FCSTD DOCUMENT  (FreeCAD 0.19R20415 (Git))
Label: Vostok_Amphibia_Bezel
License: All rights reserved
LicenseURL: http://en.wikipedia.org/wiki/All_rights_reserved
objects: Sketcher::SketchObject×46, Part::FeaturePython×33, Part::Extrusion×25, Part::Cut×24, Part::Revolution×19, Part::Part2DObjectPython×9, Part::MultiFuse×7, Part::Fillet×6, Part::Cylinder×3, Part::MultiCommon×2, App::DocumentObjectGroup×2, Part::Offset2D×1, Image::ImagePlane×1, Part::Mirroring×1
note: 176 computed .brp shape members not serialized (recipe doc carries the construction recipe); baked Part::Feature solids carry a one-line shape summary decoded from their .brp

FEATURE [Sketcher::SketchObject] Sketch043
  MapMode = 5
  Placement = pos=(0,0,0) rot=(1,0,0;1.5708rad)
  sketch-geometry (12):
    g0: LineSegment StartX=15.6 StartY=2.6 StartZ=0 EndX=15.6 EndY=3.6 EndZ=0
    g1: LineSegment StartX=15.6 StartY=3.6 StartZ=0 EndX=19 EndY=3 EndZ=0
    g2: LineSegment StartX=19 StartY=3 StartZ=0 EndX=19 EndY=1 EndZ=0
    g3: LineSegment StartX=19 StartY=1 StartZ=0 EndX=17.75 EndY=1 EndZ=0
    g4: LineSegment StartX=17.75 StartY=1 StartZ=0 EndX=17.75 EndY=0 EndZ=0
    g5: LineSegment StartX=17.75 StartY=0 StartZ=0 EndX=16.75 EndY=0 EndZ=0
    g6: LineSegment StartX=16.75 StartY=2.6 StartZ=0 EndX=15.6 EndY=2.6 EndZ=0
    g7: LineSegment StartX=16.75 StartY=0 StartZ=0 EndX=16.75 EndY=0.5 EndZ=0
    g8: LineSegment StartX=16.75 StartY=0.5 StartZ=0 EndX=17.05 EndY=0.5 EndZ=0
    g9: LineSegment StartX=17.05 StartY=0.5 StartZ=0 EndX=17.05 EndY=0.75 EndZ=0
    g10: LineSegment StartX=17.05 StartY=0.75 StartZ=0 EndX=16.75 EndY=0.75 EndZ=0
    g11: LineSegment StartX=16.75 StartY=0.75 StartZ=0 EndX=16.75 EndY=2.6 EndZ=0
  constraints (37):
    c: Vertical(g0)
    c: Coincident(g0,g1)
    c: Coincident(g1,g2)
    c: Coincident(g2,g3)
    c: Coincident(g3,g4)
    c: Vertical(g4)
    c: Coincident(g4,g5)
    c: Horizontal(g6)
    c: Vertical(g2)
    c: Horizontal(g5)
    c: Coincident(g6,g0)
    c: Coincident(g5,g7)
    c: Vertical(g7)
    c: Coincident(g7,g8)
    c: Horizontal(g8)
    c: Coincident(g8,g9)
    c: Coincident(g9,g10)
    c: Coincident(g10,g11)
    c: Coincident(g11,g6)
    c: Vertical(g11)
    c: Vertical(g9)
    c: Horizontal(g10)
    c: Vertical(g10,g7)
    c: PointOnObject(g4,g-1)
    c: DistanceX(g1) = 19
    c: DistanceY(g7,g7) = 0.5
    c: DistanceY(g9,g9) = 0.25
    c: DistanceX(g10,g10) = 0.3
    c: DistanceX(g0) = 15.6
    c: DistanceX(g5,g5) = 1
    c: DistanceX(g10) = 16.75
    c: DistanceY(g0) = 3.6
    c: DistanceY(g0,g0) = 1
    c: DistanceY(g1) = 3
    c: Angle(g0,g1) = 1.39612
    c: DistanceY(g4,g4) = 1
    c: DistanceY(g2,g2) = 2
FEATURE [Part::Revolution] Revolve
  Angle = 15
  Axis = (0,0,1)
  Base = (0,0,0)
  FaceMakerClass = Part::FaceMakerBullseye
  Solid = true
  Source = -> Sketch043
  Symmetric = false
FEATURE [Sketcher::SketchObject] Sketch044
  sketch-geometry (57):
    g0: Circle [constr] CenterX=0 CenterY=0 CenterZ=0 NormalX=0 NormalY=0 NormalZ=1 AngleXU=0 Radius=19
    g1: LineSegment [constr] StartX=0 StartY=0 StartZ=0 EndX=18.9989 EndY=0.207254 EndZ=0
    g2: LineSegment StartX=18.9989 StartY=0.207254 StartZ=0 EndX=18.9497 EndY=0.206718 EndZ=0
    g3: LineSegment StartX=18.9497 StartY=0.206718 StartZ=0 EndX=18.9497 EndY=0 EndZ=0
    g4: LineSegment StartX=18.9497 StartY=0 StartZ=0 EndX=19 EndY=0 EndZ=0
    g5: LineSegment StartX=19 StartY=0 StartZ=0 EndX=19.1989 EndY=0 EndZ=0
    g6: LineSegment StartX=19.1989 StartY=0 StartZ=0 EndX=19.1989 EndY=0.209435 EndZ=0
    g7: LineSegment StartX=19.1989 StartY=0.209435 StartZ=0 EndX=18.9989 EndY=0.207254 EndZ=0
    g8: LineSegment [constr] StartX=18.9497 StartY=0.103359 StartZ=0 EndX=18.9997 EndY=0.103631 EndZ=0
    g9: LineSegment [constr] StartX=0 StartY=0 StartZ=0 EndX=18.9898 EndY=0.621663 EndZ=0
    g10: LineSegment [constr] StartX=0 StartY=0 StartZ=0 EndX=18.9717 EndY=1.03578 EndZ=0
    g11: LineSegment StartX=18.9272 StartY=1.03334 StartZ=0 EndX=18.9407 EndY=0.620054 EndZ=0
    g12: LineSegment StartX=19.1895 StartY=0.632565 StartZ=0 EndX=18.9898 EndY=0.621663 EndZ=0
    g13: LineSegment StartX=18.9898 StartY=0.621663 StartZ=0 EndX=18.9407 EndY=0.620054 EndZ=0
    g14: LineSegment StartX=18.9272 StartY=1.03334 StartZ=0 EndX=18.9717 EndY=1.03578 EndZ=0
    g15: LineSegment StartX=18.9717 StartY=1.03578 StartZ=0 EndX=19.1669 EndY=1.04643 EndZ=0
    g16: LineSegment StartX=19.1669 StartY=1.04643 StartZ=0 EndX=19.1895 EndY=0.632565 EndZ=0
    g17: LineSegment [constr] StartX=0 StartY=0 StartZ=0 EndX=18.3526 EndY=4.91756 EndZ=0
    g18: LineSegment [constr] StartX=0 StartY=0 StartZ=0 EndX=18.4051 EndY=4.71708 EndZ=0
    g19: LineSegment [constr] StartX=18.5037 StartY=4.31445 StartZ=0 EndX=0 EndY=0 EndZ=0
    g20: LineSegment [constr] StartX=0 StartY=0 StartZ=0 EndX=18.5934 EndY=3.90977 EndZ=0
    g21: LineSegment [constr] StartX=0 StartY=0 StartZ=0 EndX=18.9085 EndY=1.86233 EndZ=0
    g22: LineSegment [constr] StartX=0 StartY=0 StartZ=0 EndX=18.9446 EndY=1.4494 EndZ=0
    g23: LineSegment [constr] StartX=0 StartY=0 StartZ=0 EndX=18.6742 EndY=3.50322 EndZ=0
    g24: LineSegment [constr] StartX=18.7462 StartY=3.09501 StartZ=0 EndX=0 EndY=0 EndZ=0
    g25: LineSegment [constr] StartX=18.8093 StartY=2.68533 StartZ=0 EndX=0 EndY=0 EndZ=0
    g26: LineSegment [constr] StartX=18.8634 StartY=2.27437 StartZ=0 EndX=0 EndY=0 EndZ=0
    g27: LineSegment StartX=18.6304 StartY=3.49499 StartZ=0 EndX=18.6977 EndY=3.08701 EndZ=0
    g28: LineSegment StartX=18.9472 StartY=3.13272 StartZ=0 EndX=18.7462 EndY=3.09501 EndZ=0
    g29: LineSegment StartX=18.7462 StartY=3.09501 StartZ=0 EndX=18.6977 EndY=3.08701 EndZ=0
    g30: LineSegment StartX=18.6304 StartY=3.49499 StartZ=0 EndX=18.6742 EndY=3.50322 EndZ=0
    g31: LineSegment StartX=18.6742 StartY=3.50322 StartZ=0 EndX=18.8708 EndY=3.5401 EndZ=0
    g32: LineSegment StartX=18.8708 StartY=3.5401 StartZ=0 EndX=18.9472 EndY=3.13272 EndZ=0
    g33: LineSegment StartX=18.4602 StartY=4.30431 StartZ=0 EndX=18.5453 EndY=3.89965 EndZ=0
    g34: LineSegment StartX=18.7926 StartY=3.95621 StartZ=0 EndX=18.5934 EndY=3.90977 EndZ=0
    g35: LineSegment StartX=18.5934 StartY=3.90977 StartZ=0 EndX=18.5453 EndY=3.89965 EndZ=0
    g36: LineSegment StartX=18.4602 StartY=4.30431 StartZ=0 EndX=18.5037 EndY=4.31445 EndZ=0
    g37: LineSegment StartX=18.5037 StartY=4.31445 StartZ=0 EndX=18.6984 EndY=4.35986 EndZ=0
    g38: LineSegment StartX=18.6984 StartY=4.35986 StartZ=0 EndX=18.7926 EndY=3.95621 EndZ=0
    g39: LineSegment StartX=18.3106 StartY=4.9063 StartZ=0 EndX=18.3619 EndY=4.70599 EndZ=0
    g40: LineSegment StartX=18.5994 StartY=4.76913 StartZ=0 EndX=18.4051 EndY=4.71708 EndZ=0
    g41: LineSegment StartX=18.4051 StartY=4.71708 StartZ=0 EndX=18.3619 EndY=4.70599 EndZ=0
    g42: LineSegment StartX=18.3106 StartY=4.9063 StartZ=0 EndX=18.3526 EndY=4.91756 EndZ=0
    g43: LineSegment StartX=18.3526 StartY=4.91756 StartZ=0 EndX=18.5458 EndY=4.96933 EndZ=0
    g44: LineSegment StartX=18.5458 StartY=4.96933 StartZ=0 EndX=18.5994 EndY=4.76913 EndZ=0
    g45: LineSegment StartX=18.9001 StartY=1.44599 StartZ=0 EndX=18.9446 EndY=1.4494 EndZ=0
    g46: LineSegment StartX=18.9446 StartY=1.4494 StartZ=0 EndX=19.1395 EndY=1.46431 EndZ=0
    g47: LineSegment StartX=19.1395 StartY=1.46431 StartZ=0 EndX=19.0985 EndY=1.88104 EndZ=0
    g48: LineSegment StartX=19.0985 StartY=1.88104 StartZ=0 EndX=18.9085 EndY=1.86233 EndZ=0
    g49: LineSegment StartX=18.9085 StartY=1.86233 StartZ=0 EndX=18.8596 EndY=1.85751 EndZ=0
    g50: LineSegment StartX=18.8596 StartY=1.85751 StartZ=0 EndX=18.9001 EndY=1.44599 EndZ=0
    g51: LineSegment StartX=18.7562 StartY=2.67775 StartZ=0 EndX=18.8093 EndY=2.68533 EndZ=0
    g52: LineSegment StartX=18.8093 StartY=2.68533 StartZ=0 EndX=19.0028 EndY=2.71296 EndZ=0
    g53: LineSegment StartX=19.0028 StartY=2.71296 StartZ=0 EndX=19.0529 EndY=2.29722 EndZ=0
    g54: LineSegment StartX=19.0529 StartY=2.29722 StartZ=0 EndX=18.8634 EndY=2.27437 EndZ=0
    g55: LineSegment StartX=18.8634 StartY=2.27437 StartZ=0 EndX=18.8146 EndY=2.26849 EndZ=0
    g56: LineSegment StartX=18.8146 StartY=2.26849 StartZ=0 EndX=18.7562 EndY=2.67775 EndZ=0
  constraints (158):
    c: Coincident(g0,g-1)
    c: Radius(g0) = 19
    c: Coincident(g1,g-1)
    c: PointOnObject(g1,g0)
    c: Angle(g1) = 0.0109083
    c: Coincident(g1,g2)
    c: Coincident(g2,g3)
    c: PointOnObject(g3,g-1)
    c: Coincident(g3,g4)
    c: PointOnObject(g4,g0)
    c: Coincident(g4,g5)
    c: Coincident(g5,g6)
    c: Coincident(g6,g7)
    c: Coincident(g7,g2)
    c: PointOnObject(g2,g1)
    c: Parallel(g2,g7)
    c: Distance(g2,g6) = 0.2
    c: PointOnObject(g4,g-1)
    c: Parallel(g4,g5)
    c: Perpendicular(g6,g5)
    c: Perpendicular(g3,g4)
    c: PointOnObject(g8,g0)
    c: Perpendicular(g0,g8)
    c: Symmetric(g2,g3,g8)
    c: Distance(g8) = 0.05
    c: Coincident(g9,g-1)
    c: PointOnObject(g9,g0)
    c: Coincident(g10,g-1)
    c: PointOnObject(g10,g0)
    c: Angle(g1,g9) = 0.0218166
    c: Angle(g9,g10) = 0.0218166
    c: PointOnObject(g11,g10)
    c: PointOnObject(g11,g9)
    c: Coincident(g12,g13)
    c: Coincident(g13,g11)
    c: Coincident(g11,g14)
    c: Coincident(g14,g15)
    c: Coincident(g15,g16)
    c: Coincident(g16,g12)
    c: Coincident(g10,g14)
    c: Coincident(g12,g9)
    c: Perpendicular(g16,g12)
    c: Perpendicular(g16,g15)
    c: Parallel(g14,g15)
    c: Equal(g12,g7)
    c: Perpendicular(g13,g11)
    c: Equal(g13,g2)
    c: Coincident(g17,g-1)
    c: PointOnObject(g17,g0)
    c: Coincident(g18,g-1)
    c: PointOnObject(g18,g0)
    c: PointOnObject(g19,g0)
    c: Coincident(g19,g-1)
    c: Coincident(g20,g-1)
    c: PointOnObject(g20,g0)
    c: Coincident(g21,g-1)
    c: PointOnObject(g21,g0)
    c: Coincident(g22,g-1)
    c: PointOnObject(g22,g0)
    c: Angle(g10,g22) = 0.0218166
    c: Angle(g22,g21) = 0.0218166
    c: Angle(g18,g17) = 0.0109083
    c: Angle(g19,g18) = 0.0218166
    c: Angle(g20,g19) = 0.0218166
    c: Coincident(g23,g-1)
    c: PointOnObject(g23,g0)
    c: PointOnObject(g24,g0)
    c: Coincident(g24,g-1)
    c: PointOnObject(g25,g0)
    c: Coincident(g25,g-1)
    c: Angle(g23,g20) = 0.0218166
    c: Angle(g24,g23) = 0.0218166
    c: Angle(g25,g24) = 0.0218166
    c: PointOnObject(g26,g0)
    c: Coincident(g26,g-1)
    c: Angle(g26,g25) = 0.0218166
    c: Coincident(g28,g29)
    c: Coincident(g29,g27)
    c: Coincident(g27,g30)
    c: Coincident(g30,g31)
    c: Coincident(g31,g32)
    c: Coincident(g32,g28)
    c: Perpendicular(g32,g28)
    c: Perpendicular(g32,g31)
    c: Parallel(g30,g31)
    c: Perpendicular(g29,g27)
    c: Coincident(g34,g35)
    c: Coincident(g35,g33)
    c: Coincident(g33,g36)
    c: Coincident(g36,g37)
    c: Coincident(g37,g38)
    c: Coincident(g38,g34)
    c: Perpendicular(g38,g34)
    c: Perpendicular(g38,g37)
    c: Parallel(g36,g37)
    c: Perpendicular(g35,g33)
    c: Coincident(g40,g41)
    c: Coincident(g41,g39)
    c: Coincident(g39,g42)
    c: Coincident(g42,g43)
    c: Coincident(g43,g44)
    c: Coincident(g44,g40)
    c: Perpendicular(g44,g40)
    c: Perpendicular(g44,g43)
    c: Parallel(g42,g43)
    c: Perpendicular(g41,g39)
    c: Angle(g21,g26) = 0.0218166
    c: Coincident(g30,g23)
    c: Coincident(g28,g24)
    c: PointOnObject(g27,g24)
    c: PointOnObject(g27,g23)
    c: PointOnObject(g33,g20)
    c: Coincident(g36,g19)
    c: Coincident(g34,g20)
    c: Equal(g37,g31)
    c: PointOnObject(g33,g19)
    c: Coincident(g42,g17)
    c: Coincident(g18,g40)
    c: PointOnObject(g39,g18)
    c: Equal(g43,g37)
    c: Equal(g36,g41)
    c: PointOnObject(g39,g17)
    c: Equal(g30,g14)
    c: Equal(g37,g31)
    c: Equal(g36,g30)
    c: Equal(g37,g7)
    c: PointOnObject(g45,g22)
    c: Coincident(g45,g22)
    c: Coincident(g45,g46)
    c: Coincident(g46,g47)
    c: Coincident(g47,g48)
    c: Coincident(g48,g21)
    c: Coincident(g48,g49)
    c: PointOnObject(g49,g21)
    c: Coincident(g49,g50)
    c: Coincident(g50,g45)
    c: Equal(g45,g14)
    c: Equal(g46,g15)
    c: Perpendicular(g49,g50)
    c: Parallel(g46,g45)
    c: Parallel(g48,g49)
    c: Perpendicular(g47,g48)
    c: PointOnObject(g51,g25)
    c: Coincident(g51,g25)
    c: Coincident(g51,g52)
    c: Coincident(g52,g53)
    c: Coincident(g53,g54)
    c: Coincident(g54,g26)
    c: Coincident(g54,g55)
    c: PointOnObject(g55,g26)
    c: Coincident(g55,g56)
    c: Coincident(g56,g51)
    c: Equal(g55,g49)
    c: Equal(g48,g54)
    c: Parallel(g51,g52)
    c: Parallel(g55,g54)
    c: Perpendicular(g53,g54)
    c: Perpendicular(g56,g51)
FEATURE [Sketcher::SketchObject] Sketch
  ExternalGeometry = -> [Revolve]
  MapMode = 6
  Placement = pos=(15.6,8e-16,3.6) rot=(0.086895,0.086895,0.992421;1.57841rad)
  Support = -> [Revolve]
  sketch-geometry (2):
    g0: Circle CenterX=-6e-16 CenterY=-1.72627 CenterZ=0 NormalX=0 NormalY=0 NormalZ=1 AngleXU=0 Radius=0.75
    g1: LineSegment [constr] StartX=0 StartY=0 StartZ=0 EndX=-1.3e-15 EndY=-3.45254 EndZ=0
  constraints (4):
    c: Coincident(g1,g-1)
    c: Coincident(g1,g-3)
    c: Symmetric(g1,g1,g0)
    c: Diameter(g0) = 1.5
FEATURE [Part::Offset2D] Offset2D
  Fill = true
  Intersection = false
  Join = 0
  Mode = 1
  SelfIntersection = false
  Source = -> Sketch
  Value = 0.5
FEATURE [Sketcher::SketchObject] Sketch045
  ExternalGeometry = -> [Sketch043]
  MapMode = 6
  Placement = pos=(15.0684,4.03758,3.6) rot=(0.066781,0.08703,0.993965;1.83844rad)
  Support = -> [Revolve]
  sketch-geometry (8):
    g0: Circle [constr] CenterX=-2.328e-13 CenterY=15.841 CenterZ=0 NormalX=0 NormalY=0 NormalZ=1 AngleXU=0 Radius=17.567
    g1: GeomPoint X=-4.47757 Y=-1.14575 Z=0
    g2: ArcOfCircle CenterX=-2.328e-13 CenterY=15.841 CenterZ=0 NormalX=0 NormalY=0 NormalZ=1 AngleXU=0 Radius=17.367 StartAngle=4.55967 EndAngle=4.86511
    g3: ArcOfCircle CenterX=-2.328e-13 CenterY=15.841 CenterZ=0 NormalX=0 NormalY=0 NormalZ=1 AngleXU=0 Radius=17.767 StartAngle=4.55967 EndAngle=4.86511
    g4: ArcOfCircle CenterX=2.67235 CenterY=-1.52152 CenterZ=0 NormalX=0 NormalY=0 NormalZ=1 AngleXU=0 Radius=0.2 StartAngle=4.86511 EndAngle=8.0067
    g5: ArcOfCircle CenterX=-2.67235 CenterY=-1.52152 CenterZ=0 NormalX=0 NormalY=0 NormalZ=1 AngleXU=0 Radius=0.2 StartAngle=1.41808 EndAngle=4.55967
    g6: LineSegment [constr] StartX=2.67235 StartY=-1.52152 StartZ=0 EndX=-2.327e-13 EndY=15.841 EndZ=0
    g7: LineSegment [constr] StartX=-2.328e-13 StartY=15.841 StartZ=0 EndX=-2.67235 EndY=-1.52152 EndZ=0
  constraints (17):
    c: Symmetric(g-3,g-3,g1)
    c: PointOnObject(g1,g0)
    c: PointOnObject(g0,g-3)
    c: PointOnObject(g4,g0)
    c: Tangent(g4,g2) = 1.5708
    c: Tangent(g4,g3) = -1.5708
    c: Tangent(g5,g3) = -1.5708
    c: Tangent(g5,g2) = 1.5708
    c: Radius(g4) = 0.2
    c: Symmetric(g5,g4,g-2)
    c: Coincident(g6,g4)
    c: Coincident(g6,g0)
    c: Coincident(g7,g6)
    c: Coincident(g7,g5)
    c: Angle(g7,g6) = 0.305433
    c: Coincident(g3,g2)
    c: Coincident(g2,g0)
FEATURE [Part::Extrusion] Extrude002
  Base = -> Sketch045
  Dir = (0.167864,0.044979,0.984784)
  DirMode = 2
  FaceMakerClass = Part::FaceMakerBullseye
  LengthFwd = 0.15
  LengthRev = 0
  Reversed = true
  Solid = true
  Symmetric = false
FEATURE [Part::Extrusion] Extrude003
  Base = -> Offset2D
  Dir = (0.173785,3e-16,0.984784)
  DirMode = 2
  FaceMakerClass = Part::FaceMakerBullseye
  LengthFwd = 0.15
  LengthRev = 0
  Reversed = true
  Solid = false
  Symmetric = false
FEATURE [Part::Extrusion] Extrude001
  Base = -> Sketch
  Dir = (0.173785,1e-16,0.984784)
  DirMode = 2
  FaceMakerClass = Part::FaceMakerBullseye
  LengthFwd = 0.15
  LengthRev = 0
  Reversed = true
  Solid = true
  Symmetric = false
FEATURE [Sketcher::SketchObject] Sketch046
  MapMode = 5
  Placement = pos=(0,0,0) rot=(1,0,0;1.5708rad)
  sketch-geometry (14):
    g0: LineSegment StartX=15.6 StartY=3.05 StartZ=0 EndX=15.6 EndY=3.95 EndZ=0
    g1: LineSegment StartX=19.5 StartY=3.56699 StartZ=0 EndX=19.5 EndY=1.90849 EndZ=0
    g2: LineSegment StartX=19.5 StartY=1.90849 StartZ=0 EndX=17.75 EndY=1.65849 EndZ=0
    g3: LineSegment StartX=17.75 StartY=1.65849 StartZ=0 EndX=17.75 EndY=0 EndZ=0
    g4: LineSegment StartX=17.75 StartY=0 StartZ=0 EndX=16.75 EndY=0 EndZ=0
    g5: LineSegment StartX=16.75 StartY=3.05 StartZ=0 EndX=15.6 EndY=3.05 EndZ=0
    g6: LineSegment StartX=16.75 StartY=0 StartZ=0 EndX=16.75 EndY=0.5 EndZ=0
    g7: LineSegment StartX=16.75 StartY=0.5 StartZ=0 EndX=17.05 EndY=0.5 EndZ=0
    g8: LineSegment StartX=17.05 StartY=0.5 StartZ=0 EndX=17.05 EndY=0.75 EndZ=0
    g9: LineSegment StartX=17.05 StartY=0.75 StartZ=0 EndX=16.75 EndY=0.75 EndZ=0
    g10: LineSegment StartX=16.75 StartY=0.75 StartZ=0 EndX=16.75 EndY=3.05 EndZ=0
    g11: LineSegment StartX=18.75 StartY=4 StartZ=0 EndX=19.5 EndY=3.56699 EndZ=0
    g12: LineSegment StartX=18.75 StartY=4 StartZ=0 EndX=18.75 EndY=3.95 EndZ=0
    g13: LineSegment StartX=18.75 StartY=3.95 StartZ=0 EndX=15.6 EndY=3.95 EndZ=0
  constraints (42):
    c: Vertical(g0)
    c: Coincident(g1,g2)
    c: Coincident(g2,g3)
    c: Vertical(g3)
    c: Coincident(g3,g4)
    c: Horizontal(g5)
    c: Vertical(g1)
    c: Horizontal(g4)
    c: Coincident(g5,g0)
    c: Coincident(g4,g6)
    c: Vertical(g6)
    c: Coincident(g6,g7)
    c: Horizontal(g7)
    c: Coincident(g7,g8)
    c: Coincident(g8,g9)
    c: Coincident(g9,g10)
    c: Coincident(g10,g5)
    c: Vertical(g10)
    c: Vertical(g8)
    c: Horizontal(g9)
    c: Vertical(g9,g6)
    c: PointOnObject(g3,g-1)
    c: DistanceX(g1) = 19.5
    c: DistanceY(g2,g1) = 0.25
    c: DistanceY(g6,g6) = 0.5
    c: DistanceY(g8,g8) = 0.25
    c: DistanceX(g9,g9) = 0.3
    c: DistanceX(g0) = 15.6
    c: DistanceX(g4,g4) = 1
    c: DistanceX(g9) = 16.75
    c: DistanceY(g0,g0) = 0.9
    c: Coincident(g11,g1)
    c: DistanceY(g11) = 4
    c: Coincident(g11,g12)
    c: Vertical(g12)
    c: Coincident(g12,g13)
    c: Horizontal(g13)
    c: DistanceY(g12,g12) = 0.05
    c: Coincident(g0,g13)
    c: Angle(g12,g11) = 1.0472
    c: DistanceX(g11,g1) = 0.75
    c: Equal(g1,g3)
FEATURE [Part::Revolution] Revolve001
  Angle = 15
  Axis = (0,0,1)
  Base = (0,0,0)
  FaceMakerClass = Part::FaceMakerBullseye
  Solid = true
  Source = -> Sketch046
  Symmetric = false
FEATURE [Sketcher::SketchObject] Sketch047
  sketch-geometry (8):
    g0: GeomPoint X=19.5 Y=0 Z=0
    g1: ArcOfCircle CenterX=19.5 CenterY=0.4 CenterZ=0 NormalX=0 NormalY=0 NormalZ=1 AngleXU=0 Radius=0.4 StartAngle=1.61182 EndAngle=4.71239
    g2: Circle [constr] CenterX=0 CenterY=0 CenterZ=0 NormalX=0 NormalY=0 NormalZ=1 AngleXU=0 Radius=19.5
    g3: LineSegment StartX=19.5463 StartY=1.02438 StartZ=0 EndX=19.6 EndY=0 EndZ=0
    g4: LineSegment StartX=19.5 StartY=0 StartZ=0 EndX=19.6 EndY=0 EndZ=0
    g5: ArcOfCircle CenterX=-4.84e-14 CenterY=9.927e-13 CenterZ=0 NormalX=0 NormalY=0 NormalZ=1 AngleXU=0 Radius=19.5 StartAngle=0.0410199 EndAngle=0.0523599
    g6: LineSegment StartX=19.5463 StartY=1.02438 StartZ=0 EndX=19.4733 EndY=1.02055 EndZ=0
    g7: LineSegment [constr] StartX=19.4733 StartY=1.02055 StartZ=0 EndX=0 EndY=0 EndZ=0
  constraints (22):
    c: PointOnObject(g0,g-1)
    c: DistanceX(g0) = 19.5
    c: PointOnObject(g0,g2)
    c: PointOnObject(g1,g2)
    c: Coincident(g1,g0)
    c: Coincident(g4,g0)
    c: Coincident(g4,g3)
    c: Coincident(g-1,g2)
    c: Horizontal(g4)
    c: DistanceX(g4,g4) = 0.1
    c: Coincident(g5,g1)
    c: Coincident(g6,g3)
    c: Coincident(g6,g5)
    c: Coincident(g7,g5)
    c: Coincident(g7,g-1)
    c: PointOnObject(g5,g2)
    c: Equal(g5,g2)
    c: Parallel(g6,g7)
    c: Perpendicular(g3,g6)
    c: Angle(g-1,g7) = 0.0523599
    c: Tangent(g1,g-1)
    c: Radius(g1) = 0.4
FEATURE [Part::FeaturePython] Array003  # Draft array (typed FeaturePython)
  Angle = 12
  ArrayType = 1
  Axis = (0,0,1)
  Base = -> Sketch047
  Center = (0,0,0)
  Fuse = false
  IntervalAxis = (0,0,0)
  IntervalX = (1,0,0)
  IntervalY = (0,1,0)
  IntervalZ = (0,0,1)
  NumberPolar = 5
  NumberX = 2
  NumberY = 2
  NumberZ = 1
FEATURE [Part::Extrusion] Extrude006
  Base = -> Array003
  Dir = (0,0,1)
  DirMode = 2
  FaceMakerClass = Part::FaceMakerBullseye
  LengthFwd = 4
  LengthRev = 0
  Solid = true
  Symmetric = false
FEATURE [Part::Cut] Cut002
  Base = -> Revolve001
  Tool = -> Extrude006
FEATURE [Part::FeaturePython] Array004  label="Bezel_2_Rally"  # Draft array (typed FeaturePython)
  Angle = 360
  ArrayType = 1
  Axis = (0,0,1)
  Base = -> Cut002
  Center = (0,0,0)
  Fuse = true
  IntervalAxis = (0,0,0)
  IntervalX = (1,0,0)
  IntervalY = (0,1,0)
  IntervalZ = (0,0,1)
  NumberCircles = 2
  NumberPolar = 24
  NumberX = 1
  NumberY = 1
  NumberZ = 1
  RadialDistance = 1
  Symmetry = 1
  TangentialDistance = 1
FEATURE [Sketcher::SketchObject] Sketch048
  sketch-geometry (8):
    g0: Circle [constr] CenterX=0 CenterY=0 CenterZ=0 NormalX=0 NormalY=0 NormalZ=1 AngleXU=0 Radius=19.5
    g1: LineSegment [constr] StartX=0 StartY=0 StartZ=0 EndX=19.3332 EndY=2.54526 EndZ=0
    g2: LineSegment [constr] StartX=0 StartY=0 StartZ=0 EndX=18.8356 EndY=5.04697 EndZ=0
    g3: ArcOfCircle CenterX=19.4755 CenterY=2.564 CenterZ=0 NormalX=0 NormalY=0 NormalZ=1 AngleXU=0 Radius=0.643603 StartAngle=1.94271 EndAngle=4.60227
    g4: GeomPoint X=18.8375 Y=2.48 Z=0
    g5: LineSegment StartX=19.3995 StartY=3.18955 StartZ=0 EndX=19.6022 EndY=1.95675 EndZ=0
    g6: LineSegment StartX=19.6022 StartY=1.95675 StartZ=0 EndX=19.4048 EndY=1.9243 EndZ=0
    g7: LineSegment StartX=19.3995 StartY=3.18955 StartZ=0 EndX=19.2417 EndY=3.16361 EndZ=0
  constraints (23):
    c: Angle(g2) = 0.261799
    c: Angle(g1) = 0.1309
    c: Coincident(g1,g-1)
    c: PointOnObject(g1,g0)
    c: PointOnObject(g2,g0)
    c: Radius(g0) = 19.5
    c: Coincident(g2,g-1)
    c: Coincident(g2,g0)
    c: PointOnObject(g3,g0)
    c: PointOnObject(g3,g0)
    c: PointOnObject(g4,g1)
    c: PointOnObject(g4,g3)
    c: Distance(g4,g1) = 0.5
    c: Coincident(g5,g6)
    c: Coincident(g6,g3)
    c: Coincident(g5,g7)
    c: Coincident(g7,g3)
    c: Perpendicular(g5,g7)
    c: Perpendicular(g0,g7)
    c: Perpendicular(g5,g6)
    c: Distance(g6) = 0.2
    c: Distance(g3,g3) = 1.25
    c: PointOnObject(g3,g1)
FEATURE [Part::FeaturePython] Array005  # Draft array (typed FeaturePython)
  Angle = 15
  ArrayType = 1
  Axis = (0,0,1)
  Base = -> Sketch048
  Center = (0,0,0)
  Fuse = false
  IntervalAxis = (0,0,0)
  IntervalX = (1,0,0)
  IntervalY = (0,1,0)
  IntervalZ = (0,0,1)
  NumberPolar = 2
  NumberX = 2
  NumberY = 2
  NumberZ = 1
FEATURE [Part::Extrusion] Extrude007
  Base = -> Array005
  Dir = (0,0,1)
  DirMode = 2
  FaceMakerClass = Part::FaceMakerBullseye
  LengthFwd = 4
  LengthRev = 0
  Solid = true
  Symmetric = false
FEATURE [Sketcher::SketchObject] Sketch049
  MapMode = 5
  Placement = pos=(0,0,0) rot=(1,0,0;1.5708rad)
  sketch-geometry (12):
    g0: LineSegment StartX=15.6 StartY=2.8 StartZ=0 EndX=15.6 EndY=3.7 EndZ=0
    g1: LineSegment StartX=19.5 StartY=2.5 StartZ=0 EndX=19.5 EndY=0 EndZ=0
    g2: LineSegment StartX=19.5 StartY=0 StartZ=0 EndX=16.75 EndY=0 EndZ=0
    g3: LineSegment StartX=16.75 StartY=2.8 StartZ=0 EndX=15.6 EndY=2.8 EndZ=0
    g4: LineSegment StartX=16.75 StartY=0 StartZ=0 EndX=16.75 EndY=0.5 EndZ=0
    g5: LineSegment StartX=16.75 StartY=0.5 StartZ=0 EndX=17.05 EndY=0.5 EndZ=0
    g6: LineSegment StartX=17.05 StartY=0.5 StartZ=0 EndX=17.05 EndY=0.75 EndZ=0
    g7: LineSegment StartX=17.05 StartY=0.75 StartZ=0 EndX=16.75 EndY=0.75 EndZ=0
    g8: LineSegment StartX=16.75 StartY=0.75 StartZ=0 EndX=16.75 EndY=2.8 EndZ=0
    g9: LineSegment StartX=18.75 StartY=2.77298 StartZ=0 EndX=19.5 EndY=2.5 EndZ=0
    g10: LineSegment StartX=18.75 StartY=2.77298 StartZ=0 EndX=18.75 EndY=2.72298 EndZ=0
    g11: LineSegment StartX=18.75 StartY=2.72298 StartZ=0 EndX=15.6 EndY=3.7 EndZ=0
  constraints (37):
    c: Vertical(g0)
    c: Horizontal(g3)
    c: Vertical(g1)
    c: Horizontal(g2)
    c: Coincident(g3,g0)
    c: Coincident(g2,g4)
    c: Vertical(g4)
    c: Coincident(g4,g5)
    c: Horizontal(g5)
    c: Coincident(g5,g6)
    c: Coincident(g6,g7)
    c: Coincident(g7,g8)
    c: Coincident(g8,g3)
    c: Vertical(g8)
    c: Vertical(g6)
    c: Horizontal(g7)
    c: Vertical(g7,g4)
    c: PointOnObject(g2,g-1)
    c: DistanceX(g1) = 19.5
    c: DistanceY(g4,g4) = 0.5
    c: DistanceY(g6,g6) = 0.25
    c: DistanceX(g7,g7) = 0.3
    c: DistanceX(g0) = 15.6
    c: DistanceX(g7) = 16.75
    c: DistanceY(g0,g0) = 0.9
    c: Coincident(g9,g1)
    c: Coincident(g9,g10)
    c: Vertical(g10)
    c: Coincident(g10,g11)
    c: DistanceY(g10,g10) = 0.05
    c: Coincident(g0,g11)
    c: Angle(g10,g9) = 1.22173
    c: DistanceX(g9,g1) = 0.75
    c: DistanceY(g0) = 3.7
    c: Coincident(g2,g1)
    c: DistanceY(g1,g1) = 2.5
    c: Angle(g0,g11) = 1.27004
FEATURE [Part::Revolution] Revolve002
  Angle = 15
  Axis = (0,0,1)
  Base = (0,0,0)
  FaceMakerClass = Part::FaceMakerBullseye
  Solid = true
  Source = -> Sketch049
  Symmetric = false
FEATURE [Part::Cut] Cut003
  Base = -> Revolve002
  Tool = -> Extrude007
FEATURE [Part::FeaturePython] Array006  label="Bezel_3"  # Draft array (typed FeaturePython)
  Angle = 360
  ArrayType = 1
  Axis = (0,0,1)
  Base = -> Cut003
  Center = (0,0,0)
  Fuse = true
  IntervalAxis = (0,0,0)
  IntervalX = (1,0,0)
  IntervalY = (0,1,0)
  IntervalZ = (0,0,1)
  NumberCircles = 2
  NumberPolar = 24
  NumberX = 1
  NumberY = 1
  NumberZ = 1
  RadialDistance = 1
  Symmetry = 1
  TangentialDistance = 1
FEATURE [Sketcher::SketchObject] Sketch051
  MapMode = 5
  Placement = pos=(0,0,0) rot=(1,0,0;1.5708rad)
  sketch-geometry (11):
    g0: LineSegment StartX=15.6 StartY=3.3 StartZ=0 EndX=15.6 EndY=4.2 EndZ=0
    g1: LineSegment StartX=19.5 StartY=0 StartZ=0 EndX=16.75 EndY=0 EndZ=0
    g2: LineSegment StartX=16.75 StartY=3.3 StartZ=0 EndX=15.6 EndY=3.3 EndZ=0
    g3: LineSegment StartX=16.75 StartY=0 StartZ=0 EndX=16.75 EndY=0.5 EndZ=0
    g4: LineSegment StartX=16.75 StartY=0.5 StartZ=0 EndX=17.05 EndY=0.5 EndZ=0
    g5: LineSegment StartX=17.05 StartY=0.5 StartZ=0 EndX=17.05 EndY=0.75 EndZ=0
    g6: LineSegment StartX=17.05 StartY=0.75 StartZ=0 EndX=16.75 EndY=0.75 EndZ=0
    g7: LineSegment StartX=16.75 StartY=0.75 StartZ=0 EndX=16.75 EndY=3.3 EndZ=0
    g8: LineSegment StartX=15.6 StartY=4.2 StartZ=0 EndX=17.6 EndY=4.2 EndZ=0
    g9: LineSegment StartX=19.5 StartY=0 StartZ=0 EndX=19.5 EndY=2 EndZ=0
    g10: LineSegment StartX=19.5 StartY=2 StartZ=0 EndX=17.6 EndY=4.2 EndZ=0
  constraints (33):
    c: Vertical(g0)
    c: Horizontal(g2)
    c: Horizontal(g1)
    c: Coincident(g2,g0)
    c: Coincident(g1,g3)
    c: Vertical(g3)
    c: Coincident(g3,g4)
    c: Horizontal(g4)
    c: Coincident(g4,g5)
    c: Coincident(g5,g6)
    c: Coincident(g6,g7)
    c: Coincident(g7,g2)
    c: Vertical(g7)
    c: Vertical(g5)
    c: Horizontal(g6)
    c: Vertical(g6,g3)
    c: PointOnObject(g1,g-1)
    c: DistanceY(g3,g3) = 0.5
    c: DistanceY(g5,g5) = 0.25
    c: DistanceX(g6,g6) = 0.3
    c: DistanceX(g0) = 15.6
    c: DistanceX(g6) = 16.75
    c: DistanceY(g0,g0) = 0.9
    c: DistanceY(g0) = 4.2
    c: DistanceX(g1) = 19.5
    c: Coincident(g0,g8)
    c: Horizontal(g8)
    c: DistanceX(g8,g8) = 2
    c: Coincident(g1,g9)
    c: Vertical(g9)
    c: Coincident(g9,g10)
    c: Coincident(g10,g8)
    c: Equal(g9,g8)
FEATURE [Part::Revolution] Revolve003  label="Bezel_Smooth_04"
  Angle = 360
  Axis = (0,0,1)
  Base = (0,0,0)
  FaceMakerClass = Part::FaceMakerBullseye
  Solid = true
  Source = -> Sketch051
  Symmetric = false
FEATURE [Sketcher::SketchObject] Sketch052
  MapMode = 5
  Placement = pos=(0,0,0) rot=(1,0,0;1.5708rad)
  sketch-geometry (11):
    g0: LineSegment StartX=15.6 StartY=2.7 StartZ=0 EndX=15.6 EndY=4.2 EndZ=0
    g1: LineSegment StartX=19 StartY=0 StartZ=0 EndX=16.75 EndY=0 EndZ=0
    g2: LineSegment StartX=16.75 StartY=2.7 StartZ=0 EndX=15.6 EndY=2.7 EndZ=0
    g3: LineSegment StartX=16.75 StartY=0 StartZ=0 EndX=16.75 EndY=0.5 EndZ=0
    g4: LineSegment StartX=16.75 StartY=0.5 StartZ=0 EndX=17.05 EndY=0.5 EndZ=0
    g5: LineSegment StartX=17.05 StartY=0.5 StartZ=0 EndX=17.05 EndY=0.75 EndZ=0
    g6: LineSegment StartX=17.05 StartY=0.75 StartZ=0 EndX=16.75 EndY=0.75 EndZ=0
    g7: LineSegment StartX=16.75 StartY=0.75 StartZ=0 EndX=16.75 EndY=2.7 EndZ=0
    g8: LineSegment StartX=15.6 StartY=4.2 StartZ=0 EndX=16.1 EndY=4.2 EndZ=0
    g9: LineSegment StartX=19 StartY=0 StartZ=0 EndX=19 EndY=0.5 EndZ=0
    g10: LineSegment StartX=16.1 StartY=4.2 StartZ=0 EndX=19 EndY=0.5 EndZ=0
  constraints (33):
    c: Vertical(g0)
    c: Horizontal(g2)
    c: Horizontal(g1)
    c: Coincident(g2,g0)
    c: Coincident(g1,g3)
    c: Vertical(g3)
    c: Coincident(g3,g4)
    c: Horizontal(g4)
    c: Coincident(g4,g5)
    c: Coincident(g5,g6)
    c: Coincident(g6,g7)
    c: Coincident(g7,g2)
    c: Vertical(g7)
    c: Vertical(g5)
    c: Horizontal(g6)
    c: Vertical(g6,g3)
    c: PointOnObject(g1,g-1)
    c: DistanceY(g3,g3) = 0.5
    c: DistanceY(g5,g5) = 0.25
    c: DistanceX(g6,g6) = 0.3
    c: DistanceX(g0) = 15.6
    c: DistanceX(g6) = 16.75
    c: DistanceY(g0,g0) = 1.5
    c: DistanceX(g1) = 19
    c: Coincident(g0,g8)
    c: Horizontal(g8)
    c: DistanceX(g8,g8) = 0.5
    c: Coincident(g1,g9)
    c: Vertical(g9)
    c: DistanceY(g0) = 4.2
    c: Coincident(g8,g10)
    c: Coincident(g9,g10)
    c: DistanceY(g9,g9) = 0.5
FEATURE [Part::Revolution] Revolve004  label="Bezel_Smooth_05"
  Angle = 360
  Axis = (0,0,1)
  Base = (0,0,0)
  FaceMakerClass = Part::FaceMakerBullseye
  Solid = true
  Source = -> Sketch052
  Symmetric = false
FEATURE [Sketcher::SketchObject] Sketch053
  MapMode = 5
  Placement = pos=(0,0,0) rot=(1,0,0;1.5708rad)
  sketch-geometry (10):
    g0: LineSegment StartX=15.6 StartY=3.3 StartZ=0 EndX=15.6 EndY=4.2 EndZ=0
    g1: LineSegment StartX=19.5 StartY=0 StartZ=0 EndX=16.75 EndY=0 EndZ=0
    g2: LineSegment StartX=16.75 StartY=3.3 StartZ=0 EndX=15.6 EndY=3.3 EndZ=0
    g3: LineSegment StartX=16.75 StartY=0 StartZ=0 EndX=16.75 EndY=0.5 EndZ=0
    g4: LineSegment StartX=16.75 StartY=0.5 StartZ=0 EndX=17.05 EndY=0.5 EndZ=0
    g5: LineSegment StartX=17.05 StartY=0.5 StartZ=0 EndX=17.05 EndY=0.75 EndZ=0
    g6: LineSegment StartX=17.05 StartY=0.75 StartZ=0 EndX=16.75 EndY=0.75 EndZ=0
    g7: LineSegment StartX=16.75 StartY=0.75 StartZ=0 EndX=16.75 EndY=3.3 EndZ=0
    g8: LineSegment StartX=15.6 StartY=4.2 StartZ=0 EndX=19.5 EndY=4.2 EndZ=0
    g9: LineSegment StartX=19.5 StartY=0 StartZ=0 EndX=19.5 EndY=4.2 EndZ=0
  constraints (30):
    c: Vertical(g0)
    c: Horizontal(g2)
    c: Horizontal(g1)
    c: Coincident(g2,g0)
    c: Coincident(g1,g3)
    c: Vertical(g3)
    c: Coincident(g3,g4)
    c: Horizontal(g4)
    c: Coincident(g4,g5)
    c: Coincident(g5,g6)
    c: Coincident(g6,g7)
    c: Coincident(g7,g2)
    c: Vertical(g7)
    c: Vertical(g5)
    c: Horizontal(g6)
    c: Vertical(g6,g3)
    c: PointOnObject(g1,g-1)
    c: DistanceY(g3,g3) = 0.5
    c: DistanceY(g5,g5) = 0.25
    c: DistanceX(g6,g6) = 0.3
    c: DistanceX(g0) = 15.6
    c: DistanceX(g6) = 16.75
    c: DistanceY(g0,g0) = 0.9
    c: DistanceX(g1) = 19.5
    c: Coincident(g0,g8)
    c: Horizontal(g8)
    c: Coincident(g1,g9)
    c: Vertical(g9)
    c: DistanceY(g0) = 4.2
    c: Coincident(g8,g9)
FEATURE [Part::Revolution] Revolve005  label="Bezel_Smooth_06"
  Angle = 360
  Axis = (0,0,1)
  Base = (0,0,0)
  FaceMakerClass = Part::FaceMakerBullseye
  Solid = true
  Source = -> Sketch053
  Symmetric = false
FEATURE [Part::Fillet] Fillet  label="Bez6"
  Base = -> Revolve005
  Edges = 2 edges: [Edge12 r=0.2,Edge14 r=0.1]
FEATURE [Part::Fillet] Fillet001  label="Bez5"
  Base = -> Revolve004
  Edges = 1 edges r=0.2: [Edge12]
FEATURE [Part::Fillet] Fillet002  label="Bez4"
  Base = -> Revolve003
  Edges = 3 edges: [Edge12 r=0.2,Edge14 r=0.1,Edge15 r=0.1]
FEATURE [Sketcher::SketchObject] Sketch054
  MapMode = 5
  Placement = pos=(0,0,0) rot=(1,0,0;1.5708rad)
  sketch-geometry (17):
    g0: LineSegment StartX=15.6 StartY=3.3 StartZ=0 EndX=15.6 EndY=4.3 EndZ=0
    g1: LineSegment StartX=19.5 StartY=2.5 StartZ=0 EndX=19.5 EndY=0 EndZ=0
    g2: LineSegment StartX=19.5 StartY=0 StartZ=0 EndX=16.75 EndY=0 EndZ=0
    g3: LineSegment StartX=16.75 StartY=3.3 StartZ=0 EndX=15.6 EndY=3.3 EndZ=0
    g4: LineSegment StartX=16.75 StartY=0 StartZ=0 EndX=16.75 EndY=0.5 EndZ=0
    g5: LineSegment StartX=16.75 StartY=0.5 StartZ=0 EndX=17.05 EndY=0.5 EndZ=0
    g6: LineSegment StartX=17.05 StartY=0.5 StartZ=0 EndX=17.05 EndY=0.75 EndZ=0
    g7: LineSegment StartX=17.05 StartY=0.75 StartZ=0 EndX=16.75 EndY=0.75 EndZ=0
    g8: LineSegment StartX=16.75 StartY=0.75 StartZ=0 EndX=16.75 EndY=3.3 EndZ=0
    g9: LineSegment StartX=16.1 StartY=4.3 StartZ=0 EndX=19.5 EndY=2.5 EndZ=0
    g10: LineSegment StartX=0 StartY=5.75 StartZ=0 EndX=11.5 EndY=5.75 EndZ=0
    g11: ArcOfCircle CenterX=11.5 CenterY=0.75 CenterZ=0 NormalX=0 NormalY=0 NormalZ=1 AngleXU=0 Radius=5 StartAngle=1.16096 EndAngle=1.5708
    g12: ArcOfCircle CenterX=12.5 CenterY=3.75 CenterZ=0 NormalX=0 NormalY=0 NormalZ=1 AngleXU=0 Radius=3 StartAngle=0.764925 EndAngle=1.5708
    g13: LineSegment StartX=12.5 StartY=6.75 StartZ=0 EndX=0 EndY=6.75 EndZ=0
    g14: LineSegment StartX=0 StartY=6.75 StartZ=0 EndX=0 EndY=5.75 EndZ=0
    g15: ArcOfCircle CenterX=3.53086 CenterY=-17.5937 CenterZ=0 NormalX=0 NormalY=0 NormalZ=1 AngleXU=0 Radius=25 StartAngle=1.06699 EndAngle=1.16096
    g16: ArcOfCircle CenterX=-57.4791 CenterY=-63.4209 CenterZ=0 NormalX=0 NormalY=0 NormalZ=1 AngleXU=0 Radius=100 StartAngle=0.743962 EndAngle=0.764925
  constraints (51):
    c: Vertical(g0)
    c: Horizontal(g3)
    c: Vertical(g1)
    c: Horizontal(g2)
    c: Coincident(g3,g0)
    c: Coincident(g2,g4)
    c: Vertical(g4)
    c: Coincident(g4,g5)
    c: Horizontal(g5)
    c: Coincident(g5,g6)
    c: Coincident(g6,g7)
    c: Coincident(g7,g8)
    c: Coincident(g8,g3)
    c: Vertical(g8)
    c: Vertical(g6)
    c: Horizontal(g7)
    c: Vertical(g7,g4)
    c: PointOnObject(g2,g-1)
    c: DistanceX(g1) = 19.5
    c: DistanceY(g4,g4) = 0.5
    c: DistanceY(g6,g6) = 0.25
    c: DistanceX(g7,g7) = 0.3
    c: DistanceX(g0) = 15.6
    c: DistanceX(g7) = 16.75
    c: DistanceY(g0) = 4.3
    c: DistanceY(g0,g0) = 1
    c: Coincident(g2,g1)
    c: Coincident(g9,g1)
    c: DistanceX(g0,g9) = 0.5
    c: DistanceY(g1,g1) = 2.5
    c: PointOnObject(g10,g-2)
    c: Horizontal(g10)
    c: Tangent(g10,g11) = 1.5708
    c: Tangent(g12,g13) = -1.5708
    c: Coincident(g13,g14)
    c: Coincident(g14,g10)
    c: Vertical(g14)
    c: DistanceY(g14,g14) = 1
    c: Horizontal(g13)
    c: Horizontal(g0,g9)
    c: DistanceX(g10,g10) = 11.5
    c: DistanceY(g10) = 5.75
    c: Coincident(g0,g15)
    c: Tangent(g11,g15) = -1.5708
    c: Radius(g11) = 5
    c: Radius(g15) = 25
    c: Coincident(g16,g9)
    c: Tangent(g16,g12) = -1.5708
    c: Radius(g12) = 3
    c: Radius(g16) = 100
    c: DistanceX(g10,g12) = 1
FEATURE [Part::Revolution] Revolve006
  Angle = 15
  Axis = (0,0,1)
  Base = (0,0,0)
  FaceMakerClass = Part::FaceMakerBullseye
  Solid = true
  Source = -> Sketch054
  Symmetric = false
FEATURE [Sketcher::SketchObject] Sketch055
  Placement = pos=(0,0,4.3) rot=(0,0,1;0rad)
  sketch-geometry (36):
    g0: ArcOfCircle CenterX=0 CenterY=0 CenterZ=0 NormalX=0 NormalY=0 NormalZ=1 AngleXU=0 Radius=16.1 StartAngle=5.81607 EndAngle=6.7503
    g1: LineSegment StartX=-7.25 StartY=7.25 StartZ=0 EndX=7.25 EndY=7.25 EndZ=0
    g2: LineSegment StartX=7.25 StartY=7.25 StartZ=0 EndX=7.25 EndY=-7.25 EndZ=0
    g3: LineSegment StartX=7.25 StartY=-7.25 StartZ=0 EndX=-7.25 EndY=-7.25 EndZ=0
    g4: LineSegment StartX=-7.25 StartY=-7.25 StartZ=0 EndX=-7.25 EndY=7.25 EndZ=0
    g5: LineSegment StartX=8.75 StartY=7.25 StartZ=0 EndX=14.3752 EndY=7.25 EndZ=0
    g6: LineSegment StartX=14.3752 StartY=-7.25 StartZ=0 EndX=8.75 EndY=-7.25 EndZ=0
    g7: LineSegment StartX=8.75 StartY=-7.25 StartZ=0 EndX=8.75 EndY=7.25 EndZ=0
    g8: LineSegment StartX=-7.25 StartY=-8.75 StartZ=0 EndX=7.25 EndY=-8.75 EndZ=0
    g9: LineSegment StartX=7.25 StartY=-8.75 StartZ=0 EndX=7.25 EndY=-14.3752 EndZ=0
    g10: LineSegment StartX=-7.25 StartY=-14.3752 StartZ=0 EndX=-7.25 EndY=-8.75 EndZ=0
    g11: LineSegment StartX=-7.25 StartY=8.75 StartZ=0 EndX=7.25 EndY=8.75 EndZ=0
    g12: LineSegment StartX=7.25 StartY=8.75 StartZ=0 EndX=7.25 EndY=14.3752 EndZ=0
    g13: LineSegment StartX=-7.25 StartY=14.3752 StartZ=0 EndX=-7.25 EndY=8.75 EndZ=0
    g14: ArcOfCircle CenterX=0 CenterY=0 CenterZ=0 NormalX=0 NormalY=0 NormalZ=1 AngleXU=0 Radius=16.1 StartAngle=1.10368 EndAngle=2.03791
    g15: LineSegment StartX=-14.3752 StartY=7.25 StartZ=0 EndX=-8.75 EndY=7.25 EndZ=0
    g16: LineSegment StartX=-8.75 StartY=7.25 StartZ=0 EndX=-8.75 EndY=-7.25 EndZ=0
    g17: LineSegment StartX=-8.75 StartY=-7.25 StartZ=0 EndX=-14.3752 EndY=-7.25 EndZ=0
    g18: LineSegment [constr] StartX=-8.75 StartY=-7.25 StartZ=0 EndX=-7.25 EndY=-7.25 EndZ=0
    g19: LineSegment [constr] StartX=-7.25 StartY=-7.25 StartZ=0 EndX=-7.25 EndY=-8.75 EndZ=0
    g20: LineSegment [constr] StartX=7.25 StartY=7.25 StartZ=0 EndX=8.75 EndY=7.25 EndZ=0
    g21: LineSegment [constr] StartX=7.25 StartY=8.75 StartZ=0 EndX=7.25 EndY=7.25 EndZ=0
    g22: ArcOfCircle CenterX=0 CenterY=0 CenterZ=0 NormalX=0 NormalY=0 NormalZ=1 AngleXU=0 Radius=16.1 StartAngle=2.67448 EndAngle=3.60871
    g23: ArcOfCircle CenterX=0 CenterY=0 CenterZ=0 NormalX=0 NormalY=0 NormalZ=1 AngleXU=0 Radius=16.1 StartAngle=4.24528 EndAngle=5.1795
    g24: ArcOfCircle CenterX=0 CenterY=0 CenterZ=0 NormalX=0 NormalY=0 NormalZ=1 AngleXU=0 Radius=16.1 StartAngle=3.71617 EndAngle=4.13781
    g25: ArcOfCircle CenterX=0 CenterY=0 CenterZ=0 NormalX=0 NormalY=0 NormalZ=1 AngleXU=0 Radius=16.1 StartAngle=5.28696 EndAngle=5.70861
    g26: ArcOfCircle CenterX=0 CenterY=0 CenterZ=0 NormalX=0 NormalY=0 NormalZ=1 AngleXU=0 Radius=16.1 StartAngle=0.574575 EndAngle=0.996221
    g27: ArcOfCircle CenterX=0 CenterY=0 CenterZ=0 NormalX=0 NormalY=0 NormalZ=1 AngleXU=0 Radius=16.1 StartAngle=2.14537 EndAngle=2.56702
    g28: LineSegment StartX=-13.5147 StartY=8.75 StartZ=0 EndX=-8.75 EndY=8.75 EndZ=0
    g29: LineSegment StartX=-8.75 StartY=8.75 StartZ=0 EndX=-8.75 EndY=13.5147 EndZ=0
    g30: LineSegment StartX=-13.5147 StartY=-8.75 StartZ=0 EndX=-8.75 EndY=-8.75 EndZ=0
    g31: LineSegment StartX=-8.75 StartY=-8.75 StartZ=0 EndX=-8.75 EndY=-13.5147 EndZ=0
    g32: LineSegment StartX=8.75 StartY=-13.5147 StartZ=0 EndX=8.75 EndY=-8.75 EndZ=0
    g33: LineSegment StartX=8.75 StartY=-8.75 StartZ=0 EndX=13.5147 EndY=-8.75 EndZ=0
    g34: LineSegment StartX=8.75 StartY=13.5147 StartZ=0 EndX=8.75 EndY=8.75 EndZ=0
    g35: LineSegment StartX=8.75 StartY=8.75 StartZ=0 EndX=13.5147 EndY=8.75 EndZ=0
  constraints (105):
    c: Coincident(g0,g-1)
    c: Radius(g0) = 16.1
    c: Coincident(g1,g2)
    c: Coincident(g2,g3)
    c: Coincident(g3,g4)
    c: Coincident(g4,g1)
    c: Horizontal(g1)
    c: Horizontal(g3)
    c: Vertical(g2)
    c: Vertical(g4)
    c: Symmetric(g3,g1,g0)
    c: Equal(g1,g4)
    c: DistanceX(g1,g1) = 14.5
    c: Coincident(g6,g7)
    c: Coincident(g7,g5)
    c: Horizontal(g5)
    c: Horizontal(g6)
    c: Vertical(g7)
    c: Horizontal(g6,g2)
    c: Horizontal(g1,g5)
    c: Coincident(g8,g9)
    c: Coincident(g10,g8)
    c: Horizontal(g8)
    c: Vertical(g9)
    c: Vertical(g10)
    c: PointOnObject(g10,g0)
    c: Vertical(g8,g3)
    c: Vertical(g8,g2)
    c: Coincident(g0,g6)
    c: Coincident(g23,g9)
    c: Coincident(g11,g12)
    c: Coincident(g13,g11)
    c: Horizontal(g11)
    c: Vertical(g12)
    c: Vertical(g13)
    c: Vertical(g11,g1)
    c: Vertical(g11,g1)
    c: DistanceY(g1,g11) = 1.5
    c: PointOnObject(g13,g0)
    c: Equal(g0,g14)
    c: Coincident(g0,g5)
    c: Coincident(g14,g12)
    c: Coincident(g0,g14)
    c: Coincident(g15,g16)
    c: Coincident(g16,g17)
    c: Horizontal(g15)
    c: Horizontal(g17)
    c: Vertical(g16)
    c: Horizontal(g16,g3)
    c: Horizontal(g15,g1)
    c: Coincident(g18,g16)
    c: Coincident(g18,g3)
    c: Coincident(g19,g3)
    c: Coincident(g19,g8)
    c: Coincident(g20,g1)
    c: Coincident(g20,g5)
    c: Coincident(g21,g11)
    c: Coincident(g21,g1)
    c: Equal(g21,g20)
    c: Equal(g19,g18)
    c: Equal(g18,g20)
    c: Equal(g14,g22)
    c: PointOnObject(g14,g13)
    c: Coincident(g14,g22)
    c: Equal(g22,g23)
    c: PointOnObject(g23,g10)
    c: Coincident(g22,g23)
    c: Coincident(g17,g22)
    c: Coincident(g15,g22)
    c: Coincident(g24,g0)
    c: Coincident(g25,g0)
    c: Coincident(g26,g0)
    c: Coincident(g27,g0)
    c: Equal(g27,g26)
    c: Equal(g26,g25)
    c: Equal(g25,g24)
    c: Equal(g24,g22)
    c: Horizontal(g28)
    c: Coincident(g28,g29)
    c: Coincident(g29,g27)
    c: Vertical(g29)
    c: Coincident(g28,g27)
    c: Horizontal(g28,g11)
    c: Vertical(g28,g15)
    c: Horizontal(g30)
    c: Coincident(g30,g31)
    c: Vertical(g31)
    c: Coincident(g24,g31)
    c: Coincident(g24,g30)
    c: Vertical(g30,g16)
    c: Horizontal(g30,g8)
    c: Vertical(g32)
    c: Coincident(g32,g33)
    c: Horizontal(g33)
    c: Coincident(g25,g33)
    c: Coincident(g25,g32)
    c: Horizontal(g32,g8)
    c: Vertical(g6,g32)
    c: Vertical(g34)
    c: Coincident(g34,g35)
    c: Horizontal(g35)
    c: Coincident(g35,g26)
    c: Coincident(g26,g34)
    c: Vertical(g34,g5)
    c: Horizontal(g34,g11)
FEATURE [Part::Extrusion] Extrude008
  Base = -> Sketch055
  Dir = (0,0,1)
  DirMode = 2
  FaceMakerClass = Part::FaceMakerBullseye
  LengthFwd = 3
  LengthRev = 0
  Solid = true
  Symmetric = false
FEATURE [Image::ImagePlane] ImagePlane
  Placement = pos=(-0.5,0,0) rot=(0,0,1;0.785398rad)
  XSize = 47
  YSize = 47
FEATURE [Sketcher::SketchObject] Sketch056
  sketch-geometry (9):
    g0: Circle [constr] CenterX=0 CenterY=0 CenterZ=0 NormalX=0 NormalY=0 NormalZ=1 AngleXU=0 Radius=19.5
    g1: LineSegment [constr] StartX=0 StartY=0 StartZ=0 EndX=19.4933 EndY=0.51045 EndZ=0
    g2: LineSegment [constr] StartX=0 StartY=0 StartZ=0 EndX=18.8356 EndY=5.04697 EndZ=0
    g3: GeomPoint X=18.9935 Y=0.497362 Z=0
    g4: LineSegment StartX=19.6463 StartY=1.02962 StartZ=0 EndX=19.6997 EndY=0.0104672 EndZ=0
    g5: LineSegment StartX=19.6997 StartY=0.0104672 StartZ=0 EndX=19.5 EndY=0 EndZ=0
    g6: LineSegment StartX=19.6463 StartY=1.02962 StartZ=0 EndX=19.4733 EndY=1.02055 EndZ=0
    g7: LineSegment StartX=19.4733 StartY=1.02055 StartZ=0 EndX=18.9935 EndY=0.497362 EndZ=0
    g8: LineSegment StartX=18.9935 StartY=0.497362 StartZ=0 EndX=19.5 EndY=0 EndZ=0
  constraints (24):
    c: Angle(g2) = 0.261799
    c: Angle(g1) = 0.0261799
    c: Coincident(g1,g-1)
    c: PointOnObject(g2,g0)
    c: Radius(g0) = 19.5
    c: Coincident(g2,g-1)
    c: Coincident(g2,g0)
    c: PointOnObject(g6,g0)
    c: PointOnObject(g5,g0)
    c: PointOnObject(g3,g1)
    c: Coincident(g4,g5)
    c: Coincident(g4,g6)
    c: Perpendicular(g4,g6)
    c: Perpendicular(g0,g6)
    c: Perpendicular(g4,g5)
    c: Distance(g5) = 0.2
    c: PointOnObject(g5,g-1)
    c: PointOnObject(g1,g0)
    c: Distance(g1,g3) = 0.5
    c: Coincident(g6,g7)
    c: Coincident(g7,g3)
    c: Coincident(g7,g8)
    c: Coincident(g8,g5)
    c: Equal(g7,g8)
FEATURE [Part::FeaturePython] Array008  # Draft array (typed FeaturePython)
  Angle = 12
  ArrayType = 1
  Axis = (0,0,1)
  Base = -> Sketch056
  Center = (0,0,0)
  Fuse = false
  IntervalAxis = (0,0,0)
  IntervalX = (1,0,0)
  IntervalY = (0,1,0)
  IntervalZ = (0,0,1)
  NumberCircles = 2
  NumberPolar = 5
  NumberX = 1
  NumberY = 1
  NumberZ = 1
  RadialDistance = 1
  Symmetry = 1
  TangentialDistance = 1
FEATURE [Part::Extrusion] Extrude009
  Base = -> Array008
  Dir = (0,0,1)
  DirMode = 2
  FaceMakerClass = Part::FaceMakerBullseye
  LengthFwd = 5
  LengthRev = 0
  Solid = true
  Symmetric = false
FEATURE [Part::Cut] Cut004
  Base = -> Revolve006
  Tool = -> Extrude009
FEATURE [Part::FeaturePython] Array009  # Draft array (typed FeaturePython)
  Angle = 360
  ArrayType = 1
  Axis = (0,0,1)
  Base = -> Cut004
  Center = (0,0,0)
  Fuse = false
  IntervalAxis = (0,0,0)
  IntervalX = (1,0,0)
  IntervalY = (0,1,0)
  IntervalZ = (0,0,1)
  NumberCircles = 2
  NumberPolar = 24
  NumberX = 1
  NumberY = 1
  NumberZ = 1
  RadialDistance = 1
  Symmetry = 1
  TangentialDistance = 1
FEATURE [Part::Cut] Cut005  label="Bez7_Grilled"
  Base = -> Array009
  Tool = -> Extrude008
FEATURE [Sketcher::SketchObject] Sketch057
  MapMode = 5
  Placement = pos=(0,0,0) rot=(1,0,0;1.5708rad)
  sketch-geometry (12):
    g0: LineSegment StartX=15.6 StartY=2.6 StartZ=0 EndX=15.6 EndY=3.6 EndZ=0
    g1: LineSegment StartX=15.6 StartY=3.6 StartZ=0 EndX=19.5 EndY=2.75 EndZ=0
    g2: LineSegment StartX=19.5 StartY=2.75 StartZ=0 EndX=19.5 EndY=1.5 EndZ=0
    g3: LineSegment StartX=19.5 StartY=1.5 StartZ=0 EndX=17.75 EndY=1.25 EndZ=0
    g4: LineSegment StartX=17.75 StartY=1.25 StartZ=0 EndX=17.75 EndY=0 EndZ=0
    g5: LineSegment StartX=17.75 StartY=0 StartZ=0 EndX=16.75 EndY=0 EndZ=0
    g6: LineSegment StartX=16.75 StartY=2.6 StartZ=0 EndX=15.6 EndY=2.6 EndZ=0
    g7: LineSegment StartX=16.75 StartY=0 StartZ=0 EndX=16.75 EndY=0.5 EndZ=0
    g8: LineSegment StartX=16.75 StartY=0.5 StartZ=0 EndX=17.05 EndY=0.5 EndZ=0
    g9: LineSegment StartX=17.05 StartY=0.5 StartZ=0 EndX=17.05 EndY=0.75 EndZ=0
    g10: LineSegment StartX=17.05 StartY=0.75 StartZ=0 EndX=16.75 EndY=0.75 EndZ=0
    g11: LineSegment StartX=16.75 StartY=0.75 StartZ=0 EndX=16.75 EndY=2.6 EndZ=0
  constraints (37):
    c: Vertical(g0)
    c: Coincident(g0,g1)
    c: Coincident(g1,g2)
    c: Coincident(g2,g3)
    c: Coincident(g3,g4)
    c: Vertical(g4)
    c: Coincident(g4,g5)
    c: Horizontal(g6)
    c: Vertical(g2)
    c: Horizontal(g5)
    c: Coincident(g6,g0)
    c: Coincident(g5,g7)
    c: Vertical(g7)
    c: Coincident(g7,g8)
    c: Horizontal(g8)
    c: Coincident(g8,g9)
    c: Coincident(g9,g10)
    c: Coincident(g10,g11)
    c: Coincident(g11,g6)
    c: Vertical(g11)
    c: Vertical(g9)
    c: Horizontal(g10)
    c: Vertical(g10,g7)
    c: PointOnObject(g4,g-1)
    c: DistanceX(g1) = 19.5
    c: DistanceY(g3,g2) = 0.25
    c: DistanceY(g4,g4) = 1.25
    c: DistanceY(g7,g7) = 0.5
    c: DistanceY(g9,g9) = 0.25
    c: DistanceX(g10,g10) = 0.3
    c: DistanceX(g0) = 15.6
    c: DistanceX(g5,g5) = 1
    c: DistanceX(g10) = 16.75
    c: DistanceY(g0) = 3.6
    c: DistanceY(g0,g0) = 1
    c: DistanceY(g1) = 2.75
    c: Angle(g0,g1) = 1.3562
FEATURE [Part::Revolution] Revolve007
  Angle = 15
  Axis = (0,0,1)
  Base = (0,0,0)
  FaceMakerClass = Part::FaceMakerBullseye
  Solid = true
  Source = -> Sketch057
  Symmetric = false
FEATURE [Sketcher::SketchObject] Sketch064
  Placement = pos=(0,0,3.6) rot=(0,0,1;0rad)
  sketch-geometry (243):
    g0: LineSegment StartX=-15.3368 StartY=6.91673 StartZ=0 EndX=-15.2087 EndY=7.18965 EndZ=0
    g1: BSplineCurve PolesCount=3 KnotsCount=2 Degree=2 IsPeriodic=0
    g2: BSplineCurve PolesCount=3 KnotsCount=2 Degree=2 IsPeriodic=0
    g3: BSplineCurve PolesCount=3 KnotsCount=2 Degree=2 IsPeriodic=0
    g4: BSplineCurve PolesCount=3 KnotsCount=2 Degree=2 IsPeriodic=0
    g5: BSplineCurve PolesCount=3 KnotsCount=2 Degree=2 IsPeriodic=0
    g6: BSplineCurve PolesCount=3 KnotsCount=2 Degree=2 IsPeriodic=0
    g7: BSplineCurve PolesCount=3 KnotsCount=2 Degree=2 IsPeriodic=0
    g8: LineSegment StartX=-16.3192 StartY=8.06864 StartZ=0 EndX=-15.8464 EndY=7.64979 EndZ=0
    g9: LineSegment StartX=-15.8537 StartY=8.87491 StartZ=0 EndX=-16.3192 EndY=8.06864 EndZ=0
    g10: LineSegment StartX=-16.0891 StartY=9.01079 StartZ=0 EndX=-15.8537 EndY=8.87491 EndZ=0
    g11: LineSegment StartX=-16.6692 StartY=8.00594 StartZ=0 EndX=-16.0891 EndY=9.01079 EndZ=0
    g12: LineSegment StartX=-15.7536 StartY=7.21617 StartZ=0 EndX=-16.6692 EndY=8.00594 EndZ=0
    g13: LineSegment StartX=-15.5889 StartY=7.43125 StartZ=0 EndX=-15.7536 EndY=7.21617 EndZ=0
    g14: BSplineCurve PolesCount=3 KnotsCount=2 Degree=2 IsPeriodic=0
    g15: BSplineCurve PolesCount=3 KnotsCount=2 Degree=2 IsPeriodic=0
    g16: BSplineCurve PolesCount=3 KnotsCount=2 Degree=2 IsPeriodic=0
    g17: BSplineCurve PolesCount=3 KnotsCount=2 Degree=2 IsPeriodic=0
    g18: BSplineCurve PolesCount=3 KnotsCount=2 Degree=2 IsPeriodic=0
    g19: BSplineCurve PolesCount=3 KnotsCount=2 Degree=2 IsPeriodic=0
    g20: BSplineCurve PolesCount=3 KnotsCount=2 Degree=2 IsPeriodic=0
    g21: BSplineCurve PolesCount=3 KnotsCount=2 Degree=2 IsPeriodic=0
    g22: BSplineCurve PolesCount=3 KnotsCount=2 Degree=2 IsPeriodic=0
    g23: BSplineCurve PolesCount=3 KnotsCount=2 Degree=2 IsPeriodic=0
    g24: BSplineCurve PolesCount=3 KnotsCount=2 Degree=2 IsPeriodic=0
    g25: BSplineCurve PolesCount=3 KnotsCount=2 Degree=2 IsPeriodic=0
    g26: BSplineCurve PolesCount=3 KnotsCount=2 Degree=2 IsPeriodic=0
    g27: BSplineCurve PolesCount=3 KnotsCount=2 Degree=2 IsPeriodic=0
    g28: BSplineCurve PolesCount=3 KnotsCount=2 Degree=2 IsPeriodic=0
    g29: BSplineCurve PolesCount=3 KnotsCount=2 Degree=2 IsPeriodic=0
    g30: BSplineCurve PolesCount=3 KnotsCount=2 Degree=2 IsPeriodic=0
    g31: BSplineCurve PolesCount=3 KnotsCount=2 Degree=2 IsPeriodic=0
    g32: BSplineCurve PolesCount=3 KnotsCount=2 Degree=2 IsPeriodic=0
    g33: BSplineCurve PolesCount=3 KnotsCount=2 Degree=2 IsPeriodic=0
    g34: BSplineCurve PolesCount=3 KnotsCount=2 Degree=2 IsPeriodic=0
    g35: BSplineCurve PolesCount=3 KnotsCount=2 Degree=2 IsPeriodic=0
    g36: BSplineCurve PolesCount=3 KnotsCount=2 Degree=2 IsPeriodic=0
    g37: BSplineCurve PolesCount=3 KnotsCount=2 Degree=2 IsPeriodic=0
    g38: BSplineCurve PolesCount=3 KnotsCount=2 Degree=2 IsPeriodic=0
    g39: BSplineCurve PolesCount=3 KnotsCount=2 Degree=2 IsPeriodic=0
    g40: BSplineCurve PolesCount=3 KnotsCount=2 Degree=2 IsPeriodic=0
    g41: BSplineCurve PolesCount=3 KnotsCount=2 Degree=2 IsPeriodic=0
    g42: LineSegment StartX=-13.5528 StartY=-8.64786 StartZ=0 EndX=-14.0236 EndY=-8.91962 EndZ=0
    g43: LineSegment StartX=-13.6962 StartY=-8.39964 StartZ=0 EndX=-13.5528 EndY=-8.64786 EndZ=0
    g44: LineSegment StartX=-14.1669 StartY=-8.6714 StartZ=0 EndX=-13.6962 EndY=-8.39964 EndZ=0
    g45: LineSegment StartX=-14.3245 StartY=-8.39835 StartZ=0 EndX=-14.1669 EndY=-8.6714 EndZ=0
    g46: LineSegment StartX=-14.5599 StartY=-8.53424 StartZ=0 EndX=-14.3245 EndY=-8.39835 EndZ=0
    g47: LineSegment StartX=-14.4022 StartY=-8.80728 StartZ=0 EndX=-14.5599 EndY=-8.53424 EndZ=0
    g48: LineSegment StartX=-15.7555 StartY=-9.5886 StartZ=0 EndX=-14.4022 EndY=-8.80728 EndZ=0
    g49: LineSegment StartX=-15.6387 StartY=-9.79085 StartZ=0 EndX=-15.7555 EndY=-9.5886 EndZ=0
    g50: LineSegment StartX=-13.7525 StartY=-9.93256 StartZ=0 EndX=-15.6387 EndY=-9.79085 EndZ=0
    g51: LineSegment StartX=-13.5172 StartY=-9.79668 StartZ=0 EndX=-13.7525 EndY=-9.93256 EndZ=0
    g52: LineSegment StartX=-14.0236 StartY=-8.91962 StartZ=0 EndX=-13.5172 EndY=-9.79668 EndZ=0
    g53: LineSegment StartX=-14.2589 StartY=-9.05551 StartZ=0 EndX=-15.2003 EndY=-9.59903 EndZ=0
    g54: LineSegment StartX=-13.8937 StartY=-9.68802 StartZ=0 EndX=-14.2589 EndY=-9.05551 EndZ=0
    g55: LineSegment StartX=-15.2003 StartY=-9.59903 StartZ=0 EndX=-13.8937 EndY=-9.68802 EndZ=0
    g56: BSplineCurve PolesCount=3 KnotsCount=2 Degree=2 IsPeriodic=0
    g57: BSplineCurve PolesCount=3 KnotsCount=2 Degree=2 IsPeriodic=0
    g58: BSplineCurve PolesCount=3 KnotsCount=2 Degree=2 IsPeriodic=0
    g59: BSplineCurve PolesCount=3 KnotsCount=2 Degree=2 IsPeriodic=0
    g60: BSplineCurve PolesCount=3 KnotsCount=2 Degree=2 IsPeriodic=0
    g61: BSplineCurve PolesCount=3 KnotsCount=2 Degree=2 IsPeriodic=0
    g62: BSplineCurve PolesCount=3 KnotsCount=2 Degree=2 IsPeriodic=0
    g63: BSplineCurve PolesCount=3 KnotsCount=2 Degree=2 IsPeriodic=0
    g64: BSplineCurve PolesCount=3 KnotsCount=2 Degree=2 IsPeriodic=0
    g65: BSplineCurve PolesCount=3 KnotsCount=2 Degree=2 IsPeriodic=0
    g66: BSplineCurve PolesCount=3 KnotsCount=2 Degree=2 IsPeriodic=0
    g67: BSplineCurve PolesCount=3 KnotsCount=2 Degree=2 IsPeriodic=0
    g68: BSplineCurve PolesCount=3 KnotsCount=2 Degree=2 IsPeriodic=0
    g69: BSplineCurve PolesCount=3 KnotsCount=2 Degree=2 IsPeriodic=0
    g70: BSplineCurve PolesCount=3 KnotsCount=2 Degree=2 IsPeriodic=0
    g71: BSplineCurve PolesCount=3 KnotsCount=2 Degree=2 IsPeriodic=0
    g72: BSplineCurve PolesCount=3 KnotsCount=2 Degree=2 IsPeriodic=0
    g73: BSplineCurve PolesCount=3 KnotsCount=2 Degree=2 IsPeriodic=0
    g74: BSplineCurve PolesCount=3 KnotsCount=2 Degree=2 IsPeriodic=0
    g75: BSplineCurve PolesCount=3 KnotsCount=2 Degree=2 IsPeriodic=0
    g76: LineSegment StartX=1.67781 StartY=-16.7022 StartZ=0 EndX=1.39119 EndY=-16.7404 EndZ=0
    g77: BSplineCurve PolesCount=3 KnotsCount=2 Degree=2 IsPeriodic=0
    g78: BSplineCurve PolesCount=3 KnotsCount=2 Degree=2 IsPeriodic=0
    g79: BSplineCurve PolesCount=3 KnotsCount=2 Degree=2 IsPeriodic=0
    g80: BSplineCurve PolesCount=3 KnotsCount=2 Degree=2 IsPeriodic=0
    g81: BSplineCurve PolesCount=3 KnotsCount=2 Degree=2 IsPeriodic=0
    g82: BSplineCurve PolesCount=3 KnotsCount=2 Degree=2 IsPeriodic=0
    g83: BSplineCurve PolesCount=3 KnotsCount=2 Degree=2 IsPeriodic=0
    g84: BSplineCurve PolesCount=3 KnotsCount=2 Degree=2 IsPeriodic=0
    g85: BSplineCurve PolesCount=3 KnotsCount=2 Degree=2 IsPeriodic=0
    g86: BSplineCurve PolesCount=3 KnotsCount=2 Degree=2 IsPeriodic=0
    g87: BSplineCurve PolesCount=3 KnotsCount=2 Degree=2 IsPeriodic=0
    g88: BSplineCurve PolesCount=3 KnotsCount=2 Degree=2 IsPeriodic=0
    g89: BSplineCurve PolesCount=3 KnotsCount=2 Degree=2 IsPeriodic=0
    g90: LineSegment StartX=1.36253 StartY=-17.7596 StartZ=0 EndX=1.64915 EndY=-17.8105 EndZ=0
    g91: BSplineCurve PolesCount=3 KnotsCount=2 Degree=2 IsPeriodic=0
    g92: BSplineCurve PolesCount=3 KnotsCount=2 Degree=2 IsPeriodic=0
    g93: BSplineCurve PolesCount=3 KnotsCount=2 Degree=2 IsPeriodic=0
    g94: BSplineCurve PolesCount=3 KnotsCount=2 Degree=2 IsPeriodic=0
    g95: BSplineCurve PolesCount=3 KnotsCount=2 Degree=2 IsPeriodic=0
    g96: BSplineCurve PolesCount=3 KnotsCount=2 Degree=2 IsPeriodic=0
    g97: BSplineCurve PolesCount=3 KnotsCount=2 Degree=2 IsPeriodic=0
    g98: LineSegment StartX=1.112 StartY=-17.1502 StartZ=0 EndX=1.08015 EndY=-17.423 EndZ=0
    g99: BSplineCurve PolesCount=3 KnotsCount=2 Degree=2 IsPeriodic=0
    g100: BSplineCurve PolesCount=3 KnotsCount=2 Degree=2 IsPeriodic=0
    g101: BSplineCurve PolesCount=3 KnotsCount=2 Degree=2 IsPeriodic=0
    g102: BSplineCurve PolesCount=3 KnotsCount=2 Degree=2 IsPeriodic=0
    g103: BSplineCurve PolesCount=3 KnotsCount=2 Degree=2 IsPeriodic=0
    g104: BSplineCurve PolesCount=3 KnotsCount=2 Degree=2 IsPeriodic=0
    g105: BSplineCurve PolesCount=3 KnotsCount=2 Degree=2 IsPeriodic=0
    g106: BSplineCurve PolesCount=3 KnotsCount=2 Degree=2 IsPeriodic=0
    g107: BSplineCurve PolesCount=3 KnotsCount=2 Degree=2 IsPeriodic=0
    g108: BSplineCurve PolesCount=3 KnotsCount=2 Degree=2 IsPeriodic=0
    g109: BSplineCurve PolesCount=3 KnotsCount=2 Degree=2 IsPeriodic=0
    g110: BSplineCurve PolesCount=3 KnotsCount=2 Degree=2 IsPeriodic=0
    g111: BSplineCurve PolesCount=3 KnotsCount=2 Degree=2 IsPeriodic=0
    g112: BSplineCurve PolesCount=3 KnotsCount=2 Degree=2 IsPeriodic=0
    g113: BSplineCurve PolesCount=3 KnotsCount=2 Degree=2 IsPeriodic=0
    g114: BSplineCurve PolesCount=3 KnotsCount=2 Degree=2 IsPeriodic=0
    g115: BSplineCurve PolesCount=3 KnotsCount=2 Degree=2 IsPeriodic=0
    g116: BSplineCurve PolesCount=3 KnotsCount=2 Degree=2 IsPeriodic=0
    g117: BSplineCurve PolesCount=3 KnotsCount=2 Degree=2 IsPeriodic=0
    g118: BSplineCurve PolesCount=3 KnotsCount=2 Degree=2 IsPeriodic=0
    g119: BSplineCurve PolesCount=3 KnotsCount=2 Degree=2 IsPeriodic=0
    g120: BSplineCurve PolesCount=3 KnotsCount=2 Degree=2 IsPeriodic=0
    g121: BSplineCurve PolesCount=3 KnotsCount=2 Degree=2 IsPeriodic=0
    g122: BSplineCurve PolesCount=3 KnotsCount=2 Degree=2 IsPeriodic=0
    g123: BSplineCurve PolesCount=3 KnotsCount=2 Degree=2 IsPeriodic=0
    g124: BSplineCurve PolesCount=3 KnotsCount=2 Degree=2 IsPeriodic=0
    g125: BSplineCurve PolesCount=3 KnotsCount=2 Degree=2 IsPeriodic=0
    g126: LineSegment StartX=14.2213 StartY=-8.03366 StartZ=0 EndX=13.9859 EndY=-7.89778 EndZ=0
    g127: LineSegment StartX=14.794 StartY=-7.04169 StartZ=0 EndX=14.2213 EndY=-8.03366 EndZ=0
    g128: BSplineCurve PolesCount=3 KnotsCount=2 Degree=2 IsPeriodic=0
    g129: BSplineCurve PolesCount=3 KnotsCount=2 Degree=2 IsPeriodic=0
    g130: BSplineCurve PolesCount=3 KnotsCount=2 Degree=2 IsPeriodic=0
    g131: BSplineCurve PolesCount=3 KnotsCount=2 Degree=2 IsPeriodic=0
    g132: BSplineCurve PolesCount=3 KnotsCount=2 Degree=2 IsPeriodic=0
    g133: BSplineCurve PolesCount=3 KnotsCount=2 Degree=2 IsPeriodic=0
    g134: BSplineCurve PolesCount=3 KnotsCount=2 Degree=2 IsPeriodic=0
    g135: BSplineCurve PolesCount=3 KnotsCount=2 Degree=2 IsPeriodic=0
    g136: BSplineCurve PolesCount=3 KnotsCount=2 Degree=2 IsPeriodic=0
    g137: LineSegment StartX=15.9952 StartY=-7.6788 StartZ=0 EndX=16.1703 EndY=-7.43915 EndZ=0
    g138: BSplineCurve PolesCount=3 KnotsCount=2 Degree=2 IsPeriodic=0
    g139: BSplineCurve PolesCount=3 KnotsCount=2 Degree=2 IsPeriodic=0
    g140: BSplineCurve PolesCount=3 KnotsCount=2 Degree=2 IsPeriodic=0
    g141: BSplineCurve PolesCount=3 KnotsCount=2 Degree=2 IsPeriodic=0
    g142: BSplineCurve PolesCount=3 KnotsCount=2 Degree=2 IsPeriodic=0
    g143: BSplineCurve PolesCount=3 KnotsCount=2 Degree=2 IsPeriodic=0
    g144: BSplineCurve PolesCount=3 KnotsCount=2 Degree=2 IsPeriodic=0
    g145: BSplineCurve PolesCount=3 KnotsCount=2 Degree=2 IsPeriodic=0
    g146: BSplineCurve PolesCount=3 KnotsCount=2 Degree=2 IsPeriodic=0
    g147: LineSegment StartX=13.9859 StartY=-7.89778 StartZ=0 EndX=14.7577 EndY=-6.56105 EndZ=0
    g148: BSplineCurve PolesCount=3 KnotsCount=2 Degree=2 IsPeriodic=0
    g149: BSplineCurve PolesCount=3 KnotsCount=2 Degree=2 IsPeriodic=0
    g150: BSplineCurve PolesCount=3 KnotsCount=2 Degree=2 IsPeriodic=0
    g151: BSplineCurve PolesCount=3 KnotsCount=2 Degree=2 IsPeriodic=0
    g152: BSplineCurve PolesCount=3 KnotsCount=2 Degree=2 IsPeriodic=0
    g153: BSplineCurve PolesCount=3 KnotsCount=2 Degree=2 IsPeriodic=0
    g154: BSplineCurve PolesCount=3 KnotsCount=2 Degree=2 IsPeriodic=0
    g155: BSplineCurve PolesCount=3 KnotsCount=2 Degree=2 IsPeriodic=0
    g156: BSplineCurve PolesCount=3 KnotsCount=2 Degree=2 IsPeriodic=0
    g157: BSplineCurve PolesCount=3 KnotsCount=2 Degree=2 IsPeriodic=0
    g158: BSplineCurve PolesCount=3 KnotsCount=2 Degree=2 IsPeriodic=0
    g159: BSplineCurve PolesCount=3 KnotsCount=2 Degree=2 IsPeriodic=0
    g160: BSplineCurve PolesCount=3 KnotsCount=2 Degree=2 IsPeriodic=0
    g161: BSplineCurve PolesCount=3 KnotsCount=2 Degree=2 IsPeriodic=0
    g162: BSplineCurve PolesCount=3 KnotsCount=2 Degree=2 IsPeriodic=0
    g163: BSplineCurve PolesCount=3 KnotsCount=2 Degree=2 IsPeriodic=0
    g164: BSplineCurve PolesCount=3 KnotsCount=2 Degree=2 IsPeriodic=0
    g165: BSplineCurve PolesCount=3 KnotsCount=2 Degree=2 IsPeriodic=0
    g166: BSplineCurve PolesCount=3 KnotsCount=2 Degree=2 IsPeriodic=0
    g167: BSplineCurve PolesCount=3 KnotsCount=2 Degree=2 IsPeriodic=0
    g168: LineSegment StartX=7.57891 StartY=14.1266 StartZ=0 EndX=8.89593 EndY=16.2515 EndZ=0
    g169: LineSegment StartX=8.89593 StartY=16.2515 StartZ=0 EndX=9.74591 EndY=15.7247 EndZ=0
    g170: LineSegment StartX=9.74591 StartY=15.7247 StartZ=0 EndX=8.4289 EndY=13.5998 EndZ=0
    g171: LineSegment StartX=8.4289 StartY=13.5998 StartZ=0 EndX=7.57891 EndY=14.1266 EndZ=0
    g172: LineSegment StartX=13.6268 StartY=8.44452 StartZ=0 EndX=15.8299 EndY=9.62628 EndZ=0
    g173: LineSegment StartX=15.8299 StartY=9.62628 StartZ=0 EndX=16.3026 EndY=8.74506 EndZ=0
    g174: LineSegment StartX=16.3026 StartY=8.74506 StartZ=0 EndX=14.0995 EndY=7.5633 EndZ=0
    g175: LineSegment StartX=14.0995 StartY=7.5633 StartZ=0 EndX=13.6268 EndY=8.44452 EndZ=0
    g176: LineSegment StartX=16.0234 StartY=0.499756 StartZ=0 EndX=18.5222 EndY=0.421669 EndZ=0
    g177: LineSegment StartX=18.5222 StartY=0.421669 StartZ=0 EndX=18.491 EndY=-0.577843 EndZ=0
    g178: LineSegment StartX=18.491 StartY=-0.577843 StartZ=0 EndX=15.9922 EndY=-0.499756 EndZ=0
    g179: LineSegment StartX=15.9922 StartY=-0.499756 StartZ=0 EndX=16.0234 EndY=0.499756 EndZ=0
    g180: LineSegment StartX=1.62144 StartY=17.6756 StartZ=0 EndX=1.50208 EndY=16.6827 EndZ=0
    g181: LineSegment StartX=1.50208 StartY=16.6827 StartZ=0 EndX=1.9985 EndY=16.623 EndZ=0
    g182: LineSegment StartX=1.9985 StartY=16.623 StartZ=0 EndX=2.11787 EndY=17.6159 EndZ=0
    g183: LineSegment StartX=2.11787 StartY=17.6159 StartZ=0 EndX=1.62144 EndY=17.6756 EndZ=0
    g184: LineSegment StartX=3.46016 StartY=17.4093 StartZ=0 EndX=3.23767 EndY=16.4343 EndZ=0
    g185: LineSegment StartX=3.23767 StartY=16.4343 StartZ=0 EndX=3.72514 EndY=16.3231 EndZ=0
    g186: LineSegment StartX=3.72514 StartY=16.3231 StartZ=0 EndX=3.94763 EndY=17.298 EndZ=0
    g187: LineSegment StartX=3.94763 StartY=17.298 StartZ=0 EndX=3.46016 EndY=17.4093 EndZ=0
    g188: LineSegment StartX=5.26097 StartY=16.9522 StartZ=0 EndX=4.93779 EndY=16.0059 EndZ=0
    g189: LineSegment StartX=4.93779 StartY=16.0059 StartZ=0 EndX=5.41096 EndY=15.8443 EndZ=0
    g190: LineSegment StartX=5.41096 StartY=15.8443 StartZ=0 EndX=5.73414 EndY=16.7906 EndZ=0
    g191: LineSegment StartX=5.73414 StartY=16.7906 StartZ=0 EndX=5.26097 EndY=16.9522 EndZ=0
    g192: LineSegment StartX=7.00414 StartY=16.3094 StartZ=0 EndX=6.58381 EndY=15.4021 EndZ=0
    g193: LineSegment StartX=6.58381 StartY=15.4021 StartZ=0 EndX=7.03749 EndY=15.1919 EndZ=0
    g194: LineSegment StartX=7.03749 StartY=15.1919 StartZ=0 EndX=7.45782 EndY=16.0993 EndZ=0
    g195: LineSegment StartX=7.45782 StartY=16.0993 StartZ=0 EndX=7.00414 EndY=16.3094 EndZ=0
    g196: LineSegment StartX=10.242 StartY=14.4968 StartZ=0 EndX=9.6422 EndY=13.6966 EndZ=0
    g197: LineSegment StartX=9.6422 StartY=13.6966 StartZ=0 EndX=10.0423 EndY=13.3967 EndZ=0
    g198: LineSegment StartX=10.0423 StartY=13.3967 StartZ=0 EndX=10.6421 EndY=14.1969 EndZ=0
    g199: LineSegment StartX=10.6421 StartY=14.1969 StartZ=0 EndX=10.242 EndY=14.4968 EndZ=0
    g200: LineSegment StartX=11.7012 StartY=13.3468 StartZ=0 EndX=11.0211 EndY=12.6137 EndZ=0
    g201: LineSegment StartX=11.0211 StartY=12.6137 StartZ=0 EndX=11.3876 EndY=12.2736 EndZ=0
    g202: LineSegment StartX=11.3876 StartY=12.2736 StartZ=0 EndX=12.0678 EndY=13.0067 EndZ=0
    g203: LineSegment StartX=12.0678 StartY=13.0067 StartZ=0 EndX=11.7012 EndY=13.3468 EndZ=0
    g204: LineSegment StartX=13.0322 StartY=12.0506 StartZ=0 EndX=12.2792 EndY=11.3926 EndZ=0
    g205: LineSegment StartX=12.2792 StartY=11.3926 StartZ=0 EndX=12.6082 EndY=11.0161 EndZ=0
    g206: LineSegment StartX=12.6082 StartY=11.0161 StartZ=0 EndX=13.3612 EndY=11.674 EndZ=0
    g207: LineSegment StartX=13.3612 StartY=11.674 StartZ=0 EndX=13.0322 EndY=12.0506 EndZ=0
    g208: LineSegment StartX=14.2205 StartY=10.6223 StartZ=0 EndX=13.4028 EndY=10.0467 EndZ=0
    g209: LineSegment StartX=13.4028 StartY=10.0467 StartZ=0 EndX=13.6906 EndY=9.63781 EndZ=0
    g210: LineSegment StartX=13.6906 StartY=9.63781 StartZ=0 EndX=14.5083 EndY=10.2135 EndZ=0
    g211: LineSegment StartX=14.5083 StartY=10.2135 StartZ=0 EndX=14.2205 EndY=10.6223 EndZ=0
    g212: LineSegment StartX=16.1182 StartY=7.43358 StartZ=0 EndX=15.1987 EndY=7.04053 EndZ=0
    g213: LineSegment StartX=15.1987 StartY=7.04053 StartZ=0 EndX=15.3952 EndY=6.58077 EndZ=0
    g214: LineSegment StartX=15.3952 StartY=6.58077 StartZ=0 EndX=16.3147 EndY=6.97382 EndZ=0
    g215: LineSegment StartX=16.3147 StartY=6.97382 StartZ=0 EndX=16.1182 EndY=7.43358 EndZ=0
    g216: LineSegment StartX=16.8069 StartY=5.70805 StartZ=0 EndX=15.8514 EndY=5.41326 EndZ=0
    g217: LineSegment StartX=15.8514 StartY=5.41326 StartZ=0 EndX=15.9988 EndY=4.93548 EndZ=0
    g218: LineSegment StartX=15.9988 StartY=4.93548 StartZ=0 EndX=16.9543 EndY=5.23026 EndZ=0
    g219: LineSegment StartX=16.9543 StartY=5.23026 StartZ=0 EndX=16.8069 EndY=5.70805 EndZ=0
    g220: LineSegment StartX=17.3115 StartY=3.91997 StartZ=0 EndX=16.3304 EndY=3.72669 EndZ=0
    g221: LineSegment StartX=16.3304 StartY=3.72669 StartZ=0 EndX=16.427 EndY=3.23612 EndZ=0
    g222: LineSegment StartX=16.427 StartY=3.23612 StartZ=0 EndX=17.4082 EndY=3.4294 EndZ=0
    g223: LineSegment StartX=17.4082 StartY=3.4294 StartZ=0 EndX=17.3115 EndY=3.91997 EndZ=0
    g224: LineSegment StartX=17.6264 StartY=2.08895 StartZ=0 EndX=16.6305 EndY=1.99928 EndZ=0
    g225: LineSegment StartX=16.6305 StartY=1.99928 StartZ=0 EndX=16.6753 EndY=1.5013 EndZ=0
    g226: LineSegment StartX=16.6753 StartY=1.5013 StartZ=0 EndX=17.6713 EndY=1.59096 EndZ=0
    g227: LineSegment StartX=17.6713 StartY=1.59096 StartZ=0 EndX=17.6264 EndY=2.08895 EndZ=0
    g228: LineSegment StartX=17.6756 StartY=-1.62144 StartZ=0 EndX=16.6827 EndY=-1.50208 EndZ=0
    g229: LineSegment StartX=16.6827 StartY=-1.50208 StartZ=0 EndX=16.623 EndY=-1.9985 EndZ=0
    g230: LineSegment StartX=16.623 StartY=-1.9985 StartZ=0 EndX=17.6159 EndY=-2.11787 EndZ=0
    g231: LineSegment StartX=17.6159 StartY=-2.11787 StartZ=0 EndX=17.6756 EndY=-1.62144 EndZ=0
    g232: LineSegment StartX=17.4093 StartY=-3.46016 StartZ=0 EndX=16.4343 EndY=-3.23767 EndZ=0
    g233: LineSegment StartX=16.4343 StartY=-3.23767 StartZ=0 EndX=16.3231 EndY=-3.72514 EndZ=0
    g234: LineSegment StartX=16.3231 StartY=-3.72514 StartZ=0 EndX=17.298 EndY=-3.94763 EndZ=0
    g235: LineSegment StartX=17.298 StartY=-3.94763 StartZ=0 EndX=17.4093 EndY=-3.46016 EndZ=0
    g236: Circle [constr] CenterX=0 CenterY=0 CenterZ=0 NormalX=0 NormalY=0 NormalZ=1 AngleXU=0 Radius=17.25
    g237: Circle CenterX=-8.625 CenterY=14.9389 CenterZ=0 NormalX=0 NormalY=0 NormalZ=1 AngleXU=0 Radius=0.4
    g238: Circle CenterX=-17.25 CenterY=0 CenterZ=0 NormalX=0 NormalY=0 NormalZ=1 AngleXU=0 Radius=0.4
    g239: Circle CenterX=-8.625 CenterY=-14.9389 CenterZ=0 NormalX=0 NormalY=0 NormalZ=1 AngleXU=0 Radius=0.4
    g240: Circle CenterX=8.625 CenterY=-14.9389 CenterZ=0 NormalX=0 NormalY=0 NormalZ=1 AngleXU=0 Radius=0.4
    g241: LineSegment [constr] StartX=-8.625 StartY=14.9389 StartZ=0 EndX=0 EndY=0 EndZ=0
    g242: Circle CenterX=0 CenterY=17.25 CenterZ=0 NormalX=0 NormalY=0 NormalZ=1 AngleXU=0 Radius=1.2
  constraints (253):
    c: Coincident(g0,g1)
    c: Coincident(g1,g2)
    c: Coincident(g2,g3)
    c: Coincident(g3,g4)
    c: Coincident(g4,g5)
    c: Coincident(g5,g6)
    c: Coincident(g6,g7)
    c: Coincident(g7,g8)
    c: Coincident(g8,g9)
    c: Coincident(g9,g10)
    c: Coincident(g10,g11)
    c: Coincident(g11,g12)
    c: Coincident(g12,g13)
    c: Coincident(g13,g14)
    c: Coincident(g14,g15)
    c: Coincident(g15,g16)
    c: Coincident(g16,g17)
    c: Coincident(g17,g18)
    c: Coincident(g18,g19)
    c: Coincident(g19,g20)
    c: Coincident(g20,g21)
    c: Coincident(g21,g0)
    c: Coincident(g22,g23)
    c: Coincident(g23,g24)
    c: Coincident(g24,g25)
    c: Coincident(g25,g26)
    c: Coincident(g26,g27)
    c: Coincident(g27,g28)
    c: Coincident(g28,g29)
    c: Coincident(g29,g30)
    c: Coincident(g30,g31)
    c: Coincident(g31,g32)
    c: Coincident(g32,g33)
    c: Coincident(g33,g22)
    c: Coincident(g34,g35)
    c: Coincident(g35,g36)
    c: Coincident(g36,g37)
    c: Coincident(g37,g38)
    c: Coincident(g38,g39)
    c: Coincident(g39,g40)
    c: Coincident(g40,g41)
    c: Coincident(g41,g34)
    c: Coincident(g42,g43)
    c: Coincident(g43,g44)
    c: Coincident(g44,g45)
    c: Coincident(g45,g46)
    c: Coincident(g46,g47)
    c: Coincident(g47,g48)
    c: Coincident(g48,g49)
    c: Coincident(g49,g50)
    c: Coincident(g50,g51)
    c: Coincident(g51,g52)
    c: Coincident(g52,g42)
    c: Coincident(g53,g54)
    c: Coincident(g54,g55)
    c: Coincident(g55,g53)
    c: Coincident(g56,g57)
    c: Coincident(g57,g58)
    c: Coincident(g58,g59)
    c: Coincident(g59,g60)
    c: Coincident(g60,g61)
    c: Coincident(g61,g62)
    c: Coincident(g62,g63)
    c: Coincident(g63,g64)
    c: Coincident(g64,g65)
    c: Coincident(g65,g66)
    c: Coincident(g66,g67)
    c: Coincident(g67,g56)
    c: Coincident(g68,g69)
    c: Coincident(g69,g70)
    c: Coincident(g70,g71)
    c: Coincident(g71,g72)
    c: Coincident(g72,g73)
    c: Coincident(g73,g74)
    c: Coincident(g74,g75)
    c: Coincident(g75,g68)
    c: Coincident(g76,g77)
    c: Coincident(g77,g78)
    c: Coincident(g78,g79)
    c: Coincident(g79,g80)
    c: Coincident(g80,g81)
    c: Coincident(g81,g82)
    c: Coincident(g82,g83)
    c: Coincident(g83,g84)
    c: Coincident(g84,g85)
    c: Coincident(g85,g86)
    c: Coincident(g86,g87)
    c: Coincident(g87,g88)
    c: Coincident(g88,g89)
    c: Coincident(g89,g90)
    c: Coincident(g90,g91)
    c: Coincident(g91,g92)
    c: Coincident(g92,g93)
    c: Coincident(g93,g94)
    c: Coincident(g94,g95)
    c: Coincident(g95,g96)
    c: Coincident(g96,g97)
    c: Coincident(g97,g98)
    c: Coincident(g98,g99)
    c: Coincident(g99,g100)
    c: Coincident(g100,g101)
    c: Coincident(g101,g102)
    c: Coincident(g102,g103)
    c: Coincident(g103,g104)
    c: Coincident(g104,g105)
    c: Coincident(g105,g76)
    c: Coincident(g106,g107)
    c: Coincident(g107,g108)
    c: Coincident(g108,g109)
    c: Coincident(g109,g110)
    c: Coincident(g110,g111)
    c: Coincident(g111,g112)
    c: Coincident(g112,g113)
    c: Coincident(g113,g114)
    c: Coincident(g114,g115)
    c: Coincident(g115,g116)
    c: Coincident(g116,g117)
    c: Coincident(g117,g106)
    c: Coincident(g118,g119)
    c: Coincident(g119,g120)
    c: Coincident(g120,g121)
    c: Coincident(g121,g122)
    c: Coincident(g122,g123)
    c: Coincident(g123,g124)
    c: Coincident(g124,g125)
    c: Coincident(g125,g118)
    c: Coincident(g126,g127)
    c: Coincident(g127,g128)
    c: Coincident(g128,g129)
    c: Coincident(g129,g130)
    c: Coincident(g130,g131)
    c: Coincident(g131,g132)
    c: Coincident(g132,g133)
    c: Coincident(g133,g134)
    c: Coincident(g134,g135)
    c: Coincident(g135,g136)
    c: Coincident(g136,g137)
    c: Coincident(g137,g138)
    c: Coincident(g138,g139)
    c: Coincident(g139,g140)
    c: Coincident(g140,g141)
    c: Coincident(g141,g142)
    c: Coincident(g142,g143)
    c: Coincident(g143,g144)
    c: Coincident(g144,g145)
    c: Coincident(g145,g146)
    c: Coincident(g146,g147)
    c: Coincident(g147,g126)
    c: Coincident(g148,g149)
    c: Coincident(g149,g150)
    c: Coincident(g150,g151)
    c: Coincident(g151,g152)
    c: Coincident(g152,g153)
    c: Coincident(g153,g154)
    c: Coincident(g154,g155)
    c: Coincident(g155,g156)
    c: Coincident(g156,g157)
    c: Coincident(g157,g158)
    c: Coincident(g158,g159)
    c: Coincident(g159,g148)
    c: Coincident(g160,g161)
    c: Coincident(g161,g162)
    c: Coincident(g162,g163)
    c: Coincident(g163,g164)
    c: Coincident(g164,g165)
    c: Coincident(g165,g166)
    c: Coincident(g166,g167)
    c: Coincident(g167,g160)
    c: Coincident(g168,g169)
    c: Coincident(g169,g170)
    c: Coincident(g170,g171)
    c: Coincident(g171,g168)
    c: Coincident(g172,g173)
    c: Coincident(g173,g174)
    c: Coincident(g174,g175)
    c: Coincident(g175,g172)
    c: Coincident(g176,g177)
    c: Coincident(g177,g178)
    c: Coincident(g178,g179)
    c: Coincident(g179,g176)
    c: Coincident(g180,g181)
    c: Coincident(g181,g182)
    c: Coincident(g182,g183)
    c: Coincident(g183,g180)
    c: Coincident(g184,g185)
    c: Coincident(g185,g186)
    c: Coincident(g186,g187)
    c: Coincident(g187,g184)
    c: Coincident(g188,g189)
    c: Coincident(g189,g190)
    c: Coincident(g190,g191)
    c: Coincident(g191,g188)
    c: Coincident(g192,g193)
    c: Coincident(g193,g194)
    c: Coincident(g194,g195)
    c: Coincident(g195,g192)
    c: Coincident(g196,g197)
    c: Coincident(g197,g198)
    c: Coincident(g198,g199)
    c: Coincident(g199,g196)
    c: Coincident(g200,g201)
    c: Coincident(g201,g202)
    c: Coincident(g202,g203)
    c: Coincident(g203,g200)
    c: Coincident(g204,g205)
    c: Coincident(g205,g206)
    c: Coincident(g206,g207)
    c: Coincident(g207,g204)
    c: Coincident(g208,g209)
    c: Coincident(g209,g210)
    c: Coincident(g210,g211)
    c: Coincident(g211,g208)
    c: Coincident(g212,g213)
    c: Coincident(g213,g214)
    c: Coincident(g214,g215)
    c: Coincident(g215,g212)
    c: Coincident(g216,g217)
    c: Coincident(g217,g218)
    c: Coincident(g218,g219)
    c: Coincident(g219,g216)
    c: Coincident(g220,g221)
    c: Coincident(g221,g222)
    c: Coincident(g222,g223)
    c: Coincident(g223,g220)
    c: Coincident(g224,g225)
    c: Coincident(g225,g226)
    c: Coincident(g226,g227)
    c: Coincident(g227,g224)
    c: Coincident(g228,g229)
    c: Coincident(g229,g230)
    c: Coincident(g230,g231)
    c: Coincident(g231,g228)
    c: Coincident(g232,g233)
    c: Coincident(g233,g234)
    c: Coincident(g234,g235)
    c: Coincident(g235,g232)
    c: Coincident(g236,g-1)
    c: Radius(g236) = 17.25
    c: PointOnObject(g237,g236)
    c: PointOnObject(g238,g236)
    c: Equal(g240,g239)
    c: Equal(g239,g238)
    c: Equal(g238,g237)
    c: Radius(g237) = 0.4
    c: PointOnObject(g238,g-1)
    c: Symmetric(g239,g237,g-1)
    c: Symmetric(g239,g240,g-2)
    c: Coincident(g241,g237)
    c: Coincident(g241,g-1)
    c: Angle(g-2,g241) = 0.523599
    c: PointOnObject(g242,g236)
    c: PointOnObject(g242,g-2)
    c: Radius(g242) = 1.2
FEATURE [Sketcher::SketchObject] Sketch065
  sketch-geometry (10):
    g0: Circle [constr] CenterX=0 CenterY=0 CenterZ=0 NormalX=0 NormalY=0 NormalZ=1 AngleXU=0 Radius=19.5
    g1: LineSegment [constr] StartX=0 StartY=0 StartZ=0 EndX=19.4998 EndY=0.0850845 EndZ=0
    g2: LineSegment [constr] StartX=0 StartY=0 StartZ=0 EndX=18.8356 EndY=5.04697 EndZ=0
    g3: GeomPoint X=19.3998 Y=0.0846482 Z=0
    g4: LineSegment StartX=19.6985 StartY=0.171906 StartZ=0 EndX=19.7 EndY=0.00174531 EndZ=0
    g5: LineSegment StartX=19.7 StartY=0.00174531 StartZ=0 EndX=19.5 EndY=0 EndZ=0
    g6: LineSegment StartX=19.6985 StartY=0.171906 StartZ=0 EndX=19.4993 EndY=0.170167 EndZ=0
    g7: LineSegment StartX=19.4993 StartY=0.170167 StartZ=0 EndX=19.3994 EndY=0.169296 EndZ=0
    g8: LineSegment StartX=19.3994 StartY=0.169296 StartZ=0 EndX=19.4002 EndY=0 EndZ=0
    g9: LineSegment StartX=19.4002 StartY=0 StartZ=0 EndX=19.5 EndY=0 EndZ=0
  constraints (27):
    c: Angle(g2) = 0.261799
    c: Angle(g1) = 0.00436332
    c: Coincident(g1,g-1)
    c: PointOnObject(g2,g0)
    c: Radius(g0) = 19.5
    c: Coincident(g2,g-1)
    c: Coincident(g2,g0)
    c: PointOnObject(g6,g0)
    c: PointOnObject(g5,g0)
    c: PointOnObject(g3,g1)
    c: Coincident(g4,g5)
    c: Coincident(g4,g6)
    c: Perpendicular(g4,g6)
    c: Perpendicular(g0,g6)
    c: Perpendicular(g4,g5)
    c: Distance(g5) = 0.2
    c: PointOnObject(g5,g-1)
    c: PointOnObject(g1,g0)
    c: Coincident(g6,g7)
    c: Coincident(g7,g8)
    c: Coincident(g8,g9)
    c: Coincident(g9,g5)
    c: Perpendicular(g0,g7)
    c: Symmetric(g8,g7,g3)
    c: Distance(g3,g1) = 0.1
    c: Perpendicular(g1,g8)
    c: Perpendicular(g0,g9)
FEATURE [Part::FeaturePython] Array012  # Draft array (typed FeaturePython)
  Angle = 15
  ArrayType = 1
  Axis = (0,0,1)
  Base = -> Sketch065
  Center = (0,0,0)
  Fuse = false
  IntervalAxis = (0,0,0)
  IntervalX = (1,0,0)
  IntervalY = (0,1,0)
  IntervalZ = (0,0,1)
  NumberCircles = 2
  NumberPolar = 15
  NumberX = 1
  NumberY = 1
  NumberZ = 1
  RadialDistance = 1
  Symmetry = 1
  TangentialDistance = 1
FEATURE [Part::Extrusion] Extrude010
  Base = -> Array012
  Dir = (0,0,1)
  DirMode = 2
  FaceMakerClass = Part::FaceMakerBullseye
  LengthFwd = 10
  LengthRev = 0
  Solid = true
  Symmetric = false
FEATURE [Part::Cut] Cut006
  Base = -> Revolve007
  Tool = -> Extrude010
FEATURE [Part::FeaturePython] Array013  # Draft array (typed FeaturePython)
  Angle = 360
  ArrayType = 1
  Axis = (0,0,1)
  Base = -> Cut006
  Center = (0,0,0)
  Fuse = false
  IntervalAxis = (0,0,0)
  IntervalX = (1,0,0)
  IntervalY = (0,1,0)
  IntervalZ = (0,0,1)
  NumberCircles = 2
  NumberPolar = 24
  NumberX = 1
  NumberY = 1
  NumberZ = 1
  RadialDistance = 1
  Symmetry = 1
  TangentialDistance = 1
FEATURE [Part::Extrusion] Extrude011
  Base = -> Sketch064
  Dir = (0,0,1)
  DirMode = 2
  FaceMakerClass = Part::FaceMakerBullseye
  LengthFwd = -0.9
  LengthRev = 0
  Solid = true
  Symmetric = false
FEATURE [Part::FeaturePython] Clone  label="Array014"  # Draft clone (typed FeaturePython)
  AttacherType = Attacher::AttachEngine3D
  Fuse = false
  Objects = -> [Array013]
  Placement = pos=(0,0,-0.15) rot=(0,0,1;0rad)
  Scale = (1,1,1)
FEATURE [Part::Cut] Cut007
  Base = -> Extrude011
  Tool = -> Clone
FEATURE [Part::Cut] Cut008  label="Bez8"
  Base = -> Array013
  Tool = -> Cut007
FEATURE [Sketcher::SketchObject] Sketch066
  Placement = pos=(0,0,3.6) rot=(0,0,1;0rad)
  sketch-geometry (243):
    g0: LineSegment StartX=-15.3368 StartY=6.91673 StartZ=0 EndX=-15.2087 EndY=7.18965 EndZ=0
    g1: BSplineCurve PolesCount=3 KnotsCount=2 Degree=2 IsPeriodic=0
    g2: BSplineCurve PolesCount=3 KnotsCount=2 Degree=2 IsPeriodic=0
    g3: BSplineCurve PolesCount=3 KnotsCount=2 Degree=2 IsPeriodic=0
    g4: BSplineCurve PolesCount=3 KnotsCount=2 Degree=2 IsPeriodic=0
    g5: BSplineCurve PolesCount=3 KnotsCount=2 Degree=2 IsPeriodic=0
    g6: BSplineCurve PolesCount=3 KnotsCount=2 Degree=2 IsPeriodic=0
    g7: BSplineCurve PolesCount=3 KnotsCount=2 Degree=2 IsPeriodic=0
    g8: LineSegment StartX=-16.3192 StartY=8.06864 StartZ=0 EndX=-15.8464 EndY=7.64979 EndZ=0
    g9: LineSegment StartX=-15.8537 StartY=8.87491 StartZ=0 EndX=-16.3192 EndY=8.06864 EndZ=0
    g10: LineSegment StartX=-16.0891 StartY=9.01079 StartZ=0 EndX=-15.8537 EndY=8.87491 EndZ=0
    g11: LineSegment StartX=-16.6692 StartY=8.00594 StartZ=0 EndX=-16.0891 EndY=9.01079 EndZ=0
    g12: LineSegment StartX=-15.7536 StartY=7.21617 StartZ=0 EndX=-16.6692 EndY=8.00594 EndZ=0
    g13: LineSegment StartX=-15.5889 StartY=7.43125 StartZ=0 EndX=-15.7536 EndY=7.21617 EndZ=0
    g14: BSplineCurve PolesCount=3 KnotsCount=2 Degree=2 IsPeriodic=0
    g15: BSplineCurve PolesCount=3 KnotsCount=2 Degree=2 IsPeriodic=0
    g16: BSplineCurve PolesCount=3 KnotsCount=2 Degree=2 IsPeriodic=0
    g17: BSplineCurve PolesCount=3 KnotsCount=2 Degree=2 IsPeriodic=0
    g18: BSplineCurve PolesCount=3 KnotsCount=2 Degree=2 IsPeriodic=0
    g19: BSplineCurve PolesCount=3 KnotsCount=2 Degree=2 IsPeriodic=0
    g20: BSplineCurve PolesCount=3 KnotsCount=2 Degree=2 IsPeriodic=0
    g21: BSplineCurve PolesCount=3 KnotsCount=2 Degree=2 IsPeriodic=0
    g22: BSplineCurve PolesCount=3 KnotsCount=2 Degree=2 IsPeriodic=0
    g23: BSplineCurve PolesCount=3 KnotsCount=2 Degree=2 IsPeriodic=0
    g24: BSplineCurve PolesCount=3 KnotsCount=2 Degree=2 IsPeriodic=0
    g25: BSplineCurve PolesCount=3 KnotsCount=2 Degree=2 IsPeriodic=0
    g26: BSplineCurve PolesCount=3 KnotsCount=2 Degree=2 IsPeriodic=0
    g27: BSplineCurve PolesCount=3 KnotsCount=2 Degree=2 IsPeriodic=0
    g28: BSplineCurve PolesCount=3 KnotsCount=2 Degree=2 IsPeriodic=0
    g29: BSplineCurve PolesCount=3 KnotsCount=2 Degree=2 IsPeriodic=0
    g30: BSplineCurve PolesCount=3 KnotsCount=2 Degree=2 IsPeriodic=0
    g31: BSplineCurve PolesCount=3 KnotsCount=2 Degree=2 IsPeriodic=0
    g32: BSplineCurve PolesCount=3 KnotsCount=2 Degree=2 IsPeriodic=0
    g33: BSplineCurve PolesCount=3 KnotsCount=2 Degree=2 IsPeriodic=0
    g34: BSplineCurve PolesCount=3 KnotsCount=2 Degree=2 IsPeriodic=0
    g35: BSplineCurve PolesCount=3 KnotsCount=2 Degree=2 IsPeriodic=0
    g36: BSplineCurve PolesCount=3 KnotsCount=2 Degree=2 IsPeriodic=0
    g37: BSplineCurve PolesCount=3 KnotsCount=2 Degree=2 IsPeriodic=0
    g38: BSplineCurve PolesCount=3 KnotsCount=2 Degree=2 IsPeriodic=0
    g39: BSplineCurve PolesCount=3 KnotsCount=2 Degree=2 IsPeriodic=0
    g40: BSplineCurve PolesCount=3 KnotsCount=2 Degree=2 IsPeriodic=0
    g41: BSplineCurve PolesCount=3 KnotsCount=2 Degree=2 IsPeriodic=0
    g42: LineSegment StartX=-13.5528 StartY=-8.64786 StartZ=0 EndX=-14.0236 EndY=-8.91962 EndZ=0
    g43: LineSegment StartX=-13.6962 StartY=-8.39964 StartZ=0 EndX=-13.5528 EndY=-8.64786 EndZ=0
    g44: LineSegment StartX=-14.1669 StartY=-8.6714 StartZ=0 EndX=-13.6962 EndY=-8.39964 EndZ=0
    g45: LineSegment StartX=-14.3245 StartY=-8.39835 StartZ=0 EndX=-14.1669 EndY=-8.6714 EndZ=0
    g46: LineSegment StartX=-14.5599 StartY=-8.53424 StartZ=0 EndX=-14.3245 EndY=-8.39835 EndZ=0
    g47: LineSegment StartX=-14.4022 StartY=-8.80728 StartZ=0 EndX=-14.5599 EndY=-8.53424 EndZ=0
    g48: LineSegment StartX=-15.7555 StartY=-9.5886 StartZ=0 EndX=-14.4022 EndY=-8.80728 EndZ=0
    g49: LineSegment StartX=-15.6387 StartY=-9.79085 StartZ=0 EndX=-15.7555 EndY=-9.5886 EndZ=0
    g50: LineSegment StartX=-13.7525 StartY=-9.93256 StartZ=0 EndX=-15.6387 EndY=-9.79085 EndZ=0
    g51: LineSegment StartX=-13.5172 StartY=-9.79668 StartZ=0 EndX=-13.7525 EndY=-9.93256 EndZ=0
    g52: LineSegment StartX=-14.0236 StartY=-8.91962 StartZ=0 EndX=-13.5172 EndY=-9.79668 EndZ=0
    g53: LineSegment StartX=-14.2589 StartY=-9.05551 StartZ=0 EndX=-15.2003 EndY=-9.59903 EndZ=0
    g54: LineSegment StartX=-13.8937 StartY=-9.68802 StartZ=0 EndX=-14.2589 EndY=-9.05551 EndZ=0
    g55: LineSegment StartX=-15.2003 StartY=-9.59903 StartZ=0 EndX=-13.8937 EndY=-9.68802 EndZ=0
    g56: BSplineCurve PolesCount=3 KnotsCount=2 Degree=2 IsPeriodic=0
    g57: BSplineCurve PolesCount=3 KnotsCount=2 Degree=2 IsPeriodic=0
    g58: BSplineCurve PolesCount=3 KnotsCount=2 Degree=2 IsPeriodic=0
    g59: BSplineCurve PolesCount=3 KnotsCount=2 Degree=2 IsPeriodic=0
    g60: BSplineCurve PolesCount=3 KnotsCount=2 Degree=2 IsPeriodic=0
    g61: BSplineCurve PolesCount=3 KnotsCount=2 Degree=2 IsPeriodic=0
    g62: BSplineCurve PolesCount=3 KnotsCount=2 Degree=2 IsPeriodic=0
    g63: BSplineCurve PolesCount=3 KnotsCount=2 Degree=2 IsPeriodic=0
    g64: BSplineCurve PolesCount=3 KnotsCount=2 Degree=2 IsPeriodic=0
    g65: BSplineCurve PolesCount=3 KnotsCount=2 Degree=2 IsPeriodic=0
    g66: BSplineCurve PolesCount=3 KnotsCount=2 Degree=2 IsPeriodic=0
    g67: BSplineCurve PolesCount=3 KnotsCount=2 Degree=2 IsPeriodic=0
    g68: BSplineCurve PolesCount=3 KnotsCount=2 Degree=2 IsPeriodic=0
    g69: BSplineCurve PolesCount=3 KnotsCount=2 Degree=2 IsPeriodic=0
    g70: BSplineCurve PolesCount=3 KnotsCount=2 Degree=2 IsPeriodic=0
    g71: BSplineCurve PolesCount=3 KnotsCount=2 Degree=2 IsPeriodic=0
    g72: BSplineCurve PolesCount=3 KnotsCount=2 Degree=2 IsPeriodic=0
    g73: BSplineCurve PolesCount=3 KnotsCount=2 Degree=2 IsPeriodic=0
    g74: BSplineCurve PolesCount=3 KnotsCount=2 Degree=2 IsPeriodic=0
    g75: BSplineCurve PolesCount=3 KnotsCount=2 Degree=2 IsPeriodic=0
    g76: LineSegment StartX=1.67781 StartY=-16.7022 StartZ=0 EndX=1.39119 EndY=-16.7404 EndZ=0
    g77: BSplineCurve PolesCount=3 KnotsCount=2 Degree=2 IsPeriodic=0
    g78: BSplineCurve PolesCount=3 KnotsCount=2 Degree=2 IsPeriodic=0
    g79: BSplineCurve PolesCount=3 KnotsCount=2 Degree=2 IsPeriodic=0
    g80: BSplineCurve PolesCount=3 KnotsCount=2 Degree=2 IsPeriodic=0
    g81: BSplineCurve PolesCount=3 KnotsCount=2 Degree=2 IsPeriodic=0
    g82: BSplineCurve PolesCount=3 KnotsCount=2 Degree=2 IsPeriodic=0
    g83: BSplineCurve PolesCount=3 KnotsCount=2 Degree=2 IsPeriodic=0
    g84: BSplineCurve PolesCount=3 KnotsCount=2 Degree=2 IsPeriodic=0
    g85: BSplineCurve PolesCount=3 KnotsCount=2 Degree=2 IsPeriodic=0
    g86: BSplineCurve PolesCount=3 KnotsCount=2 Degree=2 IsPeriodic=0
    g87: BSplineCurve PolesCount=3 KnotsCount=2 Degree=2 IsPeriodic=0
    g88: BSplineCurve PolesCount=3 KnotsCount=2 Degree=2 IsPeriodic=0
    g89: BSplineCurve PolesCount=3 KnotsCount=2 Degree=2 IsPeriodic=0
    g90: LineSegment StartX=1.36253 StartY=-17.7596 StartZ=0 EndX=1.64915 EndY=-17.8105 EndZ=0
    g91: BSplineCurve PolesCount=3 KnotsCount=2 Degree=2 IsPeriodic=0
    g92: BSplineCurve PolesCount=3 KnotsCount=2 Degree=2 IsPeriodic=0
    g93: BSplineCurve PolesCount=3 KnotsCount=2 Degree=2 IsPeriodic=0
    g94: BSplineCurve PolesCount=3 KnotsCount=2 Degree=2 IsPeriodic=0
    g95: BSplineCurve PolesCount=3 KnotsCount=2 Degree=2 IsPeriodic=0
    g96: BSplineCurve PolesCount=3 KnotsCount=2 Degree=2 IsPeriodic=0
    g97: BSplineCurve PolesCount=3 KnotsCount=2 Degree=2 IsPeriodic=0
    g98: LineSegment StartX=1.112 StartY=-17.1502 StartZ=0 EndX=1.08015 EndY=-17.423 EndZ=0
    g99: BSplineCurve PolesCount=3 KnotsCount=2 Degree=2 IsPeriodic=0
    g100: BSplineCurve PolesCount=3 KnotsCount=2 Degree=2 IsPeriodic=0
    g101: BSplineCurve PolesCount=3 KnotsCount=2 Degree=2 IsPeriodic=0
    g102: BSplineCurve PolesCount=3 KnotsCount=2 Degree=2 IsPeriodic=0
    g103: BSplineCurve PolesCount=3 KnotsCount=2 Degree=2 IsPeriodic=0
    g104: BSplineCurve PolesCount=3 KnotsCount=2 Degree=2 IsPeriodic=0
    g105: BSplineCurve PolesCount=3 KnotsCount=2 Degree=2 IsPeriodic=0
    g106: BSplineCurve PolesCount=3 KnotsCount=2 Degree=2 IsPeriodic=0
    g107: BSplineCurve PolesCount=3 KnotsCount=2 Degree=2 IsPeriodic=0
    g108: BSplineCurve PolesCount=3 KnotsCount=2 Degree=2 IsPeriodic=0
    g109: BSplineCurve PolesCount=3 KnotsCount=2 Degree=2 IsPeriodic=0
    g110: BSplineCurve PolesCount=3 KnotsCount=2 Degree=2 IsPeriodic=0
    g111: BSplineCurve PolesCount=3 KnotsCount=2 Degree=2 IsPeriodic=0
    g112: BSplineCurve PolesCount=3 KnotsCount=2 Degree=2 IsPeriodic=0
    g113: BSplineCurve PolesCount=3 KnotsCount=2 Degree=2 IsPeriodic=0
    g114: BSplineCurve PolesCount=3 KnotsCount=2 Degree=2 IsPeriodic=0
    g115: BSplineCurve PolesCount=3 KnotsCount=2 Degree=2 IsPeriodic=0
    g116: BSplineCurve PolesCount=3 KnotsCount=2 Degree=2 IsPeriodic=0
    g117: BSplineCurve PolesCount=3 KnotsCount=2 Degree=2 IsPeriodic=0
    g118: BSplineCurve PolesCount=3 KnotsCount=2 Degree=2 IsPeriodic=0
    g119: BSplineCurve PolesCount=3 KnotsCount=2 Degree=2 IsPeriodic=0
    g120: BSplineCurve PolesCount=3 KnotsCount=2 Degree=2 IsPeriodic=0
    g121: BSplineCurve PolesCount=3 KnotsCount=2 Degree=2 IsPeriodic=0
    g122: BSplineCurve PolesCount=3 KnotsCount=2 Degree=2 IsPeriodic=0
    g123: BSplineCurve PolesCount=3 KnotsCount=2 Degree=2 IsPeriodic=0
    g124: BSplineCurve PolesCount=3 KnotsCount=2 Degree=2 IsPeriodic=0
    g125: BSplineCurve PolesCount=3 KnotsCount=2 Degree=2 IsPeriodic=0
    g126: LineSegment StartX=14.2213 StartY=-8.03366 StartZ=0 EndX=13.9859 EndY=-7.89778 EndZ=0
    g127: LineSegment StartX=14.794 StartY=-7.04169 StartZ=0 EndX=14.2213 EndY=-8.03366 EndZ=0
    g128: BSplineCurve PolesCount=3 KnotsCount=2 Degree=2 IsPeriodic=0
    g129: BSplineCurve PolesCount=3 KnotsCount=2 Degree=2 IsPeriodic=0
    g130: BSplineCurve PolesCount=3 KnotsCount=2 Degree=2 IsPeriodic=0
    g131: BSplineCurve PolesCount=3 KnotsCount=2 Degree=2 IsPeriodic=0
    g132: BSplineCurve PolesCount=3 KnotsCount=2 Degree=2 IsPeriodic=0
    g133: BSplineCurve PolesCount=3 KnotsCount=2 Degree=2 IsPeriodic=0
    g134: BSplineCurve PolesCount=3 KnotsCount=2 Degree=2 IsPeriodic=0
    g135: BSplineCurve PolesCount=3 KnotsCount=2 Degree=2 IsPeriodic=0
    g136: BSplineCurve PolesCount=3 KnotsCount=2 Degree=2 IsPeriodic=0
    g137: LineSegment StartX=15.9952 StartY=-7.6788 StartZ=0 EndX=16.1703 EndY=-7.43915 EndZ=0
    g138: BSplineCurve PolesCount=3 KnotsCount=2 Degree=2 IsPeriodic=0
    g139: BSplineCurve PolesCount=3 KnotsCount=2 Degree=2 IsPeriodic=0
    g140: BSplineCurve PolesCount=3 KnotsCount=2 Degree=2 IsPeriodic=0
    g141: BSplineCurve PolesCount=3 KnotsCount=2 Degree=2 IsPeriodic=0
    g142: BSplineCurve PolesCount=3 KnotsCount=2 Degree=2 IsPeriodic=0
    g143: BSplineCurve PolesCount=3 KnotsCount=2 Degree=2 IsPeriodic=0
    g144: BSplineCurve PolesCount=3 KnotsCount=2 Degree=2 IsPeriodic=0
    g145: BSplineCurve PolesCount=3 KnotsCount=2 Degree=2 IsPeriodic=0
    g146: BSplineCurve PolesCount=3 KnotsCount=2 Degree=2 IsPeriodic=0
    g147: LineSegment StartX=13.9859 StartY=-7.89778 StartZ=0 EndX=14.7577 EndY=-6.56105 EndZ=0
    g148: BSplineCurve PolesCount=3 KnotsCount=2 Degree=2 IsPeriodic=0
    g149: BSplineCurve PolesCount=3 KnotsCount=2 Degree=2 IsPeriodic=0
    g150: BSplineCurve PolesCount=3 KnotsCount=2 Degree=2 IsPeriodic=0
    g151: BSplineCurve PolesCount=3 KnotsCount=2 Degree=2 IsPeriodic=0
    g152: BSplineCurve PolesCount=3 KnotsCount=2 Degree=2 IsPeriodic=0
    g153: BSplineCurve PolesCount=3 KnotsCount=2 Degree=2 IsPeriodic=0
    g154: BSplineCurve PolesCount=3 KnotsCount=2 Degree=2 IsPeriodic=0
    g155: BSplineCurve PolesCount=3 KnotsCount=2 Degree=2 IsPeriodic=0
    g156: BSplineCurve PolesCount=3 KnotsCount=2 Degree=2 IsPeriodic=0
    g157: BSplineCurve PolesCount=3 KnotsCount=2 Degree=2 IsPeriodic=0
    g158: BSplineCurve PolesCount=3 KnotsCount=2 Degree=2 IsPeriodic=0
    g159: BSplineCurve PolesCount=3 KnotsCount=2 Degree=2 IsPeriodic=0
    g160: BSplineCurve PolesCount=3 KnotsCount=2 Degree=2 IsPeriodic=0
    g161: BSplineCurve PolesCount=3 KnotsCount=2 Degree=2 IsPeriodic=0
    g162: BSplineCurve PolesCount=3 KnotsCount=2 Degree=2 IsPeriodic=0
    g163: BSplineCurve PolesCount=3 KnotsCount=2 Degree=2 IsPeriodic=0
    g164: BSplineCurve PolesCount=3 KnotsCount=2 Degree=2 IsPeriodic=0
    g165: BSplineCurve PolesCount=3 KnotsCount=2 Degree=2 IsPeriodic=0
    g166: BSplineCurve PolesCount=3 KnotsCount=2 Degree=2 IsPeriodic=0
    g167: BSplineCurve PolesCount=3 KnotsCount=2 Degree=2 IsPeriodic=0
    g168: LineSegment StartX=7.57891 StartY=14.1266 StartZ=0 EndX=8.89593 EndY=16.2515 EndZ=0
    g169: LineSegment StartX=8.89593 StartY=16.2515 StartZ=0 EndX=9.74591 EndY=15.7247 EndZ=0
    g170: LineSegment StartX=9.74591 StartY=15.7247 StartZ=0 EndX=8.4289 EndY=13.5998 EndZ=0
    g171: LineSegment StartX=8.4289 StartY=13.5998 StartZ=0 EndX=7.57891 EndY=14.1266 EndZ=0
    g172: LineSegment StartX=13.6268 StartY=8.44452 StartZ=0 EndX=15.8299 EndY=9.62628 EndZ=0
    g173: LineSegment StartX=15.8299 StartY=9.62628 StartZ=0 EndX=16.3026 EndY=8.74506 EndZ=0
    g174: LineSegment StartX=16.3026 StartY=8.74506 StartZ=0 EndX=14.0995 EndY=7.5633 EndZ=0
    g175: LineSegment StartX=14.0995 StartY=7.5633 StartZ=0 EndX=13.6268 EndY=8.44452 EndZ=0
    g176: LineSegment StartX=16.0234 StartY=0.499756 StartZ=0 EndX=18.5222 EndY=0.421669 EndZ=0
    g177: LineSegment StartX=18.5222 StartY=0.421669 StartZ=0 EndX=18.491 EndY=-0.577843 EndZ=0
    g178: LineSegment StartX=18.491 StartY=-0.577843 StartZ=0 EndX=15.9922 EndY=-0.499756 EndZ=0
    g179: LineSegment StartX=15.9922 StartY=-0.499756 StartZ=0 EndX=16.0234 EndY=0.499756 EndZ=0
    g180: LineSegment StartX=1.62144 StartY=17.6756 StartZ=0 EndX=1.50208 EndY=16.6827 EndZ=0
    g181: LineSegment StartX=1.50208 StartY=16.6827 StartZ=0 EndX=1.9985 EndY=16.623 EndZ=0
    g182: LineSegment StartX=1.9985 StartY=16.623 StartZ=0 EndX=2.11787 EndY=17.6159 EndZ=0
    g183: LineSegment StartX=2.11787 StartY=17.6159 StartZ=0 EndX=1.62144 EndY=17.6756 EndZ=0
    g184: LineSegment StartX=3.46016 StartY=17.4093 StartZ=0 EndX=3.23767 EndY=16.4343 EndZ=0
    g185: LineSegment StartX=3.23767 StartY=16.4343 StartZ=0 EndX=3.72514 EndY=16.3231 EndZ=0
    g186: LineSegment StartX=3.72514 StartY=16.3231 StartZ=0 EndX=3.94763 EndY=17.298 EndZ=0
    g187: LineSegment StartX=3.94763 StartY=17.298 StartZ=0 EndX=3.46016 EndY=17.4093 EndZ=0
    g188: LineSegment StartX=5.26097 StartY=16.9522 StartZ=0 EndX=4.93779 EndY=16.0059 EndZ=0
    g189: LineSegment StartX=4.93779 StartY=16.0059 StartZ=0 EndX=5.41096 EndY=15.8443 EndZ=0
    g190: LineSegment StartX=5.41096 StartY=15.8443 StartZ=0 EndX=5.73414 EndY=16.7906 EndZ=0
    g191: LineSegment StartX=5.73414 StartY=16.7906 StartZ=0 EndX=5.26097 EndY=16.9522 EndZ=0
    g192: LineSegment StartX=7.00414 StartY=16.3094 StartZ=0 EndX=6.58381 EndY=15.4021 EndZ=0
    g193: LineSegment StartX=6.58381 StartY=15.4021 StartZ=0 EndX=7.03749 EndY=15.1919 EndZ=0
    g194: LineSegment StartX=7.03749 StartY=15.1919 StartZ=0 EndX=7.45782 EndY=16.0993 EndZ=0
    g195: LineSegment StartX=7.45782 StartY=16.0993 StartZ=0 EndX=7.00414 EndY=16.3094 EndZ=0
    g196: LineSegment StartX=10.242 StartY=14.4968 StartZ=0 EndX=9.6422 EndY=13.6966 EndZ=0
    g197: LineSegment StartX=9.6422 StartY=13.6966 StartZ=0 EndX=10.0423 EndY=13.3967 EndZ=0
    g198: LineSegment StartX=10.0423 StartY=13.3967 StartZ=0 EndX=10.6421 EndY=14.1969 EndZ=0
    g199: LineSegment StartX=10.6421 StartY=14.1969 StartZ=0 EndX=10.242 EndY=14.4968 EndZ=0
    g200: LineSegment StartX=11.7012 StartY=13.3468 StartZ=0 EndX=11.0211 EndY=12.6137 EndZ=0
    g201: LineSegment StartX=11.0211 StartY=12.6137 StartZ=0 EndX=11.3876 EndY=12.2736 EndZ=0
    g202: LineSegment StartX=11.3876 StartY=12.2736 StartZ=0 EndX=12.0678 EndY=13.0067 EndZ=0
    g203: LineSegment StartX=12.0678 StartY=13.0067 StartZ=0 EndX=11.7012 EndY=13.3468 EndZ=0
    g204: LineSegment StartX=13.0322 StartY=12.0506 StartZ=0 EndX=12.2792 EndY=11.3926 EndZ=0
    g205: LineSegment StartX=12.2792 StartY=11.3926 StartZ=0 EndX=12.6082 EndY=11.0161 EndZ=0
    g206: LineSegment StartX=12.6082 StartY=11.0161 StartZ=0 EndX=13.3612 EndY=11.674 EndZ=0
    g207: LineSegment StartX=13.3612 StartY=11.674 StartZ=0 EndX=13.0322 EndY=12.0506 EndZ=0
    g208: LineSegment StartX=14.2205 StartY=10.6223 StartZ=0 EndX=13.4028 EndY=10.0467 EndZ=0
    g209: LineSegment StartX=13.4028 StartY=10.0467 StartZ=0 EndX=13.6906 EndY=9.63781 EndZ=0
    g210: LineSegment StartX=13.6906 StartY=9.63781 StartZ=0 EndX=14.5083 EndY=10.2135 EndZ=0
    g211: LineSegment StartX=14.5083 StartY=10.2135 StartZ=0 EndX=14.2205 EndY=10.6223 EndZ=0
    g212: LineSegment StartX=16.1182 StartY=7.43358 StartZ=0 EndX=15.1987 EndY=7.04053 EndZ=0
    g213: LineSegment StartX=15.1987 StartY=7.04053 StartZ=0 EndX=15.3952 EndY=6.58077 EndZ=0
    g214: LineSegment StartX=15.3952 StartY=6.58077 StartZ=0 EndX=16.3147 EndY=6.97382 EndZ=0
    g215: LineSegment StartX=16.3147 StartY=6.97382 StartZ=0 EndX=16.1182 EndY=7.43358 EndZ=0
    g216: LineSegment StartX=16.8069 StartY=5.70805 StartZ=0 EndX=15.8514 EndY=5.41326 EndZ=0
    g217: LineSegment StartX=15.8514 StartY=5.41326 StartZ=0 EndX=15.9988 EndY=4.93548 EndZ=0
    g218: LineSegment StartX=15.9988 StartY=4.93548 StartZ=0 EndX=16.9543 EndY=5.23026 EndZ=0
    g219: LineSegment StartX=16.9543 StartY=5.23026 StartZ=0 EndX=16.8069 EndY=5.70805 EndZ=0
    g220: LineSegment StartX=17.3115 StartY=3.91997 StartZ=0 EndX=16.3304 EndY=3.72669 EndZ=0
    g221: LineSegment StartX=16.3304 StartY=3.72669 StartZ=0 EndX=16.427 EndY=3.23612 EndZ=0
    g222: LineSegment StartX=16.427 StartY=3.23612 StartZ=0 EndX=17.4082 EndY=3.4294 EndZ=0
    g223: LineSegment StartX=17.4082 StartY=3.4294 StartZ=0 EndX=17.3115 EndY=3.91997 EndZ=0
    g224: LineSegment StartX=17.6264 StartY=2.08895 StartZ=0 EndX=16.6305 EndY=1.99928 EndZ=0
    g225: LineSegment StartX=16.6305 StartY=1.99928 StartZ=0 EndX=16.6753 EndY=1.5013 EndZ=0
    g226: LineSegment StartX=16.6753 StartY=1.5013 StartZ=0 EndX=17.6713 EndY=1.59096 EndZ=0
    g227: LineSegment StartX=17.6713 StartY=1.59096 StartZ=0 EndX=17.6264 EndY=2.08895 EndZ=0
    g228: LineSegment StartX=17.6756 StartY=-1.62144 StartZ=0 EndX=16.6827 EndY=-1.50208 EndZ=0
    g229: LineSegment StartX=16.6827 StartY=-1.50208 StartZ=0 EndX=16.623 EndY=-1.9985 EndZ=0
    g230: LineSegment StartX=16.623 StartY=-1.9985 StartZ=0 EndX=17.6159 EndY=-2.11787 EndZ=0
    g231: LineSegment StartX=17.6159 StartY=-2.11787 StartZ=0 EndX=17.6756 EndY=-1.62144 EndZ=0
    g232: LineSegment StartX=17.4093 StartY=-3.46016 StartZ=0 EndX=16.4343 EndY=-3.23767 EndZ=0
    g233: LineSegment StartX=16.4343 StartY=-3.23767 StartZ=0 EndX=16.3231 EndY=-3.72514 EndZ=0
    g234: LineSegment StartX=16.3231 StartY=-3.72514 StartZ=0 EndX=17.298 EndY=-3.94763 EndZ=0
    g235: LineSegment StartX=17.298 StartY=-3.94763 StartZ=0 EndX=17.4093 EndY=-3.46016 EndZ=0
    g236: Circle [constr] CenterX=0 CenterY=0 CenterZ=0 NormalX=0 NormalY=0 NormalZ=1 AngleXU=0 Radius=17.25
    g237: Circle CenterX=-8.625 CenterY=14.9389 CenterZ=0 NormalX=0 NormalY=0 NormalZ=1 AngleXU=0 Radius=0.4
    g238: Circle CenterX=-17.25 CenterY=0 CenterZ=0 NormalX=0 NormalY=0 NormalZ=1 AngleXU=0 Radius=0.4
    g239: Circle CenterX=-8.625 CenterY=-14.9389 CenterZ=0 NormalX=0 NormalY=0 NormalZ=1 AngleXU=0 Radius=0.4
    g240: Circle CenterX=8.625 CenterY=-14.9389 CenterZ=0 NormalX=0 NormalY=0 NormalZ=1 AngleXU=0 Radius=0.4
    g241: LineSegment [constr] StartX=-8.625 StartY=14.9389 StartZ=0 EndX=0 EndY=0 EndZ=0
    g242: Circle CenterX=0 CenterY=17.25 CenterZ=0 NormalX=0 NormalY=0 NormalZ=1 AngleXU=0 Radius=1.2
  constraints (253):
    c: Coincident(g0,g1)
    c: Coincident(g1,g2)
    c: Coincident(g2,g3)
    c: Coincident(g3,g4)
    c: Coincident(g4,g5)
    c: Coincident(g5,g6)
    c: Coincident(g6,g7)
    c: Coincident(g7,g8)
    c: Coincident(g8,g9)
    c: Coincident(g9,g10)
    c: Coincident(g10,g11)
    c: Coincident(g11,g12)
    c: Coincident(g12,g13)
    c: Coincident(g13,g14)
    c: Coincident(g14,g15)
    c: Coincident(g15,g16)
    c: Coincident(g16,g17)
    c: Coincident(g17,g18)
    c: Coincident(g18,g19)
    c: Coincident(g19,g20)
    c: Coincident(g20,g21)
    c: Coincident(g21,g0)
    c: Coincident(g22,g23)
    c: Coincident(g23,g24)
    c: Coincident(g24,g25)
    c: Coincident(g25,g26)
    c: Coincident(g26,g27)
    c: Coincident(g27,g28)
    c: Coincident(g28,g29)
    c: Coincident(g29,g30)
    c: Coincident(g30,g31)
    c: Coincident(g31,g32)
    c: Coincident(g32,g33)
    c: Coincident(g33,g22)
    c: Coincident(g34,g35)
    c: Coincident(g35,g36)
    c: Coincident(g36,g37)
    c: Coincident(g37,g38)
    c: Coincident(g38,g39)
    c: Coincident(g39,g40)
    c: Coincident(g40,g41)
    c: Coincident(g41,g34)
    c: Coincident(g42,g43)
    c: Coincident(g43,g44)
    c: Coincident(g44,g45)
    c: Coincident(g45,g46)
    c: Coincident(g46,g47)
    c: Coincident(g47,g48)
    c: Coincident(g48,g49)
    c: Coincident(g49,g50)
    c: Coincident(g50,g51)
    c: Coincident(g51,g52)
    c: Coincident(g52,g42)
    c: Coincident(g53,g54)
    c: Coincident(g54,g55)
    c: Coincident(g55,g53)
    c: Coincident(g56,g57)
    c: Coincident(g57,g58)
    c: Coincident(g58,g59)
    c: Coincident(g59,g60)
    c: Coincident(g60,g61)
    c: Coincident(g61,g62)
    c: Coincident(g62,g63)
    c: Coincident(g63,g64)
    c: Coincident(g64,g65)
    c: Coincident(g65,g66)
    c: Coincident(g66,g67)
    c: Coincident(g67,g56)
    c: Coincident(g68,g69)
    c: Coincident(g69,g70)
    c: Coincident(g70,g71)
    c: Coincident(g71,g72)
    c: Coincident(g72,g73)
    c: Coincident(g73,g74)
    c: Coincident(g74,g75)
    c: Coincident(g75,g68)
    c: Coincident(g76,g77)
    c: Coincident(g77,g78)
    c: Coincident(g78,g79)
    c: Coincident(g79,g80)
    c: Coincident(g80,g81)
    c: Coincident(g81,g82)
    c: Coincident(g82,g83)
    c: Coincident(g83,g84)
    c: Coincident(g84,g85)
    c: Coincident(g85,g86)
    c: Coincident(g86,g87)
    c: Coincident(g87,g88)
    c: Coincident(g88,g89)
    c: Coincident(g89,g90)
    c: Coincident(g90,g91)
    c: Coincident(g91,g92)
    c: Coincident(g92,g93)
    c: Coincident(g93,g94)
    c: Coincident(g94,g95)
    c: Coincident(g95,g96)
    c: Coincident(g96,g97)
    c: Coincident(g97,g98)
    c: Coincident(g98,g99)
    c: Coincident(g99,g100)
    c: Coincident(g100,g101)
    c: Coincident(g101,g102)
    c: Coincident(g102,g103)
    c: Coincident(g103,g104)
    c: Coincident(g104,g105)
    c: Coincident(g105,g76)
    c: Coincident(g106,g107)
    c: Coincident(g107,g108)
    c: Coincident(g108,g109)
    c: Coincident(g109,g110)
    c: Coincident(g110,g111)
    c: Coincident(g111,g112)
    c: Coincident(g112,g113)
    c: Coincident(g113,g114)
    c: Coincident(g114,g115)
    c: Coincident(g115,g116)
    c: Coincident(g116,g117)
    c: Coincident(g117,g106)
    c: Coincident(g118,g119)
    c: Coincident(g119,g120)
    c: Coincident(g120,g121)
    c: Coincident(g121,g122)
    c: Coincident(g122,g123)
    c: Coincident(g123,g124)
    c: Coincident(g124,g125)
    c: Coincident(g125,g118)
    c: Coincident(g126,g127)
    c: Coincident(g127,g128)
    c: Coincident(g128,g129)
    c: Coincident(g129,g130)
    c: Coincident(g130,g131)
    c: Coincident(g131,g132)
    c: Coincident(g132,g133)
    c: Coincident(g133,g134)
    c: Coincident(g134,g135)
    c: Coincident(g135,g136)
    c: Coincident(g136,g137)
    c: Coincident(g137,g138)
    c: Coincident(g138,g139)
    c: Coincident(g139,g140)
    c: Coincident(g140,g141)
    c: Coincident(g141,g142)
    c: Coincident(g142,g143)
    c: Coincident(g143,g144)
    c: Coincident(g144,g145)
    c: Coincident(g145,g146)
    c: Coincident(g146,g147)
    c: Coincident(g147,g126)
    c: Coincident(g148,g149)
    c: Coincident(g149,g150)
    c: Coincident(g150,g151)
    c: Coincident(g151,g152)
    c: Coincident(g152,g153)
    c: Coincident(g153,g154)
    c: Coincident(g154,g155)
    c: Coincident(g155,g156)
    c: Coincident(g156,g157)
    c: Coincident(g157,g158)
    c: Coincident(g158,g159)
    c: Coincident(g159,g148)
    c: Coincident(g160,g161)
    c: Coincident(g161,g162)
    c: Coincident(g162,g163)
    c: Coincident(g163,g164)
    c: Coincident(g164,g165)
    c: Coincident(g165,g166)
    c: Coincident(g166,g167)
    c: Coincident(g167,g160)
    c: Coincident(g168,g169)
    c: Coincident(g169,g170)
    c: Coincident(g170,g171)
    c: Coincident(g171,g168)
    c: Coincident(g172,g173)
    c: Coincident(g173,g174)
    c: Coincident(g174,g175)
    c: Coincident(g175,g172)
    c: Coincident(g176,g177)
    c: Coincident(g177,g178)
    c: Coincident(g178,g179)
    c: Coincident(g179,g176)
    c: Coincident(g180,g181)
    c: Coincident(g181,g182)
    c: Coincident(g182,g183)
    c: Coincident(g183,g180)
    c: Coincident(g184,g185)
    c: Coincident(g185,g186)
    c: Coincident(g186,g187)
    c: Coincident(g187,g184)
    c: Coincident(g188,g189)
    c: Coincident(g189,g190)
    c: Coincident(g190,g191)
    c: Coincident(g191,g188)
    c: Coincident(g192,g193)
    c: Coincident(g193,g194)
    c: Coincident(g194,g195)
    c: Coincident(g195,g192)
    c: Coincident(g196,g197)
    c: Coincident(g197,g198)
    c: Coincident(g198,g199)
    c: Coincident(g199,g196)
    c: Coincident(g200,g201)
    c: Coincident(g201,g202)
    c: Coincident(g202,g203)
    c: Coincident(g203,g200)
    c: Coincident(g204,g205)
    c: Coincident(g205,g206)
    c: Coincident(g206,g207)
    c: Coincident(g207,g204)
    c: Coincident(g208,g209)
    c: Coincident(g209,g210)
    c: Coincident(g210,g211)
    c: Coincident(g211,g208)
    c: Coincident(g212,g213)
    c: Coincident(g213,g214)
    c: Coincident(g214,g215)
    c: Coincident(g215,g212)
    c: Coincident(g216,g217)
    c: Coincident(g217,g218)
    c: Coincident(g218,g219)
    c: Coincident(g219,g216)
    c: Coincident(g220,g221)
    c: Coincident(g221,g222)
    c: Coincident(g222,g223)
    c: Coincident(g223,g220)
    c: Coincident(g224,g225)
    c: Coincident(g225,g226)
    c: Coincident(g226,g227)
    c: Coincident(g227,g224)
    c: Coincident(g228,g229)
    c: Coincident(g229,g230)
    c: Coincident(g230,g231)
    c: Coincident(g231,g228)
    c: Coincident(g232,g233)
    c: Coincident(g233,g234)
    c: Coincident(g234,g235)
    c: Coincident(g235,g232)
    c: Coincident(g236,g-1)
    c: Radius(g236) = 17.25
    c: PointOnObject(g237,g236)
    c: PointOnObject(g238,g236)
    c: Equal(g240,g239)
    c: Equal(g239,g238)
    c: Equal(g238,g237)
    c: Radius(g237) = 0.4
    c: PointOnObject(g238,g-1)
    c: Symmetric(g239,g237,g-1)
    c: Symmetric(g239,g240,g-2)
    c: Coincident(g241,g237)
    c: Coincident(g241,g-1)
    c: Angle(g-2,g241) = 0.523599
    c: PointOnObject(g242,g236)
    c: PointOnObject(g242,g-2)
    c: Radius(g242) = 1.2
FEATURE [Part::Extrusion] Extrude012
  Base = -> Sketch066
  Dir = (0,0,1)
  DirMode = 2
  FaceMakerClass = Part::FaceMakerBullseye
  LengthFwd = -0.9
  LengthRev = 0
  Solid = true
  Symmetric = false
FEATURE [Sketcher::SketchObject] Sketch067
  sketch-geometry (10):
    g0: Circle [constr] CenterX=0 CenterY=0 CenterZ=0 NormalX=0 NormalY=0 NormalZ=1 AngleXU=0 Radius=19.5
    g1: LineSegment [constr] StartX=0 StartY=0 StartZ=0 EndX=19.4998 EndY=0.0850845 EndZ=0
    g2: LineSegment [constr] StartX=0 StartY=0 StartZ=0 EndX=18.8356 EndY=5.04697 EndZ=0
    g3: GeomPoint X=19.3998 Y=0.0846482 Z=0
    g4: LineSegment StartX=19.6985 StartY=0.171906 StartZ=0 EndX=19.7 EndY=0.00174531 EndZ=0
    g5: LineSegment StartX=19.7 StartY=0.00174531 StartZ=0 EndX=19.5 EndY=0 EndZ=0
    g6: LineSegment StartX=19.6985 StartY=0.171906 StartZ=0 EndX=19.4993 EndY=0.170167 EndZ=0
    g7: LineSegment StartX=19.4993 StartY=0.170167 StartZ=0 EndX=19.3994 EndY=0.169296 EndZ=0
    g8: LineSegment StartX=19.3994 StartY=0.169296 StartZ=0 EndX=19.4002 EndY=0 EndZ=0
    g9: LineSegment StartX=19.4002 StartY=0 StartZ=0 EndX=19.5 EndY=0 EndZ=0
  constraints (27):
    c: Angle(g2) = 0.261799
    c: Angle(g1) = 0.00436332
    c: Coincident(g1,g-1)
    c: PointOnObject(g2,g0)
    c: Radius(g0) = 19.5
    c: Coincident(g2,g-1)
    c: Coincident(g2,g0)
    c: PointOnObject(g6,g0)
    c: PointOnObject(g5,g0)
    c: PointOnObject(g3,g1)
    c: Coincident(g4,g5)
    c: Coincident(g4,g6)
    c: Perpendicular(g4,g6)
    c: Perpendicular(g0,g6)
    c: Perpendicular(g4,g5)
    c: Distance(g5) = 0.2
    c: PointOnObject(g5,g-1)
    c: PointOnObject(g1,g0)
    c: Coincident(g6,g7)
    c: Coincident(g7,g8)
    c: Coincident(g8,g9)
    c: Coincident(g9,g5)
    c: Perpendicular(g0,g7)
    c: Symmetric(g8,g7,g3)
    c: Distance(g3,g1) = 0.1
    c: Perpendicular(g1,g8)
    c: Perpendicular(g0,g9)
FEATURE [Part::FeaturePython] Array014  label="Array016"  # Draft array (typed FeaturePython)
  Angle = 15
  ArrayType = 1
  Axis = (0,0,1)
  Base = -> Sketch067
  Center = (0,0,0)
  Fuse = false
  IntervalAxis = (0,0,0)
  IntervalX = (1,0,0)
  IntervalY = (0,1,0)
  IntervalZ = (0,0,1)
  NumberCircles = 2
  NumberPolar = 15
  NumberX = 1
  NumberY = 1
  NumberZ = 1
  RadialDistance = 1
  Symmetry = 1
  TangentialDistance = 1
FEATURE [Part::Extrusion] Extrude013
  Base = -> Array014
  Dir = (0,0,1)
  DirMode = 2
  FaceMakerClass = Part::FaceMakerBullseye
  LengthFwd = 10
  LengthRev = 0
  Solid = true
  Symmetric = false
FEATURE [Sketcher::SketchObject] Sketch068
  MapMode = 5
  Placement = pos=(0,0,0) rot=(1,0,0;1.5708rad)
  sketch-geometry (12):
    g0: LineSegment StartX=15.6 StartY=2.6 StartZ=0 EndX=15.6 EndY=3.6 EndZ=0
    g1: LineSegment StartX=15.6 StartY=3.6 StartZ=0 EndX=19.5 EndY=2.75 EndZ=0
    g2: LineSegment StartX=19.5 StartY=2.75 StartZ=0 EndX=19.5 EndY=1.5 EndZ=0
    g3: LineSegment StartX=19.5 StartY=1.5 StartZ=0 EndX=17.75 EndY=1.25 EndZ=0
    g4: LineSegment StartX=17.75 StartY=1.25 StartZ=0 EndX=17.75 EndY=0 EndZ=0
    g5: LineSegment StartX=17.75 StartY=0 StartZ=0 EndX=16.75 EndY=0 EndZ=0
    g6: LineSegment StartX=16.75 StartY=2.6 StartZ=0 EndX=15.6 EndY=2.6 EndZ=0
    g7: LineSegment StartX=16.75 StartY=0 StartZ=0 EndX=16.75 EndY=0.5 EndZ=0
    g8: LineSegment StartX=16.75 StartY=0.5 StartZ=0 EndX=17.05 EndY=0.5 EndZ=0
    g9: LineSegment StartX=17.05 StartY=0.5 StartZ=0 EndX=17.05 EndY=0.75 EndZ=0
    g10: LineSegment StartX=17.05 StartY=0.75 StartZ=0 EndX=16.75 EndY=0.75 EndZ=0
    g11: LineSegment StartX=16.75 StartY=0.75 StartZ=0 EndX=16.75 EndY=2.6 EndZ=0
  constraints (37):
    c: Vertical(g0)
    c: Coincident(g0,g1)
    c: Coincident(g1,g2)
    c: Coincident(g2,g3)
    c: Coincident(g3,g4)
    c: Vertical(g4)
    c: Coincident(g4,g5)
    c: Horizontal(g6)
    c: Vertical(g2)
    c: Horizontal(g5)
    c: Coincident(g6,g0)
    c: Coincident(g5,g7)
    c: Vertical(g7)
    c: Coincident(g7,g8)
    c: Horizontal(g8)
    c: Coincident(g8,g9)
    c: Coincident(g9,g10)
    c: Coincident(g10,g11)
    c: Coincident(g11,g6)
    c: Vertical(g11)
    c: Vertical(g9)
    c: Horizontal(g10)
    c: Vertical(g10,g7)
    c: PointOnObject(g4,g-1)
    c: DistanceX(g1) = 19.5
    c: DistanceY(g3,g2) = 0.25
    c: DistanceY(g4,g4) = 1.25
    c: DistanceY(g7,g7) = 0.5
    c: DistanceY(g9,g9) = 0.25
    c: DistanceX(g10,g10) = 0.3
    c: DistanceX(g0) = 15.6
    c: DistanceX(g5,g5) = 1
    c: DistanceX(g10) = 16.75
    c: DistanceY(g0) = 3.6
    c: DistanceY(g0,g0) = 1
    c: DistanceY(g1) = 2.75
    c: Angle(g0,g1) = 1.3562
FEATURE [Part::Revolution] Revolve008
  Angle = 15
  Axis = (0,0,1)
  Base = (0,0,0)
  FaceMakerClass = Part::FaceMakerBullseye
  Solid = true
  Source = -> Sketch068
  Symmetric = false
FEATURE [Part::Cut] Cut009
  Base = -> Revolve008
  Tool = -> Extrude013
FEATURE [Part::FeaturePython] Array015  label="Array017"  # Draft array (typed FeaturePython)
  Angle = 360
  ArrayType = 1
  Axis = (0,0,1)
  Base = -> Cut009
  Center = (0,0,0)
  Fuse = false
  IntervalAxis = (0,0,0)
  IntervalX = (1,0,0)
  IntervalY = (0,1,0)
  IntervalZ = (0,0,1)
  NumberCircles = 2
  NumberPolar = 24
  NumberX = 1
  NumberY = 1
  NumberZ = 1
  RadialDistance = 1
  Symmetry = 1
  TangentialDistance = 1
FEATURE [Part::FeaturePython] Clone001  label="Array015"  # Draft clone (typed FeaturePython)
  AttacherType = Attacher::AttachEngine3D
  Fuse = false
  Objects = -> [Array015]
  Scale = (1,1,1)
FEATURE [Part::MultiCommon] Common
  Placement = pos=(0,0,0.15) rot=(0,0,1;0rad)
  Shapes = -> [Clone001,Extrude012]
FEATURE [Part::MultiFuse] Fusion002  label="Bez9"
  Shapes = -> [Array015,Common]
FEATURE [Sketcher::SketchObject] Sketch069
  MapMode = 5
  Placement = pos=(0,0,0) rot=(1,0,0;1.5708rad)
  sketch-geometry (18):
    g0: LineSegment StartX=15.6 StartY=4.55 StartZ=0 EndX=15.6 EndY=5.45 EndZ=0
    g1: LineSegment StartX=20.45 StartY=5.02472 StartZ=0 EndX=20.45 EndY=1.87528 EndZ=0
    g2: LineSegment StartX=17.75 StartY=1.5 StartZ=0 EndX=17.75 EndY=0 EndZ=0
    g3: LineSegment StartX=17.75 StartY=0 StartZ=0 EndX=16.75 EndY=0 EndZ=0
    g4: LineSegment StartX=16.75 StartY=4.55 StartZ=0 EndX=15.6 EndY=4.55 EndZ=0
    g5: LineSegment StartX=16.75 StartY=0 StartZ=0 EndX=16.75 EndY=0.5 EndZ=0
    g6: LineSegment StartX=16.75 StartY=0.5 StartZ=0 EndX=17.05 EndY=0.5 EndZ=0
    g7: LineSegment StartX=17.05 StartY=0.5 StartZ=0 EndX=17.05 EndY=0.75 EndZ=0
    g8: LineSegment StartX=17.05 StartY=0.75 StartZ=0 EndX=16.75 EndY=0.75 EndZ=0
    g9: LineSegment StartX=16.75 StartY=0.75 StartZ=0 EndX=16.75 EndY=4.55 EndZ=0
    g10: LineSegment StartX=18.95 StartY=5.5 StartZ=0 EndX=18.95 EndY=5.45 EndZ=0
    g11: LineSegment StartX=18.95 StartY=5.45 StartZ=0 EndX=15.6 EndY=5.45 EndZ=0
    g12: LineSegment StartX=18.95 StartY=5.5 StartZ=0 EndX=19.7 EndY=5.5 EndZ=0
    g13: LineSegment StartX=19.7 StartY=5.5 StartZ=0 EndX=19.7 EndY=5.4 EndZ=0
    g14: LineSegment StartX=19.7 StartY=5.4 StartZ=0 EndX=19.8 EndY=5.4 EndZ=0
    g15: LineSegment StartX=19.8 StartY=5.4 StartZ=0 EndX=20.45 EndY=5.02472 EndZ=0
    g16: LineSegment StartX=17.75 StartY=1.5 StartZ=0 EndX=19.8 EndY=1.5 EndZ=0
    g17: LineSegment StartX=19.8 StartY=1.5 StartZ=0 EndX=20.45 EndY=1.87528 EndZ=0
  constraints (54):
    c: Vertical(g0)
    c: Vertical(g2)
    c: Coincident(g2,g3)
    c: Horizontal(g4)
    c: Vertical(g1)
    c: Horizontal(g3)
    c: Coincident(g4,g0)
    c: Coincident(g3,g5)
    c: Vertical(g5)
    c: Coincident(g5,g6)
    c: Horizontal(g6)
    c: Coincident(g6,g7)
    c: Coincident(g7,g8)
    c: Coincident(g8,g9)
    c: Coincident(g9,g4)
    c: Vertical(g9)
    c: Vertical(g7)
    c: Horizontal(g8)
    c: Vertical(g8,g5)
    c: PointOnObject(g2,g-1)
    c: DistanceX(g1) = 20.45
    c: DistanceY(g5,g5) = 0.5
    c: DistanceY(g7,g7) = 0.25
    c: DistanceX(g8,g8) = 0.3
    c: DistanceX(g0) = 15.6
    c: DistanceX(g3,g3) = 1
    c: DistanceX(g8) = 16.75
    c: DistanceY(g0,g0) = 0.9
    c: DistanceY(g10) = 5.5
    c: Vertical(g10)
    c: Coincident(g10,g11)
    c: Horizontal(g11)
    c: DistanceY(g10,g10) = 0.05
    c: Coincident(g0,g11)
    c: DistanceX(g10,g1) = 1.5
    c: DistanceY(g2,g2) = 1.5
    c: Coincident(g10,g12)
    c: Horizontal(g12)
    c: Coincident(g12,g13)
    c: Vertical(g13)
    c: Coincident(g13,g14)
    c: Horizontal(g14)
    c: Coincident(g14,g15)
    c: Coincident(g15,g1)
    c: Equal(g13,g14)
    c: DistanceX(g14,g1) = 0.65
    c: DistanceX(g14,g14) = 0.1
    c: Angle(g15,g1) = 2.0944
    c: Coincident(g2,g16)
    c: Horizontal(g16)
    c: Coincident(g16,g17)
    c: Coincident(g17,g1)
    c: Vertical(g14,g16)
    c: Angle(g1,g17) = 2.0944
FEATURE [Part::Revolution] Revolve009
  Angle = 15
  Axis = (0,0,1)
  Base = (0,0,0)
  FaceMakerClass = Part::FaceMakerBullseye
  Solid = true
  Source = -> Sketch069
  Symmetric = false
FEATURE [Sketcher::SketchObject] Sketch070
  sketch-geometry (13):
    g0: GeomPoint X=20.45 Y=0 Z=0
    g1: Circle [constr] CenterX=0 CenterY=0 CenterZ=0 NormalX=0 NormalY=0 NormalZ=1 AngleXU=0 Radius=20.45
    g2: LineSegment StartX=20.4621 StartY=1.34116 StartZ=0 EndX=20.55 EndY=0 EndZ=0
    g3: LineSegment StartX=20.45 StartY=0 StartZ=0 EndX=20.55 EndY=0 EndZ=0
    g4: LineSegment StartX=20.4621 StartY=1.34116 StartZ=0 EndX=20.4062 EndY=1.33749 EndZ=0
    g5: LineSegment [constr] StartX=20.4062 StartY=1.33749 StartZ=0 EndX=0 EndY=0 EndZ=0
    g6: GeomPoint X=20.449 Y=0.206046 Z=0
    g7: LineSegment [constr] StartX=19.849 StartY=0.2 StartZ=0 EndX=20.449 EndY=0.206046 EndZ=0
    g8: ArcOfCircle CenterX=19.899 CenterY=0.2 CenterZ=0 NormalX=0 NormalY=0 NormalZ=1 AngleXU=0 Radius=0.05 StartAngle=2.67644 EndAngle=4.51904
    g9: ArcOfCircle CenterX=20.4 CenterY=-1.58978e-07 CenterZ=0 NormalX=0 NormalY=0 NormalZ=1 AngleXU=0 Radius=0.05 StartAngle=3.17956e-06 EndAngle=1.37745
    g10: LineSegment StartX=20.4096 StartY=0.0490681 StartZ=0 EndX=19.8894 EndY=0.150932 EndZ=0
    g11: ArcOfCircle CenterX=20.3563 CenterY=1.33422 CenterZ=0 NormalX=0 NormalY=0 NormalZ=1 AngleXU=0 Radius=0.05 StartAngle=5.81803 EndAngle=6.34863
    g12: LineSegment StartX=20.401 StartY=1.3118 StartZ=0 EndX=19.8543 EndY=0.222428 EndZ=0
  constraints (33):
    c: PointOnObject(g0,g-1)
    c: DistanceX(g0) = 20.45
    c: PointOnObject(g0,g1)
    c: Coincident(g3,g0)
    c: Coincident(g3,g2)
    c: Coincident(g-1,g1)
    c: Horizontal(g3)
    c: DistanceX(g3,g3) = 0.1
    c: Coincident(g4,g2)
    c: Coincident(g5,g-1)
    c: PointOnObject(g4,g1)
    c: Parallel(g4,g5)
    c: Perpendicular(g2,g4)
    c: Angle(g-1,g5) = 0.0654498
    c: Coincident(g4,g5)
    c: PointOnObject(g6,g1)
    c: Coincident(g7,g6)
    c: Perpendicular(g1,g7)
    c: DistanceX(g7,g7) = 0.6
    c: PointOnObject(g7,g8)
    c: Radius(g8) = 0.05
    c: Horizontal(g8,g7)
    c: Coincident(g9,g0)
    c: Tangent(g9,g10) = -1.5708
    c: Tangent(g10,g8) = 1.5708
    c: Equal(g9,g8)
    c: Tangent(g9,g1)
    c: Coincident(g11,g4)
    c: Tangent(g11,g1)
    c: Equal(g11,g9)
    c: Tangent(g11,g12) = 1.5708
    c: Tangent(g8,g12) = -1.5708
    c: DistanceY(g7) = 0.2
FEATURE [Part::FeaturePython] Array016  label="Array018"  # Draft array (typed FeaturePython)
  Angle = 11.26
  ArrayType = 1
  Axis = (0,0,1)
  Base = -> Sketch070
  Center = (0,0,0)
  Fuse = false
  IntervalAxis = (0,0,0)
  IntervalX = (1,0,0)
  IntervalY = (0,1,0)
  IntervalZ = (0,0,1)
  NumberPolar = 4
  NumberX = 2
  NumberY = 2
  NumberZ = 1
FEATURE [Part::Extrusion] Extrude014
  Base = -> Array016
  Dir = (0,0,1)
  DirMode = 2
  FaceMakerClass = Part::FaceMakerBullseye
  LengthFwd = 8
  LengthRev = 0
  Solid = true
  Symmetric = false
FEATURE [Part::Cut] Cut010
  Base = -> Revolve009
  Tool = -> Extrude014
FEATURE [Part::FeaturePython] Array017  label="Bez_10_Shark"  # Draft array (typed FeaturePython)
  Angle = 360
  ArrayType = 1
  Axis = (0,0,1)
  Base = -> Cut010
  Center = (0,0,0)
  Fuse = true
  IntervalAxis = (0,0,0)
  IntervalX = (1,0,0)
  IntervalY = (0,1,0)
  IntervalZ = (0,0,1)
  NumberCircles = 2
  NumberPolar = 24
  NumberX = 1
  NumberY = 1
  NumberZ = 1
  RadialDistance = 1
  Symmetry = 1
  TangentialDistance = 1
FEATURE [Sketcher::SketchObject] Sketch071
  sketch-geometry (14):
    g0: GeomPoint X=20.45 Y=0 Z=0
    g1: Circle [constr] CenterX=0 CenterY=0 CenterZ=0 NormalX=0 NormalY=0 NormalZ=1 AngleXU=0 Radius=20.45
    g2: LineSegment StartX=20.6107 StartY=0.899883 StartZ=0 EndX=20.65 EndY=0 EndZ=0
    g3: LineSegment StartX=20.45 StartY=0 StartZ=0 EndX=20.65 EndY=0 EndZ=0
    g4: LineSegment StartX=20.6107 StartY=0.899883 StartZ=0 EndX=20.4305 EndY=0.892016 EndZ=0
    g5: LineSegment [constr] StartX=20.4305 StartY=0.892016 StartZ=0 EndX=0 EndY=0 EndZ=0
    g6: ArcOfCircle CenterX=20.1952 CenterY=0.440661 CenterZ=0 NormalX=0 NormalY=0 NormalZ=1 AngleXU=0 Radius=0.05 StartAngle=2.54288 EndAngle=3.78394
    g7: ArcOfCircle CenterX=20.4 CenterY=-5.00277e-09 CenterZ=0 NormalX=0 NormalY=0 NormalZ=1 AngleXU=0 Radius=0.05 StartAngle=1.00055e-07 EndAngle=0.642343
    g8: LineSegment StartX=20.44 StartY=0.0299536 StartZ=0 EndX=20.1552 EndY=0.410707 EndZ=0
    g9: ArcOfCircle CenterX=20.3806 CenterY=0.889836 CenterZ=0 NormalX=0 NormalY=0 NormalZ=1 AngleXU=0 Radius=0.05 StartAngle=5.68448 EndAngle=6.32682
    g10: LineSegment StartX=20.4219 StartY=0.861657 StartZ=0 EndX=20.1539 EndY=0.46884 EndZ=0
    g11: LineSegment [constr] StartX=20.4451 StartY=0.446114 StartZ=0 EndX=0 EndY=1e-16 EndZ=0
    g12: GeomPoint X=20.1452 Y=0.43957 Z=0
    g13: LineSegment [constr] StartX=20.1952 StartY=0.440661 StartZ=0 EndX=20.1452 EndY=0.43957 EndZ=0
  constraints (34):
    c: PointOnObject(g0,g-1)
    c: DistanceX(g0) = 20.45
    c: PointOnObject(g0,g1)
    c: Coincident(g3,g0)
    c: Coincident(g3,g2)
    c: Coincident(g-1,g1)
    c: Horizontal(g3)
    c: DistanceX(g3,g3) = 0.2
    c: Coincident(g4,g2)
    c: Coincident(g5,g-1)
    c: PointOnObject(g4,g1)
    c: Parallel(g4,g5)
    c: Perpendicular(g2,g4)
    c: Angle(g-1,g5) = 0.0436332
    c: Coincident(g4,g5)
    c: Radius(g6) = 0.05
    c: Coincident(g7,g0)
    c: Tangent(g7,g8) = -1.5708
    c: Tangent(g8,g6) = 1.5708
    c: Equal(g7,g6)
    c: Tangent(g7,g1)
    c: Coincident(g9,g4)
    c: Tangent(g9,g1)
    c: Equal(g9,g7)
    c: Tangent(g9,g10) = 1.5708
    c: Tangent(g6,g10) = -1.5708
    c: PointOnObject(g11,g1)
    c: Coincident(g11,g-1)
    c: PointOnObject(g12,g11)
    c: PointOnObject(g12,g6)
    c: Coincident(g13,g6)
    c: Coincident(g13,g12)
    c: Symmetric(g9,g7,g11)
    c: Distance(g11,g12) = 0.3
FEATURE [Part::FeaturePython] Array019  # Draft array (typed FeaturePython)
  Angle = 12.5
  ArrayType = 1
  Axis = (0,0,1)
  Base = -> Sketch071
  Center = (0,0,0)
  Fuse = false
  IntervalAxis = (0,0,0)
  IntervalX = (1,0,0)
  IntervalY = (0,1,0)
  IntervalZ = (0,0,1)
  NumberPolar = 6
  NumberX = 2
  NumberY = 2
  NumberZ = 1
FEATURE [Part::Extrusion] Extrude015
  Base = -> Array019
  Dir = (0,0,1)
  DirMode = 2
  FaceMakerClass = Part::FaceMakerBullseye
  LengthFwd = 8
  LengthRev = 0
  Solid = true
  Symmetric = false
FEATURE [Sketcher::SketchObject] Sketch072
  MapMode = 5
  Placement = pos=(0,0,0) rot=(1,0,0;1.5708rad)
  sketch-geometry (19):
    g0: LineSegment StartX=15.6 StartY=4.55 StartZ=0 EndX=15.6 EndY=5.45 EndZ=0
    g1: LineSegment StartX=20.45 StartY=5.05 StartZ=0 EndX=20.45 EndY=1.85 EndZ=0
    g2: LineSegment StartX=17.75 StartY=1.5 StartZ=0 EndX=17.75 EndY=0 EndZ=0
    g3: LineSegment StartX=17.75 StartY=0 StartZ=0 EndX=16.75 EndY=0 EndZ=0
    g4: LineSegment StartX=16.75 StartY=4.55 StartZ=0 EndX=15.6 EndY=4.55 EndZ=0
    g5: LineSegment StartX=16.75 StartY=0 StartZ=0 EndX=16.75 EndY=0.5 EndZ=0
    g6: LineSegment StartX=16.75 StartY=0.5 StartZ=0 EndX=17.05 EndY=0.5 EndZ=0
    g7: LineSegment StartX=17.05 StartY=0.5 StartZ=0 EndX=17.05 EndY=0.75 EndZ=0
    g8: LineSegment StartX=17.05 StartY=0.75 StartZ=0 EndX=16.75 EndY=0.75 EndZ=0
    g9: LineSegment StartX=16.75 StartY=0.75 StartZ=0 EndX=16.75 EndY=4.55 EndZ=0
    g10: LineSegment StartX=18.95 StartY=5.5 StartZ=0 EndX=18.95 EndY=5.45 EndZ=0
    g11: LineSegment StartX=18.95 StartY=5.45 StartZ=0 EndX=15.6 EndY=5.45 EndZ=0
    g12: LineSegment StartX=18.95 StartY=5.5 StartZ=0 EndX=19.95 EndY=5.5 EndZ=0
    g13: LineSegment StartX=19.95 StartY=5.5 StartZ=0 EndX=19.95 EndY=5.4 EndZ=0
    g14: LineSegment StartX=19.95 StartY=5.4 StartZ=0 EndX=20.05 EndY=5.4 EndZ=0
    g15: LineSegment StartX=20.05 StartY=5.4 StartZ=0 EndX=20.45 EndY=5.05 EndZ=0
    g16: LineSegment [constr] StartX=20.45 StartY=3.45 StartZ=0 EndX=20.05 EndY=3.45 EndZ=0
    g17: LineSegment StartX=17.75 StartY=1.5 StartZ=0 EndX=20.05 EndY=1.5 EndZ=0
    g18: LineSegment StartX=20.05 StartY=1.5 StartZ=0 EndX=20.45 EndY=1.85 EndZ=0
  constraints (58):
    c: Vertical(g0)
    c: Vertical(g2)
    c: Coincident(g2,g3)
    c: Horizontal(g4)
    c: Vertical(g1)
    c: Horizontal(g3)
    c: Coincident(g4,g0)
    c: Coincident(g3,g5)
    c: Vertical(g5)
    c: Coincident(g5,g6)
    c: Horizontal(g6)
    c: Coincident(g6,g7)
    c: Coincident(g7,g8)
    c: Coincident(g8,g9)
    c: Coincident(g9,g4)
    c: Vertical(g9)
    c: Vertical(g7)
    c: Horizontal(g8)
    c: Vertical(g8,g5)
    c: PointOnObject(g2,g-1)
    c: DistanceX(g1) = 20.45
    c: DistanceY(g5,g5) = 0.5
    c: DistanceY(g7,g7) = 0.25
    c: DistanceX(g8,g8) = 0.3
    c: DistanceX(g0) = 15.6
    c: DistanceX(g3,g3) = 1
    c: DistanceX(g8) = 16.75
    c: DistanceY(g0,g0) = 0.9
    c: DistanceY(g10) = 5.5
    c: Vertical(g10)
    c: Coincident(g10,g11)
    c: Horizontal(g11)
    c: DistanceY(g10,g10) = 0.05
    c: Coincident(g0,g11)
    c: DistanceX(g10,g1) = 1.5
    c: DistanceY(g2,g2) = 1.5
    c: Coincident(g10,g12)
    c: Horizontal(g12)
    c: Coincident(g12,g13)
    c: Vertical(g13)
    c: Coincident(g13,g14)
    c: Horizontal(g14)
    c: Coincident(g14,g15)
    c: Coincident(g15,g1)
    c: Equal(g13,g14)
    c: DistanceX(g14,g1) = 0.4
    c: DistanceX(g14,g14) = 0.1
    c: DistanceY(g1,g1) = 3.2
    c: Horizontal(g16)
    c: Symmetric(g1,g1,g16)
    c: Coincident(g2,g17)
    c: Horizontal(g17)
    c: Coincident(g17,g18)
    c: Coincident(g18,g1)
    c: Symmetric(g17,g14,g16)
    c: Vertical(g17,g16)
    c: DistanceY(g1) = 5.05
    c: DistanceY(g1) = 1.85
FEATURE [Part::Revolution] Revolve010
  Angle = 15
  Axis = (0,0,1)
  Base = (0,0,0)
  FaceMakerClass = Part::FaceMakerBullseye
  Solid = true
  Source = -> Sketch072
  Symmetric = false
FEATURE [Part::Cut] Cut011
  Base = -> Revolve010
  Tool = -> Extrude015
FEATURE [Sketcher::SketchObject] Sketch073
  Placement = pos=(0,0,0) rot=(1,0,0;1.5708rad)
  sketch-geometry (34):
    g0: LineSegment StartX=20.45 StartY=2.85 StartZ=0 EndX=20.1606 EndY=2.48085 EndZ=0
    g1: ArcOfCircle CenterX=20.2 CenterY=2.45 CenterZ=0 NormalX=0 NormalY=0 NormalZ=1 AngleXU=0 Radius=0.05 StartAngle=2.47679 EndAngle=3.80639
    g2: LineSegment StartX=20.1606 StartY=2.41915 StartZ=0 EndX=20.45 EndY=2.05 EndZ=0
    g3: LineSegment StartX=20.45 StartY=2.05 StartZ=0 EndX=20.65 EndY=2.05 EndZ=0
    g4: LineSegment StartX=20.65 StartY=2.05 StartZ=0 EndX=20.65 EndY=2.85 EndZ=0
    g5: LineSegment StartX=20.65 StartY=2.85 StartZ=0 EndX=20.45 EndY=2.85 EndZ=0
    g6: LineSegment [constr] StartX=20.2 StartY=2.45 StartZ=0 EndX=20.65 EndY=2.45 EndZ=0
    g7: GeomPoint X=20.15 Y=2.45 Z=0
    g8: GeomPoint X=20.45 Y=2.45 Z=0
    g9: LineSegment StartX=20.45 StartY=3.85 StartZ=0 EndX=20.1606 EndY=3.48085 EndZ=0
    g10: ArcOfCircle CenterX=20.2 CenterY=3.45 CenterZ=0 NormalX=0 NormalY=0 NormalZ=1 AngleXU=0 Radius=0.05 StartAngle=2.47679 EndAngle=3.80639
    g11: LineSegment StartX=20.1606 StartY=3.41915 StartZ=0 EndX=20.45 EndY=3.05 EndZ=0
    g12: LineSegment StartX=20.45 StartY=3.05 StartZ=0 EndX=20.65 EndY=3.05 EndZ=0
    g13: LineSegment StartX=20.65 StartY=3.05 StartZ=0 EndX=20.65 EndY=3.85 EndZ=0
    g14: LineSegment StartX=20.65 StartY=3.85 StartZ=0 EndX=20.45 EndY=3.85 EndZ=0
    g15: LineSegment [constr] StartX=20.2 StartY=3.45 StartZ=0 EndX=20.65 EndY=3.45 EndZ=0
    g16: GeomPoint X=20.15 Y=3.45 Z=0
    g17: GeomPoint X=20.45 Y=3.45 Z=0
    g18: LineSegment [constr] StartX=20.45 StartY=2.85 StartZ=0 EndX=20.45 EndY=3.85 EndZ=0
    g19: LineSegment StartX=20.45 StartY=4.85 StartZ=0 EndX=20.1606 EndY=4.48085 EndZ=0
    g20: ArcOfCircle CenterX=20.2 CenterY=4.45 CenterZ=0 NormalX=0 NormalY=0 NormalZ=1 AngleXU=0 Radius=0.05 StartAngle=2.47679 EndAngle=3.80639
    g21: LineSegment StartX=20.1606 StartY=4.41915 StartZ=0 EndX=20.45 EndY=4.05 EndZ=0
    g22: LineSegment StartX=20.45 StartY=4.05 StartZ=0 EndX=20.65 EndY=4.05 EndZ=0
    g23: LineSegment StartX=20.65 StartY=4.05 StartZ=0 EndX=20.65 EndY=4.85 EndZ=0
    g24: LineSegment StartX=20.65 StartY=4.85 StartZ=0 EndX=20.45 EndY=4.85 EndZ=0
    g25: LineSegment [constr] StartX=20.2 StartY=4.45 StartZ=0 EndX=20.65 EndY=4.45 EndZ=0
    g26: GeomPoint X=20.15 Y=4.45 Z=0
    g27: GeomPoint X=20.45 Y=4.45 Z=0
    g28: LineSegment [constr] StartX=20.45 StartY=3.85 StartZ=0 EndX=20.45 EndY=4.85 EndZ=0
    g29: GeomPoint X=20.45 Y=5.05 Z=0
    g30: GeomPoint X=20.45 Y=1.85 Z=0
    g31: LineSegment [constr] StartX=20.45 StartY=4.85 StartZ=0 EndX=20.45 EndY=5.05 EndZ=0
    g32: LineSegment [constr] StartX=20.45 StartY=1.85 StartZ=0 EndX=20.45 EndY=2.05 EndZ=0
    g33: LineSegment [constr] StartX=20.65 StartY=3.05 StartZ=0 EndX=20.65 EndY=2.85 EndZ=0
  constraints (83):
    c: Tangent(g0,g1) = -1.5708
    c: Tangent(g1,g2) = -1.5708
    c: Coincident(g2,g3)
    c: Horizontal(g3)
    c: Coincident(g3,g4)
    c: Vertical(g4)
    c: Coincident(g4,g5)
    c: Coincident(g5,g0)
    c: Horizontal(g5)
    c: Coincident(g6,g1)
    c: Horizontal(g6)
    c: Symmetric(g3,g4,g6)
    c: Symmetric(g0,g1,g6)
    c: DistanceX(g5,g5) = 0.2
    c: Radius(g1) = 0.05
    c: PointOnObject(g7,g1)
    c: PointOnObject(g7,g6)
    c: PointOnObject(g8,g6)
    c: Vertical(g8,g0)
    c: DistanceX(g7,g8) = 0.3
    c: DistanceX(g2) = 20.45
    c: Tangent(g9,g10) = -1.5708
    c: Tangent(g10,g11) = -1.5708
    c: Coincident(g11,g12)
    c: Horizontal(g12)
    c: Coincident(g12,g13)
    c: Vertical(g13)
    c: Coincident(g13,g14)
    c: Coincident(g14,g9)
    c: Horizontal(g14)
    c: Coincident(g15,g10)
    c: Horizontal(g15)
    c: Symmetric(g12,g13,g15)
    c: Symmetric(g9,g10,g15)
    c: PointOnObject(g16,g10)
    c: PointOnObject(g16,g15)
    c: PointOnObject(g17,g15)
    c: Vertical(g17,g9)
    c: Coincident(g0,g18)
    c: Coincident(g9,g18)
    c: Angle(g18) = 1.5708
    c: Tangent(g19,g20) = -1.5708
    c: Tangent(g20,g21) = -1.5708
    c: Coincident(g21,g22)
    c: Horizontal(g22)
    c: Coincident(g22,g23)
    c: Vertical(g23)
    c: Coincident(g23,g24)
    c: Coincident(g24,g19)
    c: Horizontal(g24)
    c: Coincident(g25,g20)
    c: Horizontal(g25)
    c: Symmetric(g22,g23,g25)
    c: Symmetric(g19,g20,g25)
    c: PointOnObject(g26,g20)
    c: PointOnObject(g26,g25)
    c: PointOnObject(g27,g25)
    c: Vertical(g27,g19)
    c: Coincident(g9,g28)
    c: Coincident(g19,g28)
    c: Equal(g18,g28)
    c: Parallel(g28,g18)
    c: Equal(g13,g23)
    c: Equal(g23,g4)
    c: Equal(g24,g14)
    c: Equal(g14,g5)
    c: Equal(g20,g10)
    c: Equal(g10,g1)
    c: Vertical(g26,g16)
    c: Vertical(g16,g7)
    c: Vertical(g30,g2)
    c: Vertical(g2,g29)
    c: DistanceY(g30) = 1.85
    c: DistanceY(g29) = 5.05
    c: Coincident(g31,g19)
    c: Coincident(g31,g29)
    c: Coincident(g32,g30)
    c: Coincident(g32,g2)
    c: Coincident(g33,g12)
    c: Coincident(g33,g4)
    c: DistanceY(g13,g22) = 0.2
    c: Equal(g31,g32)
    c: Equal(g33,g32)
FEATURE [Part::Revolution] Revolve011
  Angle = 15
  Axis = (0,0,1)
  Base = (0,0,0)
  FaceMakerClass = Part::FaceMakerBullseye
  Solid = true
  Source = -> Sketch073
  Symmetric = false
FEATURE [Part::Cut] Cut012
  Base = -> Cut011
  Tool = -> Revolve011
FEATURE [Part::FeaturePython] Array020  label="Bez_11_Atlas"  # Draft array (typed FeaturePython)
  Angle = 360
  ArrayType = 1
  Axis = (0,0,1)
  Base = -> Cut012
  Center = (0,0,0)
  Fuse = true
  IntervalAxis = (0,0,0)
  IntervalX = (1,0,0)
  IntervalY = (0,1,0)
  IntervalZ = (0,0,1)
  NumberCircles = 2
  NumberPolar = 24
  NumberX = 1
  NumberY = 1
  NumberZ = 1
  RadialDistance = 1
  Symmetry = 1
  TangentialDistance = 1
FEATURE [Sketcher::SketchObject] Sketch074
  MapMode = 5
  Placement = pos=(0,0,0) rot=(1,0,0;1.5708rad)
  sketch-geometry (16):
    g0: LineSegment StartX=15.6 StartY=3.3 StartZ=0 EndX=15.6 EndY=4.2 EndZ=0
    g1: LineSegment StartX=17.75 StartY=0 StartZ=0 EndX=16.75 EndY=0 EndZ=0
    g2: LineSegment StartX=16.75 StartY=3.3 StartZ=0 EndX=15.6 EndY=3.3 EndZ=0
    g3: LineSegment StartX=16.75 StartY=0 StartZ=0 EndX=16.75 EndY=0.5 EndZ=0
    g4: LineSegment StartX=16.75 StartY=0.5 StartZ=0 EndX=17.05 EndY=0.5 EndZ=0
    g5: LineSegment StartX=17.05 StartY=0.5 StartZ=0 EndX=17.05 EndY=0.75 EndZ=0
    g6: LineSegment StartX=17.05 StartY=0.75 StartZ=0 EndX=16.75 EndY=0.75 EndZ=0
    g7: LineSegment StartX=16.75 StartY=0.75 StartZ=0 EndX=16.75 EndY=3.3 EndZ=0
    g8: LineSegment StartX=17.75 StartY=0 StartZ=0 EndX=19.5 EndY=1.46842 EndZ=0
    g9: LineSegment StartX=19.5 StartY=1.46842 StartZ=0 EndX=19.5 EndY=3.36842 EndZ=0
    g10: LineSegment StartX=18.75 StartY=3.49342 StartZ=0 EndX=15.85 EndY=4.1 EndZ=0
    g11: LineSegment StartX=15.85 StartY=4.1 StartZ=0 EndX=15.85 EndY=4.2 EndZ=0
    g12: LineSegment StartX=15.85 StartY=4.2 StartZ=0 EndX=15.6 EndY=4.2 EndZ=0
    g13: LineSegment StartX=18.75 StartY=3.49342 StartZ=0 EndX=18.75 EndY=3.46842 EndZ=0
    g14: LineSegment StartX=18.75 StartY=3.46842 StartZ=0 EndX=19.4 EndY=3.46842 EndZ=0
    g15: ArcOfCircle CenterX=19.4 CenterY=3.36842 CenterZ=0 NormalX=0 NormalY=0 NormalZ=1 AngleXU=0 Radius=0.1 StartAngle=-1.8e-15 EndAngle=1.5708
  constraints (50):
    c: Vertical(g0)
    c: Horizontal(g2)
    c: Horizontal(g1)
    c: Coincident(g2,g0)
    c: Coincident(g1,g3)
    c: Vertical(g3)
    c: Coincident(g3,g4)
    c: Horizontal(g4)
    c: Coincident(g4,g5)
    c: Coincident(g5,g6)
    c: Coincident(g6,g7)
    c: Coincident(g7,g2)
    c: Vertical(g7)
    c: Vertical(g5)
    c: Horizontal(g6)
    c: Vertical(g6,g3)
    c: PointOnObject(g1,g-1)
    c: DistanceY(g3,g3) = 0.5
    c: DistanceY(g5,g5) = 0.25
    c: DistanceX(g6,g6) = 0.3
    c: DistanceX(g0) = 15.6
    c: DistanceX(g1,g1) = 1
    c: DistanceX(g6) = 16.75
    c: DistanceY(g0,g0) = 0.9
    c: DistanceY(g0) = 4.2
    c: Coincident(g1,g8)
    c: Coincident(g8,g9)
    c: Vertical(g9)
    c: Coincident(g10,g11)
    c: Coincident(g11,g12)
    c: Horizontal(g12)
    c: Vertical(g11)
    c: Coincident(g10,g13)
    c: Coincident(g13,g14)
    c: Horizontal(g14)
    c: Vertical(g13)
    c: DistanceY(g11,g11) = 0.1
    c: Coincident(g12,g0)
    c: DistanceX(g12,g12) = 0.25
    c: DistanceY(g13,g13) = 0.025
    c: Angle(g8) = 0.698132
    c: Tangent(g14,g15) = 1.5708
    c: Tangent(g9,g15) = -1.5708
    c: Radius(g15) = 0.1
    c: DistanceX(g9) = 19.5
    c: DistanceX(g13,g9) = 0.75
    c: DistanceY(g8,g14) = 2
    c: Angle(g0,g10) = 1.3646
    c: DistanceX(g10,g10) = 2.9
    c: DistanceX(g10) = 15.85
FEATURE [Part::Revolution] Revolve012
  Angle = 90
  Axis = (0,0,1)
  Base = (0,0,0)
  FaceMakerClass = Part::FaceMakerBullseye
  Solid = true
  Source = -> Sketch074
  Symmetric = false
FEATURE [Part::FeaturePython] Array  # Draft array (typed FeaturePython)
  Angle = 30
  ArrayType = 1
  Axis = (0,0,1)
  Base = -> Sketch044
  Center = (0,0,0)
  Fuse = false
  IntervalAxis = (0,0,0)
  IntervalX = (1,0,0)
  IntervalY = (0,1,0)
  IntervalZ = (0,0,1)
  NumberPolar = 2
  NumberX = 2
  NumberY = 2
  NumberZ = 1
FEATURE [Part::Extrusion] Extrude
  Base = -> Array
  Dir = (0,0,1)
  DirMode = 2
  FaceMakerClass = Part::FaceMakerBullseye
  LengthFwd = 2.95
  LengthRev = 0
  Solid = true
  Symmetric = false
FEATURE [Part::MultiFuse] Fusion
  Shapes = -> [Extrude,Extrude001,Extrude002]
FEATURE [Part::Cut] Cut
  Base = -> Revolve
  Tool = -> Fusion
FEATURE [Part::Mirroring] Part__Mirroring  label="Cut (Mirror #1)"
  Base = (0,0,0)
  Normal = (0,1,0)
  Source = -> Cut
FEATURE [Part::MultiFuse] Fusion001
  Shapes = -> [Part__Mirroring,Cut]
FEATURE [Part::FeaturePython] Array001  # Draft array (typed FeaturePython)
  Angle = 360
  ArrayType = 1
  Axis = (0,0,1)
  Base = -> Fusion001
  Center = (0,0,0)
  Fuse = true
  IntervalAxis = (0,0,0)
  IntervalX = (1,0,0)
  IntervalY = (0,1,0)
  IntervalZ = (0,0,1)
  NumberPolar = 12
  NumberX = 2
  NumberY = 2
  NumberZ = 1
FEATURE [Part::Cut] Cut001  label="Bezel_1_Vintage"
  Base = -> Array001
  Refine = true
  Tool = -> Extrude003
FEATURE [Part::Cylinder] Cylinder  label="Cylindre"
  Angle = 360
  AttacherType = Attacher::AttachEngine3D
  Height = 5
  Placement = pos=(21.1794,0,1.78127) rot=(0,-1,0;0.698132rad)
  Radius = 0.75
FEATURE [Part::FeaturePython] Array021  # Draft array (typed FeaturePython)
  Angle = 90
  ArrayType = 1
  Axis = (0,0,1)
  Base = -> Cylinder
  Center = (0,0,0)
  Fuse = false
  IntervalAxis = (0,0,0)
  IntervalX = (1,0,0)
  IntervalY = (0,1,0)
  IntervalZ = (0,0,1)
  NumberCircles = 2
  NumberPolar = 15
  NumberX = 1
  NumberY = 1
  NumberZ = 1
  RadialDistance = 1
  Symmetry = 1
  TangentialDistance = 1
FEATURE [Part::Cut] Cut013
  Base = -> Revolve012
  Tool = -> Array021
FEATURE [Part::FeaturePython] Array022  # Draft array (typed FeaturePython)
  Angle = 360
  ArrayType = 1
  Axis = (0,0,1)
  Base = -> Cut013
  Center = (0,0,0)
  Fuse = true
  IntervalAxis = (0,0,0)
  IntervalX = (1,0,0)
  IntervalY = (0,1,0)
  IntervalZ = (0,0,1)
  NumberCircles = 2
  NumberPolar = 4
  NumberX = 1
  NumberY = 1
  NumberZ = 1
  RadialDistance = 1
  Symmetry = 1
  TangentialDistance = 1
FEATURE [Part::Fillet] Fillet003  label="Bez_12"
  Base = -> Array022
  Edges = 2 edges: [Edge3 r=0.07,Edge6 r=0.1]
FEATURE [Part::Cylinder] Cylinder001  label="Cylindre001"
  Angle = 360
  AttacherType = Attacher::AttachEngine3D
  Height = 0.25
  Placement = pos=(0,17.1853,3.75852) rot=(-1,0,0;0.226893rad)
  Radius = 0.9
FEATURE [Part::MultiFuse] Fusion003
  Shapes = -> [Cylinder001,Fillet003]
FEATURE [Part::Fillet] Fillet004  label="Bez12_T_Kom"
  Base = -> Fusion003
  Edges = 1 edges r=0.1: [Edge5]
FEATURE [Sketcher::SketchObject] Sketch075
  sketch-geometry (13):
    g0: Circle [constr] CenterX=0 CenterY=0 CenterZ=0 NormalX=0 NormalY=0 NormalZ=1 AngleXU=0 Radius=20
    g1: LineSegment [constr] StartX=0 StartY=0 StartZ=0 EndX=10 EndY=17.3205 EndZ=0
    g2: LineSegment [constr] StartX=0 StartY=0 StartZ=0 EndX=14.1421 EndY=14.1421 EndZ=0
    g3: LineSegment [constr] StartX=0 StartY=0 StartZ=0 EndX=19.3185 EndY=5.17638 EndZ=0
    g4: ArcOfCircle CenterX=14.1424 CenterY=14.1424 CenterZ=0 NormalX=0 NormalY=0 NormalZ=1 AngleXU=0 Radius=1.00032 StartAngle=2.38153 EndAngle=5.47246
    g5: LineSegment StartX=13.4173 StartY=14.8316 StartZ=0 EndX=13.6769 EndY=15.0664 EndZ=0
    g6: LineSegment StartX=13.6769 StartY=15.0664 StartZ=0 EndX=15.0169 EndY=13.5851 EndZ=0
    g7: LineSegment StartX=15.0169 StartY=13.5851 StartZ=0 EndX=14.8316 EndY=13.4173 EndZ=0
    g8: GeomPoint X=13.435 Y=13.435 Z=0
    g9: ArcOfCircle CenterX=19.3188 CenterY=5.17646 CenterZ=0 NormalX=0 NormalY=0 NormalZ=1 AngleXU=0 Radius=1.00032 StartAngle=1.85793 EndAngle=4.94886
    g10: LineSegment StartX=19.0355 StartY=6.13583 StartZ=0 EndX=19.2799 EndY=6.18838 EndZ=0
    g11: LineSegment StartX=19.2799 StartY=6.18838 StartZ=0 EndX=19.6998 EndY=4.23551 EndZ=0
    g12: LineSegment StartX=19.6998 StartY=4.23551 StartZ=0 EndX=19.5532 EndY=4.20398 EndZ=0
  constraints (39):
    c: Angle(g1) = 1.0472
    c: PointOnObject(g1,g0)
    c: Radius(g0) = 20
    c: Coincident(g1,g-1)
    c: Coincident(g1,g0)
    c: Coincident(g2,g-1)
    c: PointOnObject(g2,g0)
    c: Coincident(g3,g-1)
    c: PointOnObject(g3,g0)
    c: Angle(g3) = 0.261799
    c: Angle(g2,g1) = 0.261799
    c: PointOnObject(g4,g0)
    c: PointOnObject(g4,g0)
    c: Coincident(g5,g6)
    c: Coincident(g6,g7)
    c: Coincident(g7,g4)
    c: Perpendicular(g6,g7)
    c: Coincident(g5,g4)
    c: Perpendicular(g6,g5)
    c: Perpendicular(g0,g7)
    c: PointOnObject(g4,g2)
    c: Distance(g4,g4) = 2
    c: PointOnObject(g8,g4)
    c: PointOnObject(g8,g2)
    c: Distance(g8,g2) = 1
    c: Distance(g7) = 0.25
    c: PointOnObject(g9,g0)
    c: PointOnObject(g9,g0)
    c: Coincident(g10,g11)
    c: Coincident(g11,g12)
    c: Perpendicular(g11,g12)
    c: Coincident(g12,g9)
    c: Perpendicular(g0,g12)
    c: Coincident(g9,g10)
    c: Perpendicular(g11,g10)
    c: PointOnObject(g9,g3)
    c: Equal(g9,g4)
    c: Equal(g11,g6)
    c: Equal(g10,g7)
FEATURE [Sketcher::SketchObject] Sketch076
  MapMode = 5
  Placement = pos=(0,0,0) rot=(1,0,0;1.5708rad)
  sketch-geometry (10):
    g0: LineSegment StartX=15.6 StartY=2.7 StartZ=0 EndX=15.6 EndY=3.6 EndZ=0
    g1: LineSegment StartX=20 StartY=3.6 StartZ=0 EndX=20 EndY=0 EndZ=0
    g2: LineSegment StartX=20 StartY=0 StartZ=0 EndX=16.75 EndY=0 EndZ=0
    g3: LineSegment StartX=16.75 StartY=2.7 StartZ=0 EndX=15.6 EndY=2.7 EndZ=0
    g4: LineSegment StartX=16.75 StartY=0 StartZ=0 EndX=16.75 EndY=0.5 EndZ=0
    g5: LineSegment StartX=16.75 StartY=0.5 StartZ=0 EndX=17.05 EndY=0.5 EndZ=0
    g6: LineSegment StartX=17.05 StartY=0.5 StartZ=0 EndX=17.05 EndY=0.75 EndZ=0
    g7: LineSegment StartX=17.05 StartY=0.75 StartZ=0 EndX=16.75 EndY=0.75 EndZ=0
    g8: LineSegment StartX=16.75 StartY=0.75 StartZ=0 EndX=16.75 EndY=2.7 EndZ=0
    g9: LineSegment StartX=20 StartY=3.6 StartZ=0 EndX=15.6 EndY=3.6 EndZ=0
  constraints (30):
    c: Vertical(g0)
    c: Horizontal(g3)
    c: Vertical(g1)
    c: Horizontal(g2)
    c: Coincident(g3,g0)
    c: Coincident(g2,g4)
    c: Vertical(g4)
    c: Coincident(g4,g5)
    c: Horizontal(g5)
    c: Coincident(g5,g6)
    c: Coincident(g6,g7)
    c: Coincident(g7,g8)
    c: Coincident(g8,g3)
    c: Vertical(g8)
    c: Vertical(g6)
    c: Horizontal(g7)
    c: Vertical(g7,g4)
    c: PointOnObject(g2,g-1)
    c: DistanceX(g1) = 20
    c: DistanceY(g4,g4) = 0.5
    c: DistanceY(g6,g6) = 0.25
    c: DistanceX(g7,g7) = 0.3
    c: DistanceX(g0) = 15.6
    c: DistanceX(g7) = 16.75
    c: DistanceY(g0,g0) = 0.9
    c: DistanceY(g0) = 3.6
    c: Coincident(g2,g1)
    c: Coincident(g9,g1)
    c: Coincident(g9,g0)
    c: Horizontal(g9)
FEATURE [Part::Revolution] Revolve013
  Angle = 60
  Axis = (0,0,1)
  Base = (0,0,0)
  FaceMakerClass = Part::FaceMakerBullseye
  Solid = true
  Source = -> Sketch076
  Symmetric = false
FEATURE [Part::Extrusion] Extrude016
  Base = -> Sketch075
  Dir = (0,0,1)
  DirMode = 2
  FaceMakerClass = Part::FaceMakerBullseye
  LengthFwd = 5
  LengthRev = 0
  Solid = true
  Symmetric = false
FEATURE [Sketcher::SketchObject] Sketch077
  Placement = pos=(0,0,3.6) rot=(0,0,1;0rad)
  sketch-geometry (10):
    g0: Circle [constr] CenterX=0 CenterY=0 CenterZ=0 NormalX=0 NormalY=0 NormalZ=1 AngleXU=0 Radius=20
    g1: LineSegment [constr] StartX=14.1421 StartY=14.1421 StartZ=0 EndX=0 EndY=0 EndZ=0
    g2: LineSegment [constr] StartX=0 StartY=0 StartZ=0 EndX=19.3185 EndY=5.17638 EndZ=0
    g3: ArcOfCircle CenterX=0 CenterY=0 CenterZ=0 NormalX=0 NormalY=0 NormalZ=1 AngleXU=0 Radius=19 StartAngle=0.261799 EndAngle=0.785398
    g4: ArcOfCircle CenterX=14.1421 CenterY=14.1421 CenterZ=0 NormalX=0 NormalY=0 NormalZ=1 AngleXU=0 Radius=1 StartAngle=2.3812 EndAngle=3.92699
    g5: ArcOfCircle CenterX=19.3185 CenterY=5.17638 CenterZ=0 NormalX=0 NormalY=0 NormalZ=1 AngleXU=0 Radius=1 StartAngle=3.40339 EndAngle=4.94919
    g6: LineSegment StartX=13.4176 StartY=14.8313 StartZ=0 EndX=14.7593 EndY=16.3145 EndZ=0
    g7: LineSegment StartX=14.7593 StartY=16.3145 StartZ=0 EndX=21.5084 EndY=4.62472 EndZ=0
    g8: LineSegment StartX=21.5084 StartY=4.62472 StartZ=0 EndX=19.5531 EndY=4.20429 EndZ=0
    g9: LineSegment [constr] StartX=18.1339 StartY=10.4696 StartZ=0 EndX=0 EndY=0 EndZ=0
  constraints (27):
    c: Coincident(g0,g-1)
    c: Radius(g0) = 20
    c: PointOnObject(g1,g0)
    c: Coincident(g2,g-1)
    c: PointOnObject(g2,g0)
    c: Coincident(g1,g-1)
    c: Angle(g-1,g2) = 0.261799
    c: Angle(g2,g1) = 0.523599
    c: Coincident(g3,g-1)
    c: PointOnObject(g5,g0)
    c: PointOnObject(g4,g0)
    c: Tangent(g4,g3) = 1.5708
    c: Tangent(g5,g3) = 1.5708
    c: Coincident(g6,g7)
    c: Coincident(g7,g8)
    c: Coincident(g8,g5)
    c: Coincident(g4,g6)
    c: Perpendicular(g0,g6)
    c: Equal(g4,g5)
    c: Perpendicular(g0,g8)
    c: Distance(g1,g4) = 1
    c: Coincident(g5,g2)
    c: Coincident(g9,g3)
    c: Symmetric(g6,g7,g9)
    c: Symmetric(g3,g3,g9)
    c: Distance(g8) = 2
    c: Distance(g3,g5) = 1
FEATURE [Part::Extrusion] Extrude017
  Base = -> Sketch077
  Dir = (0,0,1)
  DirMode = 2
  FaceMakerClass = Part::FaceMakerBullseye
  LengthFwd = 1
  LengthRev = 0
  Reversed = true
  Solid = true
  Symmetric = false
FEATURE [Part::MultiFuse] Fusion004
  Shapes = -> [Extrude016,Extrude017]
FEATURE [Part::Cut] Cut014
  Base = -> Revolve013
  Tool = -> Fusion004
FEATURE [Part::FeaturePython] Array023  # Draft array (typed FeaturePython)
  Angle = 360
  ArrayType = 1
  Axis = (0,0,1)
  Base = -> Cut014
  Center = (0,0,0)
  Fuse = true
  IntervalAxis = (0,0,0)
  IntervalX = (1,0,0)
  IntervalY = (0,1,0)
  IntervalZ = (0,0,1)
  NumberCircles = 2
  NumberPolar = 6
  NumberX = 1
  NumberY = 1
  NumberZ = 1
  RadialDistance = 1
  Symmetry = 1
  TangentialDistance = 1
FEATURE [Part::Part2DObjectPython] ShapeString002  # Draft 2D object (typed FeaturePython)
  FontFile = <path>
  Placement = pos=(-15.2249,6.27623,0) rot=(0,0,1;1.0472rad)
  Size = 3
  String = 50
  Tracking = 0
FEATURE [Part::Part2DObjectPython] ShapeString004  # Draft 2D object (typed FeaturePython)
  FontFile = <path>
  Placement = pos=(-13.0762,-9.99793,0) rot=(0,0,1;2.0944rad)
  Size = 3
  String = 40
  Tracking = 0
FEATURE [Part::Part2DObjectPython] ShapeString006  # Draft 2D object (typed FeaturePython)
  FontFile = <path>
  Placement = pos=(2.17771,-16.3232,0) rot=(0,0,1;3.14159rad)
  Size = 3
  String = 30
  Tracking = 0
FEATURE [Part::Part2DObjectPython] ShapeString008  # Draft 2D object (typed FeaturePython)
  FontFile = <path>
  Placement = pos=(15.2137,-6.29566,0) rot=(0,0,1;4.18879rad)
  Size = 3
  String = 20
  Tracking = 0
FEATURE [Part::Part2DObjectPython] ShapeString010  # Draft 2D object (typed FeaturePython)
  FontFile = <path>
  Placement = pos=(12.9819,10.1612,0) rot=(0,0,-1;1.0472rad)
  Size = 3
  String = 10
  Tracking = 0
FEATURE [App::DocumentObjectGroup] FcClock
  Group = -> [ShapeString002,ShapeString004,ShapeString006,ShapeString008,ShapeString010]
FEATURE [Sketcher::SketchObject] Sketch080
  Placement = pos=(0,0,3.6) rot=(0,0,1;0.523599rad)
  sketch-geometry (210):
    g0: Circle [constr] CenterX=0 CenterY=0 CenterZ=0 NormalX=0 NormalY=0 NormalZ=1 AngleXU=0 Radius=17.75
    g1: Circle CenterX=0 CenterY=17.75 CenterZ=0 NormalX=0 NormalY=0 NormalZ=1 AngleXU=0 Radius=1.625
    g2: Circle CenterX=0 CenterY=17.75 CenterZ=0 NormalX=0 NormalY=0 NormalZ=1 AngleXU=0 Radius=1
    g3: LineSegment [constr] StartX=0 StartY=0 StartZ=0 EndX=8.875 EndY=15.372 EndZ=0
    g4: LineSegment [constr] StartX=0 StartY=0 StartZ=0 EndX=8.875 EndY=-15.372 EndZ=0
    g5: LineSegment [constr] StartX=0 StartY=0 StartZ=0 EndX=-8.875 EndY=-15.372 EndZ=0
    g6: LineSegment [constr] StartX=0 StartY=0 StartZ=0 EndX=-8.875 EndY=15.372 EndZ=0
    g7: Circle CenterX=8.875 CenterY=15.372 CenterZ=0 NormalX=0 NormalY=0 NormalZ=1 AngleXU=0 Radius=0.5
    g8: Circle CenterX=17.75 CenterY=0 CenterZ=0 NormalX=0 NormalY=0 NormalZ=1 AngleXU=0 Radius=0.5
    g9: Circle CenterX=8.875 CenterY=-15.372 CenterZ=0 NormalX=0 NormalY=0 NormalZ=1 AngleXU=0 Radius=0.5
    g10: Circle CenterX=-8.875 CenterY=-15.372 CenterZ=0 NormalX=0 NormalY=0 NormalZ=1 AngleXU=0 Radius=0.5
    g11: Circle CenterX=-17.75 CenterY=0 CenterZ=0 NormalX=0 NormalY=0 NormalZ=1 AngleXU=0 Radius=0.5
    g12: Circle CenterX=-8.875 CenterY=15.372 CenterZ=0 NormalX=0 NormalY=0 NormalZ=1 AngleXU=0 Radius=0.5
    g13: LineSegment StartX=-15.8494 StartY=6.82508 StartZ=0 EndX=-15.6956 EndY=7.15258 EndZ=0
    g14: BSplineCurve PolesCount=3 KnotsCount=2 Degree=2 IsPeriodic=0
    g15: BSplineCurve PolesCount=3 KnotsCount=2 Degree=2 IsPeriodic=0
    g16: BSplineCurve PolesCount=3 KnotsCount=2 Degree=2 IsPeriodic=0
    g17: BSplineCurve PolesCount=3 KnotsCount=2 Degree=2 IsPeriodic=0
    g18: BSplineCurve PolesCount=3 KnotsCount=2 Degree=2 IsPeriodic=0
    g19: BSplineCurve PolesCount=3 KnotsCount=2 Degree=2 IsPeriodic=0
    g20: BSplineCurve PolesCount=3 KnotsCount=2 Degree=2 IsPeriodic=0
    g21: LineSegment StartX=-17.0283 StartY=8.20737 StartZ=0 EndX=-16.4609 EndY=7.70475 EndZ=0
    g22: LineSegment StartX=-16.4697 StartY=9.17489 StartZ=0 EndX=-17.0283 EndY=8.20737 EndZ=0
    g23: LineSegment StartX=-16.7521 StartY=9.33795 StartZ=0 EndX=-16.4697 EndY=9.17489 EndZ=0
    g24: LineSegment StartX=-17.4483 StartY=8.13213 StartZ=0 EndX=-16.7521 EndY=9.33795 EndZ=0
    g25: LineSegment StartX=-16.3495 StartY=7.18441 StartZ=0 EndX=-17.4483 EndY=8.13213 EndZ=0
    g26: LineSegment StartX=-16.1519 StartY=7.4425 StartZ=0 EndX=-16.3495 EndY=7.18441 EndZ=0
    g27: BSplineCurve PolesCount=3 KnotsCount=2 Degree=2 IsPeriodic=0
    g28: BSplineCurve PolesCount=3 KnotsCount=2 Degree=2 IsPeriodic=0
    g29: BSplineCurve PolesCount=3 KnotsCount=2 Degree=2 IsPeriodic=0
    g30: BSplineCurve PolesCount=3 KnotsCount=2 Degree=2 IsPeriodic=0
    g31: BSplineCurve PolesCount=3 KnotsCount=2 Degree=2 IsPeriodic=0
    g32: BSplineCurve PolesCount=3 KnotsCount=2 Degree=2 IsPeriodic=0
    g33: BSplineCurve PolesCount=3 KnotsCount=2 Degree=2 IsPeriodic=0
    g34: BSplineCurve PolesCount=3 KnotsCount=2 Degree=2 IsPeriodic=0
    g35: BSplineCurve PolesCount=3 KnotsCount=2 Degree=2 IsPeriodic=0
    g36: BSplineCurve PolesCount=3 KnotsCount=2 Degree=2 IsPeriodic=0
    g37: BSplineCurve PolesCount=3 KnotsCount=2 Degree=2 IsPeriodic=0
    g38: BSplineCurve PolesCount=3 KnotsCount=2 Degree=2 IsPeriodic=0
    g39: BSplineCurve PolesCount=3 KnotsCount=2 Degree=2 IsPeriodic=0
    g40: BSplineCurve PolesCount=3 KnotsCount=2 Degree=2 IsPeriodic=0
    g41: BSplineCurve PolesCount=3 KnotsCount=2 Degree=2 IsPeriodic=0
    g42: BSplineCurve PolesCount=3 KnotsCount=2 Degree=2 IsPeriodic=0
    g43: BSplineCurve PolesCount=3 KnotsCount=2 Degree=2 IsPeriodic=0
    g44: BSplineCurve PolesCount=3 KnotsCount=2 Degree=2 IsPeriodic=0
    g45: BSplineCurve PolesCount=3 KnotsCount=2 Degree=2 IsPeriodic=0
    g46: BSplineCurve PolesCount=3 KnotsCount=2 Degree=2 IsPeriodic=0
    g47: BSplineCurve PolesCount=3 KnotsCount=2 Degree=2 IsPeriodic=0
    g48: BSplineCurve PolesCount=3 KnotsCount=2 Degree=2 IsPeriodic=0
    g49: BSplineCurve PolesCount=3 KnotsCount=2 Degree=2 IsPeriodic=0
    g50: BSplineCurve PolesCount=3 KnotsCount=2 Degree=2 IsPeriodic=0
    g51: BSplineCurve PolesCount=3 KnotsCount=2 Degree=2 IsPeriodic=0
    g52: BSplineCurve PolesCount=3 KnotsCount=2 Degree=2 IsPeriodic=0
    g53: BSplineCurve PolesCount=3 KnotsCount=2 Degree=2 IsPeriodic=0
    g54: BSplineCurve PolesCount=3 KnotsCount=2 Degree=2 IsPeriodic=0
    g55: LineSegment StartX=-13.7086 StartY=-8.90243 StartZ=0 EndX=-14.2735 EndY=-9.22855 EndZ=0
    g56: LineSegment StartX=-13.8806 StartY=-8.60457 StartZ=0 EndX=-13.7086 EndY=-8.90243 EndZ=0
    g57: LineSegment StartX=-14.4455 StartY=-8.93068 StartZ=0 EndX=-13.8806 EndY=-8.60457 EndZ=0
    g58: LineSegment StartX=-14.6346 StartY=-8.60303 StartZ=0 EndX=-14.4455 EndY=-8.93068 EndZ=0
    g59: LineSegment StartX=-14.9171 StartY=-8.76608 StartZ=0 EndX=-14.6346 EndY=-8.60303 EndZ=0
    g60: LineSegment StartX=-14.7279 StartY=-9.09374 StartZ=0 EndX=-14.9171 EndY=-8.76608 EndZ=0
    g61: LineSegment StartX=-16.3518 StartY=-10.0313 StartZ=0 EndX=-14.7279 EndY=-9.09374 EndZ=0
    g62: LineSegment StartX=-16.2117 StartY=-10.274 StartZ=0 EndX=-16.3518 EndY=-10.0313 EndZ=0
    g63: LineSegment StartX=-13.9483 StartY=-10.4441 StartZ=0 EndX=-16.2117 EndY=-10.274 EndZ=0
    g64: LineSegment StartX=-13.6658 StartY=-10.281 StartZ=0 EndX=-13.9483 EndY=-10.4441 EndZ=0
    g65: LineSegment StartX=-14.2735 StartY=-9.22855 StartZ=0 EndX=-13.6658 EndY=-10.281 EndZ=0
    g66: LineSegment StartX=-14.5559 StartY=-9.39161 StartZ=0 EndX=-15.6856 EndY=-10.0438 EndZ=0
    g67: LineSegment StartX=-14.1177 StartY=-10.1506 StartZ=0 EndX=-14.5559 EndY=-9.39161 EndZ=0
    g68: LineSegment StartX=-15.6856 StartY=-10.0438 StartZ=0 EndX=-14.1177 EndY=-10.1506 EndZ=0
    g69: BSplineCurve PolesCount=3 KnotsCount=2 Degree=2 IsPeriodic=0
    g70: BSplineCurve PolesCount=3 KnotsCount=2 Degree=2 IsPeriodic=0
    g71: BSplineCurve PolesCount=3 KnotsCount=2 Degree=2 IsPeriodic=0
    g72: BSplineCurve PolesCount=3 KnotsCount=2 Degree=2 IsPeriodic=0
    g73: BSplineCurve PolesCount=3 KnotsCount=2 Degree=2 IsPeriodic=0
    g74: BSplineCurve PolesCount=3 KnotsCount=2 Degree=2 IsPeriodic=0
    g75: BSplineCurve PolesCount=3 KnotsCount=2 Degree=2 IsPeriodic=0
    g76: BSplineCurve PolesCount=3 KnotsCount=2 Degree=2 IsPeriodic=0
    g77: BSplineCurve PolesCount=3 KnotsCount=2 Degree=2 IsPeriodic=0
    g78: BSplineCurve PolesCount=3 KnotsCount=2 Degree=2 IsPeriodic=0
    g79: BSplineCurve PolesCount=3 KnotsCount=2 Degree=2 IsPeriodic=0
    g80: BSplineCurve PolesCount=3 KnotsCount=2 Degree=2 IsPeriodic=0
    g81: BSplineCurve PolesCount=3 KnotsCount=2 Degree=2 IsPeriodic=0
    g82: BSplineCurve PolesCount=3 KnotsCount=2 Degree=2 IsPeriodic=0
    g83: BSplineCurve PolesCount=3 KnotsCount=2 Degree=2 IsPeriodic=0
    g84: BSplineCurve PolesCount=3 KnotsCount=2 Degree=2 IsPeriodic=0
    g85: BSplineCurve PolesCount=3 KnotsCount=2 Degree=2 IsPeriodic=0
    g86: BSplineCurve PolesCount=3 KnotsCount=2 Degree=2 IsPeriodic=0
    g87: BSplineCurve PolesCount=3 KnotsCount=2 Degree=2 IsPeriodic=0
    g88: BSplineCurve PolesCount=3 KnotsCount=2 Degree=2 IsPeriodic=0
    g89: LineSegment StartX=2.01338 StartY=-17.0927 StartZ=0 EndX=1.66943 EndY=-17.1385 EndZ=0
    g90: BSplineCurve PolesCount=3 KnotsCount=2 Degree=2 IsPeriodic=0
    g91: BSplineCurve PolesCount=3 KnotsCount=2 Degree=2 IsPeriodic=0
    g92: BSplineCurve PolesCount=3 KnotsCount=2 Degree=2 IsPeriodic=0
    g93: BSplineCurve PolesCount=3 KnotsCount=2 Degree=2 IsPeriodic=0
    g94: BSplineCurve PolesCount=3 KnotsCount=2 Degree=2 IsPeriodic=0
    g95: BSplineCurve PolesCount=3 KnotsCount=2 Degree=2 IsPeriodic=0
    g96: BSplineCurve PolesCount=3 KnotsCount=2 Degree=2 IsPeriodic=0
    g97: BSplineCurve PolesCount=3 KnotsCount=2 Degree=2 IsPeriodic=0
    g98: BSplineCurve PolesCount=3 KnotsCount=2 Degree=2 IsPeriodic=0
    g99: BSplineCurve PolesCount=3 KnotsCount=2 Degree=2 IsPeriodic=0
    g100: BSplineCurve PolesCount=3 KnotsCount=2 Degree=2 IsPeriodic=0
    g101: BSplineCurve PolesCount=3 KnotsCount=2 Degree=2 IsPeriodic=0
    g102: BSplineCurve PolesCount=3 KnotsCount=2 Degree=2 IsPeriodic=0
    g103: LineSegment StartX=1.63503 StartY=-18.3615 StartZ=0 EndX=1.97898 EndY=-18.4226 EndZ=0
    g104: BSplineCurve PolesCount=3 KnotsCount=2 Degree=2 IsPeriodic=0
    g105: BSplineCurve PolesCount=3 KnotsCount=2 Degree=2 IsPeriodic=0
    g106: BSplineCurve PolesCount=3 KnotsCount=2 Degree=2 IsPeriodic=0
    g107: BSplineCurve PolesCount=3 KnotsCount=2 Degree=2 IsPeriodic=0
    g108: BSplineCurve PolesCount=3 KnotsCount=2 Degree=2 IsPeriodic=0
    g109: BSplineCurve PolesCount=3 KnotsCount=2 Degree=2 IsPeriodic=0
    g110: BSplineCurve PolesCount=3 KnotsCount=2 Degree=2 IsPeriodic=0
    g111: LineSegment StartX=1.33439 StartY=-17.6303 StartZ=0 EndX=1.29618 EndY=-17.9576 EndZ=0
    g112: BSplineCurve PolesCount=3 KnotsCount=2 Degree=2 IsPeriodic=0
    g113: BSplineCurve PolesCount=3 KnotsCount=2 Degree=2 IsPeriodic=0
    g114: BSplineCurve PolesCount=3 KnotsCount=2 Degree=2 IsPeriodic=0
    g115: BSplineCurve PolesCount=3 KnotsCount=2 Degree=2 IsPeriodic=0
    g116: BSplineCurve PolesCount=3 KnotsCount=2 Degree=2 IsPeriodic=0
    g117: BSplineCurve PolesCount=3 KnotsCount=2 Degree=2 IsPeriodic=0
    g118: BSplineCurve PolesCount=3 KnotsCount=2 Degree=2 IsPeriodic=0
    g119: BSplineCurve PolesCount=3 KnotsCount=2 Degree=2 IsPeriodic=0
    g120: BSplineCurve PolesCount=3 KnotsCount=2 Degree=2 IsPeriodic=0
    g121: BSplineCurve PolesCount=3 KnotsCount=2 Degree=2 IsPeriodic=0
    g122: BSplineCurve PolesCount=3 KnotsCount=2 Degree=2 IsPeriodic=0
    g123: BSplineCurve PolesCount=3 KnotsCount=2 Degree=2 IsPeriodic=0
    g124: BSplineCurve PolesCount=3 KnotsCount=2 Degree=2 IsPeriodic=0
    g125: BSplineCurve PolesCount=3 KnotsCount=2 Degree=2 IsPeriodic=0
    g126: BSplineCurve PolesCount=3 KnotsCount=2 Degree=2 IsPeriodic=0
    g127: BSplineCurve PolesCount=3 KnotsCount=2 Degree=2 IsPeriodic=0
    g128: BSplineCurve PolesCount=3 KnotsCount=2 Degree=2 IsPeriodic=0
    g129: BSplineCurve PolesCount=3 KnotsCount=2 Degree=2 IsPeriodic=0
    g130: BSplineCurve PolesCount=3 KnotsCount=2 Degree=2 IsPeriodic=0
    g131: BSplineCurve PolesCount=3 KnotsCount=2 Degree=2 IsPeriodic=0
    g132: BSplineCurve PolesCount=3 KnotsCount=2 Degree=2 IsPeriodic=0
    g133: BSplineCurve PolesCount=3 KnotsCount=2 Degree=2 IsPeriodic=0
    g134: BSplineCurve PolesCount=3 KnotsCount=2 Degree=2 IsPeriodic=0
    g135: BSplineCurve PolesCount=3 KnotsCount=2 Degree=2 IsPeriodic=0
    g136: BSplineCurve PolesCount=3 KnotsCount=2 Degree=2 IsPeriodic=0
    g137: BSplineCurve PolesCount=3 KnotsCount=2 Degree=2 IsPeriodic=0
    g138: BSplineCurve PolesCount=3 KnotsCount=2 Degree=2 IsPeriodic=0
    g139: LineSegment StartX=14.5107 StartY=-8.1654 StartZ=0 EndX=14.2283 EndY=-8.00234 EndZ=0
    g140: LineSegment StartX=15.198 StartY=-6.97502 StartZ=0 EndX=14.5107 EndY=-8.1654 EndZ=0
    g141: BSplineCurve PolesCount=3 KnotsCount=2 Degree=2 IsPeriodic=0
    g142: BSplineCurve PolesCount=3 KnotsCount=2 Degree=2 IsPeriodic=0
    g143: BSplineCurve PolesCount=3 KnotsCount=2 Degree=2 IsPeriodic=0
    g144: BSplineCurve PolesCount=3 KnotsCount=2 Degree=2 IsPeriodic=0
    g145: BSplineCurve PolesCount=3 KnotsCount=2 Degree=2 IsPeriodic=0
    g146: BSplineCurve PolesCount=3 KnotsCount=2 Degree=2 IsPeriodic=0
    g147: BSplineCurve PolesCount=3 KnotsCount=2 Degree=2 IsPeriodic=0
    g148: BSplineCurve PolesCount=3 KnotsCount=2 Degree=2 IsPeriodic=0
    g149: BSplineCurve PolesCount=3 KnotsCount=2 Degree=2 IsPeriodic=0
    g150: LineSegment StartX=16.6394 StartY=-7.73956 StartZ=0 EndX=16.8496 EndY=-7.45198 EndZ=0
    g151: BSplineCurve PolesCount=3 KnotsCount=2 Degree=2 IsPeriodic=0
    g152: BSplineCurve PolesCount=3 KnotsCount=2 Degree=2 IsPeriodic=0
    g153: BSplineCurve PolesCount=3 KnotsCount=2 Degree=2 IsPeriodic=0
    g154: BSplineCurve PolesCount=3 KnotsCount=2 Degree=2 IsPeriodic=0
    g155: BSplineCurve PolesCount=3 KnotsCount=2 Degree=2 IsPeriodic=0
    g156: BSplineCurve PolesCount=3 KnotsCount=2 Degree=2 IsPeriodic=0
    g157: BSplineCurve PolesCount=3 KnotsCount=2 Degree=2 IsPeriodic=0
    g158: BSplineCurve PolesCount=3 KnotsCount=2 Degree=2 IsPeriodic=0
    g159: BSplineCurve PolesCount=3 KnotsCount=2 Degree=2 IsPeriodic=0
    g160: LineSegment StartX=14.2283 StartY=-8.00234 StartZ=0 EndX=15.1544 EndY=-6.39826 EndZ=0
    g161: BSplineCurve PolesCount=3 KnotsCount=2 Degree=2 IsPeriodic=0
    g162: BSplineCurve PolesCount=3 KnotsCount=2 Degree=2 IsPeriodic=0
    g163: BSplineCurve PolesCount=3 KnotsCount=2 Degree=2 IsPeriodic=0
    g164: BSplineCurve PolesCount=3 KnotsCount=2 Degree=2 IsPeriodic=0
    g165: BSplineCurve PolesCount=3 KnotsCount=2 Degree=2 IsPeriodic=0
    g166: BSplineCurve PolesCount=3 KnotsCount=2 Degree=2 IsPeriodic=0
    g167: BSplineCurve PolesCount=3 KnotsCount=2 Degree=2 IsPeriodic=0
    g168: BSplineCurve PolesCount=3 KnotsCount=2 Degree=2 IsPeriodic=0
    g169: BSplineCurve PolesCount=3 KnotsCount=2 Degree=2 IsPeriodic=0
    g170: BSplineCurve PolesCount=3 KnotsCount=2 Degree=2 IsPeriodic=0
    g171: BSplineCurve PolesCount=3 KnotsCount=2 Degree=2 IsPeriodic=0
    g172: BSplineCurve PolesCount=3 KnotsCount=2 Degree=2 IsPeriodic=0
    g173: BSplineCurve PolesCount=3 KnotsCount=2 Degree=2 IsPeriodic=0
    g174: BSplineCurve PolesCount=3 KnotsCount=2 Degree=2 IsPeriodic=0
    g175: BSplineCurve PolesCount=3 KnotsCount=2 Degree=2 IsPeriodic=0
    g176: BSplineCurve PolesCount=3 KnotsCount=2 Degree=2 IsPeriodic=0
    g177: BSplineCurve PolesCount=3 KnotsCount=2 Degree=2 IsPeriodic=0
    g178: BSplineCurve PolesCount=3 KnotsCount=2 Degree=2 IsPeriodic=0
    g179: BSplineCurve PolesCount=3 KnotsCount=2 Degree=2 IsPeriodic=0
    g180: BSplineCurve PolesCount=3 KnotsCount=2 Degree=2 IsPeriodic=0
    g181: LineSegment StartX=13.7112 StartY=8.89802 StartZ=0 EndX=13.5392 EndY=9.19589 EndZ=0
    g182: LineSegment StartX=16.1824 StartY=10.3248 StartZ=0 EndX=13.7112 EndY=8.89802 EndZ=0
    g183: LineSegment StartX=16.0716 StartY=10.5167 StartZ=0 EndX=16.1824 EndY=10.3248 EndZ=0
    g184: BSplineCurve PolesCount=3 KnotsCount=2 Degree=2 IsPeriodic=0
    g185: BSplineCurve PolesCount=3 KnotsCount=2 Degree=2 IsPeriodic=0
    g186: LineSegment StartX=14.7486 StartY=10.6884 StartZ=0 EndX=15.031 EndY=10.8515 EndZ=0
    g187: BSplineCurve PolesCount=3 KnotsCount=2 Degree=2 IsPeriodic=0
    g188: BSplineCurve PolesCount=3 KnotsCount=2 Degree=2 IsPeriodic=0
    g189: LineSegment StartX=13.5392 StartY=9.19589 StartZ=0 EndX=15.4643 EndY=10.3074 EndZ=0
    g190: BSplineCurve PolesCount=3 KnotsCount=2 Degree=2 IsPeriodic=0
    g191: BSplineCurve PolesCount=3 KnotsCount=2 Degree=2 IsPeriodic=0
    g192: BSplineCurve PolesCount=3 KnotsCount=2 Degree=2 IsPeriodic=0
    g193: BSplineCurve PolesCount=3 KnotsCount=2 Degree=2 IsPeriodic=0
    g194: BSplineCurve PolesCount=3 KnotsCount=2 Degree=2 IsPeriodic=0
    g195: BSplineCurve PolesCount=3 KnotsCount=2 Degree=2 IsPeriodic=0
    g196: BSplineCurve PolesCount=3 KnotsCount=2 Degree=2 IsPeriodic=0
    g197: BSplineCurve PolesCount=3 KnotsCount=2 Degree=2 IsPeriodic=0
    g198: BSplineCurve PolesCount=3 KnotsCount=2 Degree=2 IsPeriodic=0
    g199: BSplineCurve PolesCount=3 KnotsCount=2 Degree=2 IsPeriodic=0
    g200: BSplineCurve PolesCount=3 KnotsCount=2 Degree=2 IsPeriodic=0
    g201: BSplineCurve PolesCount=3 KnotsCount=2 Degree=2 IsPeriodic=0
    g202: BSplineCurve PolesCount=3 KnotsCount=2 Degree=2 IsPeriodic=0
    g203: BSplineCurve PolesCount=3 KnotsCount=2 Degree=2 IsPeriodic=0
    g204: BSplineCurve PolesCount=3 KnotsCount=2 Degree=2 IsPeriodic=0
    g205: BSplineCurve PolesCount=3 KnotsCount=2 Degree=2 IsPeriodic=0
    g206: BSplineCurve PolesCount=3 KnotsCount=2 Degree=2 IsPeriodic=0
    g207: BSplineCurve PolesCount=3 KnotsCount=2 Degree=2 IsPeriodic=0
    g208: BSplineCurve PolesCount=3 KnotsCount=2 Degree=2 IsPeriodic=0
    g209: BSplineCurve PolesCount=3 KnotsCount=2 Degree=2 IsPeriodic=0
  constraints (230):
    c: Coincident(g0,g-1)
    c: Radius(g0) = 17.75
    c: PointOnObject(g1,g0)
    c: Coincident(g2,g1)
    c: Radius(g2) = 1
    c: Radius(g1) = 1.625
    c: PointOnObject(g1,g-2)
    c: Coincident(g3,g-1)
    c: PointOnObject(g3,g0)
    c: Coincident(g4,g-1)
    c: PointOnObject(g4,g0)
    c: Coincident(g5,g-1)
    c: PointOnObject(g5,g0)
    c: PointOnObject(g6,g0)
    c: Coincident(g6,g-1)
    c: Angle(g3,g-2) = 0.523599
    c: Angle(g4,g-2) = 2.61799
    c: Angle(g-2,g5) = 2.61799
    c: Angle(g-2,g6) = 0.523599
    c: Coincident(g7,g3)
    c: PointOnObject(g8,g0)
    c: Coincident(g9,g4)
    c: Coincident(g10,g5)
    c: PointOnObject(g11,g0)
    c: Coincident(g12,g6)
    c: Equal(g12,g7)
    c: Equal(g7,g8)
    c: Equal(g8,g11)
    c: Equal(g11,g10)
    c: Equal(g10,g9)
    c: Radius(g9) = 0.5
    c: PointOnObject(g8,g-1)
    c: PointOnObject(g11,g-1)
    c: Coincident(g13,g14)
    c: Coincident(g14,g15)
    c: Coincident(g15,g16)
    c: Coincident(g16,g17)
    c: Coincident(g17,g18)
    c: Coincident(g18,g19)
    c: Coincident(g19,g20)
    c: Coincident(g20,g21)
    c: Coincident(g21,g22)
    c: Coincident(g22,g23)
    c: Coincident(g23,g24)
    c: Coincident(g24,g25)
    c: Coincident(g25,g26)
    c: Coincident(g26,g27)
    c: Coincident(g27,g28)
    c: Coincident(g28,g29)
    c: Coincident(g29,g30)
    c: Coincident(g30,g31)
    c: Coincident(g31,g32)
    c: Coincident(g32,g33)
    c: Coincident(g33,g34)
    c: Coincident(g34,g13)
    c: Coincident(g35,g36)
    c: Coincident(g36,g37)
    c: Coincident(g37,g38)
    c: Coincident(g38,g39)
    c: Coincident(g39,g40)
    c: Coincident(g40,g41)
    c: Coincident(g41,g42)
    c: Coincident(g42,g43)
    c: Coincident(g43,g44)
    c: Coincident(g44,g45)
    c: Coincident(g45,g46)
    c: Coincident(g46,g35)
    c: Coincident(g47,g48)
    c: Coincident(g48,g49)
    c: Coincident(g49,g50)
    c: Coincident(g50,g51)
    c: Coincident(g51,g52)
    c: Coincident(g52,g53)
    c: Coincident(g53,g54)
    c: Coincident(g54,g47)
    c: Coincident(g55,g56)
    c: Coincident(g56,g57)
    c: Coincident(g57,g58)
    c: Coincident(g58,g59)
    c: Coincident(g59,g60)
    c: Coincident(g60,g61)
    c: Coincident(g61,g62)
    c: Coincident(g62,g63)
    c: Coincident(g63,g64)
    c: Coincident(g64,g65)
    c: Coincident(g65,g55)
    c: Coincident(g66,g67)
    c: Coincident(g67,g68)
    c: Coincident(g68,g66)
    c: Coincident(g69,g70)
    c: Coincident(g70,g71)
    c: Coincident(g71,g72)
    c: Coincident(g72,g73)
    c: Coincident(g73,g74)
    c: Coincident(g74,g75)
    c: Coincident(g75,g76)
    c: Coincident(g76,g77)
    c: Coincident(g77,g78)
    c: Coincident(g78,g79)
    c: Coincident(g79,g80)
    c: Coincident(g80,g69)
    c: Coincident(g81,g82)
    c: Coincident(g82,g83)
    c: Coincident(g83,g84)
    c: Coincident(g84,g85)
    c: Coincident(g85,g86)
    c: Coincident(g86,g87)
    c: Coincident(g87,g88)
    c: Coincident(g88,g81)
    c: Coincident(g89,g90)
    c: Coincident(g90,g91)
    c: Coincident(g91,g92)
    c: Coincident(g92,g93)
    c: Coincident(g93,g94)
    c: Coincident(g94,g95)
    c: Coincident(g95,g96)
    c: Coincident(g96,g97)
    c: Coincident(g97,g98)
    c: Coincident(g98,g99)
    c: Coincident(g99,g100)
    c: Coincident(g100,g101)
    c: Coincident(g101,g102)
    c: Coincident(g102,g103)
    c: Coincident(g103,g104)
    c: Coincident(g104,g105)
    c: Coincident(g105,g106)
    c: Coincident(g106,g107)
    c: Coincident(g107,g108)
    c: Coincident(g108,g109)
    c: Coincident(g109,g110)
    c: Coincident(g110,g111)
    c: Coincident(g111,g112)
    c: Coincident(g112,g113)
    c: Coincident(g113,g114)
    c: Coincident(g114,g115)
    c: Coincident(g115,g116)
    c: Coincident(g116,g117)
    c: Coincident(g117,g118)
    c: Coincident(g118,g89)
    c: Coincident(g119,g120)
    c: Coincident(g120,g121)
    c: Coincident(g121,g122)
    c: Coincident(g122,g123)
    c: Coincident(g123,g124)
    c: Coincident(g124,g125)
    c: Coincident(g125,g126)
    c: Coincident(g126,g127)
    c: Coincident(g127,g128)
    c: Coincident(g128,g129)
    c: Coincident(g129,g130)
    c: Coincident(g130,g119)
    c: Coincident(g131,g132)
    c: Coincident(g132,g133)
    c: Coincident(g133,g134)
    c: Coincident(g134,g135)
    c: Coincident(g135,g136)
    c: Coincident(g136,g137)
    c: Coincident(g137,g138)
    c: Coincident(g138,g131)
    c: Coincident(g139,g140)
    c: Coincident(g140,g141)
    c: Coincident(g141,g142)
    c: Coincident(g142,g143)
    c: Coincident(g143,g144)
    c: Coincident(g144,g145)
    c: Coincident(g145,g146)
    c: Coincident(g146,g147)
    c: Coincident(g147,g148)
    c: Coincident(g148,g149)
    c: Coincident(g149,g150)
    c: Coincident(g150,g151)
    c: Coincident(g151,g152)
    c: Coincident(g152,g153)
    c: Coincident(g153,g154)
    c: Coincident(g154,g155)
    c: Coincident(g155,g156)
    c: Coincident(g156,g157)
    c: Coincident(g157,g158)
    c: Coincident(g158,g159)
    c: Coincident(g159,g160)
    c: Coincident(g160,g139)
    c: Coincident(g161,g162)
    c: Coincident(g162,g163)
    c: Coincident(g163,g164)
    c: Coincident(g164,g165)
    c: Coincident(g165,g166)
    c: Coincident(g166,g167)
    c: Coincident(g167,g168)
    c: Coincident(g168,g169)
    c: Coincident(g169,g170)
    c: Coincident(g170,g171)
    c: Coincident(g171,g172)
    c: Coincident(g172,g161)
    c: Coincident(g173,g174)
    c: Coincident(g174,g175)
    c: Coincident(g175,g176)
    c: Coincident(g176,g177)
    c: Coincident(g177,g178)
    c: Coincident(g178,g179)
    c: Coincident(g179,g180)
    c: Coincident(g180,g173)
    c: Coincident(g181,g182)
    c: Coincident(g182,g183)
    c: Coincident(g183,g184)
    c: Coincident(g184,g185)
    c: Coincident(g185,g186)
    c: Coincident(g186,g187)
    c: Coincident(g187,g188)
    c: Coincident(g188,g189)
    c: Coincident(g189,g181)
    c: Coincident(g190,g191)
    c: Coincident(g191,g192)
    c: Coincident(g192,g193)
    c: Coincident(g193,g194)
    c: Coincident(g194,g195)
    c: Coincident(g195,g196)
    c: Coincident(g196,g197)
    c: Coincident(g197,g198)
    c: Coincident(g198,g199)
    c: Coincident(g199,g200)
    c: Coincident(g200,g201)
    c: Coincident(g201,g190)
    c: Coincident(g202,g203)
    c: Coincident(g203,g204)
    c: Coincident(g204,g205)
    c: Coincident(g205,g206)
    c: Coincident(g206,g207)
    c: Coincident(g207,g208)
    c: Coincident(g208,g209)
    c: Coincident(g209,g202)
FEATURE [Part::Extrusion] Extrude018
  Base = -> Sketch080
  Dir = (0,0,1)
  DirMode = 2
  FaceMakerClass = Part::FaceMakerBullseye
  LengthFwd = 0.15
  LengthRev = 0
  Reversed = true
  Solid = true
  Symmetric = false
FEATURE [Part::Cut] Cut015  label="Bez_13"
  Base = -> Array023
  Tool = -> Extrude018
FEATURE [Sketcher::SketchObject] Sketch081
  sketch-geometry (7):
    g0: Circle [constr] CenterX=0 CenterY=0 CenterZ=0 NormalX=0 NormalY=0 NormalZ=1 AngleXU=0 Radius=19.75
    g1: LineSegment [constr] StartX=0 StartY=0 StartZ=0 EndX=19.3705 EndY=3.85303 EndZ=0
    g2: ArcOfCircle CenterX=19.2567 CenterY=3.83039 CenterZ=0 NormalX=0 NormalY=0 NormalZ=1 AngleXU=0 Radius=0.633951 StartAngle=1.5989 EndAngle=5.07698
    g3: GeomPoint X=18.6349 Y=3.70672 Z=0
    g4: LineSegment StartX=19.6874 StartY=4.56817 StartZ=0 EndX=19.9698 EndY=3.35113 EndZ=0
    g5: LineSegment StartX=19.9698 StartY=3.35113 StartZ=0 EndX=19.4827 EndY=3.23811 EndZ=0
    g6: LineSegment StartX=19.6874 StartY=4.56817 StartZ=0 EndX=19.2389 EndY=4.46409 EndZ=0
  constraints (20):
    c: Angle(g1) = 0.19635
    c: Coincident(g1,g-1)
    c: PointOnObject(g1,g0)
    c: Radius(g0) = 19.75
    c: PointOnObject(g2,g0)
    c: PointOnObject(g2,g0)
    c: PointOnObject(g3,g1)
    c: PointOnObject(g3,g2)
    c: Distance(g3,g1) = 0.75
    c: Coincident(g4,g5)
    c: Coincident(g5,g2)
    c: Coincident(g4,g6)
    c: Coincident(g6,g2)
    c: Perpendicular(g4,g6)
    c: Perpendicular(g0,g6)
    c: Perpendicular(g4,g5)
    c: Distance(g5) = 0.5
    c: Distance(g2,g2) = 1.25
    c: PointOnObject(g2,g1)
    c: Coincident(g0,g-1)
FEATURE [Part::FeaturePython] Array024  # Draft array (typed FeaturePython)
  Angle = 360
  ArrayType = 1
  Axis = (0,0,1)
  Base = -> Sketch081
  Center = (0,0,0)
  Fuse = false
  IntervalAxis = (0,0,0)
  IntervalX = (1,0,0)
  IntervalY = (0,1,0)
  IntervalZ = (0,0,1)
  NumberPolar = 32
  NumberX = 2
  NumberY = 2
  NumberZ = 1
FEATURE [Part::Extrusion] Extrude019
  Base = -> Array024
  Dir = (0,0,1)
  DirMode = 2
  FaceMakerClass = Part::FaceMakerBullseye
  LengthFwd = 4
  LengthRev = 0
  Placement = pos=(0,0,0) rot=(0,0,1;0.098175rad)
  Solid = true
  Symmetric = false
FEATURE [Sketcher::SketchObject] Sketch082
  MapMode = 5
  Placement = pos=(0,0,0) rot=(1,0,0;1.5708rad)
  sketch-geometry (15):
    g0: LineSegment StartX=15.6 StartY=2.9 StartZ=0 EndX=15.6 EndY=3.8 EndZ=0
    g1: LineSegment StartX=16.75 StartY=2.9 StartZ=0 EndX=15.6 EndY=2.9 EndZ=0
    g2: LineSegment StartX=16.75 StartY=0 StartZ=0 EndX=16.75 EndY=0.5 EndZ=0
    g3: LineSegment StartX=16.75 StartY=0.5 StartZ=0 EndX=17.05 EndY=0.5 EndZ=0
    g4: LineSegment StartX=17.05 StartY=0.5 StartZ=0 EndX=17.05 EndY=0.75 EndZ=0
    g5: LineSegment StartX=17.05 StartY=0.75 StartZ=0 EndX=16.75 EndY=0.75 EndZ=0
    g6: LineSegment StartX=16.75 StartY=0.75 StartZ=0 EndX=16.75 EndY=2.9 EndZ=0
    g7: LineSegment StartX=18.45 StartY=3.40361 StartZ=0 EndX=19.75 EndY=3.2 EndZ=0
    g8: LineSegment StartX=18.45 StartY=3.40361 StartZ=0 EndX=18.45 EndY=3.35361 EndZ=0
    g9: LineSegment StartX=18.45 StartY=3.35361 StartZ=0 EndX=15.6 EndY=3.8 EndZ=0
    g10: LineSegment StartX=16.75 StartY=0 StartZ=0 EndX=17.75 EndY=0 EndZ=0
    g11: LineSegment StartX=17.75 StartY=0 StartZ=0 EndX=17.75 EndY=1.7 EndZ=0
    g12: LineSegment StartX=17.75 StartY=1.7 StartZ=0 EndX=18.45 EndY=1.7 EndZ=0
    g13: LineSegment StartX=18.45 StartY=1.7 StartZ=0 EndX=19.75 EndY=1.95 EndZ=0
    g14: LineSegment StartX=19.75 StartY=1.95 StartZ=0 EndX=19.75 EndY=3.2 EndZ=0
  constraints (46):
    c: Vertical(g0)
    c: Horizontal(g1)
    c: Coincident(g1,g0)
    c: Vertical(g2)
    c: Coincident(g2,g3)
    c: Horizontal(g3)
    c: Coincident(g3,g4)
    c: Coincident(g4,g5)
    c: Coincident(g5,g6)
    c: Coincident(g6,g1)
    c: Vertical(g6)
    c: Vertical(g4)
    c: Horizontal(g5)
    c: Vertical(g5,g2)
    c: DistanceX(g7) = 19.75
    c: DistanceY(g2,g2) = 0.5
    c: DistanceY(g4,g4) = 0.25
    c: DistanceX(g5,g5) = 0.3
    c: DistanceX(g0) = 15.6
    c: DistanceX(g5) = 16.75
    c: DistanceY(g0,g0) = 0.9
    c: Coincident(g7,g8)
    c: Vertical(g8)
    c: Coincident(g8,g9)
    c: DistanceY(g8,g8) = 0.05
    c: Coincident(g0,g9)
    c: DistanceY(g0) = 3.8
    c: Angle(g0,g9) = 1.41543
    c: Coincident(g2,g10)
    c: Horizontal(g10)
    c: Coincident(g10,g11)
    c: Vertical(g11)
    c: Coincident(g11,g12)
    c: Horizontal(g12)
    c: Coincident(g12,g13)
    c: Coincident(g13,g14)
    c: Coincident(g14,g7)
    c: Parallel(g7,g9)
    c: DistanceY(g7,g0) = 0.6
    c: DistanceY(g12,g7) = 1.5
    c: Vertical(g14)
    c: PointOnObject(g10,g-1)
    c: DistanceX(g7) = 18.45
    c: DistanceX(g10,g10) = 1
    c: Vertical(g8,g12)
    c: DistanceY(g14,g14) = 1.25
FEATURE [Part::Revolution] Revolve014
  Angle = 180
  Axis = (0,0,1)
  Base = (0,0,0)
  FaceMakerClass = Part::FaceMakerBullseye
  Solid = true
  Source = -> Sketch082
  Symmetric = false
FEATURE [Part::Cut] Cut016
  Base = -> Revolve014
  Tool = -> Extrude019
FEATURE [Part::FeaturePython] Array025  label="temp"  # Draft array (typed FeaturePython)
  Angle = 360
  ArrayType = 1
  Axis = (0,0,1)
  Base = -> Cut016
  Center = (0,0,0)
  Fuse = true
  IntervalAxis = (0,0,0)
  IntervalX = (1,0,0)
  IntervalY = (0,1,0)
  IntervalZ = (0,0,1)
  NumberCircles = 2
  NumberPolar = 2
  NumberX = 1
  NumberY = 1
  NumberZ = 1
  RadialDistance = 1
  Symmetry = 1
  TangentialDistance = 1
FEATURE [Part::Cylinder] Cylinder002  label="Cylindre002"
  Angle = 360
  AttacherType = Attacher::AttachEngine3D
  Height = 0.2
  Placement = pos=(0,17.0334,3.5102) rot=(-1,0,0;0.174533rad)
  Radius = 0.75
FEATURE [Part::MultiFuse] Fusion005
  Shapes = -> [Cylinder002,Array025]
FEATURE [Sketcher::SketchObject] Sketch083
  sketch-geometry (12):
    g0: Circle [constr] CenterX=0 CenterY=0 CenterZ=0 NormalX=0 NormalY=0 NormalZ=1 AngleXU=0 Radius=19.75
    g1: LineSegment [constr] StartX=0 StartY=0 StartZ=0 EndX=19.7229 EndY=1.03364 EndZ=0
    g2: ArcOfCircle CenterX=19.5232 CenterY=1.02317 CenterZ=0 NormalX=0 NormalY=0 NormalZ=1 AngleXU=0 Radius=0.2 StartAngle=5.25185 EndAngle=6.33555
    g3: ArcOfCircle CenterX=19.55 CenterY=0 CenterZ=0 NormalX=0 NormalY=0 NormalZ=1 AngleXU=0 Radius=0.2 StartAngle=0 EndAngle=1.0837
    g4: ArcOfCircle CenterX=19.4433 CenterY=0.509142 CenterZ=0 NormalX=0 NormalY=0 NormalZ=1 AngleXU=0 Radius=0.2 StartAngle=2.11025 EndAngle=4.22529
    g5: LineSegment StartX=19.3406 StartY=0.680739 StartZ=0 EndX=19.6259 EndY=0.85157 EndZ=0
    g6: LineSegment StartX=19.3497 StartY=0.332403 StartZ=0 EndX=19.6436 EndY=0.176739 EndZ=0
    g7: LineSegment [constr] StartX=19.7432 StartY=0.516995 StartZ=0 EndX=0 EndY=0 EndZ=0
    g8: LineSegment StartX=19.7229 StartY=1.03364 StartZ=0 EndX=19.9726 EndY=1.04672 EndZ=0
    g9: LineSegment StartX=19.9726 StartY=1.04672 StartZ=0 EndX=20.0274 EndY=0 EndZ=0
    g10: LineSegment StartX=20.0274 StartY=0 StartZ=0 EndX=19.75 EndY=0 EndZ=0
    g11: GeomPoint X=19.2434 Y=0.503906 Z=0
  constraints (31):
    c: Angle(g1) = 0.0523599
    c: Coincident(g1,g-1)
    c: PointOnObject(g1,g0)
    c: Radius(g0) = 19.75
    c: Coincident(g0,g-1)
    c: PointOnObject(g2,g1)
    c: Coincident(g2,g1)
    c: PointOnObject(g3,g-1)
    c: Tangent(g5,g2) = -1.5708
    c: Tangent(g4,g5) = 1.5708
    c: Tangent(g6,g4) = -1.5708
    c: PointOnObject(g7,g0)
    c: Coincident(g7,g-1)
    c: PointOnObject(g4,g7)
    c: Tangent(g3,g6) = 1.5708
    c: Equal(g2,g3)
    c: Equal(g3,g4)
    c: Symmetric(g3,g2,g7)
    c: Coincident(g8,g9)
    c: PointOnObject(g9,g-1)
    c: Coincident(g9,g10)
    c: Coincident(g10,g3)
    c: Horizontal(g10)
    c: Coincident(g2,g8)
    c: Perpendicular(g0,g8)
    c: Perpendicular(g9,g8)
    c: Distance(g8) = 0.25
    c: PointOnObject(g11,g4)
    c: PointOnObject(g11,g7)
    c: Radius(g4) = 0.2
    c: Distance(g11,g7) = 0.5
FEATURE [Part::FeaturePython] Array026  # Draft array (typed FeaturePython)
  Angle = 12
  ArrayType = 1
  Axis = (0,0,1)
  Base = -> Sketch083
  Center = (0,0,0)
  Fuse = false
  IntervalAxis = (0,0,0)
  IntervalX = (1,0,0)
  IntervalY = (0,1,0)
  IntervalZ = (0,0,1)
  NumberPolar = 5
  NumberX = 2
  NumberY = 2
  NumberZ = 1
FEATURE [Part::Extrusion] Extrude020
  Base = -> Array026
  Dir = (0,0,1)
  DirMode = 2
  FaceMakerClass = Part::FaceMakerBullseye
  LengthFwd = 4
  LengthRev = 0
  Solid = true
  Symmetric = false
FEATURE [Sketcher::SketchObject] Sketch084
  MapMode = 5
  Placement = pos=(0,0,0) rot=(1,0,0;1.5708rad)
  sketch-geometry (12):
    g0: LineSegment StartX=15.6 StartY=2.9 StartZ=0 EndX=15.6 EndY=3.8 EndZ=0
    g1: LineSegment StartX=16.75 StartY=2.9 StartZ=0 EndX=15.6 EndY=2.9 EndZ=0
    g2: LineSegment StartX=16.75 StartY=0 StartZ=0 EndX=16.75 EndY=0.5 EndZ=0
    g3: LineSegment StartX=16.75 StartY=0.5 StartZ=0 EndX=17.05 EndY=0.5 EndZ=0
    g4: LineSegment StartX=17.05 StartY=0.5 StartZ=0 EndX=17.05 EndY=0.75 EndZ=0
    g5: LineSegment StartX=17.05 StartY=0.75 StartZ=0 EndX=16.75 EndY=0.75 EndZ=0
    g6: LineSegment StartX=16.75 StartY=0.75 StartZ=0 EndX=16.75 EndY=2.9 EndZ=0
    g7: LineSegment StartX=16.75 StartY=0 StartZ=0 EndX=17.75 EndY=0 EndZ=0
    g8: LineSegment StartX=17.75 StartY=0 StartZ=0 EndX=17.75 EndY=1.8 EndZ=0
    g9: LineSegment StartX=17.75 StartY=1.8 StartZ=0 EndX=19.75 EndY=1.8 EndZ=0
    g10: LineSegment StartX=19.75 StartY=1.8 StartZ=0 EndX=19.75 EndY=3.3 EndZ=0
    g11: LineSegment StartX=15.6 StartY=3.8 StartZ=0 EndX=19.75 EndY=3.3 EndZ=0
  constraints (36):
    c: Vertical(g0)
    c: Horizontal(g1)
    c: Coincident(g1,g0)
    c: Vertical(g2)
    c: Coincident(g2,g3)
    c: Horizontal(g3)
    c: Coincident(g3,g4)
    c: Coincident(g4,g5)
    c: Coincident(g5,g6)
    c: Coincident(g6,g1)
    c: Vertical(g6)
    c: Vertical(g4)
    c: Horizontal(g5)
    c: Vertical(g5,g2)
    c: DistanceX(g10) = 19.75
    c: DistanceY(g2,g2) = 0.5
    c: DistanceY(g4,g4) = 0.25
    c: DistanceX(g5,g5) = 0.3
    c: DistanceX(g0) = 15.6
    c: DistanceX(g5) = 16.75
    c: DistanceY(g0,g0) = 0.9
    c: DistanceY(g0) = 3.8
    c: Coincident(g2,g7)
    c: Horizontal(g7)
    c: Coincident(g7,g8)
    c: Vertical(g8)
    c: Coincident(g8,g9)
    c: Horizontal(g9)
    c: Vertical(g10)
    c: PointOnObject(g7,g-1)
    c: DistanceX(g7,g7) = 1
    c: Coincident(g11,g0)
    c: Coincident(g11,g10)
    c: Coincident(g9,g10)
    c: DistanceY(g10,g0) = 0.5
    c: DistanceY(g10,g10) = 1.5
FEATURE [Part::Revolution] Revolve015
  Angle = 15
  Axis = (0,0,1)
  Base = (0,0,0)
  FaceMakerClass = Part::FaceMakerBullseye
  Solid = true
  Source = -> Sketch084
  Symmetric = false
FEATURE [Part::Cut] Cut017
  Base = -> Revolve015
  Tool = -> Extrude020
FEATURE [Part::FeaturePython] Array027  label="temp001"  # Draft array (typed FeaturePython)
  Angle = 360
  ArrayType = 1
  Axis = (0,0,1)
  Base = -> Cut017
  Center = (0,0,0)
  Fuse = true
  IntervalAxis = (0,0,0)
  IntervalX = (1,0,0)
  IntervalY = (0,1,0)
  IntervalZ = (0,0,1)
  NumberCircles = 2
  NumberPolar = 24
  NumberX = 1
  NumberY = 1
  NumberZ = 1
  RadialDistance = 1
  Symmetry = 1
  TangentialDistance = 1
FEATURE [Part::Fillet] Fillet005  label="Bez_014"
  Base = -> Fusion005
  Edges = 65 edges r=0.2: [Edge7,Edge88,Edge89,Edge91,Edge92,Edge95,Edge96,Edge99,Edge100,Edge103,Edge104,Edge107,Edge108,Edge111,Edge112,Edge115,Edge116,Edge119,Edge120,Edge123,Edge124,Edge127,Edge128,Edge131,Edge132,Edge135,Edge136,Edge139,Edge140,Edge143,Edge144,Edge147,Edge148,Edge151,Edge153,Edge156,Edge157,Edge160,+27 more]
FEATURE [Sketcher::SketchObject] Sketch087
  Placement = pos=(0,0,3.8) rot=(0,0,1;0rad)
  sketch-geometry (172):
    g0: Circle [constr] CenterX=0 CenterY=0 CenterZ=0 NormalX=0 NormalY=0 NormalZ=1 AngleXU=0 Radius=17.375
    g1: LineSegment [constr] StartX=0 StartY=0 StartZ=0 EndX=8.6875 EndY=15.0472 EndZ=0
    g2: LineSegment [constr] StartX=15.0472 StartY=8.6875 StartZ=0 EndX=0 EndY=0 EndZ=0
    g3: LineSegment [constr] StartX=0 StartY=0 StartZ=0 EndX=15.0472 EndY=-8.6875 EndZ=0
    g4: LineSegment [constr] StartX=8.6875 StartY=-15.0472 StartZ=0 EndX=0 EndY=0 EndZ=0
    g5: LineSegment [constr] StartX=0 StartY=0 StartZ=0 EndX=-8.6875 EndY=-15.0472 EndZ=0
    g6: LineSegment [constr] StartX=0 StartY=0 StartZ=0 EndX=-15.0472 EndY=-8.6875 EndZ=0
    g7: LineSegment [constr] StartX=0 StartY=0 StartZ=0 EndX=-15.0472 EndY=8.6875 EndZ=0
    g8: LineSegment [constr] StartX=-8.6875 StartY=15.0472 StartZ=0 EndX=0 EndY=0 EndZ=0
    g9: LineSegment StartX=8.37051 StartY=13.4982 StartZ=0 EndX=9.87051 EndY=16.0962 EndZ=0
    g10: LineSegment StartX=9.87051 StartY=16.0962 StartZ=0 EndX=9.00449 EndY=16.5962 EndZ=0
    g11: LineSegment StartX=9.00449 StartY=16.5962 StartZ=0 EndX=7.50449 EndY=13.9982 EndZ=0
    g12: LineSegment StartX=7.50449 StartY=13.9982 StartZ=0 EndX=8.37051 EndY=13.4982 EndZ=0
    g13: LineSegment StartX=13.9982 StartY=7.50449 StartZ=0 EndX=16.5962 EndY=9.00449 EndZ=0
    g14: LineSegment StartX=16.5962 StartY=9.00449 StartZ=0 EndX=16.0962 EndY=9.87051 EndZ=0
    g15: LineSegment StartX=16.0962 StartY=9.87051 StartZ=0 EndX=13.4982 EndY=8.37051 EndZ=0
    g16: LineSegment StartX=13.4982 StartY=8.37051 StartZ=0 EndX=13.9982 EndY=7.50449 EndZ=0
    g17: LineSegment StartX=13.4982 StartY=-8.37051 StartZ=0 EndX=16.0962 EndY=-9.87051 EndZ=0
    g18: LineSegment StartX=16.0962 StartY=-9.87051 StartZ=0 EndX=16.5962 EndY=-9.00449 EndZ=0
    g19: LineSegment StartX=16.5962 StartY=-9.00449 StartZ=0 EndX=13.9982 EndY=-7.50449 EndZ=0
    g20: LineSegment StartX=13.9982 StartY=-7.50449 StartZ=0 EndX=13.4982 EndY=-8.37051 EndZ=0
    g21: LineSegment StartX=9.87051 StartY=-16.0962 StartZ=0 EndX=8.37051 EndY=-13.4982 EndZ=0
    g22: LineSegment StartX=8.37051 StartY=-13.4982 StartZ=0 EndX=7.50449 EndY=-13.9982 EndZ=0
    g23: LineSegment StartX=7.50449 StartY=-13.9982 StartZ=0 EndX=9.00449 EndY=-16.5962 EndZ=0
    g24: LineSegment StartX=9.00449 StartY=-16.5962 StartZ=0 EndX=9.87051 EndY=-16.0962 EndZ=0
    g25: LineSegment StartX=-7.50449 StartY=13.9982 StartZ=0 EndX=-9.00449 EndY=16.5962 EndZ=0
    g26: LineSegment StartX=-9.00449 StartY=16.5962 StartZ=0 EndX=-9.87051 EndY=16.0962 EndZ=0
    g27: LineSegment StartX=-9.87051 StartY=16.0962 StartZ=0 EndX=-8.37051 EndY=13.4982 EndZ=0
    g28: LineSegment StartX=-8.37051 StartY=13.4982 StartZ=0 EndX=-7.50449 EndY=13.9982 EndZ=0
    g29: LineSegment StartX=-13.4982 StartY=8.37051 StartZ=0 EndX=-16.0962 EndY=9.87051 EndZ=0
    g30: LineSegment StartX=-16.0962 StartY=9.87051 StartZ=0 EndX=-16.5962 EndY=9.00449 EndZ=0
    g31: LineSegment StartX=-16.5962 StartY=9.00449 StartZ=0 EndX=-13.9982 EndY=7.50449 EndZ=0
    g32: LineSegment StartX=-13.9982 StartY=7.50449 StartZ=0 EndX=-13.4982 EndY=8.37051 EndZ=0
    g33: LineSegment StartX=-16.0962 StartY=-9.87051 StartZ=0 EndX=-13.4982 EndY=-8.37051 EndZ=0
    g34: LineSegment StartX=-13.4982 StartY=-8.37051 StartZ=0 EndX=-13.9982 EndY=-7.50449 EndZ=0
    g35: LineSegment StartX=-13.9982 StartY=-7.50449 StartZ=0 EndX=-16.5962 EndY=-9.00449 EndZ=0
    g36: LineSegment StartX=-16.5962 StartY=-9.00449 StartZ=0 EndX=-16.0962 EndY=-9.87051 EndZ=0
    g37: LineSegment StartX=-9.00449 StartY=-16.5962 StartZ=0 EndX=-7.50449 EndY=-13.9982 EndZ=0
    g38: LineSegment StartX=-7.50449 StartY=-13.9982 StartZ=0 EndX=-8.37051 EndY=-13.4982 EndZ=0
    g39: LineSegment StartX=-8.37051 StartY=-13.4982 StartZ=0 EndX=-9.87051 EndY=-16.0962 EndZ=0
    g40: LineSegment StartX=-9.87051 StartY=-16.0962 StartZ=0 EndX=-9.00449 EndY=-16.5962 EndZ=0
    g41: LineSegment StartX=-15.8294 StartY=-0.943259 StartZ=0 EndX=-16.5359 EndY=-0.943259 EndZ=0
    g42: LineSegment StartX=-15.8294 StartY=-0.570648 StartZ=0 EndX=-15.8294 EndY=-0.943259 EndZ=0
    g43: LineSegment StartX=-16.5359 StartY=-0.570648 StartZ=0 EndX=-15.8294 EndY=-0.570648 EndZ=0
    g44: LineSegment StartX=-16.5359 StartY=-0.160775 StartZ=0 EndX=-16.5359 EndY=-0.570648 EndZ=0
    g45: LineSegment StartX=-16.8892 StartY=-0.160775 StartZ=0 EndX=-16.5359 EndY=-0.160775 EndZ=0
    g46: LineSegment StartX=-16.8892 StartY=-0.570648 StartZ=0 EndX=-16.8892 EndY=-0.160775 EndZ=0
    g47: LineSegment StartX=-18.9206 StartY=-0.570648 StartZ=0 EndX=-16.8892 EndY=-0.570648 EndZ=0
    g48: LineSegment StartX=-18.9206 StartY=-0.874257 StartZ=0 EndX=-18.9206 EndY=-0.570648 EndZ=0
    g49: LineSegment StartX=-16.8892 StartY=-2.25982 StartZ=0 EndX=-18.9206 EndY=-0.874257 EndZ=0
    g50: LineSegment StartX=-16.5359 StartY=-2.25982 StartZ=0 EndX=-16.8892 EndY=-2.25982 EndZ=0
    g51: LineSegment StartX=-16.5359 StartY=-0.943259 StartZ=0 EndX=-16.5359 EndY=-2.25982 EndZ=0
    g52: LineSegment StartX=-16.8892 StartY=-0.943259 StartZ=0 EndX=-18.3024 EndY=-0.943259 EndZ=0
    g53: LineSegment StartX=-16.8892 StartY=-1.89273 StartZ=0 EndX=-16.8892 EndY=-0.943259 EndZ=0
    g54: LineSegment StartX=-18.3024 StartY=-0.943259 StartZ=0 EndX=-16.8892 EndY=-1.89273 EndZ=0
    g55: LineSegment StartX=-16.7126 StartY=0.247718 StartZ=0 EndX=-16.7457 EndY=0.63827 EndZ=0
    g56: BSplineCurve PolesCount=3 KnotsCount=2 Degree=2 IsPeriodic=0
    g57: BSplineCurve PolesCount=3 KnotsCount=2 Degree=2 IsPeriodic=0
    g58: BSplineCurve PolesCount=3 KnotsCount=2 Degree=2 IsPeriodic=0
    g59: BSplineCurve PolesCount=3 KnotsCount=2 Degree=2 IsPeriodic=0
    g60: BSplineCurve PolesCount=3 KnotsCount=2 Degree=2 IsPeriodic=0
    g61: BSplineCurve PolesCount=3 KnotsCount=2 Degree=2 IsPeriodic=0
    g62: BSplineCurve PolesCount=3 KnotsCount=2 Degree=2 IsPeriodic=0
    g63: LineSegment StartX=-18.5674 StartY=0.905998 StartZ=0 EndX=-17.7628 EndY=0.741773 EndZ=0
    g64: LineSegment StartX=-18.5674 StartY=2.1163 StartZ=0 EndX=-18.5674 EndY=0.905998 EndZ=0
    g65: LineSegment StartX=-18.9206 StartY=2.1163 StartZ=0 EndX=-18.5674 EndY=2.1163 EndZ=0
    g66: LineSegment StartX=-18.9206 StartY=0.607909 StartZ=0 EndX=-18.9206 EndY=2.1163 EndZ=0
    g67: LineSegment StartX=-17.3764 StartY=0.31396 StartZ=0 EndX=-18.9206 EndY=0.607909 EndZ=0
    g68: LineSegment StartX=-17.3308 StartY=0.66311 StartZ=0 EndX=-17.3764 EndY=0.31396 EndZ=0
    g69: BSplineCurve PolesCount=3 KnotsCount=2 Degree=2 IsPeriodic=0
    g70: BSplineCurve PolesCount=3 KnotsCount=2 Degree=2 IsPeriodic=0
    g71: BSplineCurve PolesCount=3 KnotsCount=2 Degree=2 IsPeriodic=0
    g72: BSplineCurve PolesCount=3 KnotsCount=2 Degree=2 IsPeriodic=0
    g73: BSplineCurve PolesCount=3 KnotsCount=2 Degree=2 IsPeriodic=0
    g74: BSplineCurve PolesCount=3 KnotsCount=2 Degree=2 IsPeriodic=0
    g75: BSplineCurve PolesCount=3 KnotsCount=2 Degree=2 IsPeriodic=0
    g76: BSplineCurve PolesCount=3 KnotsCount=2 Degree=2 IsPeriodic=0
    g77: LineSegment StartX=2.18116 StartY=-16.6629 StartZ=0 EndX=1.80855 EndY=-16.7126 EndZ=0
    g78: BSplineCurve PolesCount=3 KnotsCount=2 Degree=2 IsPeriodic=0
    g79: BSplineCurve PolesCount=3 KnotsCount=2 Degree=2 IsPeriodic=0
    g80: BSplineCurve PolesCount=3 KnotsCount=2 Degree=2 IsPeriodic=0
    g81: BSplineCurve PolesCount=3 KnotsCount=2 Degree=2 IsPeriodic=0
    g82: BSplineCurve PolesCount=3 KnotsCount=2 Degree=2 IsPeriodic=0
    g83: BSplineCurve PolesCount=3 KnotsCount=2 Degree=2 IsPeriodic=0
    g84: BSplineCurve PolesCount=3 KnotsCount=2 Degree=2 IsPeriodic=0
    g85: BSplineCurve PolesCount=3 KnotsCount=2 Degree=2 IsPeriodic=0
    g86: BSplineCurve PolesCount=3 KnotsCount=2 Degree=2 IsPeriodic=0
    g87: BSplineCurve PolesCount=3 KnotsCount=2 Degree=2 IsPeriodic=0
    g88: BSplineCurve PolesCount=3 KnotsCount=2 Degree=2 IsPeriodic=0
    g89: BSplineCurve PolesCount=3 KnotsCount=2 Degree=2 IsPeriodic=0
    g90: BSplineCurve PolesCount=3 KnotsCount=2 Degree=2 IsPeriodic=0
    g91: LineSegment StartX=1.77128 StartY=-18.0374 StartZ=0 EndX=2.1439 EndY=-18.1037 EndZ=0
    g92: BSplineCurve PolesCount=3 KnotsCount=2 Degree=2 IsPeriodic=0
    g93: BSplineCurve PolesCount=3 KnotsCount=2 Degree=2 IsPeriodic=0
    g94: BSplineCurve PolesCount=3 KnotsCount=2 Degree=2 IsPeriodic=0
    g95: BSplineCurve PolesCount=3 KnotsCount=2 Degree=2 IsPeriodic=0
    g96: BSplineCurve PolesCount=3 KnotsCount=2 Degree=2 IsPeriodic=0
    g97: BSplineCurve PolesCount=3 KnotsCount=2 Degree=2 IsPeriodic=0
    g98: BSplineCurve PolesCount=3 KnotsCount=2 Degree=2 IsPeriodic=0
    g99: LineSegment StartX=1.44559 StartY=-17.2453 StartZ=0 EndX=1.40419 EndY=-17.5999 EndZ=0
    g100: BSplineCurve PolesCount=3 KnotsCount=2 Degree=2 IsPeriodic=0
    g101: BSplineCurve PolesCount=3 KnotsCount=2 Degree=2 IsPeriodic=0
    g102: BSplineCurve PolesCount=3 KnotsCount=2 Degree=2 IsPeriodic=0
    g103: BSplineCurve PolesCount=3 KnotsCount=2 Degree=2 IsPeriodic=0
    g104: BSplineCurve PolesCount=3 KnotsCount=2 Degree=2 IsPeriodic=0
    g105: BSplineCurve PolesCount=3 KnotsCount=2 Degree=2 IsPeriodic=0
    g106: BSplineCurve PolesCount=3 KnotsCount=2 Degree=2 IsPeriodic=0
    g107: BSplineCurve PolesCount=3 KnotsCount=2 Degree=2 IsPeriodic=0
    g108: BSplineCurve PolesCount=3 KnotsCount=2 Degree=2 IsPeriodic=0
    g109: BSplineCurve PolesCount=3 KnotsCount=2 Degree=2 IsPeriodic=0
    g110: BSplineCurve PolesCount=3 KnotsCount=2 Degree=2 IsPeriodic=0
    g111: BSplineCurve PolesCount=3 KnotsCount=2 Degree=2 IsPeriodic=0
    g112: BSplineCurve PolesCount=3 KnotsCount=2 Degree=2 IsPeriodic=0
    g113: BSplineCurve PolesCount=3 KnotsCount=2 Degree=2 IsPeriodic=0
    g114: BSplineCurve PolesCount=3 KnotsCount=2 Degree=2 IsPeriodic=0
    g115: BSplineCurve PolesCount=3 KnotsCount=2 Degree=2 IsPeriodic=0
    g116: BSplineCurve PolesCount=3 KnotsCount=2 Degree=2 IsPeriodic=0
    g117: BSplineCurve PolesCount=3 KnotsCount=2 Degree=2 IsPeriodic=0
    g118: BSplineCurve PolesCount=3 KnotsCount=2 Degree=2 IsPeriodic=0
    g119: BSplineCurve PolesCount=3 KnotsCount=2 Degree=2 IsPeriodic=0
    g120: BSplineCurve PolesCount=3 KnotsCount=2 Degree=2 IsPeriodic=0
    g121: BSplineCurve PolesCount=3 KnotsCount=2 Degree=2 IsPeriodic=0
    g122: BSplineCurve PolesCount=3 KnotsCount=2 Degree=2 IsPeriodic=0
    g123: BSplineCurve PolesCount=3 KnotsCount=2 Degree=2 IsPeriodic=0
    g124: BSplineCurve PolesCount=3 KnotsCount=2 Degree=2 IsPeriodic=0
    g125: BSplineCurve PolesCount=3 KnotsCount=2 Degree=2 IsPeriodic=0
    g126: BSplineCurve PolesCount=3 KnotsCount=2 Degree=2 IsPeriodic=0
    g127: LineSegment StartX=15.8294 StartY=0.937739 StartZ=0 EndX=15.8294 EndY=1.31035 EndZ=0
    g128: LineSegment StartX=18.9206 StartY=0.937739 StartZ=0 EndX=15.8294 EndY=0.937739 EndZ=0
    g129: LineSegment StartX=18.9206 StartY=1.17787 StartZ=0 EndX=18.9206 EndY=0.937739 EndZ=0
    g130: BSplineCurve PolesCount=3 KnotsCount=2 Degree=2 IsPeriodic=0
    g131: BSplineCurve PolesCount=3 KnotsCount=2 Degree=2 IsPeriodic=0
    g132: LineSegment StartX=17.7725 StartY=2.05557 StartZ=0 EndX=18.1257 EndY=2.05557 EndZ=0
    g133: BSplineCurve PolesCount=3 KnotsCount=2 Degree=2 IsPeriodic=0
    g134: BSplineCurve PolesCount=3 KnotsCount=2 Degree=2 IsPeriodic=0
    g135: LineSegment StartX=15.8294 StartY=1.31035 StartZ=0 EndX=18.2375 EndY=1.31035 EndZ=0
    g136: LineSegment StartX=16.7126 StartY=-0.0434713 StartZ=0 EndX=16.7457 EndY=-0.434023 EndZ=0
    g137: BSplineCurve PolesCount=3 KnotsCount=2 Degree=2 IsPeriodic=0
    g138: BSplineCurve PolesCount=3 KnotsCount=2 Degree=2 IsPeriodic=0
    g139: BSplineCurve PolesCount=3 KnotsCount=2 Degree=2 IsPeriodic=0
    g140: BSplineCurve PolesCount=3 KnotsCount=2 Degree=2 IsPeriodic=0
    g141: BSplineCurve PolesCount=3 KnotsCount=2 Degree=2 IsPeriodic=0
    g142: BSplineCurve PolesCount=3 KnotsCount=2 Degree=2 IsPeriodic=0
    g143: BSplineCurve PolesCount=3 KnotsCount=2 Degree=2 IsPeriodic=0
    g144: LineSegment StartX=18.5674 StartY=-0.701752 StartZ=0 EndX=17.7628 EndY=-0.537527 EndZ=0
    g145: LineSegment StartX=18.5674 StartY=-1.91205 StartZ=0 EndX=18.5674 EndY=-0.701752 EndZ=0
    g146: LineSegment StartX=18.9206 StartY=-1.91205 StartZ=0 EndX=18.5674 EndY=-1.91205 EndZ=0
    g147: LineSegment StartX=18.9206 StartY=-0.403662 StartZ=0 EndX=18.9206 EndY=-1.91205 EndZ=0
    g148: LineSegment StartX=17.3764 StartY=-0.109713 StartZ=0 EndX=18.9206 EndY=-0.403662 EndZ=0
    g149: LineSegment StartX=17.3308 StartY=-0.458864 StartZ=0 EndX=17.3764 EndY=-0.109713 EndZ=0
    g150: BSplineCurve PolesCount=3 KnotsCount=2 Degree=2 IsPeriodic=0
    g151: BSplineCurve PolesCount=3 KnotsCount=2 Degree=2 IsPeriodic=0
    g152: BSplineCurve PolesCount=3 KnotsCount=2 Degree=2 IsPeriodic=0
    g153: BSplineCurve PolesCount=3 KnotsCount=2 Degree=2 IsPeriodic=0
    g154: BSplineCurve PolesCount=3 KnotsCount=2 Degree=2 IsPeriodic=0
    g155: BSplineCurve PolesCount=3 KnotsCount=2 Degree=2 IsPeriodic=0
    g156: BSplineCurve PolesCount=3 KnotsCount=2 Degree=2 IsPeriodic=0
    g157: BSplineCurve PolesCount=3 KnotsCount=2 Degree=2 IsPeriodic=0
    g158: BSplineCurve PolesCount=2 KnotsCount=2 Degree=1 IsPeriodic=0
    g159: BSplineCurve PolesCount=2 KnotsCount=2 Degree=1 IsPeriodic=0
    g160: BSplineCurve PolesCount=2 KnotsCount=2 Degree=1 IsPeriodic=0
    g161: BSplineCurve PolesCount=2 KnotsCount=2 Degree=1 IsPeriodic=0
    g162: BSplineCurve PolesCount=2 KnotsCount=2 Degree=1 IsPeriodic=0
    g163: BSplineCurve PolesCount=2 KnotsCount=2 Degree=1 IsPeriodic=0
    g164: BSplineCurve PolesCount=2 KnotsCount=2 Degree=1 IsPeriodic=0
    g165: BSplineCurve PolesCount=2 KnotsCount=2 Degree=1 IsPeriodic=0
    g166: BSplineCurve PolesCount=2 KnotsCount=2 Degree=1 IsPeriodic=0
    g167: BSplineCurve PolesCount=2 KnotsCount=2 Degree=1 IsPeriodic=0
    g168: BSplineCurve PolesCount=2 KnotsCount=2 Degree=1 IsPeriodic=0
    g169: BSplineCurve PolesCount=2 KnotsCount=2 Degree=1 IsPeriodic=0
    g170: BSplineCurve PolesCount=2 KnotsCount=2 Degree=1 IsPeriodic=0
    g171: BSplineCurve PolesCount=2 KnotsCount=2 Degree=1 IsPeriodic=0
  constraints (245):
    c: Coincident(g0,g-1)
    c: Radius(g0) = 17.375
    c: Coincident(g1,g-1)
    c: PointOnObject(g1,g0)
    c: PointOnObject(g2,g0)
    c: Coincident(g2,g-1)
    c: Coincident(g3,g-1)
    c: PointOnObject(g3,g0)
    c: PointOnObject(g4,g0)
    c: Coincident(g4,g-1)
    c: Coincident(g5,g-1)
    c: PointOnObject(g5,g0)
    c: Coincident(g6,g-1)
    c: PointOnObject(g6,g0)
    c: Coincident(g7,g-1)
    c: PointOnObject(g7,g0)
    c: PointOnObject(g8,g0)
    c: Coincident(g8,g-1)
    c: Angle(g1,g-2) = 0.523599
    c: Angle(g2,g1) = 0.523599
    c: Angle(g3,g-1) = 0.523599
    c: Angle(g4,g3) = 0.523599
    c: Angle(g-2,g5) = 2.61799
    c: Angle(g6,g5) = 0.523599
    c: Angle(g-1,g7) = 2.61799
    c: Angle(g8,g7) = 0.523599
    c: Coincident(g9,g10)
    c: Coincident(g10,g11)
    c: Coincident(g11,g12)
    c: Coincident(g12,g9)
    c: Symmetric(g11,g9,g1)
    c: Symmetric(g10,g9,g1)
    c: Symmetric(g11,g9,g1)
    c: Distance(g9) = 3
    c: Distance(g10) = 1
    c: Coincident(g13,g14)
    c: Coincident(g14,g15)
    c: Coincident(g15,g16)
    c: Coincident(g16,g13)
    c: Equal(g9,g13) = 3.25
    c: Equal(g10,g14) = 1
    c: Symmetric(g15,g13,g2)
    c: Symmetric(g14,g13,g2)
    c: Symmetric(g15,g13,g2)
    c: Coincident(g17,g18)
    c: Coincident(g18,g19)
    c: Coincident(g19,g20)
    c: Coincident(g20,g17)
    c: Symmetric(g19,g17,g3)
    c: Symmetric(g18,g17,g3)
    c: Symmetric(g19,g17,g3)
    c: Equal(g20,g12)
    c: Equal(g9,g19)
    c: Coincident(g21,g22)
    c: Coincident(g22,g23)
    c: Coincident(g23,g24)
    c: Coincident(g24,g21)
    c: Equal(g9,g21) = 3.25
    c: Equal(g10,g22) = 1
    c: Symmetric(g22,g21,g4)
    c: Symmetric(g21,g23,g4)
    c: Symmetric(g23,g21,g4)
    c: Coincident(g25,g26)
    c: Coincident(g26,g27)
    c: Coincident(g27,g28)
    c: Coincident(g28,g25)
    c: Equal(g9,g25) = 3.25
    c: Equal(g10,g26) = 1
    c: Coincident(g29,g30)
    c: Coincident(g30,g31)
    c: Coincident(g31,g32)
    c: Coincident(g32,g29)
    c: Equal(g9,g29) = 3.25
    c: Equal(g10,g30) = 1
    c: Coincident(g33,g34)
    c: Coincident(g34,g35)
    c: Coincident(g35,g36)
    c: Coincident(g36,g33)
    c: Equal(g9,g33) = 3.25
    c: Equal(g10,g34) = 1
    c: Coincident(g37,g38)
    c: Coincident(g38,g39)
    c: Coincident(g39,g40)
    c: Coincident(g40,g37)
    c: Equal(g9,g37) = 3.25
    c: Equal(g10,g38) = 1
    c: Symmetric(g27,g25,g8)
    c: Symmetric(g25,g27,g8)
    c: Symmetric(g26,g25,g8)
    c: Symmetric(g31,g29,g7)
    c: Symmetric(g29,g31,g7)
    c: Symmetric(g30,g29,g7)
    c: Symmetric(g34,g33,g6)
    c: Symmetric(g33,g35,g6)
    c: Symmetric(g35,g33,g6)
    c: Symmetric(g38,g37,g5)
    c: Symmetric(g39,g37,g5)
    c: Symmetric(g39,g37,g5)
    c: Coincident(g41,g42)
    c: Vertical(g42)
    c: Coincident(g42,g43)
    c: Coincident(g43,g44)
    c: Vertical(g44)
    c: Coincident(g44,g45)
    c: Coincident(g45,g46)
    c: Vertical(g46)
    c: Coincident(g46,g47)
    c: Coincident(g47,g48)
    c: Vertical(g48)
    c: Coincident(g48,g49)
    c: Coincident(g49,g50)
    c: Horizontal(g50)
    c: Coincident(g50,g51)
    c: Vertical(g51)
    c: Coincident(g51,g41)
    c: Coincident(g52,g53)
    c: Vertical(g53)
    c: Coincident(g53,g54)
    c: Coincident(g54,g52)
    c: Coincident(g55,g56)
    c: Coincident(g56,g57)
    c: Coincident(g57,g58)
    c: Coincident(g58,g59)
    c: Coincident(g59,g60)
    c: Coincident(g60,g61)
    c: Coincident(g61,g62)
    c: Coincident(g62,g63)
    c: Coincident(g63,g64)
    c: Vertical(g64)
    c: Coincident(g64,g65)
    c: Horizontal(g65)
    c: Coincident(g65,g66)
    c: Vertical(g66)
    c: Coincident(g66,g67)
    c: Coincident(g67,g68)
    c: Coincident(g68,g69)
    c: Coincident(g69,g70)
    c: Coincident(g70,g71)
    c: Coincident(g71,g72)
    c: Coincident(g72,g73)
    c: Coincident(g73,g74)
    c: Coincident(g74,g75)
    c: Coincident(g75,g76)
    c: Coincident(g76,g55)
    c: Coincident(g77,g78)
    c: Coincident(g78,g79)
    c: Coincident(g79,g80)
    c: Coincident(g80,g81)
    c: Coincident(g81,g82)
    c: Coincident(g82,g83)
    c: Coincident(g83,g84)
    c: Coincident(g84,g85)
    c: Coincident(g85,g86)
    c: Coincident(g86,g87)
    c: Coincident(g87,g88)
    c: Coincident(g88,g89)
    c: Coincident(g89,g90)
    c: Coincident(g90,g91)
    c: Coincident(g91,g92)
    c: Coincident(g92,g93)
    c: Coincident(g93,g94)
    c: Coincident(g94,g95)
    c: Coincident(g95,g96)
    c: Coincident(g96,g97)
    c: Coincident(g97,g98)
    c: Coincident(g98,g99)
    c: Coincident(g99,g100)
    c: Coincident(g100,g101)
    c: Coincident(g101,g102)
    c: Coincident(g102,g103)
    c: Coincident(g103,g104)
    c: Coincident(g104,g105)
    c: Coincident(g105,g106)
    c: Coincident(g106,g77)
    c: Coincident(g107,g108)
    c: Coincident(g108,g109)
    c: Coincident(g109,g110)
    c: Coincident(g110,g111)
    c: Coincident(g111,g112)
    c: Coincident(g112,g113)
    c: Coincident(g113,g114)
    c: Coincident(g114,g115)
    c: Coincident(g115,g116)
    c: Coincident(g116,g117)
    c: Coincident(g117,g118)
    c: Coincident(g118,g107)
    c: Coincident(g119,g120)
    c: Coincident(g120,g121)
    c: Coincident(g121,g122)
    c: Coincident(g122,g123)
    c: Coincident(g123,g124)
    c: Coincident(g124,g125)
    c: Coincident(g125,g126)
    c: Coincident(g126,g119)
    c: Vertical(g127)
    c: Coincident(g127,g128)
    c: Coincident(g128,g129)
    c: Vertical(g129)
    c: Coincident(g129,g130)
    c: Coincident(g130,g131)
    c: Coincident(g131,g132)
    c: Horizontal(g132)
    c: Coincident(g132,g133)
    c: Coincident(g133,g134)
    c: Coincident(g134,g135)
    c: Coincident(g135,g127)
    c: Coincident(g136,g137)
    c: Coincident(g137,g138)
    c: Coincident(g138,g139)
    c: Coincident(g139,g140)
    c: Coincident(g140,g141)
    c: Coincident(g141,g142)
    c: Coincident(g142,g143)
    c: Coincident(g143,g144)
    c: Coincident(g144,g145)
    c: Vertical(g145)
    c: Coincident(g145,g146)
    c: Horizontal(g146)
    c: Coincident(g146,g147)
    c: Vertical(g147)
    c: Coincident(g147,g148)
    c: Coincident(g148,g149)
    c: Coincident(g149,g150)
    c: Coincident(g150,g151)
    c: Coincident(g151,g152)
    c: Coincident(g152,g153)
    c: Coincident(g153,g154)
    c: Coincident(g154,g155)
    c: Coincident(g155,g156)
    c: Coincident(g156,g157)
    c: Coincident(g157,g136)
    c: Coincident(g158,g159)
    c: Coincident(g159,g160)
    c: Coincident(g160,g161)
    c: Coincident(g161,g162)
    c: Coincident(g162,g163)
    c: Coincident(g163,g164)
    c: Coincident(g164,g158)
    c: Coincident(g165,g166)
    c: Coincident(g166,g167)
    c: Coincident(g167,g168)
    c: Coincident(g168,g169)
    c: Coincident(g169,g170)
    c: Coincident(g170,g171)
    c: Coincident(g171,g165)
FEATURE [Part::Extrusion] Extrude021
  Base = -> Sketch087
  Dir = (0,0,1)
  DirMode = 2
  FaceMakerClass = Part::FaceMakerBullseye
  LengthFwd = 0.9
  LengthRev = 0
  Reversed = true
  Solid = true
  Symmetric = false
FEATURE [Part::FeaturePython] Clone002  label="temp002"  # Draft clone (typed FeaturePython)
  AttacherType = Attacher::AttachEngine3D
  Fuse = false
  Objects = -> [Array027]
  Placement = pos=(0,0,-0.15) rot=(0,0,1;0rad)
  Scale = (1,1,1)
FEATURE [Part::Cut] Cut018
  Base = -> Extrude021
  Tool = -> Clone002
FEATURE [Part::Cut] Cut019  label="Bez_15"
  Base = -> Array027
  Refine = true
  Tool = -> Cut018
FEATURE [Sketcher::SketchObject] Sketch088
  sketch-geometry (9):
    g0: Circle [constr] CenterX=0 CenterY=0 CenterZ=0 NormalX=0 NormalY=0 NormalZ=1 AngleXU=0 Radius=20
    g1: LineSegment [constr] StartX=0 StartY=0 StartZ=0 EndX=19.981 EndY=0.872388 EndZ=0
    g2: LineSegment [constr] StartX=0 StartY=0 StartZ=0 EndX=19.3185 EndY=5.17638 EndZ=0
    g3: LineSegment StartX=20.1808 StartY=0.881112 StartZ=0 EndX=20.2 EndY=0.00437383 EndZ=0
    g4: LineSegment StartX=20.2 StartY=0.00437383 StartZ=0 EndX=20 EndY=0 EndZ=0
    g5: LineSegment StartX=20.1808 StartY=0.881112 StartZ=0 EndX=19.981 EndY=0.872388 EndZ=0
    g6: LineSegment StartX=19.981 StartY=0.872388 StartZ=0 EndX=19.5953 EndY=0.427572 EndZ=0
    g7: LineSegment StartX=19.5953 StartY=0.427572 StartZ=0 EndX=20 EndY=-1e-16 EndZ=0
    g8: LineSegment [constr] StartX=19.9952 StartY=0.436298 StartZ=0 EndX=0 EndY=0 EndZ=0
  constraints (24):
    c: Angle(g2) = 0.261799
    c: Angle(g1) = 0.0436332
    c: Coincident(g1,g-1)
    c: PointOnObject(g2,g0)
    c: Radius(g0) = 20
    c: Coincident(g2,g-1)
    c: Coincident(g2,g0)
    c: PointOnObject(g4,g0)
    c: Coincident(g3,g4)
    c: Perpendicular(g3,g4)
    c: Distance(g4) = 0.2
    c: PointOnObject(g4,g-1)
    c: Coincident(g3,g5)
    c: Coincident(g5,g1)
    c: Coincident(g5,g6)
    c: Coincident(g6,g7)
    c: Coincident(g7,g4)
    c: Coincident(g8,g-1)
    c: PointOnObject(g6,g8)
    c: Symmetric(g5,g4,g8)
    c: Perpendicular(g0,g5)
    c: Distance(g5) = 0.2
    c: PointOnObject(g8,g0)
    c: Distance(g6,g8) = 0.4
FEATURE [Part::FeaturePython] Array028  # Draft array (typed FeaturePython)
  Angle = 12.5
  ArrayType = 1
  Axis = (0,0,1)
  Base = -> Sketch088
  Center = (0,0,0)
  Fuse = false
  IntervalAxis = (0,0,0)
  IntervalX = (1,0,0)
  IntervalY = (0,1,0)
  IntervalZ = (0,0,1)
  NumberCircles = 2
  NumberPolar = 6
  NumberX = 1
  NumberY = 1
  NumberZ = 1
  RadialDistance = 1
  Symmetry = 1
  TangentialDistance = 1
FEATURE [Sketcher::SketchObject] Sketch089
  MapMode = 5
  Placement = pos=(0,0,0) rot=(1,0,0;1.5708rad)
  sketch-geometry (17):
    g0: LineSegment StartX=15.6 StartY=3 StartZ=0 EndX=15.6 EndY=4 EndZ=0
    g1: LineSegment StartX=17.75 StartY=0 StartZ=0 EndX=16.75 EndY=0 EndZ=0
    g2: LineSegment StartX=16.75 StartY=3 StartZ=0 EndX=15.6 EndY=3 EndZ=0
    g3: LineSegment StartX=16.75 StartY=0 StartZ=0 EndX=16.75 EndY=0.5 EndZ=0
    g4: LineSegment StartX=16.75 StartY=0.5 StartZ=0 EndX=17.05 EndY=0.5 EndZ=0
    g5: LineSegment StartX=17.05 StartY=0.5 StartZ=0 EndX=17.05 EndY=0.75 EndZ=0
    g6: LineSegment StartX=17.05 StartY=0.75 StartZ=0 EndX=16.75 EndY=0.75 EndZ=0
    g7: LineSegment StartX=16.75 StartY=0.75 StartZ=0 EndX=16.75 EndY=3 EndZ=0
    g8: LineSegment StartX=15.6 StartY=4 StartZ=0 EndX=18.5 EndY=3.5 EndZ=0
    g9: LineSegment StartX=18.5 StartY=3.5 StartZ=0 EndX=18.5 EndY=3 EndZ=0
    g10: LineSegment StartX=18.5 StartY=3 StartZ=0 EndX=19 EndY=3 EndZ=0
    g11: LineSegment StartX=19 StartY=3 StartZ=0 EndX=20 EndY=2.25 EndZ=0
    g12: LineSegment StartX=17.75 StartY=0 StartZ=0 EndX=19 EndY=0 EndZ=0
    g13: LineSegment StartX=19 StartY=0 StartZ=0 EndX=20 EndY=0.75 EndZ=0
    g14: LineSegment StartX=20 StartY=0.75 StartZ=0 EndX=20 EndY=2.25 EndZ=0
    g15: GeomPoint X=20 Y=1.5 Z=0
    g16: LineSegment [constr] StartX=20 StartY=1.5 StartZ=0 EndX=19 EndY=1.5 EndZ=0
  constraints (48):
    c: Vertical(g0)
    c: Horizontal(g2)
    c: Horizontal(g1)
    c: Coincident(g2,g0)
    c: Coincident(g1,g3)
    c: Vertical(g3)
    c: Coincident(g3,g4)
    c: Horizontal(g4)
    c: Coincident(g4,g5)
    c: Coincident(g5,g6)
    c: Coincident(g6,g7)
    c: Coincident(g7,g2)
    c: Vertical(g7)
    c: Vertical(g5)
    c: Horizontal(g6)
    c: Vertical(g6,g3)
    c: PointOnObject(g1,g-1)
    c: DistanceX(g11) = 20
    c: DistanceY(g3,g3) = 0.5
    c: DistanceY(g5,g5) = 0.25
    c: DistanceX(g6,g6) = 0.3
    c: DistanceX(g0) = 15.6
    c: DistanceX(g1,g1) = 1
    c: DistanceX(g6) = 16.75
    c: DistanceY(g0) = 4
    c: DistanceY(g0,g0) = 1
    c: Coincident(g0,g8)
    c: Coincident(g8,g9)
    c: Vertical(g9)
    c: Coincident(g9,g10)
    c: Horizontal(g10)
    c: Coincident(g10,g11)
    c: Coincident(g1,g12)
    c: Horizontal(g12)
    c: Coincident(g12,g13)
    c: Coincident(g13,g14)
    c: Coincident(g14,g11)
    c: Vertical(g14)
    c: Vertical(g10,g12)
    c: Symmetric(g13,g11,g15)
    c: Coincident(g16,g15)
    c: Horizontal(g16)
    c: Symmetric(g10,g12,g16)
    c: DistanceY(g11,g10) = 0.75
    c: Equal(g10,g9)
    c: DistanceY(g9,g9) = 0.5
    c: DistanceY(g14,g14) = 1.5
    c: DistanceX(g10,g11) = 1
FEATURE [Part::Extrusion] Extrude023
  Base = -> Array028
  Dir = (0,0,1)
  DirMode = 2
  FaceMakerClass = Part::FaceMakerBullseye
  LengthFwd = 10
  LengthRev = 0
  Solid = true
  Symmetric = false
FEATURE [Part::Revolution] Revolve016
  Angle = 15
  Axis = (0,0,1)
  Base = (0,0,0)
  FaceMakerClass = Part::FaceMakerBullseye
  Solid = true
  Source = -> Sketch089
  Symmetric = false
FEATURE [Part::Cut] Cut020
  Base = -> Revolve016
  Tool = -> Extrude023
FEATURE [Part::FeaturePython] Array029  # Draft array (typed FeaturePython)
  Angle = 360
  ArrayType = 1
  Axis = (0,0,1)
  Base = -> Cut020
  Center = (0,0,0)
  Fuse = true
  IntervalAxis = (0,0,0)
  IntervalX = (1,0,0)
  IntervalY = (0,1,0)
  IntervalZ = (0,0,1)
  NumberCircles = 2
  NumberPolar = 24
  NumberX = 1
  NumberY = 1
  NumberZ = 1
  RadialDistance = 1
  Symmetry = 1
  TangentialDistance = 1
FEATURE [Sketcher::SketchObject] Sketch093
  Placement = pos=(0,0,4) rot=(0,0,1;0rad)
  sketch-geometry (275):
    g0: LineSegment StartX=-15.2684 StartY=6.68341 StartZ=0 EndX=-15.1274 EndY=6.98361 EndZ=0
    g1: BSplineCurve PolesCount=3 KnotsCount=2 Degree=2 IsPeriodic=0
    g2: BSplineCurve PolesCount=3 KnotsCount=2 Degree=2 IsPeriodic=0
    g3: BSplineCurve PolesCount=3 KnotsCount=2 Degree=2 IsPeriodic=0
    g4: BSplineCurve PolesCount=3 KnotsCount=2 Degree=2 IsPeriodic=0
    g5: BSplineCurve PolesCount=3 KnotsCount=2 Degree=2 IsPeriodic=0
    g6: BSplineCurve PolesCount=3 KnotsCount=2 Degree=2 IsPeriodic=0
    g7: BSplineCurve PolesCount=3 KnotsCount=2 Degree=2 IsPeriodic=0
    g8: LineSegment StartX=-16.349 StartY=7.9505 StartZ=0 EndX=-15.8289 EndY=7.48977 EndZ=0
    g9: LineSegment StartX=-15.837 StartY=8.8374 StartZ=0 EndX=-16.349 EndY=7.9505 EndZ=0
    g10: LineSegment StartX=-16.0959 StartY=8.98687 StartZ=0 EndX=-15.837 EndY=8.8374 EndZ=0
    g11: LineSegment StartX=-16.734 StartY=7.88154 StartZ=0 EndX=-16.0959 EndY=8.98687 EndZ=0
    g12: LineSegment StartX=-15.7268 StartY=7.01279 StartZ=0 EndX=-16.734 EndY=7.88154 EndZ=0
    g13: LineSegment StartX=-15.5457 StartY=7.24937 StartZ=0 EndX=-15.7268 EndY=7.01279 EndZ=0
    g14: BSplineCurve PolesCount=3 KnotsCount=2 Degree=2 IsPeriodic=0
    g15: BSplineCurve PolesCount=3 KnotsCount=2 Degree=2 IsPeriodic=0
    g16: BSplineCurve PolesCount=3 KnotsCount=2 Degree=2 IsPeriodic=0
    g17: BSplineCurve PolesCount=3 KnotsCount=2 Degree=2 IsPeriodic=0
    g18: BSplineCurve PolesCount=3 KnotsCount=2 Degree=2 IsPeriodic=0
    g19: BSplineCurve PolesCount=3 KnotsCount=2 Degree=2 IsPeriodic=0
    g20: BSplineCurve PolesCount=3 KnotsCount=2 Degree=2 IsPeriodic=0
    g21: BSplineCurve PolesCount=3 KnotsCount=2 Degree=2 IsPeriodic=0
    g22: BSplineCurve PolesCount=3 KnotsCount=2 Degree=2 IsPeriodic=0
    g23: BSplineCurve PolesCount=3 KnotsCount=2 Degree=2 IsPeriodic=0
    g24: BSplineCurve PolesCount=3 KnotsCount=2 Degree=2 IsPeriodic=0
    g25: BSplineCurve PolesCount=3 KnotsCount=2 Degree=2 IsPeriodic=0
    g26: BSplineCurve PolesCount=3 KnotsCount=2 Degree=2 IsPeriodic=0
    g27: BSplineCurve PolesCount=3 KnotsCount=2 Degree=2 IsPeriodic=0
    g28: BSplineCurve PolesCount=3 KnotsCount=2 Degree=2 IsPeriodic=0
    g29: BSplineCurve PolesCount=3 KnotsCount=2 Degree=2 IsPeriodic=0
    g30: BSplineCurve PolesCount=3 KnotsCount=2 Degree=2 IsPeriodic=0
    g31: BSplineCurve PolesCount=3 KnotsCount=2 Degree=2 IsPeriodic=0
    g32: BSplineCurve PolesCount=3 KnotsCount=2 Degree=2 IsPeriodic=0
    g33: BSplineCurve PolesCount=3 KnotsCount=2 Degree=2 IsPeriodic=0
    g34: BSplineCurve PolesCount=3 KnotsCount=2 Degree=2 IsPeriodic=0
    g35: BSplineCurve PolesCount=3 KnotsCount=2 Degree=2 IsPeriodic=0
    g36: BSplineCurve PolesCount=3 KnotsCount=2 Degree=2 IsPeriodic=0
    g37: BSplineCurve PolesCount=3 KnotsCount=2 Degree=2 IsPeriodic=0
    g38: BSplineCurve PolesCount=3 KnotsCount=2 Degree=2 IsPeriodic=0
    g39: BSplineCurve PolesCount=3 KnotsCount=2 Degree=2 IsPeriodic=0
    g40: BSplineCurve PolesCount=3 KnotsCount=2 Degree=2 IsPeriodic=0
    g41: BSplineCurve PolesCount=3 KnotsCount=2 Degree=2 IsPeriodic=0
    g42: LineSegment StartX=-13.306 StartY=-8.58765 StartZ=0 EndX=-13.8238 EndY=-8.88659 EndZ=0
    g43: LineSegment StartX=-13.4636 StartY=-8.3146 StartZ=0 EndX=-13.306 EndY=-8.58765 EndZ=0
    g44: LineSegment StartX=-13.9814 StartY=-8.61354 StartZ=0 EndX=-13.4636 EndY=-8.3146 EndZ=0
    g45: LineSegment StartX=-14.1548 StartY=-8.31319 StartZ=0 EndX=-13.9814 EndY=-8.61354 EndZ=0
    g46: LineSegment StartX=-14.4137 StartY=-8.46266 StartZ=0 EndX=-14.1548 EndY=-8.31319 EndZ=0
    g47: LineSegment StartX=-14.2403 StartY=-8.76301 StartZ=0 EndX=-14.4137 EndY=-8.46266 EndZ=0
    g48: LineSegment StartX=-15.7289 StartY=-9.62246 StartZ=0 EndX=-14.2403 EndY=-8.76301 EndZ=0
    g49: LineSegment StartX=-15.6004 StartY=-9.84494 StartZ=0 EndX=-15.7289 EndY=-9.62246 EndZ=0
    g50: LineSegment StartX=-13.5256 StartY=-10.0008 StartZ=0 EndX=-15.6004 EndY=-9.84494 EndZ=0
    g51: LineSegment StartX=-13.2668 StartY=-9.85135 StartZ=0 EndX=-13.5256 EndY=-10.0008 EndZ=0
    g52: LineSegment StartX=-13.8238 StartY=-8.88659 StartZ=0 EndX=-13.2668 EndY=-9.85135 EndZ=0
    g53: LineSegment StartX=-14.0826 StartY=-9.03606 StartZ=0 EndX=-15.1182 EndY=-9.63393 EndZ=0
    g54: LineSegment StartX=-13.681 StartY=-9.73182 StartZ=0 EndX=-14.0826 EndY=-9.03606 EndZ=0
    g55: LineSegment StartX=-15.1182 StartY=-9.63393 StartZ=0 EndX=-13.681 EndY=-9.73182 EndZ=0
    g56: BSplineCurve PolesCount=3 KnotsCount=2 Degree=2 IsPeriodic=0
    g57: BSplineCurve PolesCount=3 KnotsCount=2 Degree=2 IsPeriodic=0
    g58: BSplineCurve PolesCount=3 KnotsCount=2 Degree=2 IsPeriodic=0
    g59: BSplineCurve PolesCount=3 KnotsCount=2 Degree=2 IsPeriodic=0
    g60: BSplineCurve PolesCount=3 KnotsCount=2 Degree=2 IsPeriodic=0
    g61: BSplineCurve PolesCount=3 KnotsCount=2 Degree=2 IsPeriodic=0
    g62: BSplineCurve PolesCount=3 KnotsCount=2 Degree=2 IsPeriodic=0
    g63: BSplineCurve PolesCount=3 KnotsCount=2 Degree=2 IsPeriodic=0
    g64: BSplineCurve PolesCount=3 KnotsCount=2 Degree=2 IsPeriodic=0
    g65: BSplineCurve PolesCount=3 KnotsCount=2 Degree=2 IsPeriodic=0
    g66: BSplineCurve PolesCount=3 KnotsCount=2 Degree=2 IsPeriodic=0
    g67: BSplineCurve PolesCount=3 KnotsCount=2 Degree=2 IsPeriodic=0
    g68: BSplineCurve PolesCount=3 KnotsCount=2 Degree=2 IsPeriodic=0
    g69: BSplineCurve PolesCount=3 KnotsCount=2 Degree=2 IsPeriodic=0
    g70: BSplineCurve PolesCount=3 KnotsCount=2 Degree=2 IsPeriodic=0
    g71: BSplineCurve PolesCount=3 KnotsCount=2 Degree=2 IsPeriodic=0
    g72: BSplineCurve PolesCount=3 KnotsCount=2 Degree=2 IsPeriodic=0
    g73: BSplineCurve PolesCount=3 KnotsCount=2 Degree=2 IsPeriodic=0
    g74: BSplineCurve PolesCount=3 KnotsCount=2 Degree=2 IsPeriodic=0
    g75: BSplineCurve PolesCount=3 KnotsCount=2 Degree=2 IsPeriodic=0
    g76: LineSegment StartX=1.84559 StartY=-16.5225 StartZ=0 EndX=1.53031 EndY=-16.5645 EndZ=0
    g77: BSplineCurve PolesCount=3 KnotsCount=2 Degree=2 IsPeriodic=0
    g78: BSplineCurve PolesCount=3 KnotsCount=2 Degree=2 IsPeriodic=0
    g79: BSplineCurve PolesCount=3 KnotsCount=2 Degree=2 IsPeriodic=0
    g80: BSplineCurve PolesCount=3 KnotsCount=2 Degree=2 IsPeriodic=0
    g81: BSplineCurve PolesCount=3 KnotsCount=2 Degree=2 IsPeriodic=0
    g82: BSplineCurve PolesCount=3 KnotsCount=2 Degree=2 IsPeriodic=0
    g83: BSplineCurve PolesCount=3 KnotsCount=2 Degree=2 IsPeriodic=0
    g84: BSplineCurve PolesCount=3 KnotsCount=2 Degree=2 IsPeriodic=0
    g85: BSplineCurve PolesCount=3 KnotsCount=2 Degree=2 IsPeriodic=0
    g86: BSplineCurve PolesCount=3 KnotsCount=2 Degree=2 IsPeriodic=0
    g87: BSplineCurve PolesCount=3 KnotsCount=2 Degree=2 IsPeriodic=0
    g88: BSplineCurve PolesCount=3 KnotsCount=2 Degree=2 IsPeriodic=0
    g89: BSplineCurve PolesCount=3 KnotsCount=2 Degree=2 IsPeriodic=0
    g90: LineSegment StartX=1.49878 StartY=-17.6855 StartZ=0 EndX=1.81407 EndY=-17.7416 EndZ=0
    g91: BSplineCurve PolesCount=3 KnotsCount=2 Degree=2 IsPeriodic=0
    g92: BSplineCurve PolesCount=3 KnotsCount=2 Degree=2 IsPeriodic=0
    g93: BSplineCurve PolesCount=3 KnotsCount=2 Degree=2 IsPeriodic=0
    g94: BSplineCurve PolesCount=3 KnotsCount=2 Degree=2 IsPeriodic=0
    g95: BSplineCurve PolesCount=3 KnotsCount=2 Degree=2 IsPeriodic=0
    g96: BSplineCurve PolesCount=3 KnotsCount=2 Degree=2 IsPeriodic=0
    g97: BSplineCurve PolesCount=3 KnotsCount=2 Degree=2 IsPeriodic=0
    g98: LineSegment StartX=1.2232 StartY=-17.0152 StartZ=0 EndX=1.18816 EndY=-17.3153 EndZ=0
    g99: BSplineCurve PolesCount=3 KnotsCount=2 Degree=2 IsPeriodic=0
    g100: BSplineCurve PolesCount=3 KnotsCount=2 Degree=2 IsPeriodic=0
    g101: BSplineCurve PolesCount=3 KnotsCount=2 Degree=2 IsPeriodic=0
    g102: BSplineCurve PolesCount=3 KnotsCount=2 Degree=2 IsPeriodic=0
    g103: BSplineCurve PolesCount=3 KnotsCount=2 Degree=2 IsPeriodic=0
    g104: BSplineCurve PolesCount=3 KnotsCount=2 Degree=2 IsPeriodic=0
    g105: BSplineCurve PolesCount=3 KnotsCount=2 Degree=2 IsPeriodic=0
    g106: BSplineCurve PolesCount=3 KnotsCount=2 Degree=2 IsPeriodic=0
    g107: BSplineCurve PolesCount=3 KnotsCount=2 Degree=2 IsPeriodic=0
    g108: BSplineCurve PolesCount=3 KnotsCount=2 Degree=2 IsPeriodic=0
    g109: BSplineCurve PolesCount=3 KnotsCount=2 Degree=2 IsPeriodic=0
    g110: BSplineCurve PolesCount=3 KnotsCount=2 Degree=2 IsPeriodic=0
    g111: BSplineCurve PolesCount=3 KnotsCount=2 Degree=2 IsPeriodic=0
    g112: BSplineCurve PolesCount=3 KnotsCount=2 Degree=2 IsPeriodic=0
    g113: BSplineCurve PolesCount=3 KnotsCount=2 Degree=2 IsPeriodic=0
    g114: BSplineCurve PolesCount=3 KnotsCount=2 Degree=2 IsPeriodic=0
    g115: BSplineCurve PolesCount=3 KnotsCount=2 Degree=2 IsPeriodic=0
    g116: BSplineCurve PolesCount=3 KnotsCount=2 Degree=2 IsPeriodic=0
    g117: BSplineCurve PolesCount=3 KnotsCount=2 Degree=2 IsPeriodic=0
    g118: BSplineCurve PolesCount=3 KnotsCount=2 Degree=2 IsPeriodic=0
    g119: BSplineCurve PolesCount=3 KnotsCount=2 Degree=2 IsPeriodic=0
    g120: BSplineCurve PolesCount=3 KnotsCount=2 Degree=2 IsPeriodic=0
    g121: BSplineCurve PolesCount=3 KnotsCount=2 Degree=2 IsPeriodic=0
    g122: BSplineCurve PolesCount=3 KnotsCount=2 Degree=2 IsPeriodic=0
    g123: BSplineCurve PolesCount=3 KnotsCount=2 Degree=2 IsPeriodic=0
    g124: BSplineCurve PolesCount=3 KnotsCount=2 Degree=2 IsPeriodic=0
    g125: BSplineCurve PolesCount=3 KnotsCount=2 Degree=2 IsPeriodic=0
    g126: LineSegment StartX=14.0412 StartY=-7.91203 StartZ=0 EndX=13.7823 EndY=-7.76256 EndZ=0
    g127: LineSegment StartX=14.6712 StartY=-6.82086 StartZ=0 EndX=14.0412 EndY=-7.91203 EndZ=0
    g128: BSplineCurve PolesCount=3 KnotsCount=2 Degree=2 IsPeriodic=0
    g129: BSplineCurve PolesCount=3 KnotsCount=2 Degree=2 IsPeriodic=0
    g130: BSplineCurve PolesCount=3 KnotsCount=2 Degree=2 IsPeriodic=0
    g131: BSplineCurve PolesCount=3 KnotsCount=2 Degree=2 IsPeriodic=0
    g132: BSplineCurve PolesCount=3 KnotsCount=2 Degree=2 IsPeriodic=0
    g133: BSplineCurve PolesCount=3 KnotsCount=2 Degree=2 IsPeriodic=0
    g134: BSplineCurve PolesCount=3 KnotsCount=2 Degree=2 IsPeriodic=0
    g135: BSplineCurve PolesCount=3 KnotsCount=2 Degree=2 IsPeriodic=0
    g136: BSplineCurve PolesCount=3 KnotsCount=2 Degree=2 IsPeriodic=0
    g137: LineSegment StartX=15.9925 StartY=-7.52168 StartZ=0 EndX=16.1852 EndY=-7.25806 EndZ=0
    g138: BSplineCurve PolesCount=3 KnotsCount=2 Degree=2 IsPeriodic=0
    g139: BSplineCurve PolesCount=3 KnotsCount=2 Degree=2 IsPeriodic=0
    g140: BSplineCurve PolesCount=3 KnotsCount=2 Degree=2 IsPeriodic=0
    g141: BSplineCurve PolesCount=3 KnotsCount=2 Degree=2 IsPeriodic=0
    g142: BSplineCurve PolesCount=3 KnotsCount=2 Degree=2 IsPeriodic=0
    g143: BSplineCurve PolesCount=3 KnotsCount=2 Degree=2 IsPeriodic=0
    g144: BSplineCurve PolesCount=3 KnotsCount=2 Degree=2 IsPeriodic=0
    g145: BSplineCurve PolesCount=3 KnotsCount=2 Degree=2 IsPeriodic=0
    g146: BSplineCurve PolesCount=3 KnotsCount=2 Degree=2 IsPeriodic=0
    g147: LineSegment StartX=13.7823 StartY=-7.76256 StartZ=0 EndX=14.6313 EndY=-6.29216 EndZ=0
    g148: BSplineCurve PolesCount=3 KnotsCount=2 Degree=2 IsPeriodic=0
    g149: BSplineCurve PolesCount=3 KnotsCount=2 Degree=2 IsPeriodic=0
    g150: BSplineCurve PolesCount=3 KnotsCount=2 Degree=2 IsPeriodic=0
    g151: BSplineCurve PolesCount=3 KnotsCount=2 Degree=2 IsPeriodic=0
    g152: BSplineCurve PolesCount=3 KnotsCount=2 Degree=2 IsPeriodic=0
    g153: BSplineCurve PolesCount=3 KnotsCount=2 Degree=2 IsPeriodic=0
    g154: BSplineCurve PolesCount=3 KnotsCount=2 Degree=2 IsPeriodic=0
    g155: BSplineCurve PolesCount=3 KnotsCount=2 Degree=2 IsPeriodic=0
    g156: BSplineCurve PolesCount=3 KnotsCount=2 Degree=2 IsPeriodic=0
    g157: BSplineCurve PolesCount=3 KnotsCount=2 Degree=2 IsPeriodic=0
    g158: BSplineCurve PolesCount=3 KnotsCount=2 Degree=2 IsPeriodic=0
    g159: BSplineCurve PolesCount=3 KnotsCount=2 Degree=2 IsPeriodic=0
    g160: BSplineCurve PolesCount=3 KnotsCount=2 Degree=2 IsPeriodic=0
    g161: BSplineCurve PolesCount=3 KnotsCount=2 Degree=2 IsPeriodic=0
    g162: BSplineCurve PolesCount=3 KnotsCount=2 Degree=2 IsPeriodic=0
    g163: BSplineCurve PolesCount=3 KnotsCount=2 Degree=2 IsPeriodic=0
    g164: BSplineCurve PolesCount=3 KnotsCount=2 Degree=2 IsPeriodic=0
    g165: BSplineCurve PolesCount=3 KnotsCount=2 Degree=2 IsPeriodic=0
    g166: BSplineCurve PolesCount=3 KnotsCount=2 Degree=2 IsPeriodic=0
    g167: BSplineCurve PolesCount=3 KnotsCount=2 Degree=2 IsPeriodic=0
    g168: LineSegment StartX=13.3083 StartY=8.5836 StartZ=0 EndX=13.1507 EndY=8.85665 EndZ=0
    g169: LineSegment StartX=15.5736 StartY=9.89146 StartZ=0 EndX=13.3083 EndY=8.5836 EndZ=0
    g170: LineSegment StartX=15.472 StartY=10.0674 StartZ=0 EndX=15.5736 EndY=9.89146 EndZ=0
    g171: BSplineCurve PolesCount=3 KnotsCount=2 Degree=2 IsPeriodic=0
    g172: BSplineCurve PolesCount=3 KnotsCount=2 Degree=2 IsPeriodic=0
    g173: LineSegment StartX=14.2593 StartY=10.2248 StartZ=0 EndX=14.5182 EndY=10.3743 EndZ=0
    g174: BSplineCurve PolesCount=3 KnotsCount=2 Degree=2 IsPeriodic=0
    g175: BSplineCurve PolesCount=3 KnotsCount=2 Degree=2 IsPeriodic=0
    g176: LineSegment StartX=13.1507 StartY=8.85665 StartZ=0 EndX=14.9154 EndY=9.87549 EndZ=0
    g177: BSplineCurve PolesCount=3 KnotsCount=2 Degree=2 IsPeriodic=0
    g178: BSplineCurve PolesCount=3 KnotsCount=2 Degree=2 IsPeriodic=0
    g179: BSplineCurve PolesCount=3 KnotsCount=2 Degree=2 IsPeriodic=0
    g180: BSplineCurve PolesCount=3 KnotsCount=2 Degree=2 IsPeriodic=0
    g181: BSplineCurve PolesCount=3 KnotsCount=2 Degree=2 IsPeriodic=0
    g182: BSplineCurve PolesCount=3 KnotsCount=2 Degree=2 IsPeriodic=0
    g183: BSplineCurve PolesCount=3 KnotsCount=2 Degree=2 IsPeriodic=0
    g184: BSplineCurve PolesCount=3 KnotsCount=2 Degree=2 IsPeriodic=0
    g185: BSplineCurve PolesCount=3 KnotsCount=2 Degree=2 IsPeriodic=0
    g186: BSplineCurve PolesCount=3 KnotsCount=2 Degree=2 IsPeriodic=0
    g187: BSplineCurve PolesCount=3 KnotsCount=2 Degree=2 IsPeriodic=0
    g188: BSplineCurve PolesCount=3 KnotsCount=2 Degree=2 IsPeriodic=0
    g189: BSplineCurve PolesCount=3 KnotsCount=2 Degree=2 IsPeriodic=0
    g190: BSplineCurve PolesCount=3 KnotsCount=2 Degree=2 IsPeriodic=0
    g191: BSplineCurve PolesCount=3 KnotsCount=2 Degree=2 IsPeriodic=0
    g192: BSplineCurve PolesCount=3 KnotsCount=2 Degree=2 IsPeriodic=0
    g193: BSplineCurve PolesCount=3 KnotsCount=2 Degree=2 IsPeriodic=0
    g194: BSplineCurve PolesCount=3 KnotsCount=2 Degree=2 IsPeriodic=0
    g195: BSplineCurve PolesCount=3 KnotsCount=2 Degree=2 IsPeriodic=0
    g196: BSplineCurve PolesCount=3 KnotsCount=2 Degree=2 IsPeriodic=0
    g197: Circle [constr] CenterX=0 CenterY=0 CenterZ=0 NormalX=0 NormalY=0 NormalZ=1 AngleXU=0 Radius=17.125
    g198: LineSegment [constr] StartX=0 StartY=0 StartZ=0 EndX=8.5625 EndY=14.8307 EndZ=0
    g199: LineSegment [constr] StartX=0 StartY=0 StartZ=0 EndX=8.5625 EndY=-14.8307 EndZ=0
    g200: LineSegment [constr] StartX=0 StartY=0 StartZ=0 EndX=-8.5625 EndY=-14.8307 EndZ=0
    g201: LineSegment [constr] StartX=0 StartY=0 StartZ=0 EndX=-8.5625 EndY=14.8307 EndZ=0
    g202: LineSegment StartX=7.56699 StartY=14.1064 StartZ=0 EndX=8.69199 EndY=16.055 EndZ=0
    g203: LineSegment StartX=8.69199 StartY=16.055 StartZ=0 EndX=9.55801 EndY=15.555 EndZ=0
    g204: LineSegment StartX=9.55801 StartY=15.555 StartZ=0 EndX=8.43301 EndY=13.6064 EndZ=0
    g205: LineSegment StartX=8.43301 StartY=13.6064 StartZ=0 EndX=7.56699 EndY=14.1064 EndZ=0
    g206: LineSegment StartX=16 StartY=0.5 StartZ=0 EndX=18.25 EndY=0.5 EndZ=0
    g207: LineSegment StartX=18.25 StartY=0.5 StartZ=0 EndX=18.25 EndY=-0.5 EndZ=0
    g208: LineSegment StartX=18.25 StartY=-0.5 StartZ=0 EndX=16 EndY=-0.5 EndZ=0
    g209: LineSegment StartX=16 StartY=-0.5 StartZ=0 EndX=16 EndY=0.5 EndZ=0
    g210: LineSegment StartX=-8.43301 StartY=13.6064 StartZ=0 EndX=-9.55801 EndY=15.555 EndZ=0
    g211: LineSegment StartX=-9.55801 StartY=15.555 StartZ=0 EndX=-8.69199 EndY=16.055 EndZ=0
    g212: LineSegment StartX=-8.69199 StartY=16.055 StartZ=0 EndX=-7.56699 EndY=14.1064 EndZ=0
    g213: LineSegment StartX=-7.56699 StartY=14.1064 StartZ=0 EndX=-8.43301 EndY=13.6064 EndZ=0
    g214: LineSegment StartX=8.69199 StartY=-16.055 StartZ=0 EndX=7.56699 EndY=-14.1064 EndZ=0
    g215: LineSegment StartX=7.56699 StartY=-14.1064 StartZ=0 EndX=8.43301 EndY=-13.6064 EndZ=0
    g216: LineSegment StartX=8.43301 StartY=-13.6064 StartZ=0 EndX=9.55801 EndY=-15.555 EndZ=0
    g217: LineSegment StartX=9.55801 StartY=-15.555 StartZ=0 EndX=8.69199 EndY=-16.055 EndZ=0
    g218: LineSegment StartX=-9.55801 StartY=-15.555 StartZ=0 EndX=-8.43301 EndY=-13.6064 EndZ=0
    g219: LineSegment StartX=-8.43301 StartY=-13.6064 StartZ=0 EndX=-7.56699 EndY=-14.1064 EndZ=0
    g220: LineSegment StartX=-7.56699 StartY=-14.1064 StartZ=0 EndX=-8.69199 EndY=-16.055 EndZ=0
    g221: LineSegment StartX=-8.69199 StartY=-16.055 StartZ=0 EndX=-9.55801 EndY=-15.555 EndZ=0
    g222: LineSegment StartX=-18.25 StartY=0.5 StartZ=0 EndX=-16 EndY=0.5 EndZ=0
    g223: LineSegment StartX=-16 StartY=0.5 StartZ=0 EndX=-16 EndY=-0.5 EndZ=0
    g224: LineSegment StartX=-16 StartY=-0.5 StartZ=0 EndX=-18.25 EndY=-0.5 EndZ=0
    g225: LineSegment StartX=-18.25 StartY=-0.5 StartZ=0 EndX=-18.25 EndY=0.5 EndZ=0
    g226: GeomPoint X=17.125 Y=0 Z=0
    g227: GeomPoint X=-17.125 Y=0 Z=0
    g228: LineSegment [constr] StartX=0 StartY=0 StartZ=0 EndX=1.79005 EndY=17.0312 EndZ=0
    g229: LineSegment [constr] StartX=3.56049 StartY=16.7508 StartZ=0 EndX=0 EndY=0 EndZ=0
    g230: LineSegment [constr] StartX=5.29192 StartY=16.2868 StartZ=0 EndX=0 EndY=0 EndZ=0
    g231: LineSegment [constr] StartX=6.96537 StartY=15.6445 StartZ=0 EndX=0 EndY=0 EndZ=0
    g232: Circle [constr] CenterX=0 CenterY=0 CenterZ=0 NormalX=0 NormalY=0 NormalZ=1 AngleXU=0 Radius=16.0078
    g233: LineSegment [constr] StartX=0 StartY=0 StartZ=0 EndX=9.40915 EndY=12.9506 EndZ=0
    g234: LineSegment [constr] StartX=10.7113 StartY=11.8961 StartZ=0 EndX=0 EndY=0 EndZ=0
    g235: LineSegment [constr] StartX=11.8961 StartY=10.7113 StartZ=0 EndX=0 EndY=0 EndZ=0
    g236: LineSegment [constr] StartX=0 StartY=0 StartZ=0 EndX=15.9201 EndY=1.67327 EndZ=0
    g237: LineSegment [constr] StartX=15.658 StartY=3.32821 StartZ=0 EndX=0 EndY=0 EndZ=0
    g238: LineSegment [constr] StartX=15.2243 StartY=4.94669 StartZ=0 EndX=0 EndY=0 EndZ=0
    g239: LineSegment [constr] StartX=9.40915 StartY=12.9506 StartZ=0 EndX=10.0658 EndY=13.8544 EndZ=0
    g240: LineSegment [constr] StartX=10.7113 StartY=11.8961 StartZ=0 EndX=11.4589 EndY=12.7264 EndZ=0
    g241: LineSegment [constr] StartX=11.8961 StartY=10.7113 StartZ=0 EndX=12.7264 EndY=11.4589 EndZ=0
    g242: LineSegment [constr] StartX=15.2243 StartY=4.94669 StartZ=0 EndX=16.2868 EndY=5.29192 EndZ=0
    g243: LineSegment [constr] StartX=15.658 StartY=3.32821 StartZ=0 EndX=16.7508 EndY=3.56049 EndZ=0
    g244: LineSegment [constr] StartX=15.9201 StartY=1.67327 StartZ=0 EndX=17.0312 EndY=1.79005 EndZ=0
    g245: Circle [constr] CenterX=0 CenterY=0 CenterZ=0 NormalX=0 NormalY=0 NormalZ=1 AngleXU=0 Radius=18.2568
    g246: LineSegment [constr] StartX=3.56049 StartY=16.7508 StartZ=0 EndX=3.79581 EndY=17.8579 EndZ=0
    g247: LineSegment StartX=3.19285 StartY=16.8247 StartZ=0 EndX=3.92812 EndY=16.6768 EndZ=0
    g248: LineSegment StartX=3.92812 StartY=16.6768 StartZ=0 EndX=3.6941 EndY=15.5757 EndZ=0
    g249: LineSegment StartX=3.6941 StartY=15.5757 StartZ=0 EndX=2.96049 EndY=15.7317 EndZ=0
    g250: LineSegment StartX=2.96049 StartY=15.7317 StartZ=0 EndX=3.19285 EndY=16.8247 EndZ=0
    g251: LineSegment StartX=0 StartY=16.0078 StartZ=0 EndX=-2.6584 EndY=18.0623 EndZ=0
    g252: LineSegment StartX=-2.6584 StartY=18.0623 StartZ=0 EndX=2.6584 EndY=18.0623 EndZ=0
    g253: LineSegment StartX=5.64727 StartY=16.1671 StartZ=0 EndX=4.93656 EndY=16.4066 EndZ=0
    g254: LineSegment StartX=4.93656 StartY=16.4066 StartZ=0 EndX=4.58868 EndY=15.336 EndZ=0
    g255: LineSegment StartX=4.58868 StartY=15.336 StartZ=0 EndX=5.30197 EndY=15.1043 EndZ=0
    g256: LineSegment StartX=5.30197 StartY=15.1043 StartZ=0 EndX=5.64727 EndY=16.1671 EndZ=0
    g257: LineSegment StartX=6.62114 StartY=15.7932 StartZ=0 EndX=7.30959 EndY=15.4957 EndZ=0
    g258: LineSegment StartX=7.30959 StartY=15.4957 StartZ=0 EndX=6.85176 EndY=14.4673 EndZ=0
    g259: LineSegment StartX=6.85176 StartY=14.4673 StartZ=0 EndX=6.1666 EndY=14.7724 EndZ=0
    g260: LineSegment StartX=6.1666 StartY=14.7724 StartZ=0 EndX=6.62114 EndY=15.7932 EndZ=0
    g261: LineSegment StartX=9.76005 StartY=14.0715 StartZ=0 EndX=10.3716 EndY=13.6373 EndZ=0
    g262: LineSegment StartX=10.3716 StartY=13.6373 StartZ=0 EndX=9.70993 EndY=12.7266 EndZ=0
    g263: LineSegment StartX=9.70993 StartY=12.7266 StartZ=0 EndX=9.10838 EndY=13.1745 EndZ=0
    g264: LineSegment StartX=9.10838 StartY=13.1745 StartZ=0 EndX=9.76005 EndY=14.0715 EndZ=0
    g265: LineSegment StartX=11.1775 StartY=12.9742 StartZ=0 EndX=11.7403 EndY=12.4785 EndZ=0
    g266: LineSegment StartX=11.7403 StartY=12.4785 StartZ=0 EndX=10.9871 EndY=11.6419 EndZ=0
    g267: LineSegment StartX=10.9871 StartY=11.6419 StartZ=0 EndX=10.4297 EndY=12.1438 EndZ=0
    g268: LineSegment StartX=10.4297 StartY=12.1438 StartZ=0 EndX=11.1775 EndY=12.9742 EndZ=0
    g269: LineSegment StartX=12.4724 StartY=11.7348 StartZ=0 EndX=12.9803 EndY=11.1829 EndZ=0
    g270: LineSegment StartX=12.9803 StartY=11.1829 StartZ=0 EndX=12.1438 EndY=10.4297 EndZ=0
    g271: LineSegment StartX=12.1438 StartY=10.4297 StartZ=0 EndX=11.6419 EndY=10.9871 EndZ=0
    g272: LineSegment StartX=11.6419 StartY=10.9871 StartZ=0 EndX=12.4724 EndY=11.7348 EndZ=0
    g273: LineSegment [constr] StartX=2.49359 StartY=16.9425 StartZ=0 EndX=2.6584 EndY=18.0623 EndZ=0
    g274: LineSegment StartX=2.6584 StartY=18.0623 StartZ=0 EndX=0 EndY=16.0078 EndZ=0
  constraints (395):
    c: Coincident(g0,g1)
    c: Coincident(g1,g2)
    c: Coincident(g2,g3)
    c: Coincident(g3,g4)
    c: Coincident(g4,g5)
    c: Coincident(g5,g6)
    c: Coincident(g6,g7)
    c: Coincident(g7,g8)
    c: Coincident(g8,g9)
    c: Coincident(g9,g10)
    c: Coincident(g10,g11)
    c: Coincident(g11,g12)
    c: Coincident(g12,g13)
    c: Coincident(g13,g14)
    c: Coincident(g14,g15)
    c: Coincident(g15,g16)
    c: Coincident(g16,g17)
    c: Coincident(g17,g18)
    c: Coincident(g18,g19)
    c: Coincident(g19,g20)
    c: Coincident(g20,g21)
    c: Coincident(g21,g0)
    c: Coincident(g22,g23)
    c: Coincident(g23,g24)
    c: Coincident(g24,g25)
    c: Coincident(g25,g26)
    c: Coincident(g26,g27)
    c: Coincident(g27,g28)
    c: Coincident(g28,g29)
    c: Coincident(g29,g30)
    c: Coincident(g30,g31)
    c: Coincident(g31,g32)
    c: Coincident(g32,g33)
    c: Coincident(g33,g22)
    c: Coincident(g34,g35)
    c: Coincident(g35,g36)
    c: Coincident(g36,g37)
    c: Coincident(g37,g38)
    c: Coincident(g38,g39)
    c: Coincident(g39,g40)
    c: Coincident(g40,g41)
    c: Coincident(g41,g34)
    c: Coincident(g42,g43)
    c: Coincident(g43,g44)
    c: Coincident(g44,g45)
    c: Coincident(g45,g46)
    c: Coincident(g46,g47)
    c: Coincident(g47,g48)
    c: Coincident(g48,g49)
    c: Coincident(g49,g50)
    c: Coincident(g50,g51)
    c: Coincident(g51,g52)
    c: Coincident(g52,g42)
    c: Coincident(g53,g54)
    c: Coincident(g54,g55)
    c: Coincident(g55,g53)
    c: Coincident(g56,g57)
    c: Coincident(g57,g58)
    c: Coincident(g58,g59)
    c: Coincident(g59,g60)
    c: Coincident(g60,g61)
    c: Coincident(g61,g62)
    c: Coincident(g62,g63)
    c: Coincident(g63,g64)
    c: Coincident(g64,g65)
    c: Coincident(g65,g66)
    c: Coincident(g66,g67)
    c: Coincident(g67,g56)
    c: Coincident(g68,g69)
    c: Coincident(g69,g70)
    c: Coincident(g70,g71)
    c: Coincident(g71,g72)
    c: Coincident(g72,g73)
    c: Coincident(g73,g74)
    c: Coincident(g74,g75)
    c: Coincident(g75,g68)
    c: Coincident(g76,g77)
    c: Coincident(g77,g78)
    c: Coincident(g78,g79)
    c: Coincident(g79,g80)
    c: Coincident(g80,g81)
    c: Coincident(g81,g82)
    c: Coincident(g82,g83)
    c: Coincident(g83,g84)
    c: Coincident(g84,g85)
    c: Coincident(g85,g86)
    c: Coincident(g86,g87)
    c: Coincident(g87,g88)
    c: Coincident(g88,g89)
    c: Coincident(g89,g90)
    c: Coincident(g90,g91)
    c: Coincident(g91,g92)
    c: Coincident(g92,g93)
    c: Coincident(g93,g94)
    c: Coincident(g94,g95)
    c: Coincident(g95,g96)
    c: Coincident(g96,g97)
    c: Coincident(g97,g98)
    c: Coincident(g98,g99)
    c: Coincident(g99,g100)
    c: Coincident(g100,g101)
    c: Coincident(g101,g102)
    c: Coincident(g102,g103)
    c: Coincident(g103,g104)
    c: Coincident(g104,g105)
    c: Coincident(g105,g76)
    c: Coincident(g106,g107)
    c: Coincident(g107,g108)
    c: Coincident(g108,g109)
    c: Coincident(g109,g110)
    c: Coincident(g110,g111)
    c: Coincident(g111,g112)
    c: Coincident(g112,g113)
    c: Coincident(g113,g114)
    c: Coincident(g114,g115)
    c: Coincident(g115,g116)
    c: Coincident(g116,g117)
    c: Coincident(g117,g106)
    c: Coincident(g118,g119)
    c: Coincident(g119,g120)
    c: Coincident(g120,g121)
    c: Coincident(g121,g122)
    c: Coincident(g122,g123)
    c: Coincident(g123,g124)
    c: Coincident(g124,g125)
    c: Coincident(g125,g118)
    c: Coincident(g126,g127)
    c: Coincident(g127,g128)
    c: Coincident(g128,g129)
    c: Coincident(g129,g130)
    c: Coincident(g130,g131)
    c: Coincident(g131,g132)
    c: Coincident(g132,g133)
    c: Coincident(g133,g134)
    c: Coincident(g134,g135)
    c: Coincident(g135,g136)
    c: Coincident(g136,g137)
    c: Coincident(g137,g138)
    c: Coincident(g138,g139)
    c: Coincident(g139,g140)
    c: Coincident(g140,g141)
    c: Coincident(g141,g142)
    c: Coincident(g142,g143)
    c: Coincident(g143,g144)
    c: Coincident(g144,g145)
    c: Coincident(g145,g146)
    c: Coincident(g146,g147)
    c: Coincident(g147,g126)
    c: Coincident(g148,g149)
    c: Coincident(g149,g150)
    c: Coincident(g150,g151)
    c: Coincident(g151,g152)
    c: Coincident(g152,g153)
    c: Coincident(g153,g154)
    c: Coincident(g154,g155)
    c: Coincident(g155,g156)
    c: Coincident(g156,g157)
    c: Coincident(g157,g158)
    c: Coincident(g158,g159)
    c: Coincident(g159,g148)
    c: Coincident(g160,g161)
    c: Coincident(g161,g162)
    c: Coincident(g162,g163)
    c: Coincident(g163,g164)
    c: Coincident(g164,g165)
    c: Coincident(g165,g166)
    c: Coincident(g166,g167)
    c: Coincident(g167,g160)
    c: Coincident(g168,g169)
    c: Coincident(g169,g170)
    c: Coincident(g170,g171)
    c: Coincident(g171,g172)
    c: Coincident(g172,g173)
    c: Coincident(g173,g174)
    c: Coincident(g174,g175)
    c: Coincident(g175,g176)
    c: Coincident(g176,g168)
    c: Coincident(g177,g178)
    c: Coincident(g178,g179)
    c: Coincident(g179,g180)
    c: Coincident(g180,g181)
    c: Coincident(g181,g182)
    c: Coincident(g182,g183)
    c: Coincident(g183,g184)
    c: Coincident(g184,g185)
    c: Coincident(g185,g186)
    c: Coincident(g186,g187)
    c: Coincident(g187,g188)
    c: Coincident(g188,g177)
    c: Coincident(g189,g190)
    c: Coincident(g190,g191)
    c: Coincident(g191,g192)
    c: Coincident(g192,g193)
    c: Coincident(g193,g194)
    c: Coincident(g194,g195)
    c: Coincident(g195,g196)
    c: Coincident(g196,g189)
    c: Coincident(g197,g-1)
    c: Radius(g197) = 17.125
    c: Coincident(g198,g-1)
    c: PointOnObject(g198,g197)
    c: Coincident(g199,g-1)
    c: PointOnObject(g199,g197)
    c: Coincident(g200,g-1)
    c: PointOnObject(g200,g197)
    c: Coincident(g201,g-1)
    c: PointOnObject(g201,g197)
    c: Angle(g198,g-2) = 0.523599
    c: Angle(g-2,g201) = 0.523599
    c: Angle(g199,g-2) = 2.61799
    c: Angle(g200,g-1) = 2.0944
    c: Coincident(g202,g203)
    c: Coincident(g203,g204)
    c: Coincident(g204,g205)
    c: Coincident(g205,g202)
    c: Symmetric(g202,g203,g198)
    c: Symmetric(g202,g204,g198)
    c: Symmetric(g202,g203,g198)
    c: Distance(g204) = 2.25
    c: Distance(g205) = 1
    c: Coincident(g206,g207)
    c: Coincident(g207,g208)
    c: Coincident(g208,g209)
    c: Coincident(g209,g206)
    c: Equal(g204,g208) = 2.75
    c: Equal(g205,g209) = 1
    c: Coincident(g210,g211)
    c: Coincident(g211,g212)
    c: Coincident(g212,g213)
    c: Coincident(g213,g210)
    c: Equal(g204,g212) = 2.75
    c: Equal(g205,g213) = 1
    c: Coincident(g214,g215)
    c: Coincident(g215,g216)
    c: Coincident(g216,g217)
    c: Coincident(g217,g214)
    c: Equal(g204,g216) = 2.75
    c: Equal(g205,g217) = 1
    c: Coincident(g218,g219)
    c: Coincident(g219,g220)
    c: Coincident(g220,g221)
    c: Coincident(g221,g218)
    c: Equal(g204,g220) = 2.75
    c: Equal(g205,g221) = 1
    c: Coincident(g222,g223)
    c: Coincident(g223,g224)
    c: Coincident(g224,g225)
    c: Coincident(g225,g222)
    c: Equal(g204,g224) = 2.75
    c: Equal(g205,g225) = 1
    c: Symmetric(g206,g208,g-1)
    c: Symmetric(g207,g206,g-1)
    c: PointOnObject(g226,g197)
    c: PointOnObject(g226,g-1)
    c: Symmetric(g206,g207,g226)
    c: Symmetric(g214,g216,g199)
    c: Symmetric(g214,g215,g199)
    c: Symmetric(g214,g216,g199)
    c: Symmetric(g218,g220,g200)
    c: Symmetric(g218,g219,g200)
    c: Symmetric(g218,g220,g200)
    c: PointOnObject(g227,g197)
    c: PointOnObject(g227,g-1)
    c: Symmetric(g224,g222,g227)
    c: Symmetric(g223,g222,g-1)
    c: Symmetric(g222,g224,g-1)
    c: Symmetric(g210,g212,g201)
    c: Symmetric(g210,g211,g201)
    c: Symmetric(g210,g212,g201)
    c: Coincident(g-1,g228)
    c: PointOnObject(g228,g197)
    c: PointOnObject(g229,g197)
    c: Coincident(g229,g-1)
    c: PointOnObject(g230,g197)
    c: Coincident(g230,g-1)
    c: PointOnObject(g231,g197)
    c: Coincident(g231,g-1)
    c: Angle(g228,g-2) = 0.10472
    c: Angle(g229,g228) = 0.10472
    c: Angle(g230,g229) = 0.10472
    c: Angle(g231,g230) = 0.10472
    c: Coincident(g232,g-1)
    c: PointOnObject(g202,g232)
    c: Coincident(g-1,g233)
    c: PointOnObject(g233,g232)
    c: PointOnObject(g234,g232)
    c: Coincident(g234,g-1)
    c: PointOnObject(g235,g232)
    c: Coincident(g235,g-1)
    c: Coincident(g-1,g236)
    c: PointOnObject(g236,g232)
    c: PointOnObject(g237,g232)
    c: Coincident(g237,g-1)
    c: PointOnObject(g238,g232)
    c: Coincident(g238,g-1)
    c: Angle(g-1,g236) = 0.10472
    c: Angle(g236,g237) = 0.10472
    c: Angle(g237,g238) = 0.10472
    c: Angle(g233,g198) = 0.10472
    c: Angle(g234,g233) = 0.10472
    c: Angle(g235,g234) = 0.10472
    c: Coincident(g239,g233)
    c: PointOnObject(g239,g197)
    c: Coincident(g240,g234)
    c: PointOnObject(g240,g197)
    c: Coincident(g241,g235)
    c: PointOnObject(g241,g197)
    c: Coincident(g242,g238)
    c: PointOnObject(g242,g197)
    c: Coincident(g243,g237)
    c: PointOnObject(g243,g197)
    c: Coincident(g244,g236)
    c: PointOnObject(g244,g197)
    c: Parallel(g244,g236)
    c: Parallel(g237,g243)
    c: Parallel(g242,g238)
    c: Parallel(g235,g241)
    c: Parallel(g234,g240)
    c: Parallel(g239,g233)
    c: Coincident(g245,g-1)
    c: PointOnObject(g202,g245)
    c: Coincident(g246,g229)
    c: PointOnObject(g246,g245)
    c: Parallel(g246,g229)
    c: Coincident(g247,g248)
    c: PointOnObject(g248,g232)
    c: Coincident(g248,g249)
    c: Coincident(g249,g250)
    c: Coincident(g250,g247)
    c: Symmetric(g249,g248,g229)
    c: PointOnObject(g247,g197)
    c: Symmetric(g247,g247,g229)
    c: Distance(g249) = 0.75
    c: Equal(g247,g249)
    c: PointOnObject(g251,g-2)
    c: PointOnObject(g251,g245)
    c: Coincident(g251,g252)
    c: Horizontal(g252)
    c: PointOnObject(g251,g232)
    c: Coincident(g253,g254)
    c: Coincident(g254,g255)
    c: Coincident(g255,g256)
    c: Coincident(g256,g253)
    c: Equal(g249,g255) = 0.75
    c: Equal(g253,g255)
    c: PointOnObject(g255,g232)
    c: PointOnObject(g253,g197)
    c: Symmetric(g253,g253,g230)
    c: Symmetric(g254,g255,g230)
    c: Coincident(g257,g258)
    c: Coincident(g258,g259)
    c: Coincident(g259,g260)
    c: Coincident(g260,g257)
    c: Equal(g249,g259) = 0.75
    c: Equal(g257,g259)
    c: Symmetric(g257,g257,g231)
    c: Symmetric(g259,g258,g231)
    c: PointOnObject(g259,g232)
    c: PointOnObject(g257,g197)
    c: Coincident(g261,g262)
    c: Coincident(g262,g263)
    c: Coincident(g263,g264)
    c: Coincident(g264,g261)
    c: Equal(g249,g263) = 0.75
    c: Equal(g261,g263)
    c: Symmetric(g261,g261,g239)
    c: Symmetric(g263,g262,g233)
    c: PointOnObject(g262,g232)
    c: PointOnObject(g261,g197)
    c: Coincident(g265,g266)
    c: Coincident(g266,g267)
    c: Coincident(g267,g268)
    c: Coincident(g268,g265)
    c: Equal(g249,g267) = 0.75
    c: Equal(g265,g267)
    c: Coincident(g269,g270)
    c: Coincident(g270,g271)
    c: Coincident(g271,g272)
    c: Coincident(g272,g269)
    c: Equal(g249,g271) = 0.75
    c: Equal(g269,g271)
    c: Symmetric(g265,g265,g240)
    c: Symmetric(g267,g266,g234)
    c: PointOnObject(g267,g232)
    c: PointOnObject(g265,g197)
    c: Symmetric(g269,g269,g241)
    c: Symmetric(g271,g270,g235)
    c: PointOnObject(g269,g197)
    c: PointOnObject(g271,g232)
    c: PointOnObject(g273,g197)
    c: PointOnObject(g273,g245)
    c: Symmetric(g228,g247,g273)
    c: Coincident(g252,g273)
    c: Coincident(g274,g252)
    c: Coincident(g274,g251)
FEATURE [Part::Extrusion] Extrude024
  Base = -> Sketch093
  Dir = (0,0,1)
  DirMode = 2
  FaceMakerClass = Part::FaceMakerBullseye
  LengthFwd = -0.9
  LengthRev = 0
  Solid = true
  Symmetric = false
FEATURE [Part::FeaturePython] Clone004  label="Array030"  # Draft clone (typed FeaturePython)
  AttacherType = Attacher::AttachEngine3D
  Fuse = false
  Objects = -> [Array029]
  Scale = (1,1,1)
FEATURE [Part::MultiCommon] Common002
  Placement = pos=(0,0,0.35) rot=(0,0,1;0rad)
  Shapes = -> [Extrude024,Clone004]
FEATURE [Part::MultiFuse] Fusion006  label="Bez16_AM"
  Shapes = -> [Array029,Common002]
FEATURE [Sketcher::SketchObject] Sketch094
  sketch-geometry (12):
    g0: Circle [constr] CenterX=0 CenterY=0 CenterZ=0 NormalX=0 NormalY=0 NormalZ=1 AngleXU=0 Radius=20
    g1: LineSegment [constr] StartX=0 StartY=0 StartZ=0 EndX=19.9726 EndY=1.04672 EndZ=0
    g2: ArcOfCircle CenterX=19.673 CenterY=1.03102 CenterZ=0 NormalX=0 NormalY=0 NormalZ=1 AngleXU=0 Radius=0.3 StartAngle=5.61649 EndAngle=6.33555
    g3: ArcOfCircle CenterX=19.85 CenterY=0 CenterZ=0 NormalX=0 NormalY=0 NormalZ=1 AngleXU=0 Radius=0.15 StartAngle=0 EndAngle=0.628513
    g4: ArcOfCircle CenterX=19.8432 CenterY=0.519612 CenterZ=0 NormalX=0 NormalY=0 NormalZ=1 AngleXU=0 Radius=0.15 StartAngle=2.4749 EndAngle=3.77011
    g5: LineSegment StartX=19.7253 StartY=0.612371 StartZ=0 EndX=19.9088 EndY=0.845502 EndZ=0
    g6: LineSegment StartX=19.7219 StartY=0.431421 StartZ=0 EndX=19.9713 EndY=0.0881914 EndZ=0
    g7: LineSegment [constr] StartX=19.9931 StartY=0.523539 StartZ=0 EndX=0 EndY=0 EndZ=0
    g8: LineSegment StartX=19.9726 StartY=1.04672 StartZ=0 EndX=20.2222 EndY=1.0598 EndZ=0
    g9: LineSegment StartX=20.2222 StartY=1.0598 StartZ=0 EndX=20.2778 EndY=0 EndZ=0
    g10: LineSegment StartX=20.2778 StartY=0 StartZ=0 EndX=20 EndY=0 EndZ=0
    g11: GeomPoint X=19.6932 Y=0.515686 Z=0
  constraints (31):
    c: Angle(g1) = 0.0523599
    c: Coincident(g1,g-1)
    c: PointOnObject(g1,g0)
    c: Radius(g0) = 20
    c: Coincident(g0,g-1)
    c: PointOnObject(g2,g1)
    c: Coincident(g2,g1)
    c: PointOnObject(g3,g-1)
    c: Tangent(g5,g2) = -1.5708
    c: Tangent(g4,g5) = 1.5708
    c: Tangent(g6,g4) = -1.5708
    c: PointOnObject(g7,g0)
    c: Coincident(g7,g-1)
    c: PointOnObject(g4,g7)
    c: Tangent(g3,g6) = 1.5708
    c: Equal(g3,g4)
    c: Symmetric(g3,g2,g7)
    c: Coincident(g8,g9)
    c: PointOnObject(g9,g-1)
    c: Coincident(g9,g10)
    c: Coincident(g10,g3)
    c: Horizontal(g10)
    c: Coincident(g2,g8)
    c: Perpendicular(g0,g8)
    c: Perpendicular(g9,g8)
    c: Distance(g8) = 0.25
    c: PointOnObject(g11,g4)
    c: PointOnObject(g11,g7)
    c: Distance(g11,g7) = 0.3
    c: Radius(g2) = 0.3
    c: Radius(g4) = 0.15
FEATURE [Sketcher::SketchObject] Sketch095
  MapMode = 5
  Placement = pos=(0,0,0) rot=(1,0,0;1.5708rad)
  sketch-geometry (12):
    g0: LineSegment StartX=15.6 StartY=3.1 StartZ=0 EndX=15.6 EndY=4 EndZ=0
    g1: LineSegment StartX=16.75 StartY=3.1 StartZ=0 EndX=15.6 EndY=3.1 EndZ=0
    g2: LineSegment StartX=16.75 StartY=0 StartZ=0 EndX=16.75 EndY=0.5 EndZ=0
    g3: LineSegment StartX=16.75 StartY=0.5 StartZ=0 EndX=17.05 EndY=0.5 EndZ=0
    g4: LineSegment StartX=17.05 StartY=0.5 StartZ=0 EndX=17.05 EndY=0.75 EndZ=0
    g5: LineSegment StartX=17.05 StartY=0.75 StartZ=0 EndX=16.75 EndY=0.75 EndZ=0
    g6: LineSegment StartX=16.75 StartY=0.75 StartZ=0 EndX=16.75 EndY=3.1 EndZ=0
    g7: LineSegment StartX=15.6 StartY=4 StartZ=0 EndX=19.6 EndY=4 EndZ=0
    g8: LineSegment StartX=19.6 StartY=4 StartZ=0 EndX=20 EndY=3.6 EndZ=0
    g9: LineSegment StartX=16.75 StartY=0 StartZ=0 EndX=19.6 EndY=0 EndZ=0
    g10: LineSegment StartX=19.6 StartY=0 StartZ=0 EndX=20 EndY=0.4 EndZ=0
    g11: LineSegment StartX=20 StartY=0.4 StartZ=0 EndX=20 EndY=3.6 EndZ=0
  constraints (36):
    c: Vertical(g0)
    c: Horizontal(g1)
    c: Coincident(g1,g0)
    c: Vertical(g2)
    c: Coincident(g2,g3)
    c: Horizontal(g3)
    c: Coincident(g3,g4)
    c: Coincident(g4,g5)
    c: Coincident(g5,g6)
    c: Coincident(g6,g1)
    c: Vertical(g6)
    c: Vertical(g4)
    c: Horizontal(g5)
    c: Vertical(g5,g2)
    c: DistanceY(g2,g2) = 0.5
    c: DistanceY(g4,g4) = 0.25
    c: DistanceX(g5,g5) = 0.3
    c: DistanceX(g0) = 15.6
    c: DistanceX(g5) = 16.75
    c: DistanceY(g0,g0) = 0.9
    c: DistanceY(g0) = 4
    c: Coincident(g0,g7)
    c: Horizontal(g7)
    c: Coincident(g7,g8)
    c: DistanceX(g8) = 20
    c: DistanceX(g7,g8) = 0.4
    c: Coincident(g2,g9)
    c: Horizontal(g9)
    c: Coincident(g9,g10)
    c: Coincident(g10,g11)
    c: Coincident(g11,g8)
    c: Vertical(g11)
    c: Vertical(g7,g9)
    c: Angle(g11,g10) = 2.35619
    c: PointOnObject(g9,g-1)
    c: Angle(g7,g8) = 2.35619
FEATURE [Part::Revolution] Revolve017
  Angle = 15
  Axis = (0,0,1)
  Base = (0,0,0)
  FaceMakerClass = Part::FaceMakerBullseye
  Solid = true
  Source = -> Sketch095
  Symmetric = false
FEATURE [Part::FeaturePython] Array031  # Draft array (typed FeaturePython)
  Angle = 12
  ArrayType = 1
  Axis = (0,0,1)
  Base = -> Sketch094
  Center = (0,0,0)
  Fuse = false
  IntervalAxis = (0,0,0)
  IntervalX = (1,0,0)
  IntervalY = (0,1,0)
  IntervalZ = (0,0,1)
  NumberPolar = 5
  NumberX = 2
  NumberY = 2
  NumberZ = 1
FEATURE [Part::Extrusion] Extrude026
  Base = -> Array031
  Dir = (0,0,1)
  DirMode = 2
  FaceMakerClass = Part::FaceMakerBullseye
  LengthFwd = 4
  LengthRev = 0
  Solid = true
  Symmetric = false
FEATURE [Part::Cut] Cut022
  Base = -> Revolve017
  Tool = -> Extrude026
FEATURE [Part::FeaturePython] Array030  label="temp003"  # Draft array (typed FeaturePython)
  Angle = 360
  ArrayType = 1
  Axis = (0,0,1)
  Base = -> Cut022
  Center = (0,0,0)
  Fuse = true
  IntervalAxis = (0,0,0)
  IntervalX = (1,0,0)
  IntervalY = (0,1,0)
  IntervalZ = (0,0,1)
  NumberCircles = 2
  NumberPolar = 24
  NumberX = 1
  NumberY = 1
  NumberZ = 1
  RadialDistance = 1
  Symmetry = 1
  TangentialDistance = 1
FEATURE [Sketcher::SketchObject] Sketch098
  Placement = pos=(0,0,4) rot=(0,0,1;0rad)
  sketch-geometry (65):
    g0: LineSegment [constr] StartX=0 StartY=0 StartZ=0 EndX=8.8 EndY=15.242 EndZ=0
    g1: LineSegment [constr] StartX=15.242 StartY=8.8 StartZ=0 EndX=0 EndY=0 EndZ=0
    g2: LineSegment [constr] StartX=8.8 StartY=-15.242 StartZ=0 EndX=0 EndY=0 EndZ=0
    g3: LineSegment [constr] StartX=0 StartY=0 StartZ=0 EndX=-8.8 EndY=-15.242 EndZ=0
    g4: LineSegment [constr] StartX=0 StartY=0 StartZ=0 EndX=-8.8 EndY=15.242 EndZ=0
    g5: LineSegment StartX=8.70981 StartY=14.4858 StartZ=0 EndX=9.40981 EndY=15.6983 EndZ=0
    g6: LineSegment StartX=9.3366 StartY=15.9715 StartZ=0 EndX=9.1634 EndY=16.0715 EndZ=0
    g7: LineSegment StartX=8.89019 StartY=15.9983 StartZ=0 EndX=8.19019 EndY=14.7858 EndZ=0
    g8: LineSegment StartX=8.2634 StartY=14.5126 StartZ=0 EndX=8.4366 EndY=14.4126 EndZ=0
    g9: Circle [constr] CenterX=0 CenterY=0 CenterZ=0 NormalX=0 NormalY=0 NormalZ=1 AngleXU=0 Radius=19.2
    g10: Circle [constr] CenterX=0 CenterY=0 CenterZ=0 NormalX=0 NormalY=0 NormalZ=1 AngleXU=0 Radius=17.6
    g11: ArcOfCircle CenterX=9.0634 CenterY=15.8983 CenterZ=0 NormalX=0 NormalY=0 NormalZ=1 AngleXU=0 Radius=0.2 StartAngle=1.0472 EndAngle=2.61799
    g12: ArcOfCircle CenterX=9.2366 CenterY=15.7983 CenterZ=0 NormalX=0 NormalY=0 NormalZ=1 AngleXU=0 Radius=0.2 StartAngle=5.75959 EndAngle=7.33038
    g13: ArcOfCircle CenterX=8.3634 CenterY=14.6858 CenterZ=0 NormalX=0 NormalY=0 NormalZ=1 AngleXU=0 Radius=0.2 StartAngle=2.61799 EndAngle=4.18879
    g14: ArcOfCircle CenterX=8.5366 CenterY=14.5858 CenterZ=0 NormalX=0 NormalY=0 NormalZ=1 AngleXU=0 Radius=0.2 StartAngle=4.18879 EndAngle=5.75959
    g15: LineSegment StartX=14.8233 StartY=8.12524 StartZ=0 EndX=16.0358 EndY=8.82524 EndZ=0
    g16: LineSegment StartX=16.109 StartY=9.09845 StartZ=0 EndX=15.934 EndY=9.40155 EndZ=0
    g17: LineSegment StartX=15.6608 StartY=9.47476 StartZ=0 EndX=14.4483 EndY=8.77476 EndZ=0
    g18: LineSegment StartX=14.3751 StartY=8.50155 StartZ=0 EndX=14.5501 EndY=8.19845 EndZ=0
    g19: ArcOfCircle CenterX=15.7608 CenterY=9.30155 CenterZ=0 NormalX=0 NormalY=0 NormalZ=1 AngleXU=0 Radius=0.2 StartAngle=0.523599 EndAngle=2.0944
    g20: ArcOfCircle CenterX=15.9358 CenterY=8.99845 CenterZ=0 NormalX=0 NormalY=0 NormalZ=1 AngleXU=0 Radius=0.2 StartAngle=5.23599 EndAngle=6.80678
    g21: ArcOfCircle CenterX=14.5483 CenterY=8.60155 CenterZ=0 NormalX=0 NormalY=0 NormalZ=1 AngleXU=0 Radius=0.2 StartAngle=2.0944 EndAngle=3.66519
    g22: ArcOfCircle CenterX=14.7233 CenterY=8.29845 CenterZ=0 NormalX=0 NormalY=0 NormalZ=1 AngleXU=0 Radius=0.2 StartAngle=3.66519 EndAngle=5.23599
    g23: LineSegment StartX=16.9 StartY=-0.3 StartZ=0 EndX=18.3 EndY=-0.3 EndZ=0
    g24: LineSegment StartX=18.5 StartY=-0.1 StartZ=0 EndX=18.5 EndY=0.1 EndZ=0
    g25: LineSegment StartX=18.3 StartY=0.3 StartZ=0 EndX=16.9 EndY=0.3 EndZ=0
    g26: LineSegment StartX=16.7 StartY=0.1 StartZ=0 EndX=16.7 EndY=-0.1 EndZ=0
    g27: ArcOfCircle CenterX=18.3 CenterY=0.1 CenterZ=0 NormalX=0 NormalY=0 NormalZ=1 AngleXU=0 Radius=0.2 StartAngle=0 EndAngle=1.5708
    g28: ArcOfCircle CenterX=18.3 CenterY=-0.1 CenterZ=0 NormalX=0 NormalY=0 NormalZ=1 AngleXU=0 Radius=0.2 StartAngle=4.71239 EndAngle=6.28319
    g29: ArcOfCircle CenterX=16.9 CenterY=0.1 CenterZ=0 NormalX=0 NormalY=0 NormalZ=1 AngleXU=0 Radius=0.2 StartAngle=1.5708 EndAngle=3.14159
    g30: ArcOfCircle CenterX=16.9 CenterY=-0.1 CenterZ=0 NormalX=0 NormalY=0 NormalZ=1 AngleXU=0 Radius=0.2 StartAngle=3.14159 EndAngle=4.71239
    g31: GeomPoint X=17.6 Y=0 Z=0
    g32: LineSegment StartX=9.40981 StartY=-15.6983 StartZ=0 EndX=8.70981 EndY=-14.4858 EndZ=0
    g33: LineSegment StartX=8.4366 StartY=-14.4126 StartZ=0 EndX=8.2634 EndY=-14.5126 EndZ=0
    g34: LineSegment StartX=8.19019 StartY=-14.7858 StartZ=0 EndX=8.89019 EndY=-15.9983 EndZ=0
    g35: LineSegment StartX=9.1634 StartY=-16.0715 StartZ=0 EndX=9.3366 EndY=-15.9715 EndZ=0
    g36: ArcOfCircle CenterX=8.3634 CenterY=-14.6858 CenterZ=0 NormalX=0 NormalY=0 NormalZ=1 AngleXU=0 Radius=0.2 StartAngle=2.0944 EndAngle=3.66519
    g37: ArcOfCircle CenterX=8.5366 CenterY=-14.5858 CenterZ=0 NormalX=0 NormalY=0 NormalZ=1 AngleXU=0 Radius=0.2 StartAngle=0.523599 EndAngle=2.0944
    g38: ArcOfCircle CenterX=9.0634 CenterY=-15.8983 CenterZ=0 NormalX=0 NormalY=0 NormalZ=1 AngleXU=0 Radius=0.2 StartAngle=3.66519 EndAngle=5.23599
    g39: ArcOfCircle CenterX=9.2366 CenterY=-15.7983 CenterZ=0 NormalX=0 NormalY=0 NormalZ=1 AngleXU=0 Radius=0.2 StartAngle=5.23599 EndAngle=6.80678
    g40: LineSegment StartX=-8.19019 StartY=14.7858 StartZ=0 EndX=-8.89019 EndY=15.9983 EndZ=0
    g41: LineSegment StartX=-9.1634 StartY=16.0715 StartZ=0 EndX=-9.3366 EndY=15.9715 EndZ=0
    g42: LineSegment StartX=-9.40981 StartY=15.6983 StartZ=0 EndX=-8.70981 EndY=14.4858 EndZ=0
    g43: LineSegment StartX=-8.4366 StartY=14.4126 StartZ=0 EndX=-8.2634 EndY=14.5126 EndZ=0
    g44: ArcOfCircle CenterX=-9.2366 CenterY=15.7983 CenterZ=0 NormalX=0 NormalY=0 NormalZ=1 AngleXU=0 Radius=0.2 StartAngle=2.0944 EndAngle=3.66519
    g45: ArcOfCircle CenterX=-9.0634 CenterY=15.8983 CenterZ=0 NormalX=0 NormalY=0 NormalZ=1 AngleXU=0 Radius=0.2 StartAngle=0.523599 EndAngle=2.0944
    g46: ArcOfCircle CenterX=-8.5366 CenterY=14.5858 CenterZ=0 NormalX=0 NormalY=0 NormalZ=1 AngleXU=0 Radius=0.2 StartAngle=3.66519 EndAngle=5.23599
    g47: ArcOfCircle CenterX=-8.3634 CenterY=14.6858 CenterZ=0 NormalX=0 NormalY=0 NormalZ=1 AngleXU=0 Radius=0.2 StartAngle=5.23599 EndAngle=6.80678
    g48: LineSegment StartX=-18.3 StartY=-0.3 StartZ=0 EndX=-16.9 EndY=-0.3 EndZ=0
    g49: LineSegment StartX=-16.7 StartY=-0.1 StartZ=0 EndX=-16.7 EndY=0.1 EndZ=0
    g50: LineSegment StartX=-16.9 StartY=0.3 StartZ=0 EndX=-18.3 EndY=0.3 EndZ=0
    g51: LineSegment StartX=-18.5 StartY=0.1 StartZ=0 EndX=-18.5 EndY=-0.1 EndZ=0
    g52: ArcOfCircle CenterX=-16.9 CenterY=0.1 CenterZ=0 NormalX=0 NormalY=0 NormalZ=1 AngleXU=0 Radius=0.2 StartAngle=0 EndAngle=1.5708
    g53: ArcOfCircle CenterX=-16.9 CenterY=-0.1 CenterZ=0 NormalX=0 NormalY=0 NormalZ=1 AngleXU=0 Radius=0.2 StartAngle=4.71239 EndAngle=6.28319
    g54: ArcOfCircle CenterX=-18.3 CenterY=0.1 CenterZ=0 NormalX=0 NormalY=0 NormalZ=1 AngleXU=0 Radius=0.2 StartAngle=1.5708 EndAngle=3.14159
    g55: ArcOfCircle CenterX=-18.3 CenterY=-0.1 CenterZ=0 NormalX=0 NormalY=0 NormalZ=1 AngleXU=0 Radius=0.2 StartAngle=3.14159 EndAngle=4.71239
    g56: GeomPoint X=-17.6 Y=0 Z=0
    g57: LineSegment StartX=-8.89019 StartY=-15.9983 StartZ=0 EndX=-8.19019 EndY=-14.7858 EndZ=0
    g58: LineSegment StartX=-8.2634 StartY=-14.5126 StartZ=0 EndX=-8.4366 EndY=-14.4126 EndZ=0
    g59: LineSegment StartX=-8.70981 StartY=-14.4858 StartZ=0 EndX=-9.40981 EndY=-15.6983 EndZ=0
    g60: LineSegment StartX=-9.3366 StartY=-15.9715 StartZ=0 EndX=-9.1634 EndY=-16.0715 EndZ=0
    g61: ArcOfCircle CenterX=-8.5366 CenterY=-14.5858 CenterZ=0 NormalX=0 NormalY=0 NormalZ=1 AngleXU=0 Radius=0.2 StartAngle=1.0472 EndAngle=2.61799
    g62: ArcOfCircle CenterX=-8.3634 CenterY=-14.6858 CenterZ=0 NormalX=0 NormalY=0 NormalZ=1 AngleXU=0 Radius=0.2 StartAngle=5.75959 EndAngle=7.33038
    g63: ArcOfCircle CenterX=-9.2366 CenterY=-15.7983 CenterZ=0 NormalX=0 NormalY=0 NormalZ=1 AngleXU=0 Radius=0.2 StartAngle=2.61799 EndAngle=4.18879
    g64: ArcOfCircle CenterX=-9.0634 CenterY=-15.8983 CenterZ=0 NormalX=0 NormalY=0 NormalZ=1 AngleXU=0 Radius=0.2 StartAngle=4.18879 EndAngle=5.75959
  constraints (143):
    c: Coincident(g0,g-1)
    c: Coincident(g1,g-1)
    c: Coincident(g2,g-1)
    c: Coincident(g3,g-1)
    c: Coincident(g4,g-1)
    c: Angle(g0,g-2) = 0.523599
    c: Angle(g1,g0) = 0.523599
    c: Angle(g-2,g3) = 2.61799
    c: Coincident(g9,g-1)
    c: Radius(g9) = 19.2
    c: Coincident(g10,g9)
    c: Radius(g10) = 17.6
    c: PointOnObject(g0,g10)
    c: Tangent(g7,g11) = -1.5708
    c: Tangent(g6,g11) = -1.5708
    c: Tangent(g6,g12) = -1.5708
    c: Tangent(g5,g12) = -1.5708
    c: Tangent(g7,g13) = -1.5708
    c: Tangent(g8,g13) = -1.5708
    c: Tangent(g8,g14) = -1.5708
    c: Tangent(g5,g14) = -1.5708
    c: Equal(g13,g14)
    c: Equal(g14,g12)
    c: Equal(g12,g11)
    c: Symmetric(g13,g12,g0)
    c: Symmetric(g6,g6,g0)
    c: Distance(g7,g5) = 0.6
    c: Distance(g6,g8) = 1.8
    c: Radius(g11) = 0.2
    c: Symmetric(g8,g8,g0)
    c: PointOnObject(g1,g10)
    c: PointOnObject(g2,g10)
    c: PointOnObject(g3,g10)
    c: PointOnObject(g4,g10)
    c: Angle(g2,g-2) = 2.61799
    c: Angle(g-2,g4) = 0.523599
    c: Tangent(g17,g19) = -1.5708
    c: Tangent(g16,g19) = -1.5708
    c: Tangent(g16,g20) = -1.5708
    c: Tangent(g15,g20) = -1.5708
    c: Tangent(g17,g21) = -1.5708
    c: Tangent(g18,g21) = -1.5708
    c: Tangent(g18,g22) = -1.5708
    c: Tangent(g15,g22) = -1.5708
    c: Equal(g21,g22)
    c: Equal(g22,g20)
    c: Equal(g20,g19)
    c: Distance(g17,g15) = 0.75
    c: Distance(g16,g18) = 1.8
    c: Equal(g11,g19) = 0.2
    c: Symmetric(g21,g20,g1)
    c: Symmetric(g18,g18,g1)
    c: Symmetric(g16,g16,g1)
    c: Tangent(g25,g27) = -1.5708
    c: Tangent(g24,g27) = -1.5708
    c: Tangent(g24,g28) = -1.5708
    c: Tangent(g23,g28) = -1.5708
    c: Tangent(g25,g29) = -1.5708
    c: Tangent(g26,g29) = -1.5708
    c: Tangent(g26,g30) = -1.5708
    c: Tangent(g23,g30) = -1.5708
    c: Equal(g29,g30)
    c: Equal(g30,g28)
    c: Equal(g28,g27)
    c: Distance(g25,g23) = 0.6
    c: Distance(g24,g26) = 1.8
    c: Equal(g11,g27) = 0.2
    c: PointOnObject(g31,g10)
    c: PointOnObject(g31,g-1)
    c: Symmetric(g29,g28,g31)
    c: Symmetric(g24,g24,g-1)
    c: Symmetric(g26,g26,g-1)
    c: Tangent(g34,g36) = -1.5708
    c: Tangent(g33,g36) = -1.5708
    c: Tangent(g33,g37) = -1.5708
    c: Tangent(g32,g37) = -1.5708
    c: Tangent(g34,g38) = -1.5708
    c: Tangent(g35,g38) = -1.5708
    c: Tangent(g35,g39) = -1.5708
    c: Tangent(g32,g39) = -1.5708
    c: Equal(g38,g39)
    c: Equal(g39,g37)
    c: Equal(g37,g36)
    c: Distance(g34,g32) = 0.6
    c: Distance(g33,g35) = 1.8
    c: Equal(g11,g36) = 0.2
    c: Symmetric(g36,g39,g2)
    c: Symmetric(g33,g33,g2)
    c: Symmetric(g35,g35,g2)
    c: Tangent(g42,g44) = -1.5708
    c: Tangent(g41,g44) = -1.5708
    c: Tangent(g41,g45) = -1.5708
    c: Tangent(g40,g45) = -1.5708
    c: Tangent(g42,g46) = -1.5708
    c: Tangent(g43,g46) = -1.5708
    c: Tangent(g43,g47) = -1.5708
    c: Tangent(g40,g47) = -1.5708
    c: Equal(g46,g47)
    c: Equal(g47,g45)
    c: Equal(g45,g44)
    c: Distance(g42,g40) = 0.6
    c: Distance(g41,g43) = 1.8
    c: Equal(g11,g44) = 0.2
    c: Symmetric(g46,g45,g4)
    c: Symmetric(g43,g43,g4)
    c: Symmetric(g41,g41,g4)
    c: Tangent(g50,g52) = -1.5708
    c: Tangent(g49,g52) = -1.5708
    c: Tangent(g49,g53) = -1.5708
    c: Tangent(g48,g53) = -1.5708
    c: Tangent(g50,g54) = -1.5708
    c: Tangent(g51,g54) = -1.5708
    c: Tangent(g51,g55) = -1.5708
    c: Tangent(g48,g55) = -1.5708
    c: Equal(g54,g55)
    c: Equal(g55,g53)
    c: Equal(g53,g52)
    c: Distance(g50,g48) = 0.6
    c: Distance(g49,g51) = 1.8
    c: Equal(g11,g52) = 0.2
    c: PointOnObject(g56,g-1)
    c: PointOnObject(g56,g10)
    c: Symmetric(g53,g54,g56)
    c: Symmetric(g51,g51,g-1)
    c: Symmetric(g49,g49,g-1)
    c: Tangent(g59,g61) = -1.5708
    c: Tangent(g58,g61) = -1.5708
    c: Tangent(g58,g62) = -1.5708
    c: Tangent(g57,g62) = -1.5708
    c: Tangent(g59,g63) = -1.5708
    c: Tangent(g60,g63) = -1.5708
    c: Tangent(g60,g64) = -1.5708
    c: Tangent(g57,g64) = -1.5708
    c: Equal(g63,g64)
    c: Equal(g64,g62)
    c: Equal(g62,g61)
    c: Distance(g59,g57) = 0.6
    c: Distance(g58,g60) = 1.8
    c: Equal(g11,g61) = 0.2
    c: Symmetric(g61,g64,g3)
    c: Symmetric(g63,g64,g3)
    c: Symmetric(g61,g62,g3)
    c: Distance(g0) = 17.6
FEATURE [Part::Part2DObjectPython] ShapeString012  # Draft 2D object (typed FeaturePython)
  FontFile = <path>
  Placement = pos=(-15.144,7.06748,0) rot=(0,0,1;1.0472rad)
  Size = 2
  String = 50
  Tracking = 0
FEATURE [Part::Part2DObjectPython] ShapeString014  # Draft 2D object (typed FeaturePython)
  FontFile = <path>
  Placement = pos=(-13.7115,-9.54862,0) rot=(0,0,1;2.0944rad)
  Size = 2
  String = 40
  Tracking = 0
FEATURE [Part::Part2DObjectPython] ShapeString016  # Draft 2D object (typed FeaturePython)
  FontFile = <path>
  Placement = pos=(1.4518,-16.6488,0) rot=(0,0,1;3.14159rad)
  Size = 2
  String = 30
  Tracking = 0
FEATURE [Part::Part2DObjectPython] ShapeString018  # Draft 2D object (typed FeaturePython)
  FontFile = <path>
  Placement = pos=(15.1365,-7.08044,0) rot=(0,0,1;4.18879rad)
  Size = 2
  String = 20
  Tracking = 0
FEATURE [App::DocumentObjectGroup] FcClock001
  Group = -> [ShapeString012,ShapeString014,ShapeString016,ShapeString018]
FEATURE [Sketcher::SketchObject] Sketch099
  Placement = pos=(0,0,4) rot=(0,0,1;0rad)
  sketch-geometry (168):
    g0: LineSegment StartX=-15.5604 StartY=7.43339 StartZ=0 EndX=-15.4578 EndY=7.65172 EndZ=0
    g1: BSplineCurve PolesCount=3 KnotsCount=2 Degree=2 IsPeriodic=0
    g2: BSplineCurve PolesCount=3 KnotsCount=2 Degree=2 IsPeriodic=0
    g3: BSplineCurve PolesCount=3 KnotsCount=2 Degree=2 IsPeriodic=0
    g4: BSplineCurve PolesCount=3 KnotsCount=2 Degree=2 IsPeriodic=0
    g5: BSplineCurve PolesCount=3 KnotsCount=2 Degree=2 IsPeriodic=0
    g6: BSplineCurve PolesCount=3 KnotsCount=2 Degree=2 IsPeriodic=0
    g7: BSplineCurve PolesCount=3 KnotsCount=2 Degree=2 IsPeriodic=0
    g8: LineSegment StartX=-16.3463 StartY=8.35491 StartZ=0 EndX=-15.968 EndY=8.01983 EndZ=0
    g9: LineSegment StartX=-15.9739 StartY=8.99993 StartZ=0 EndX=-16.3463 EndY=8.35491 EndZ=0
    g10: LineSegment StartX=-16.1622 StartY=9.10863 StartZ=0 EndX=-15.9739 EndY=8.99993 EndZ=0
    g11: LineSegment StartX=-16.6263 StartY=8.30475 StartZ=0 EndX=-16.1622 EndY=9.10863 EndZ=0
    g12: LineSegment StartX=-15.8937 StartY=7.67294 StartZ=0 EndX=-16.6263 EndY=8.30475 EndZ=0
    g13: LineSegment StartX=-15.762 StartY=7.845 StartZ=0 EndX=-15.8937 EndY=7.67294 EndZ=0
    g14: BSplineCurve PolesCount=3 KnotsCount=2 Degree=2 IsPeriodic=0
    g15: BSplineCurve PolesCount=3 KnotsCount=2 Degree=2 IsPeriodic=0
    g16: BSplineCurve PolesCount=3 KnotsCount=2 Degree=2 IsPeriodic=0
    g17: BSplineCurve PolesCount=3 KnotsCount=2 Degree=2 IsPeriodic=0
    g18: BSplineCurve PolesCount=3 KnotsCount=2 Degree=2 IsPeriodic=0
    g19: BSplineCurve PolesCount=3 KnotsCount=2 Degree=2 IsPeriodic=0
    g20: BSplineCurve PolesCount=3 KnotsCount=2 Degree=2 IsPeriodic=0
    g21: BSplineCurve PolesCount=3 KnotsCount=2 Degree=2 IsPeriodic=0
    g22: BSplineCurve PolesCount=3 KnotsCount=2 Degree=2 IsPeriodic=0
    g23: BSplineCurve PolesCount=3 KnotsCount=2 Degree=2 IsPeriodic=0
    g24: BSplineCurve PolesCount=3 KnotsCount=2 Degree=2 IsPeriodic=0
    g25: BSplineCurve PolesCount=3 KnotsCount=2 Degree=2 IsPeriodic=0
    g26: BSplineCurve PolesCount=3 KnotsCount=2 Degree=2 IsPeriodic=0
    g27: BSplineCurve PolesCount=3 KnotsCount=2 Degree=2 IsPeriodic=0
    g28: BSplineCurve PolesCount=3 KnotsCount=2 Degree=2 IsPeriodic=0
    g29: BSplineCurve PolesCount=3 KnotsCount=2 Degree=2 IsPeriodic=0
    g30: BSplineCurve PolesCount=3 KnotsCount=2 Degree=2 IsPeriodic=0
    g31: BSplineCurve PolesCount=3 KnotsCount=2 Degree=2 IsPeriodic=0
    g32: BSplineCurve PolesCount=3 KnotsCount=2 Degree=2 IsPeriodic=0
    g33: BSplineCurve PolesCount=3 KnotsCount=2 Degree=2 IsPeriodic=0
    g34: BSplineCurve PolesCount=3 KnotsCount=2 Degree=2 IsPeriodic=0
    g35: BSplineCurve PolesCount=3 KnotsCount=2 Degree=2 IsPeriodic=0
    g36: BSplineCurve PolesCount=3 KnotsCount=2 Degree=2 IsPeriodic=0
    g37: BSplineCurve PolesCount=3 KnotsCount=2 Degree=2 IsPeriodic=0
    g38: BSplineCurve PolesCount=3 KnotsCount=2 Degree=2 IsPeriodic=0
    g39: BSplineCurve PolesCount=3 KnotsCount=2 Degree=2 IsPeriodic=0
    g40: BSplineCurve PolesCount=3 KnotsCount=2 Degree=2 IsPeriodic=0
    g41: BSplineCurve PolesCount=3 KnotsCount=2 Degree=2 IsPeriodic=0
    g42: LineSegment StartX=-14.1332 StartY=-8.81829 StartZ=0 EndX=-14.5097 EndY=-9.0357 EndZ=0
    g43: LineSegment StartX=-14.2478 StartY=-8.61971 StartZ=0 EndX=-14.1332 EndY=-8.81829 EndZ=0
    g44: LineSegment StartX=-14.6244 StartY=-8.83712 StartZ=0 EndX=-14.2478 EndY=-8.61971 EndZ=0
    g45: LineSegment StartX=-14.7505 StartY=-8.61868 StartZ=0 EndX=-14.6244 EndY=-8.83712 EndZ=0
    g46: LineSegment StartX=-14.9388 StartY=-8.72739 StartZ=0 EndX=-14.7505 EndY=-8.61868 EndZ=0
    g47: LineSegment StartX=-14.8127 StartY=-8.94583 StartZ=0 EndX=-14.9388 EndY=-8.72739 EndZ=0
    g48: LineSegment StartX=-15.8953 StartY=-9.57088 StartZ=0 EndX=-14.8127 EndY=-8.94583 EndZ=0
    g49: LineSegment StartX=-15.8019 StartY=-9.73268 StartZ=0 EndX=-15.8953 EndY=-9.57088 EndZ=0
    g50: LineSegment StartX=-14.2929 StartY=-9.84605 StartZ=0 EndX=-15.8019 EndY=-9.73268 EndZ=0
    g51: LineSegment StartX=-14.1046 StartY=-9.73735 StartZ=0 EndX=-14.2929 EndY=-9.84605 EndZ=0
    g52: LineSegment StartX=-14.5097 StartY=-9.0357 StartZ=0 EndX=-14.1046 EndY=-9.73735 EndZ=0
    g53: LineSegment StartX=-14.698 StartY=-9.1444 StartZ=0 EndX=-15.4512 EndY=-9.57922 EndZ=0
    g54: LineSegment StartX=-14.4059 StartY=-9.65041 StartZ=0 EndX=-14.698 EndY=-9.1444 EndZ=0
    g55: LineSegment StartX=-15.4512 StartY=-9.57922 StartZ=0 EndX=-14.4059 EndY=-9.65041 EndZ=0
    g56: BSplineCurve PolesCount=3 KnotsCount=2 Degree=2 IsPeriodic=0
    g57: BSplineCurve PolesCount=3 KnotsCount=2 Degree=2 IsPeriodic=0
    g58: BSplineCurve PolesCount=3 KnotsCount=2 Degree=2 IsPeriodic=0
    g59: BSplineCurve PolesCount=3 KnotsCount=2 Degree=2 IsPeriodic=0
    g60: BSplineCurve PolesCount=3 KnotsCount=2 Degree=2 IsPeriodic=0
    g61: BSplineCurve PolesCount=3 KnotsCount=2 Degree=2 IsPeriodic=0
    g62: BSplineCurve PolesCount=3 KnotsCount=2 Degree=2 IsPeriodic=0
    g63: BSplineCurve PolesCount=3 KnotsCount=2 Degree=2 IsPeriodic=0
    g64: BSplineCurve PolesCount=3 KnotsCount=2 Degree=2 IsPeriodic=0
    g65: BSplineCurve PolesCount=3 KnotsCount=2 Degree=2 IsPeriodic=0
    g66: BSplineCurve PolesCount=3 KnotsCount=2 Degree=2 IsPeriodic=0
    g67: BSplineCurve PolesCount=3 KnotsCount=2 Degree=2 IsPeriodic=0
    g68: BSplineCurve PolesCount=3 KnotsCount=2 Degree=2 IsPeriodic=0
    g69: BSplineCurve PolesCount=3 KnotsCount=2 Degree=2 IsPeriodic=0
    g70: BSplineCurve PolesCount=3 KnotsCount=2 Degree=2 IsPeriodic=0
    g71: BSplineCurve PolesCount=3 KnotsCount=2 Degree=2 IsPeriodic=0
    g72: BSplineCurve PolesCount=3 KnotsCount=2 Degree=2 IsPeriodic=0
    g73: BSplineCurve PolesCount=3 KnotsCount=2 Degree=2 IsPeriodic=0
    g74: BSplineCurve PolesCount=3 KnotsCount=2 Degree=2 IsPeriodic=0
    g75: BSplineCurve PolesCount=3 KnotsCount=2 Degree=2 IsPeriodic=0
    g76: LineSegment StartX=1.34225 StartY=-17.1618 StartZ=0 EndX=1.11295 EndY=-17.1924 EndZ=0
    g77: BSplineCurve PolesCount=3 KnotsCount=2 Degree=2 IsPeriodic=0
    g78: BSplineCurve PolesCount=3 KnotsCount=2 Degree=2 IsPeriodic=0
    g79: BSplineCurve PolesCount=3 KnotsCount=2 Degree=2 IsPeriodic=0
    g80: BSplineCurve PolesCount=3 KnotsCount=2 Degree=2 IsPeriodic=0
    g81: BSplineCurve PolesCount=3 KnotsCount=2 Degree=2 IsPeriodic=0
    g82: BSplineCurve PolesCount=3 KnotsCount=2 Degree=2 IsPeriodic=0
    g83: BSplineCurve PolesCount=3 KnotsCount=2 Degree=2 IsPeriodic=0
    g84: BSplineCurve PolesCount=3 KnotsCount=2 Degree=2 IsPeriodic=0
    g85: BSplineCurve PolesCount=3 KnotsCount=2 Degree=2 IsPeriodic=0
    g86: BSplineCurve PolesCount=3 KnotsCount=2 Degree=2 IsPeriodic=0
    g87: BSplineCurve PolesCount=3 KnotsCount=2 Degree=2 IsPeriodic=0
    g88: BSplineCurve PolesCount=3 KnotsCount=2 Degree=2 IsPeriodic=0
    g89: BSplineCurve PolesCount=3 KnotsCount=2 Degree=2 IsPeriodic=0
    g90: LineSegment StartX=1.09002 StartY=-18.0076 StartZ=0 EndX=1.31932 EndY=-18.0484 EndZ=0
    g91: BSplineCurve PolesCount=3 KnotsCount=2 Degree=2 IsPeriodic=0
    g92: BSplineCurve PolesCount=3 KnotsCount=2 Degree=2 IsPeriodic=0
    g93: BSplineCurve PolesCount=3 KnotsCount=2 Degree=2 IsPeriodic=0
    g94: BSplineCurve PolesCount=3 KnotsCount=2 Degree=2 IsPeriodic=0
    g95: BSplineCurve PolesCount=3 KnotsCount=2 Degree=2 IsPeriodic=0
    g96: BSplineCurve PolesCount=3 KnotsCount=2 Degree=2 IsPeriodic=0
    g97: BSplineCurve PolesCount=3 KnotsCount=2 Degree=2 IsPeriodic=0
    g98: LineSegment StartX=0.889597 StartY=-17.5202 StartZ=0 EndX=0.864119 EndY=-17.7384 EndZ=0
    g99: BSplineCurve PolesCount=3 KnotsCount=2 Degree=2 IsPeriodic=0
    g100: BSplineCurve PolesCount=3 KnotsCount=2 Degree=2 IsPeriodic=0
    g101: BSplineCurve PolesCount=3 KnotsCount=2 Degree=2 IsPeriodic=0
    g102: BSplineCurve PolesCount=3 KnotsCount=2 Degree=2 IsPeriodic=0
    g103: BSplineCurve PolesCount=3 KnotsCount=2 Degree=2 IsPeriodic=0
    g104: BSplineCurve PolesCount=3 KnotsCount=2 Degree=2 IsPeriodic=0
    g105: BSplineCurve PolesCount=3 KnotsCount=2 Degree=2 IsPeriodic=0
    g106: BSplineCurve PolesCount=3 KnotsCount=2 Degree=2 IsPeriodic=0
    g107: BSplineCurve PolesCount=3 KnotsCount=2 Degree=2 IsPeriodic=0
    g108: BSplineCurve PolesCount=3 KnotsCount=2 Degree=2 IsPeriodic=0
    g109: BSplineCurve PolesCount=3 KnotsCount=2 Degree=2 IsPeriodic=0
    g110: BSplineCurve PolesCount=3 KnotsCount=2 Degree=2 IsPeriodic=0
    g111: BSplineCurve PolesCount=3 KnotsCount=2 Degree=2 IsPeriodic=0
    g112: BSplineCurve PolesCount=3 KnotsCount=2 Degree=2 IsPeriodic=0
    g113: BSplineCurve PolesCount=3 KnotsCount=2 Degree=2 IsPeriodic=0
    g114: BSplineCurve PolesCount=3 KnotsCount=2 Degree=2 IsPeriodic=0
    g115: BSplineCurve PolesCount=3 KnotsCount=2 Degree=2 IsPeriodic=0
    g116: BSplineCurve PolesCount=3 KnotsCount=2 Degree=2 IsPeriodic=0
    g117: BSplineCurve PolesCount=3 KnotsCount=2 Degree=2 IsPeriodic=0
    g118: BSplineCurve PolesCount=3 KnotsCount=2 Degree=2 IsPeriodic=0
    g119: BSplineCurve PolesCount=3 KnotsCount=2 Degree=2 IsPeriodic=0
    g120: BSplineCurve PolesCount=3 KnotsCount=2 Degree=2 IsPeriodic=0
    g121: BSplineCurve PolesCount=3 KnotsCount=2 Degree=2 IsPeriodic=0
    g122: BSplineCurve PolesCount=3 KnotsCount=2 Degree=2 IsPeriodic=0
    g123: BSplineCurve PolesCount=3 KnotsCount=2 Degree=2 IsPeriodic=0
    g124: BSplineCurve PolesCount=3 KnotsCount=2 Degree=2 IsPeriodic=0
    g125: BSplineCurve PolesCount=3 KnotsCount=2 Degree=2 IsPeriodic=0
    g126: LineSegment StartX=14.6679 StartY=-8.32693 StartZ=0 EndX=14.4796 EndY=-8.21823 EndZ=0
    g127: LineSegment StartX=15.1261 StartY=-7.53335 StartZ=0 EndX=14.6679 EndY=-8.32693 EndZ=0
    g128: BSplineCurve PolesCount=3 KnotsCount=2 Degree=2 IsPeriodic=0
    g129: BSplineCurve PolesCount=3 KnotsCount=2 Degree=2 IsPeriodic=0
    g130: BSplineCurve PolesCount=3 KnotsCount=2 Degree=2 IsPeriodic=0
    g131: BSplineCurve PolesCount=3 KnotsCount=2 Degree=2 IsPeriodic=0
    g132: BSplineCurve PolesCount=3 KnotsCount=2 Degree=2 IsPeriodic=0
    g133: BSplineCurve PolesCount=3 KnotsCount=2 Degree=2 IsPeriodic=0
    g134: BSplineCurve PolesCount=3 KnotsCount=2 Degree=2 IsPeriodic=0
    g135: BSplineCurve PolesCount=3 KnotsCount=2 Degree=2 IsPeriodic=0
    g136: BSplineCurve PolesCount=3 KnotsCount=2 Degree=2 IsPeriodic=0
    g137: LineSegment StartX=16.087 StartY=-8.04304 StartZ=0 EndX=16.2271 EndY=-7.85132 EndZ=0
    g138: BSplineCurve PolesCount=3 KnotsCount=2 Degree=2 IsPeriodic=0
    g139: BSplineCurve PolesCount=3 KnotsCount=2 Degree=2 IsPeriodic=0
    g140: BSplineCurve PolesCount=3 KnotsCount=2 Degree=2 IsPeriodic=0
    g141: BSplineCurve PolesCount=3 KnotsCount=2 Degree=2 IsPeriodic=0
    g142: BSplineCurve PolesCount=3 KnotsCount=2 Degree=2 IsPeriodic=0
    g143: BSplineCurve PolesCount=3 KnotsCount=2 Degree=2 IsPeriodic=0
    g144: BSplineCurve PolesCount=3 KnotsCount=2 Degree=2 IsPeriodic=0
    g145: BSplineCurve PolesCount=3 KnotsCount=2 Degree=2 IsPeriodic=0
    g146: BSplineCurve PolesCount=3 KnotsCount=2 Degree=2 IsPeriodic=0
    g147: LineSegment StartX=14.4796 StartY=-8.21823 StartZ=0 EndX=15.097 EndY=-7.14884 EndZ=0
    g148: BSplineCurve PolesCount=3 KnotsCount=2 Degree=2 IsPeriodic=0
    g149: BSplineCurve PolesCount=3 KnotsCount=2 Degree=2 IsPeriodic=0
    g150: BSplineCurve PolesCount=3 KnotsCount=2 Degree=2 IsPeriodic=0
    g151: BSplineCurve PolesCount=3 KnotsCount=2 Degree=2 IsPeriodic=0
    g152: BSplineCurve PolesCount=3 KnotsCount=2 Degree=2 IsPeriodic=0
    g153: BSplineCurve PolesCount=3 KnotsCount=2 Degree=2 IsPeriodic=0
    g154: BSplineCurve PolesCount=3 KnotsCount=2 Degree=2 IsPeriodic=0
    g155: BSplineCurve PolesCount=3 KnotsCount=2 Degree=2 IsPeriodic=0
    g156: BSplineCurve PolesCount=3 KnotsCount=2 Degree=2 IsPeriodic=0
    g157: BSplineCurve PolesCount=3 KnotsCount=2 Degree=2 IsPeriodic=0
    g158: BSplineCurve PolesCount=3 KnotsCount=2 Degree=2 IsPeriodic=0
    g159: BSplineCurve PolesCount=3 KnotsCount=2 Degree=2 IsPeriodic=0
    g160: BSplineCurve PolesCount=3 KnotsCount=2 Degree=2 IsPeriodic=0
    g161: BSplineCurve PolesCount=3 KnotsCount=2 Degree=2 IsPeriodic=0
    g162: BSplineCurve PolesCount=3 KnotsCount=2 Degree=2 IsPeriodic=0
    g163: BSplineCurve PolesCount=3 KnotsCount=2 Degree=2 IsPeriodic=0
    g164: BSplineCurve PolesCount=3 KnotsCount=2 Degree=2 IsPeriodic=0
    g165: BSplineCurve PolesCount=3 KnotsCount=2 Degree=2 IsPeriodic=0
    g166: BSplineCurve PolesCount=3 KnotsCount=2 Degree=2 IsPeriodic=0
    g167: BSplineCurve PolesCount=3 KnotsCount=2 Degree=2 IsPeriodic=0
  constraints (168):
    c: Coincident(g0,g1)
    c: Coincident(g1,g2)
    c: Coincident(g2,g3)
    c: Coincident(g3,g4)
    c: Coincident(g4,g5)
    c: Coincident(g5,g6)
    c: Coincident(g6,g7)
    c: Coincident(g7,g8)
    c: Coincident(g8,g9)
    c: Coincident(g9,g10)
    c: Coincident(g10,g11)
    c: Coincident(g11,g12)
    c: Coincident(g12,g13)
    c: Coincident(g13,g14)
    c: Coincident(g14,g15)
    c: Coincident(g15,g16)
    c: Coincident(g16,g17)
    c: Coincident(g17,g18)
    c: Coincident(g18,g19)
    c: Coincident(g19,g20)
    c: Coincident(g20,g21)
    c: Coincident(g21,g0)
    c: Coincident(g22,g23)
    c: Coincident(g23,g24)
    c: Coincident(g24,g25)
    c: Coincident(g25,g26)
    c: Coincident(g26,g27)
    c: Coincident(g27,g28)
    c: Coincident(g28,g29)
    c: Coincident(g29,g30)
    c: Coincident(g30,g31)
    c: Coincident(g31,g32)
    c: Coincident(g32,g33)
    c: Coincident(g33,g22)
    c: Coincident(g34,g35)
    c: Coincident(g35,g36)
    c: Coincident(g36,g37)
    c: Coincident(g37,g38)
    c: Coincident(g38,g39)
    c: Coincident(g39,g40)
    c: Coincident(g40,g41)
    c: Coincident(g41,g34)
    c: Coincident(g42,g43)
    c: Coincident(g43,g44)
    c: Coincident(g44,g45)
    c: Coincident(g45,g46)
    c: Coincident(g46,g47)
    c: Coincident(g47,g48)
    c: Coincident(g48,g49)
    c: Coincident(g49,g50)
    c: Coincident(g50,g51)
    c: Coincident(g51,g52)
    c: Coincident(g52,g42)
    c: Coincident(g53,g54)
    c: Coincident(g54,g55)
    c: Coincident(g55,g53)
    c: Coincident(g56,g57)
    c: Coincident(g57,g58)
    c: Coincident(g58,g59)
    c: Coincident(g59,g60)
    c: Coincident(g60,g61)
    c: Coincident(g61,g62)
    c: Coincident(g62,g63)
    c: Coincident(g63,g64)
    c: Coincident(g64,g65)
    c: Coincident(g65,g66)
    c: Coincident(g66,g67)
    c: Coincident(g67,g56)
    c: Coincident(g68,g69)
    c: Coincident(g69,g70)
    c: Coincident(g70,g71)
    c: Coincident(g71,g72)
    c: Coincident(g72,g73)
    c: Coincident(g73,g74)
    c: Coincident(g74,g75)
    c: Coincident(g75,g68)
    c: Coincident(g76,g77)
    c: Coincident(g77,g78)
    c: Coincident(g78,g79)
    c: Coincident(g79,g80)
    c: Coincident(g80,g81)
    c: Coincident(g81,g82)
    c: Coincident(g82,g83)
    c: Coincident(g83,g84)
    c: Coincident(g84,g85)
    c: Coincident(g85,g86)
    c: Coincident(g86,g87)
    c: Coincident(g87,g88)
    c: Coincident(g88,g89)
    c: Coincident(g89,g90)
    c: Coincident(g90,g91)
    c: Coincident(g91,g92)
    c: Coincident(g92,g93)
    c: Coincident(g93,g94)
    c: Coincident(g94,g95)
    c: Coincident(g95,g96)
    c: Coincident(g96,g97)
    c: Coincident(g97,g98)
    c: Coincident(g98,g99)
    c: Coincident(g99,g100)
    c: Coincident(g100,g101)
    c: Coincident(g101,g102)
    c: Coincident(g102,g103)
    c: Coincident(g103,g104)
    c: Coincident(g104,g105)
    c: Coincident(g105,g76)
    c: Coincident(g106,g107)
    c: Coincident(g107,g108)
    c: Coincident(g108,g109)
    c: Coincident(g109,g110)
    c: Coincident(g110,g111)
    c: Coincident(g111,g112)
    c: Coincident(g112,g113)
    c: Coincident(g113,g114)
    c: Coincident(g114,g115)
    c: Coincident(g115,g116)
    c: Coincident(g116,g117)
    c: Coincident(g117,g106)
    c: Coincident(g118,g119)
    c: Coincident(g119,g120)
    c: Coincident(g120,g121)
    c: Coincident(g121,g122)
    c: Coincident(g122,g123)
    c: Coincident(g123,g124)
    c: Coincident(g124,g125)
    c: Coincident(g125,g118)
    c: Coincident(g126,g127)
    c: Coincident(g127,g128)
    c: Coincident(g128,g129)
    c: Coincident(g129,g130)
    c: Coincident(g130,g131)
    c: Coincident(g131,g132)
    c: Coincident(g132,g133)
    c: Coincident(g133,g134)
    c: Coincident(g134,g135)
    c: Coincident(g135,g136)
    c: Coincident(g136,g137)
    c: Coincident(g137,g138)
    c: Coincident(g138,g139)
    c: Coincident(g139,g140)
    c: Coincident(g140,g141)
    c: Coincident(g141,g142)
    c: Coincident(g142,g143)
    c: Coincident(g143,g144)
    c: Coincident(g144,g145)
    c: Coincident(g145,g146)
    c: Coincident(g146,g147)
    c: Coincident(g147,g126)
    c: Coincident(g148,g149)
    c: Coincident(g149,g150)
    c: Coincident(g150,g151)
    c: Coincident(g151,g152)
    c: Coincident(g152,g153)
    c: Coincident(g153,g154)
    c: Coincident(g154,g155)
    c: Coincident(g155,g156)
    c: Coincident(g156,g157)
    c: Coincident(g157,g158)
    c: Coincident(g158,g159)
    c: Coincident(g159,g148)
    c: Coincident(g160,g161)
    c: Coincident(g161,g162)
    c: Coincident(g162,g163)
    c: Coincident(g163,g164)
    c: Coincident(g164,g165)
    c: Coincident(g165,g166)
    c: Coincident(g166,g167)
    c: Coincident(g167,g160)
FEATURE [Sketcher::SketchObject] Sketch100
  Placement = pos=(0,0,4) rot=(0,0,1;0rad)
  sketch-geometry (107):
    g0: LineSegment [constr] StartX=0 StartY=0 StartZ=0 EndX=3.32659 EndY=15.6504 EndZ=0
    g1: LineSegment [constr] StartX=0 StartY=0 StartZ=0 EndX=4.94427 EndY=15.2169 EndZ=0
    g2: LineSegment [constr] StartX=0 StartY=0 StartZ=0 EndX=6.50779 EndY=14.6167 EndZ=0
    g3: LineSegment [constr] StartX=0 StartY=0 StartZ=0 EndX=9.40456 EndY=12.9443 EndZ=0
    g4: LineSegment [constr] StartX=0 StartY=0 StartZ=0 EndX=10.7061 EndY=11.8903 EndZ=0
    g5: LineSegment [constr] StartX=0 StartY=0 StartZ=0 EndX=11.8903 EndY=10.7061 EndZ=0
    g6: LineSegment [constr] StartX=0 StartY=0 StartZ=0 EndX=12.9443 EndY=9.40456 EndZ=0
    g7: LineSegment [constr] StartX=0 StartY=0 StartZ=0 EndX=14.6167 EndY=6.50779 EndZ=0
    g8: LineSegment [constr] StartX=0 StartY=0 StartZ=0 EndX=15.2169 EndY=4.94427 EndZ=0
    g9: LineSegment [constr] StartX=0 StartY=0 StartZ=0 EndX=15.6504 EndY=3.32659 EndZ=0
    g10: LineSegment [constr] StartX=0 StartY=0 StartZ=0 EndX=15.9124 EndY=1.67246 EndZ=0
    g11: ArcOfCircle CenterX=-1.2e-14 CenterY=0 CenterZ=0 NormalX=0 NormalY=0 NormalZ=1 AngleXU=0 Radius=16 StartAngle=1.37073 EndAngle=1.51844
    g12: ArcOfCircle CenterX=-1.2e-14 CenterY=0 CenterZ=0 NormalX=0 NormalY=0 NormalZ=1 AngleXU=0 Radius=16 StartAngle=1.26601 EndAngle=1.35198
    g13: ArcOfCircle CenterX=-1.2e-14 CenterY=0 CenterZ=0 NormalX=0 NormalY=0 NormalZ=1 AngleXU=0 Radius=16 StartAngle=1.16129 EndAngle=1.24726
    g14: ArcOfCircle CenterX=-1.2e-14 CenterY=0 CenterZ=0 NormalX=0 NormalY=0 NormalZ=1 AngleXU=0 Radius=16 StartAngle=0.951853 EndAngle=1.14254
    g15: ArcOfCircle CenterX=-1.2e-14 CenterY=0 CenterZ=0 NormalX=0 NormalY=0 NormalZ=1 AngleXU=0 Radius=16 StartAngle=0.847133 EndAngle=0.933103
    g16: ArcOfCircle CenterX=-1.2e-14 CenterY=0 CenterZ=0 NormalX=0 NormalY=0 NormalZ=1 AngleXU=0 Radius=16 StartAngle=0.742413 EndAngle=0.828383
    g17: ArcOfCircle CenterX=-1.2e-14 CenterY=0 CenterZ=0 NormalX=0 NormalY=0 NormalZ=1 AngleXU=0 Radius=16 StartAngle=0.637694 EndAngle=0.723663
    g18: ArcOfCircle CenterX=-1.2e-14 CenterY=0 CenterZ=0 NormalX=0 NormalY=0 NormalZ=1 AngleXU=0 Radius=16 StartAngle=0.428254 EndAngle=0.618943
    g19: ArcOfCircle CenterX=-1.2e-14 CenterY=0 CenterZ=0 NormalX=0 NormalY=0 NormalZ=1 AngleXU=0 Radius=16 StartAngle=0.323534 EndAngle=0.409504
    g20: ArcOfCircle CenterX=-1.2e-14 CenterY=0 CenterZ=0 NormalX=0 NormalY=0 NormalZ=1 AngleXU=0 Radius=16 StartAngle=0.218815 EndAngle=0.304784
    g21: ArcOfCircle CenterX=-1.2e-14 CenterY=0 CenterZ=0 NormalX=0 NormalY=0 NormalZ=1 AngleXU=0 Radius=16 StartAngle=0.114095 EndAngle=0.200064
    g22: LineSegment [constr] StartX=15.9273 StartY=1.5232 StartZ=0 EndX=15.896 EndY=1.82156 EndZ=0
    g23: LineSegment [constr] StartX=15.6185 StartY=3.47316 StartZ=0 EndX=15.6809 EndY=3.17972 EndZ=0
    g24: LineSegment [constr] StartX=15.1699 StartY=5.08671 StartZ=0 EndX=15.2626 EndY=4.8014 EndZ=0
    g25: LineSegment [constr] StartX=14.6771 StartY=6.37047 StartZ=0 EndX=14.5551 EndY=6.64453 EndZ=0
    g26: LineSegment [constr] StartX=12.8555 StartY=9.5255 StartZ=0 EndX=13.0319 EndY=9.2828 EndZ=0
    g27: LineSegment [constr] StartX=11.9902 StartY=10.5941 StartZ=0 EndX=11.7894 EndY=10.8171 EndZ=0
    g28: LineSegment [constr] StartX=10.5941 StartY=11.9902 StartZ=0 EndX=10.8171 EndY=11.7894 EndZ=0
    g29: LineSegment [constr] StartX=9.2828 StartY=13.0319 StartZ=0 EndX=9.5255 EndY=12.8555 EndZ=0
    g30: LineSegment [constr] StartX=6.37047 StartY=14.6771 StartZ=0 EndX=6.64453 EndY=14.5551 EndZ=0
    g31: LineSegment [constr] StartX=4.8014 StartY=15.2626 StartZ=0 EndX=5.08671 EndY=15.1699 EndZ=0
    g32: LineSegment [constr] StartX=3.17972 StartY=15.6809 StartZ=0 EndX=3.47316 EndY=15.6185 EndZ=0
    g33: LineSegment StartX=3.17972 StartY=15.6809 StartZ=0 EndX=3.41896 EndY=16.8064 EndZ=0
    g34: ArcOfCircle CenterX=3.46787 CenterY=16.796 CenterZ=0 NormalX=0 NormalY=0 NormalZ=1 AngleXU=0 Radius=0.05 StartAngle=1.36136 EndAngle=2.93215
    g35: LineSegment StartX=3.47827 StartY=16.8449 StartZ=0 EndX=3.6739 EndY=16.8033 EndZ=0
    g36: ArcOfCircle CenterX=3.6635 CenterY=16.7544 CenterZ=0 NormalX=0 NormalY=0 NormalZ=1 AngleXU=0 Radius=0.05 StartAngle=6.07375 EndAngle=7.64454
    g37: LineSegment StartX=3.71241 StartY=16.744 StartZ=0 EndX=3.47316 EndY=15.6185 EndZ=0
    g38: GeomPoint X=3.57608 Y=16.8241 Z=0
    g39: Circle [constr] CenterX=-1.2e-14 CenterY=0 CenterZ=0 NormalX=0 NormalY=0 NormalZ=1 AngleXU=0 Radius=17.2
    g40: LineSegment StartX=4.8014 StartY=15.2626 StartZ=0 EndX=5.15698 EndY=16.357 EndZ=0
    g41: ArcOfCircle CenterX=5.20454 CenterY=16.3415 CenterZ=0 NormalX=0 NormalY=0 NormalZ=1 AngleXU=0 Radius=0.05 StartAngle=1.25664 EndAngle=2.82743
    g42: LineSegment StartX=5.21999 StartY=16.3891 StartZ=0 EndX=5.4102 EndY=16.3273 EndZ=0
    g43: ArcOfCircle CenterX=5.39475 CenterY=16.2797 CenterZ=0 NormalX=0 NormalY=0 NormalZ=1 AngleXU=0 Radius=0.05 StartAngle=5.96903 EndAngle=7.53982
    g44: LineSegment StartX=5.4423 StartY=16.2643 StartZ=0 EndX=5.08671 EndY=15.1699 EndZ=0
    g45: GeomPoint X=5.31509 Y=16.3582 Z=0
    g46: LineSegment StartX=6.37047 StartY=14.6771 StartZ=0 EndX=6.8385 EndY=15.7283 EndZ=0
    g47: ArcOfCircle CenterX=6.88418 CenterY=15.708 CenterZ=0 NormalX=0 NormalY=0 NormalZ=1 AngleXU=0 Radius=0.05 StartAngle=1.15192 EndAngle=2.72271
    g48: LineSegment StartX=6.90452 StartY=15.7537 StartZ=0 EndX=7.08722 EndY=15.6723 EndZ=0
    g49: GeomPoint X=6.99587 Y=15.713 Z=0
    g50: ArcOfCircle CenterX=7.06689 CenterY=15.6266 CenterZ=0 NormalX=0 NormalY=0 NormalZ=1 AngleXU=0 Radius=0.05 StartAngle=5.86431 EndAngle=7.4351
    g51: LineSegment StartX=7.11257 StartY=15.6063 StartZ=0 EndX=6.64453 EndY=14.5551 EndZ=0
    g52: LineSegment StartX=9.2828 StartY=13.0319 StartZ=0 EndX=9.95916 EndY=13.9628 EndZ=0
    g53: ArcOfCircle CenterX=9.99962 CenterY=13.9334 CenterZ=0 NormalX=0 NormalY=0 NormalZ=1 AngleXU=0 Radius=0.05 StartAngle=0.942478 EndAngle=2.51327
    g54: LineSegment StartX=10.029 StartY=13.9739 StartZ=0 EndX=10.1908 EndY=13.8563 EndZ=0
    g55: GeomPoint X=10.1099 Y=13.9151 Z=0
    g56: ArcOfCircle CenterX=10.1614 CenterY=13.8159 CenterZ=0 NormalX=0 NormalY=0 NormalZ=1 AngleXU=0 Radius=0.05 StartAngle=5.65487 EndAngle=7.22566
    g57: LineSegment StartX=10.2019 StartY=13.7865 StartZ=0 EndX=9.5255 EndY=12.8555 EndZ=0
    g58: LineSegment StartX=10.5941 StartY=11.9902 StartZ=0 EndX=11.3641 EndY=12.8453 EndZ=0
    g59: ArcOfCircle CenterX=11.4013 CenterY=12.8118 CenterZ=0 NormalX=0 NormalY=0 NormalZ=1 AngleXU=0 Radius=0.05 StartAngle=0.837758 EndAngle=2.40855
    g60: LineSegment StartX=11.4347 StartY=12.849 StartZ=0 EndX=11.5834 EndY=12.7152 EndZ=0
    g61: GeomPoint X=11.509 Y=12.7821 Z=0
    g62: ArcOfCircle CenterX=11.5499 CenterY=12.678 CenterZ=0 NormalX=0 NormalY=0 NormalZ=1 AngleXU=0 Radius=0.05 StartAngle=5.55015 EndAngle=7.12094
    g63: LineSegment StartX=11.5871 StartY=12.6446 StartZ=0 EndX=10.8171 EndY=11.7894 EndZ=0
    g64: LineSegment StartX=11.7894 StartY=10.8171 StartZ=0 EndX=12.6446 EndY=11.5871 EndZ=0
    g65: ArcOfCircle CenterX=12.678 CenterY=11.5499 CenterZ=0 NormalX=0 NormalY=0 NormalZ=1 AngleXU=0 Radius=0.05 StartAngle=0.733038 EndAngle=2.30383
    g66: LineSegment StartX=12.7152 StartY=11.5834 StartZ=0 EndX=12.849 EndY=11.4347 EndZ=0
    g67: GeomPoint X=12.7821 Y=11.509 Z=0
    g68: ArcOfCircle CenterX=12.8118 CenterY=11.4013 CenterZ=0 NormalX=0 NormalY=0 NormalZ=1 AngleXU=0 Radius=0.05 StartAngle=5.44543 EndAngle=7.01622
    g69: LineSegment StartX=12.8453 StartY=11.3641 StartZ=0 EndX=11.9902 EndY=10.5941 EndZ=0
    g70: LineSegment StartX=12.8555 StartY=9.5255 StartZ=0 EndX=13.7865 EndY=10.2019 EndZ=0
    g71: ArcOfCircle CenterX=13.8159 CenterY=10.1614 CenterZ=0 NormalX=0 NormalY=0 NormalZ=1 AngleXU=0 Radius=0.05 StartAngle=0.628319 EndAngle=2.19911
    g72: LineSegment StartX=13.8563 StartY=10.1908 StartZ=0 EndX=13.9739 EndY=10.029 EndZ=0
    g73: GeomPoint X=13.9151 Y=10.1099 Z=0
    g74: ArcOfCircle CenterX=13.9334 CenterY=9.99962 CenterZ=0 NormalX=0 NormalY=0 NormalZ=1 AngleXU=0 Radius=0.05 StartAngle=5.34071 EndAngle=6.9115
    g75: LineSegment StartX=13.9628 StartY=9.95916 StartZ=0 EndX=13.0319 EndY=9.2828 EndZ=0
    g76: LineSegment StartX=14.5551 StartY=6.64453 StartZ=0 EndX=15.6063 EndY=7.11257 EndZ=0
    g77: ArcOfCircle CenterX=15.6266 CenterY=7.06689 CenterZ=0 NormalX=0 NormalY=0 NormalZ=1 AngleXU=0 Radius=0.05 StartAngle=0.418879 EndAngle=1.98968
    g78: LineSegment StartX=15.6723 StartY=7.08722 StartZ=0 EndX=15.7537 EndY=6.90452 EndZ=0
    g79: GeomPoint X=15.713 Y=6.99587 Z=0
    g80: ArcOfCircle CenterX=15.708 CenterY=6.88418 CenterZ=0 NormalX=0 NormalY=0 NormalZ=1 AngleXU=0 Radius=0.05 StartAngle=5.13127 EndAngle=6.70206
    g81: LineSegment StartX=15.7283 StartY=6.8385 StartZ=0 EndX=14.6771 EndY=6.37047 EndZ=0
    g82: LineSegment StartX=15.1699 StartY=5.08671 StartZ=0 EndX=16.2643 EndY=5.4423 EndZ=0
    g83: ArcOfCircle CenterX=16.2797 CenterY=5.39475 CenterZ=0 NormalX=0 NormalY=0 NormalZ=1 AngleXU=0 Radius=0.05 StartAngle=0.314159 EndAngle=1.88496
    g84: LineSegment StartX=16.3273 StartY=5.4102 StartZ=0 EndX=16.3891 EndY=5.21999 EndZ=0
    g85: GeomPoint X=16.3582 Y=5.31509 Z=0
    g86: ArcOfCircle CenterX=16.3415 CenterY=5.20454 CenterZ=0 NormalX=0 NormalY=0 NormalZ=1 AngleXU=0 Radius=0.05 StartAngle=5.02655 EndAngle=6.59734
    g87: LineSegment StartX=16.357 StartY=5.15698 StartZ=0 EndX=15.2626 EndY=4.8014 EndZ=0
    g88: LineSegment StartX=15.6185 StartY=3.47316 StartZ=0 EndX=16.744 EndY=3.71241 EndZ=0
    g89: ArcOfCircle CenterX=16.7544 CenterY=3.6635 CenterZ=0 NormalX=0 NormalY=0 NormalZ=1 AngleXU=0 Radius=0.05 StartAngle=0.20944 EndAngle=1.78024
    g90: LineSegment StartX=16.8033 StartY=3.6739 StartZ=0 EndX=16.8449 EndY=3.47827 EndZ=0
    g91: GeomPoint X=16.8241 Y=3.57608 Z=0
    g92: ArcOfCircle CenterX=16.796 CenterY=3.46787 CenterZ=0 NormalX=0 NormalY=0 NormalZ=1 AngleXU=0 Radius=0.05 StartAngle=4.92183 EndAngle=6.49262
    g93: LineSegment StartX=16.8064 StartY=3.41896 StartZ=0 EndX=15.6809 EndY=3.17972 EndZ=0
    g94: LineSegment StartX=15.896 StartY=1.82156 StartZ=0 EndX=17.0404 EndY=1.94184 EndZ=0
    g95: ArcOfCircle CenterX=17.0456 CenterY=1.89212 CenterZ=0 NormalX=0 NormalY=0 NormalZ=1 AngleXU=0 Radius=0.05 StartAngle=0.10472 EndAngle=1.67552
    g96: LineSegment StartX=17.0953 StartY=1.89734 StartZ=0 EndX=17.1162 EndY=1.69844 EndZ=0
    g97: GeomPoint X=17.1058 Y=1.79789 Z=0
    g98: ArcOfCircle CenterX=17.0665 CenterY=1.69321 CenterZ=0 NormalX=0 NormalY=0 NormalZ=1 AngleXU=0 Radius=0.05 StartAngle=4.81711 EndAngle=6.38791
    g99: LineSegment StartX=17.0717 StartY=1.64348 StartZ=0 EndX=15.9273 EndY=1.5232 EndZ=0
    g100: Circle CenterX=0 CenterY=17.6 CenterZ=0 NormalX=0 NormalY=0 NormalZ=1 AngleXU=0 Radius=0.9
    g101: LineSegment StartX=0.837375 StartY=15.9781 StartZ=0 EndX=3.9919 EndY=18.7804 EndZ=0
    g102: LineSegment StartX=-0.837375 StartY=15.9781 StartZ=0 EndX=-3.9919 EndY=18.7804 EndZ=0
    g103: ArcOfCircle CenterX=-1.2e-14 CenterY=0 CenterZ=0 NormalX=0 NormalY=0 NormalZ=1 AngleXU=0 Radius=16 StartAngle=1.62316 EndAngle=6.37853
    g104: ArcOfCircle CenterX=-1.2e-14 CenterY=0 CenterZ=0 NormalX=0 NormalY=0 NormalZ=1 AngleXU=0 Radius=19.2 StartAngle=1.78024 EndAngle=7.64454
    g105: LineSegment [constr] StartX=3.57608 StartY=16.8241 StartZ=0 EndX=3.9919 EndY=18.7804 EndZ=0
    g106: LineSegment [constr] StartX=0.837375 StartY=15.9781 StartZ=0 EndX=-1.2e-14 EndY=0 EndZ=0
  constraints (241):
    c: Coincident(g0,g-1)
    c: Coincident(g1,g-1)
    c: Coincident(g2,g-1)
    c: Coincident(g3,g-1)
    c: Coincident(g4,g-1)
    c: Coincident(g5,g-1)
    c: Coincident(g6,g-1)
    c: Coincident(g7,g-1)
    c: Coincident(g8,g-1)
    c: Coincident(g9,g-1)
    c: Coincident(g10,g-1)
    c: Angle(g0,g-2) = 0.20944
    c: Angle(g1,g0) = 0.10472
    c: Angle(g2,g1) = 0.10472
    c: Angle(g3,g2) = 0.20944
    c: Angle(g4,g3) = 0.10472
    c: Angle(g5,g4) = 0.10472
    c: Angle(g6,g5) = 0.10472
    c: Angle(g7,g6) = 0.20944
    c: Angle(g8,g7) = 0.10472
    c: Angle(g9,g8) = 0.10472
    c: Angle(g10,g9) = 0.10472
    c: Coincident(g11,g-1)
    c: Radius(g11) = 16
    c: PointOnObject(g0,g11)
    c: PointOnObject(g1,g11)
    c: PointOnObject(g2,g11)
    c: PointOnObject(g3,g11)
    c: PointOnObject(g4,g11)
    c: PointOnObject(g5,g11)
    c: PointOnObject(g6,g11)
    c: PointOnObject(g7,g11)
    c: PointOnObject(g8,g11)
    c: PointOnObject(g9,g11)
    c: PointOnObject(g10,g11)
    c: Coincident(g12,g11)
    c: Coincident(g13,g11)
    c: Coincident(g14,g11)
    c: Coincident(g15,g11)
    c: Coincident(g16,g11)
    c: Coincident(g17,g11)
    c: Coincident(g18,g11)
    c: Coincident(g19,g11)
    c: Coincident(g20,g11)
    c: Coincident(g21,g11)
    c: Symmetric(g11,g12,g0)
    c: Symmetric(g12,g13,g1)
    c: Symmetric(g13,g14,g2)
    c: Symmetric(g14,g15,g3)
    c: Symmetric(g15,g16,g4)
    c: Symmetric(g16,g17,g5)
    c: Symmetric(g17,g18,g6)
    c: Symmetric(g18,g19,g7)
    c: Symmetric(g19,g20,g8)
    c: Symmetric(g20,g21,g9)
    c: Symmetric(g21,g103,g10)
    c: Coincident(g22,g103)
    c: Coincident(g22,g21)
    c: Coincident(g23,g20)
    c: Coincident(g23,g21)
    c: Coincident(g24,g19)
    c: Coincident(g24,g20)
    c: Coincident(g25,g19)
    c: Coincident(g25,g18)
    c: Coincident(g26,g17)
    c: Coincident(g26,g18)
    c: Coincident(g27,g17)
    c: Coincident(g27,g16)
    c: Coincident(g28,g15)
    c: Coincident(g28,g16)
    c: Coincident(g29,g14)
    c: Coincident(g29,g15)
    c: Coincident(g30,g13)
    c: Coincident(g30,g14)
    c: Coincident(g31,g12)
    c: Coincident(g31,g13)
    c: Coincident(g32,g11)
    c: Coincident(g32,g12)
    c: Distance(g32) = 0.3
    c: Equal(g32,g31)
    c: Equal(g31,g30)
    c: Equal(g30,g29)
    c: Equal(g29,g28)
    c: Equal(g28,g27)
    c: Equal(g27,g26)
    c: Equal(g26,g25)
    c: Equal(g25,g24)
    c: Equal(g24,g23)
    c: Equal(g23,g22)
    c: Tangent(g33,g34) = 1.5708
    c: Tangent(g34,g35) = 1.5708
    c: Tangent(g35,g36) = 1.5708
    c: Tangent(g36,g37) = 1.5708
    c: Symmetric(g34,g35,g38)
    c: Coincident(g37,g12)
    c: Coincident(g11,g33)
    c: Equal(g34,g36)
    c: Parallel(g0,g37)
    c: Radius(g36) = 0.05
    c: Symmetric(g33,g36,g0)
    c: Distance(g38,g0) = 1.2
    c: Coincident(g39,g11)
    c: PointOnObject(g38,g39)
    c: Tangent(g40,g41) = 1.5708
    c: Tangent(g41,g42) = 1.5708
    c: Tangent(g42,g43) = 1.5708
    c: Tangent(g43,g44) = 1.5708
    c: Equal(g41,g43)
    c: Equal(g36,g43) = 0.05
    c: Coincident(g40,g12)
    c: Coincident(g44,g13)
    c: PointOnObject(g45,g39)
    c: Symmetric(g41,g42,g1)
    c: Parallel(g44,g1)
    c: Symmetric(g41,g42,g45)
    c: Tangent(g46,g47) = 1.5708
    c: Tangent(g47,g48) = 1.5708
    c: Tangent(g48,g50) = 1.5708
    c: Tangent(g50,g51) = 1.5708
    c: Symmetric(g47,g48,g49)
    c: Coincident(g46,g13)
    c: Coincident(g51,g14)
    c: Parallel(g51,g2)
    c: PointOnObject(g49,g39)
    c: Radius(g47) = 0.05
    c: Equal(g50,g47)
    c: Symmetric(g50,g46,g2)
    c: Tangent(g52,g53) = 1.5708
    c: Tangent(g53,g54) = 1.5708
    c: Tangent(g54,g56) = 1.5708
    c: Tangent(g56,g57) = 1.5708
    c: Symmetric(g53,g54,g55)
    c: Equal(g53,g56)
    c: Equal(g36,g56) = 0.05
    c: Coincident(g14,g52)
    c: Coincident(g15,g57)
    c: Parallel(g57,g3)
    c: PointOnObject(g55,g39)
    c: Symmetric(g52,g56,g3)
    c: Tangent(g58,g59) = 1.5708
    c: Tangent(g59,g60) = 1.5708
    c: Tangent(g60,g62) = 1.5708
    c: Tangent(g62,g63) = 1.5708
    c: Symmetric(g59,g60,g61)
    c: Equal(g59,g62)
    c: Equal(g36,g62) = 0.05
    c: Coincident(g58,g15)
    c: Coincident(g16,g63)
    c: PointOnObject(g61,g39)
    c: Parallel(g4,g63)
    c: Symmetric(g58,g62,g4)
    c: Tangent(g64,g65) = 1.5708
    c: Tangent(g65,g66) = 1.5708
    c: Tangent(g66,g68) = 1.5708
    c: Tangent(g68,g69) = 1.5708
    c: Symmetric(g65,g66,g67)
    c: Equal(g65,g68)
    c: Equal(g36,g68) = 0.05
    c: Coincident(g64,g16)
    c: Coincident(g69,g17)
    c: PointOnObject(g67,g39)
    c: Parallel(g69,g5)
    c: Symmetric(g65,g66,g5)
    c: Tangent(g70,g71) = 1.5708
    c: Tangent(g71,g72) = 1.5708
    c: Tangent(g72,g74) = 1.5708
    c: Tangent(g74,g75) = 1.5708
    c: Symmetric(g71,g72,g73)
    c: Equal(g71,g74)
    c: Equal(g36,g74) = 0.05
    c: Coincident(g70,g17)
    c: Coincident(g75,g18)
    c: PointOnObject(g73,g39)
    c: Parallel(g75,g6)
    c: Symmetric(g74,g70,g6)
    c: Tangent(g76,g77) = 1.5708
    c: Tangent(g77,g78) = 1.5708
    c: Tangent(g78,g80) = 1.5708
    c: Tangent(g80,g81) = 1.5708
    c: Symmetric(g77,g78,g79)
    c: Equal(g77,g80)
    c: Equal(g36,g80) = 0.05
    c: PointOnObject(g79,g39)
    c: Coincident(g76,g18)
    c: Coincident(g81,g19)
    c: Parallel(g81,g7)
    c: Symmetric(g76,g80,g7)
    c: Tangent(g82,g83) = 1.5708
    c: Tangent(g83,g84) = 1.5708
    c: Tangent(g84,g86) = 1.5708
    c: Tangent(g86,g87) = 1.5708
    c: Symmetric(g83,g84,g85)
    c: Equal(g83,g86)
    c: Equal(g36,g86) = 0.05
    c: PointOnObject(g85,g39)
    c: Coincident(g82,g19)
    c: Coincident(g20,g87)
    c: Parallel(g87,g8)
    c: Symmetric(g82,g86,g8)
    c: Tangent(g88,g89) = 1.5708
    c: Tangent(g89,g90) = 1.5708
    c: Tangent(g90,g92) = 1.5708
    c: Tangent(g92,g93) = 1.5708
    c: Symmetric(g89,g90,g91)
    c: Equal(g89,g92)
    c: Equal(g36,g92) = 0.05
    c: Coincident(g20,g88)
    c: PointOnObject(g91,g39)
    c: Coincident(g21,g93)
    c: Parallel(g9,g93)
    c: Symmetric(g88,g92,g9)
    c: Tangent(g94,g95) = 1.5708
    c: Tangent(g95,g96) = 1.5708
    c: Tangent(g96,g98) = 1.5708
    c: Tangent(g98,g99) = 1.5708
    c: Symmetric(g95,g96,g97)
    c: Equal(g95,g98)
    c: Equal(g36,g98) = 0.05
    c: PointOnObject(g97,g39)
    c: Coincident(g94,g21)
    c: Coincident(g99,g103)
    c: Parallel(g99,g10)
    c: Symmetric(g94,g98,g10)
    c: PointOnObject(g100,g-2)
    c: DistanceY(g100) = 17.6
    c: Radius(g100) = 0.9
    c: Coincident(g11,g101)
    c: Coincident(g103,g102)
    c: Coincident(g11,g103)
    c: Symmetric(g102,g11,g-2)
    c: Symmetric(g102,g101,g-2)
    c: Coincident(g104,g11)
    c: Coincident(g104,g101)
    c: Coincident(g104,g102)
    c: Radius(g104) = 19.2
    c: Coincident(g105,g38)
    c: Parallel(g0,g105)
    c: Coincident(g101,g105)
    c: Coincident(g106,g11)
    c: Coincident(g106,g11)
    c: Angle(g106,g-2) = 0.0523599
FEATURE [Sketcher::SketchObject] Sketch101
  Placement = pos=(0,0,4) rot=(0,0,1;0rad)
  sketch-geometry (340):
    g0: LineSegment [constr] StartX=0 StartY=0 StartZ=0 EndX=8.8 EndY=15.242 EndZ=0
    g1: LineSegment [constr] StartX=15.242 StartY=8.8 StartZ=0 EndX=0 EndY=0 EndZ=0
    g2: LineSegment [constr] StartX=8.8 StartY=-15.242 StartZ=0 EndX=0 EndY=0 EndZ=0
    g3: LineSegment [constr] StartX=0 StartY=0 StartZ=0 EndX=-8.8 EndY=-15.242 EndZ=0
    g4: LineSegment [constr] StartX=0 StartY=0 StartZ=0 EndX=-8.8 EndY=15.242 EndZ=0
    g5: LineSegment StartX=8.70981 StartY=14.4858 StartZ=0 EndX=9.40981 EndY=15.6983 EndZ=0
    g6: LineSegment StartX=9.3366 StartY=15.9715 StartZ=0 EndX=9.1634 EndY=16.0715 EndZ=0
    g7: LineSegment StartX=8.89019 StartY=15.9983 StartZ=0 EndX=8.19019 EndY=14.7858 EndZ=0
    g8: LineSegment StartX=8.2634 StartY=14.5126 StartZ=0 EndX=8.4366 EndY=14.4126 EndZ=0
    g9: Circle [constr] CenterX=0 CenterY=0 CenterZ=0 NormalX=0 NormalY=0 NormalZ=1 AngleXU=0 Radius=19.2
    g10: Circle [constr] CenterX=0 CenterY=0 CenterZ=0 NormalX=0 NormalY=0 NormalZ=1 AngleXU=0 Radius=17.6
    g11: ArcOfCircle CenterX=9.0634 CenterY=15.8983 CenterZ=0 NormalX=0 NormalY=0 NormalZ=1 AngleXU=0 Radius=0.2 StartAngle=1.0472 EndAngle=2.61799
    g12: ArcOfCircle CenterX=9.2366 CenterY=15.7983 CenterZ=0 NormalX=0 NormalY=0 NormalZ=1 AngleXU=0 Radius=0.2 StartAngle=5.75959 EndAngle=7.33038
    g13: ArcOfCircle CenterX=8.3634 CenterY=14.6858 CenterZ=0 NormalX=0 NormalY=0 NormalZ=1 AngleXU=0 Radius=0.2 StartAngle=2.61799 EndAngle=4.18879
    g14: ArcOfCircle CenterX=8.5366 CenterY=14.5858 CenterZ=0 NormalX=0 NormalY=0 NormalZ=1 AngleXU=0 Radius=0.2 StartAngle=4.18879 EndAngle=5.75959
    g15: LineSegment StartX=14.8233 StartY=8.12524 StartZ=0 EndX=16.0358 EndY=8.82524 EndZ=0
    g16: LineSegment StartX=16.109 StartY=9.09845 StartZ=0 EndX=15.934 EndY=9.40155 EndZ=0
    g17: LineSegment StartX=15.6608 StartY=9.47476 StartZ=0 EndX=14.4483 EndY=8.77476 EndZ=0
    g18: LineSegment StartX=14.3751 StartY=8.50155 StartZ=0 EndX=14.5501 EndY=8.19845 EndZ=0
    g19: ArcOfCircle CenterX=15.7608 CenterY=9.30155 CenterZ=0 NormalX=0 NormalY=0 NormalZ=1 AngleXU=0 Radius=0.2 StartAngle=0.523599 EndAngle=2.0944
    g20: ArcOfCircle CenterX=15.9358 CenterY=8.99845 CenterZ=0 NormalX=0 NormalY=0 NormalZ=1 AngleXU=0 Radius=0.2 StartAngle=5.23599 EndAngle=6.80678
    g21: ArcOfCircle CenterX=14.5483 CenterY=8.60155 CenterZ=0 NormalX=0 NormalY=0 NormalZ=1 AngleXU=0 Radius=0.2 StartAngle=2.0944 EndAngle=3.66519
    g22: ArcOfCircle CenterX=14.7233 CenterY=8.29845 CenterZ=0 NormalX=0 NormalY=0 NormalZ=1 AngleXU=0 Radius=0.2 StartAngle=3.66519 EndAngle=5.23599
    g23: LineSegment StartX=16.9 StartY=-0.3 StartZ=0 EndX=18.3 EndY=-0.3 EndZ=0
    g24: LineSegment StartX=18.5 StartY=-0.1 StartZ=0 EndX=18.5 EndY=0.1 EndZ=0
    g25: LineSegment StartX=18.3 StartY=0.3 StartZ=0 EndX=16.9 EndY=0.3 EndZ=0
    g26: LineSegment StartX=16.7 StartY=0.1 StartZ=0 EndX=16.7 EndY=-0.1 EndZ=0
    g27: ArcOfCircle CenterX=18.3 CenterY=0.1 CenterZ=0 NormalX=0 NormalY=0 NormalZ=1 AngleXU=0 Radius=0.2 StartAngle=0 EndAngle=1.5708
    g28: ArcOfCircle CenterX=18.3 CenterY=-0.1 CenterZ=0 NormalX=0 NormalY=0 NormalZ=1 AngleXU=0 Radius=0.2 StartAngle=4.71239 EndAngle=6.28319
    g29: ArcOfCircle CenterX=16.9 CenterY=0.1 CenterZ=0 NormalX=0 NormalY=0 NormalZ=1 AngleXU=0 Radius=0.2 StartAngle=1.5708 EndAngle=3.14159
    g30: ArcOfCircle CenterX=16.9 CenterY=-0.1 CenterZ=0 NormalX=0 NormalY=0 NormalZ=1 AngleXU=0 Radius=0.2 StartAngle=3.14159 EndAngle=4.71239
    g31: GeomPoint X=17.6 Y=0 Z=0
    g32: LineSegment StartX=9.40981 StartY=-15.6983 StartZ=0 EndX=8.70981 EndY=-14.4858 EndZ=0
    g33: LineSegment StartX=8.4366 StartY=-14.4126 StartZ=0 EndX=8.2634 EndY=-14.5126 EndZ=0
    g34: LineSegment StartX=8.19019 StartY=-14.7858 StartZ=0 EndX=8.89019 EndY=-15.9983 EndZ=0
    g35: LineSegment StartX=9.1634 StartY=-16.0715 StartZ=0 EndX=9.3366 EndY=-15.9715 EndZ=0
    g36: ArcOfCircle CenterX=8.3634 CenterY=-14.6858 CenterZ=0 NormalX=0 NormalY=0 NormalZ=1 AngleXU=0 Radius=0.2 StartAngle=2.0944 EndAngle=3.66519
    g37: ArcOfCircle CenterX=8.5366 CenterY=-14.5858 CenterZ=0 NormalX=0 NormalY=0 NormalZ=1 AngleXU=0 Radius=0.2 StartAngle=0.523599 EndAngle=2.0944
    g38: ArcOfCircle CenterX=9.0634 CenterY=-15.8983 CenterZ=0 NormalX=0 NormalY=0 NormalZ=1 AngleXU=0 Radius=0.2 StartAngle=3.66519 EndAngle=5.23599
    g39: ArcOfCircle CenterX=9.2366 CenterY=-15.7983 CenterZ=0 NormalX=0 NormalY=0 NormalZ=1 AngleXU=0 Radius=0.2 StartAngle=5.23599 EndAngle=6.80678
    g40: LineSegment StartX=-8.19019 StartY=14.7858 StartZ=0 EndX=-8.89019 EndY=15.9983 EndZ=0
    g41: LineSegment StartX=-9.1634 StartY=16.0715 StartZ=0 EndX=-9.3366 EndY=15.9715 EndZ=0
    g42: LineSegment StartX=-9.40981 StartY=15.6983 StartZ=0 EndX=-8.70981 EndY=14.4858 EndZ=0
    g43: LineSegment StartX=-8.4366 StartY=14.4126 StartZ=0 EndX=-8.2634 EndY=14.5126 EndZ=0
    g44: ArcOfCircle CenterX=-9.2366 CenterY=15.7983 CenterZ=0 NormalX=0 NormalY=0 NormalZ=1 AngleXU=0 Radius=0.2 StartAngle=2.0944 EndAngle=3.66519
    g45: ArcOfCircle CenterX=-9.0634 CenterY=15.8983 CenterZ=0 NormalX=0 NormalY=0 NormalZ=1 AngleXU=0 Radius=0.2 StartAngle=0.523599 EndAngle=2.0944
    g46: ArcOfCircle CenterX=-8.5366 CenterY=14.5858 CenterZ=0 NormalX=0 NormalY=0 NormalZ=1 AngleXU=0 Radius=0.2 StartAngle=3.66519 EndAngle=5.23599
    g47: ArcOfCircle CenterX=-8.3634 CenterY=14.6858 CenterZ=0 NormalX=0 NormalY=0 NormalZ=1 AngleXU=0 Radius=0.2 StartAngle=5.23599 EndAngle=6.80678
    g48: LineSegment StartX=-18.3 StartY=-0.3 StartZ=0 EndX=-16.9 EndY=-0.3 EndZ=0
    g49: LineSegment StartX=-16.7 StartY=-0.1 StartZ=0 EndX=-16.7 EndY=0.1 EndZ=0
    g50: LineSegment StartX=-16.9 StartY=0.3 StartZ=0 EndX=-18.3 EndY=0.3 EndZ=0
    g51: LineSegment StartX=-18.5 StartY=0.1 StartZ=0 EndX=-18.5 EndY=-0.1 EndZ=0
    g52: ArcOfCircle CenterX=-16.9 CenterY=0.1 CenterZ=0 NormalX=0 NormalY=0 NormalZ=1 AngleXU=0 Radius=0.2 StartAngle=0 EndAngle=1.5708
    g53: ArcOfCircle CenterX=-16.9 CenterY=-0.1 CenterZ=0 NormalX=0 NormalY=0 NormalZ=1 AngleXU=0 Radius=0.2 StartAngle=4.71239 EndAngle=6.28319
    g54: ArcOfCircle CenterX=-18.3 CenterY=0.1 CenterZ=0 NormalX=0 NormalY=0 NormalZ=1 AngleXU=0 Radius=0.2 StartAngle=1.5708 EndAngle=3.14159
    g55: ArcOfCircle CenterX=-18.3 CenterY=-0.1 CenterZ=0 NormalX=0 NormalY=0 NormalZ=1 AngleXU=0 Radius=0.2 StartAngle=3.14159 EndAngle=4.71239
    g56: GeomPoint X=-17.6 Y=0 Z=0
    g57: LineSegment StartX=-8.89019 StartY=-15.9983 StartZ=0 EndX=-8.19019 EndY=-14.7858 EndZ=0
    g58: LineSegment StartX=-8.2634 StartY=-14.5126 StartZ=0 EndX=-8.4366 EndY=-14.4126 EndZ=0
    g59: LineSegment StartX=-8.70981 StartY=-14.4858 StartZ=0 EndX=-9.40981 EndY=-15.6983 EndZ=0
    g60: LineSegment StartX=-9.3366 StartY=-15.9715 StartZ=0 EndX=-9.1634 EndY=-16.0715 EndZ=0
    g61: ArcOfCircle CenterX=-8.5366 CenterY=-14.5858 CenterZ=0 NormalX=0 NormalY=0 NormalZ=1 AngleXU=0 Radius=0.2 StartAngle=1.0472 EndAngle=2.61799
    g62: ArcOfCircle CenterX=-8.3634 CenterY=-14.6858 CenterZ=0 NormalX=0 NormalY=0 NormalZ=1 AngleXU=0 Radius=0.2 StartAngle=5.75959 EndAngle=7.33038
    g63: ArcOfCircle CenterX=-9.2366 CenterY=-15.7983 CenterZ=0 NormalX=0 NormalY=0 NormalZ=1 AngleXU=0 Radius=0.2 StartAngle=2.61799 EndAngle=4.18879
    g64: ArcOfCircle CenterX=-9.0634 CenterY=-15.8983 CenterZ=0 NormalX=0 NormalY=0 NormalZ=1 AngleXU=0 Radius=0.2 StartAngle=4.18879 EndAngle=5.75959
    g65: LineSegment StartX=-15.5604 StartY=7.43339 StartZ=0 EndX=-15.4578 EndY=7.65172 EndZ=0
    g66: BSplineCurve PolesCount=3 KnotsCount=2 Degree=2 IsPeriodic=0
    g67: BSplineCurve PolesCount=3 KnotsCount=2 Degree=2 IsPeriodic=0
    g68: BSplineCurve PolesCount=3 KnotsCount=2 Degree=2 IsPeriodic=0
    g69: BSplineCurve PolesCount=3 KnotsCount=2 Degree=2 IsPeriodic=0
    g70: BSplineCurve PolesCount=3 KnotsCount=2 Degree=2 IsPeriodic=0
    g71: BSplineCurve PolesCount=3 KnotsCount=2 Degree=2 IsPeriodic=0
    g72: BSplineCurve PolesCount=3 KnotsCount=2 Degree=2 IsPeriodic=0
    g73: LineSegment StartX=-16.3463 StartY=8.35491 StartZ=0 EndX=-15.968 EndY=8.01983 EndZ=0
    g74: LineSegment StartX=-15.9739 StartY=8.99993 StartZ=0 EndX=-16.3463 EndY=8.35491 EndZ=0
    g75: LineSegment StartX=-16.1622 StartY=9.10863 StartZ=0 EndX=-15.9739 EndY=8.99993 EndZ=0
    g76: LineSegment StartX=-16.6263 StartY=8.30475 StartZ=0 EndX=-16.1622 EndY=9.10863 EndZ=0
    g77: LineSegment StartX=-15.8937 StartY=7.67294 StartZ=0 EndX=-16.6263 EndY=8.30475 EndZ=0
    g78: LineSegment StartX=-15.762 StartY=7.845 StartZ=0 EndX=-15.8937 EndY=7.67294 EndZ=0
    g79: BSplineCurve PolesCount=3 KnotsCount=2 Degree=2 IsPeriodic=0
    g80: BSplineCurve PolesCount=3 KnotsCount=2 Degree=2 IsPeriodic=0
    g81: BSplineCurve PolesCount=3 KnotsCount=2 Degree=2 IsPeriodic=0
    g82: BSplineCurve PolesCount=3 KnotsCount=2 Degree=2 IsPeriodic=0
    g83: BSplineCurve PolesCount=3 KnotsCount=2 Degree=2 IsPeriodic=0
    g84: BSplineCurve PolesCount=3 KnotsCount=2 Degree=2 IsPeriodic=0
    g85: BSplineCurve PolesCount=3 KnotsCount=2 Degree=2 IsPeriodic=0
    g86: BSplineCurve PolesCount=3 KnotsCount=2 Degree=2 IsPeriodic=0
    g87: BSplineCurve PolesCount=3 KnotsCount=2 Degree=2 IsPeriodic=0
    g88: BSplineCurve PolesCount=3 KnotsCount=2 Degree=2 IsPeriodic=0
    g89: BSplineCurve PolesCount=3 KnotsCount=2 Degree=2 IsPeriodic=0
    g90: BSplineCurve PolesCount=3 KnotsCount=2 Degree=2 IsPeriodic=0
    g91: BSplineCurve PolesCount=3 KnotsCount=2 Degree=2 IsPeriodic=0
    g92: BSplineCurve PolesCount=3 KnotsCount=2 Degree=2 IsPeriodic=0
    g93: BSplineCurve PolesCount=3 KnotsCount=2 Degree=2 IsPeriodic=0
    g94: BSplineCurve PolesCount=3 KnotsCount=2 Degree=2 IsPeriodic=0
    g95: BSplineCurve PolesCount=3 KnotsCount=2 Degree=2 IsPeriodic=0
    g96: BSplineCurve PolesCount=3 KnotsCount=2 Degree=2 IsPeriodic=0
    g97: BSplineCurve PolesCount=3 KnotsCount=2 Degree=2 IsPeriodic=0
    g98: BSplineCurve PolesCount=3 KnotsCount=2 Degree=2 IsPeriodic=0
    g99: BSplineCurve PolesCount=3 KnotsCount=2 Degree=2 IsPeriodic=0
    g100: BSplineCurve PolesCount=3 KnotsCount=2 Degree=2 IsPeriodic=0
    g101: BSplineCurve PolesCount=3 KnotsCount=2 Degree=2 IsPeriodic=0
    g102: BSplineCurve PolesCount=3 KnotsCount=2 Degree=2 IsPeriodic=0
    g103: BSplineCurve PolesCount=3 KnotsCount=2 Degree=2 IsPeriodic=0
    g104: BSplineCurve PolesCount=3 KnotsCount=2 Degree=2 IsPeriodic=0
    g105: BSplineCurve PolesCount=3 KnotsCount=2 Degree=2 IsPeriodic=0
    g106: BSplineCurve PolesCount=3 KnotsCount=2 Degree=2 IsPeriodic=0
    g107: LineSegment StartX=-14.1332 StartY=-8.81829 StartZ=0 EndX=-14.5097 EndY=-9.0357 EndZ=0
    g108: LineSegment StartX=-14.2478 StartY=-8.61971 StartZ=0 EndX=-14.1332 EndY=-8.81829 EndZ=0
    g109: LineSegment StartX=-14.6244 StartY=-8.83712 StartZ=0 EndX=-14.2478 EndY=-8.61971 EndZ=0
    g110: LineSegment StartX=-14.7505 StartY=-8.61868 StartZ=0 EndX=-14.6244 EndY=-8.83712 EndZ=0
    g111: LineSegment StartX=-14.9388 StartY=-8.72739 StartZ=0 EndX=-14.7505 EndY=-8.61868 EndZ=0
    g112: LineSegment StartX=-14.8127 StartY=-8.94583 StartZ=0 EndX=-14.9388 EndY=-8.72739 EndZ=0
    g113: LineSegment StartX=-15.8953 StartY=-9.57088 StartZ=0 EndX=-14.8127 EndY=-8.94583 EndZ=0
    g114: LineSegment StartX=-15.8019 StartY=-9.73268 StartZ=0 EndX=-15.8953 EndY=-9.57088 EndZ=0
    g115: LineSegment StartX=-14.2929 StartY=-9.84605 StartZ=0 EndX=-15.8019 EndY=-9.73268 EndZ=0
    g116: LineSegment StartX=-14.1046 StartY=-9.73735 StartZ=0 EndX=-14.2929 EndY=-9.84605 EndZ=0
    g117: LineSegment StartX=-14.5097 StartY=-9.0357 StartZ=0 EndX=-14.1046 EndY=-9.73735 EndZ=0
    g118: LineSegment StartX=-14.698 StartY=-9.1444 StartZ=0 EndX=-15.4512 EndY=-9.57922 EndZ=0
    g119: LineSegment StartX=-14.4059 StartY=-9.65041 StartZ=0 EndX=-14.698 EndY=-9.1444 EndZ=0
    g120: LineSegment StartX=-15.4512 StartY=-9.57922 StartZ=0 EndX=-14.4059 EndY=-9.65041 EndZ=0
    g121: BSplineCurve PolesCount=3 KnotsCount=2 Degree=2 IsPeriodic=0
    g122: BSplineCurve PolesCount=3 KnotsCount=2 Degree=2 IsPeriodic=0
    g123: BSplineCurve PolesCount=3 KnotsCount=2 Degree=2 IsPeriodic=0
    g124: BSplineCurve PolesCount=3 KnotsCount=2 Degree=2 IsPeriodic=0
    g125: BSplineCurve PolesCount=3 KnotsCount=2 Degree=2 IsPeriodic=0
    g126: BSplineCurve PolesCount=3 KnotsCount=2 Degree=2 IsPeriodic=0
    g127: BSplineCurve PolesCount=3 KnotsCount=2 Degree=2 IsPeriodic=0
    g128: BSplineCurve PolesCount=3 KnotsCount=2 Degree=2 IsPeriodic=0
    g129: BSplineCurve PolesCount=3 KnotsCount=2 Degree=2 IsPeriodic=0
    g130: BSplineCurve PolesCount=3 KnotsCount=2 Degree=2 IsPeriodic=0
    g131: BSplineCurve PolesCount=3 KnotsCount=2 Degree=2 IsPeriodic=0
    g132: BSplineCurve PolesCount=3 KnotsCount=2 Degree=2 IsPeriodic=0
    g133: BSplineCurve PolesCount=3 KnotsCount=2 Degree=2 IsPeriodic=0
    g134: BSplineCurve PolesCount=3 KnotsCount=2 Degree=2 IsPeriodic=0
    g135: BSplineCurve PolesCount=3 KnotsCount=2 Degree=2 IsPeriodic=0
    g136: BSplineCurve PolesCount=3 KnotsCount=2 Degree=2 IsPeriodic=0
    g137: BSplineCurve PolesCount=3 KnotsCount=2 Degree=2 IsPeriodic=0
    g138: BSplineCurve PolesCount=3 KnotsCount=2 Degree=2 IsPeriodic=0
    g139: BSplineCurve PolesCount=3 KnotsCount=2 Degree=2 IsPeriodic=0
    g140: BSplineCurve PolesCount=3 KnotsCount=2 Degree=2 IsPeriodic=0
    g141: LineSegment StartX=1.34225 StartY=-17.1618 StartZ=0 EndX=1.11295 EndY=-17.1924 EndZ=0
    g142: BSplineCurve PolesCount=3 KnotsCount=2 Degree=2 IsPeriodic=0
    g143: BSplineCurve PolesCount=3 KnotsCount=2 Degree=2 IsPeriodic=0
    g144: BSplineCurve PolesCount=3 KnotsCount=2 Degree=2 IsPeriodic=0
    g145: BSplineCurve PolesCount=3 KnotsCount=2 Degree=2 IsPeriodic=0
    g146: BSplineCurve PolesCount=3 KnotsCount=2 Degree=2 IsPeriodic=0
    g147: BSplineCurve PolesCount=3 KnotsCount=2 Degree=2 IsPeriodic=0
    g148: BSplineCurve PolesCount=3 KnotsCount=2 Degree=2 IsPeriodic=0
    g149: BSplineCurve PolesCount=3 KnotsCount=2 Degree=2 IsPeriodic=0
    g150: BSplineCurve PolesCount=3 KnotsCount=2 Degree=2 IsPeriodic=0
    g151: BSplineCurve PolesCount=3 KnotsCount=2 Degree=2 IsPeriodic=0
    g152: BSplineCurve PolesCount=3 KnotsCount=2 Degree=2 IsPeriodic=0
    g153: BSplineCurve PolesCount=3 KnotsCount=2 Degree=2 IsPeriodic=0
    g154: BSplineCurve PolesCount=3 KnotsCount=2 Degree=2 IsPeriodic=0
    g155: LineSegment StartX=1.09002 StartY=-18.0076 StartZ=0 EndX=1.31932 EndY=-18.0484 EndZ=0
    g156: BSplineCurve PolesCount=3 KnotsCount=2 Degree=2 IsPeriodic=0
    g157: BSplineCurve PolesCount=3 KnotsCount=2 Degree=2 IsPeriodic=0
    g158: BSplineCurve PolesCount=3 KnotsCount=2 Degree=2 IsPeriodic=0
    g159: BSplineCurve PolesCount=3 KnotsCount=2 Degree=2 IsPeriodic=0
    g160: BSplineCurve PolesCount=3 KnotsCount=2 Degree=2 IsPeriodic=0
    g161: BSplineCurve PolesCount=3 KnotsCount=2 Degree=2 IsPeriodic=0
    g162: BSplineCurve PolesCount=3 KnotsCount=2 Degree=2 IsPeriodic=0
    g163: LineSegment StartX=0.889597 StartY=-17.5202 StartZ=0 EndX=0.864119 EndY=-17.7384 EndZ=0
    g164: BSplineCurve PolesCount=3 KnotsCount=2 Degree=2 IsPeriodic=0
    g165: BSplineCurve PolesCount=3 KnotsCount=2 Degree=2 IsPeriodic=0
    g166: BSplineCurve PolesCount=3 KnotsCount=2 Degree=2 IsPeriodic=0
    g167: BSplineCurve PolesCount=3 KnotsCount=2 Degree=2 IsPeriodic=0
    g168: BSplineCurve PolesCount=3 KnotsCount=2 Degree=2 IsPeriodic=0
    g169: BSplineCurve PolesCount=3 KnotsCount=2 Degree=2 IsPeriodic=0
    g170: BSplineCurve PolesCount=3 KnotsCount=2 Degree=2 IsPeriodic=0
    g171: BSplineCurve PolesCount=3 KnotsCount=2 Degree=2 IsPeriodic=0
    g172: BSplineCurve PolesCount=3 KnotsCount=2 Degree=2 IsPeriodic=0
    g173: BSplineCurve PolesCount=3 KnotsCount=2 Degree=2 IsPeriodic=0
    g174: BSplineCurve PolesCount=3 KnotsCount=2 Degree=2 IsPeriodic=0
    g175: BSplineCurve PolesCount=3 KnotsCount=2 Degree=2 IsPeriodic=0
    g176: BSplineCurve PolesCount=3 KnotsCount=2 Degree=2 IsPeriodic=0
    g177: BSplineCurve PolesCount=3 KnotsCount=2 Degree=2 IsPeriodic=0
    g178: BSplineCurve PolesCount=3 KnotsCount=2 Degree=2 IsPeriodic=0
    g179: BSplineCurve PolesCount=3 KnotsCount=2 Degree=2 IsPeriodic=0
    g180: BSplineCurve PolesCount=3 KnotsCount=2 Degree=2 IsPeriodic=0
    g181: BSplineCurve PolesCount=3 KnotsCount=2 Degree=2 IsPeriodic=0
    g182: BSplineCurve PolesCount=3 KnotsCount=2 Degree=2 IsPeriodic=0
    g183: BSplineCurve PolesCount=3 KnotsCount=2 Degree=2 IsPeriodic=0
    g184: BSplineCurve PolesCount=3 KnotsCount=2 Degree=2 IsPeriodic=0
    g185: BSplineCurve PolesCount=3 KnotsCount=2 Degree=2 IsPeriodic=0
    g186: BSplineCurve PolesCount=3 KnotsCount=2 Degree=2 IsPeriodic=0
    g187: BSplineCurve PolesCount=3 KnotsCount=2 Degree=2 IsPeriodic=0
    g188: BSplineCurve PolesCount=3 KnotsCount=2 Degree=2 IsPeriodic=0
    g189: BSplineCurve PolesCount=3 KnotsCount=2 Degree=2 IsPeriodic=0
    g190: BSplineCurve PolesCount=3 KnotsCount=2 Degree=2 IsPeriodic=0
    g191: LineSegment StartX=14.6679 StartY=-8.32693 StartZ=0 EndX=14.4796 EndY=-8.21823 EndZ=0
    g192: LineSegment StartX=15.1261 StartY=-7.53335 StartZ=0 EndX=14.6679 EndY=-8.32693 EndZ=0
    g193: BSplineCurve PolesCount=3 KnotsCount=2 Degree=2 IsPeriodic=0
    g194: BSplineCurve PolesCount=3 KnotsCount=2 Degree=2 IsPeriodic=0
    g195: BSplineCurve PolesCount=3 KnotsCount=2 Degree=2 IsPeriodic=0
    g196: BSplineCurve PolesCount=3 KnotsCount=2 Degree=2 IsPeriodic=0
    g197: BSplineCurve PolesCount=3 KnotsCount=2 Degree=2 IsPeriodic=0
    g198: BSplineCurve PolesCount=3 KnotsCount=2 Degree=2 IsPeriodic=0
    g199: BSplineCurve PolesCount=3 KnotsCount=2 Degree=2 IsPeriodic=0
    g200: BSplineCurve PolesCount=3 KnotsCount=2 Degree=2 IsPeriodic=0
    g201: BSplineCurve PolesCount=3 KnotsCount=2 Degree=2 IsPeriodic=0
    g202: LineSegment StartX=16.087 StartY=-8.04304 StartZ=0 EndX=16.2271 EndY=-7.85132 EndZ=0
    g203: BSplineCurve PolesCount=3 KnotsCount=2 Degree=2 IsPeriodic=0
    g204: BSplineCurve PolesCount=3 KnotsCount=2 Degree=2 IsPeriodic=0
    g205: BSplineCurve PolesCount=3 KnotsCount=2 Degree=2 IsPeriodic=0
    g206: BSplineCurve PolesCount=3 KnotsCount=2 Degree=2 IsPeriodic=0
    g207: BSplineCurve PolesCount=3 KnotsCount=2 Degree=2 IsPeriodic=0
    g208: BSplineCurve PolesCount=3 KnotsCount=2 Degree=2 IsPeriodic=0
    g209: BSplineCurve PolesCount=3 KnotsCount=2 Degree=2 IsPeriodic=0
    g210: BSplineCurve PolesCount=3 KnotsCount=2 Degree=2 IsPeriodic=0
    g211: BSplineCurve PolesCount=3 KnotsCount=2 Degree=2 IsPeriodic=0
    g212: LineSegment StartX=14.4796 StartY=-8.21823 StartZ=0 EndX=15.097 EndY=-7.14884 EndZ=0
    g213: BSplineCurve PolesCount=3 KnotsCount=2 Degree=2 IsPeriodic=0
    g214: BSplineCurve PolesCount=3 KnotsCount=2 Degree=2 IsPeriodic=0
    g215: BSplineCurve PolesCount=3 KnotsCount=2 Degree=2 IsPeriodic=0
    g216: BSplineCurve PolesCount=3 KnotsCount=2 Degree=2 IsPeriodic=0
    g217: BSplineCurve PolesCount=3 KnotsCount=2 Degree=2 IsPeriodic=0
    g218: BSplineCurve PolesCount=3 KnotsCount=2 Degree=2 IsPeriodic=0
    g219: BSplineCurve PolesCount=3 KnotsCount=2 Degree=2 IsPeriodic=0
    g220: BSplineCurve PolesCount=3 KnotsCount=2 Degree=2 IsPeriodic=0
    g221: BSplineCurve PolesCount=3 KnotsCount=2 Degree=2 IsPeriodic=0
    g222: BSplineCurve PolesCount=3 KnotsCount=2 Degree=2 IsPeriodic=0
    g223: BSplineCurve PolesCount=3 KnotsCount=2 Degree=2 IsPeriodic=0
    g224: BSplineCurve PolesCount=3 KnotsCount=2 Degree=2 IsPeriodic=0
    g225: BSplineCurve PolesCount=3 KnotsCount=2 Degree=2 IsPeriodic=0
    g226: BSplineCurve PolesCount=3 KnotsCount=2 Degree=2 IsPeriodic=0
    g227: BSplineCurve PolesCount=3 KnotsCount=2 Degree=2 IsPeriodic=0
    g228: BSplineCurve PolesCount=3 KnotsCount=2 Degree=2 IsPeriodic=0
    g229: BSplineCurve PolesCount=3 KnotsCount=2 Degree=2 IsPeriodic=0
    g230: BSplineCurve PolesCount=3 KnotsCount=2 Degree=2 IsPeriodic=0
    g231: BSplineCurve PolesCount=3 KnotsCount=2 Degree=2 IsPeriodic=0
    g232: BSplineCurve PolesCount=3 KnotsCount=2 Degree=2 IsPeriodic=0
    g233: LineSegment [constr] StartX=0 StartY=0 StartZ=0 EndX=3.32659 EndY=15.6504 EndZ=0
    g234: LineSegment [constr] StartX=0 StartY=0 StartZ=0 EndX=4.94427 EndY=15.2169 EndZ=0
    g235: LineSegment [constr] StartX=0 StartY=0 StartZ=0 EndX=6.50779 EndY=14.6167 EndZ=0
    g236: LineSegment [constr] StartX=0 StartY=0 StartZ=0 EndX=9.40456 EndY=12.9443 EndZ=0
    g237: LineSegment [constr] StartX=0 StartY=0 StartZ=0 EndX=10.7061 EndY=11.8903 EndZ=0
    g238: LineSegment [constr] StartX=0 StartY=0 StartZ=0 EndX=11.8903 EndY=10.7061 EndZ=0
    g239: LineSegment [constr] StartX=0 StartY=0 StartZ=0 EndX=12.9443 EndY=9.40456 EndZ=0
    g240: LineSegment [constr] StartX=0 StartY=0 StartZ=0 EndX=14.6167 EndY=6.50779 EndZ=0
    g241: LineSegment [constr] StartX=0 StartY=0 StartZ=0 EndX=15.2169 EndY=4.94427 EndZ=0
    g242: LineSegment [constr] StartX=0 StartY=0 StartZ=0 EndX=15.6504 EndY=3.32659 EndZ=0
    g243: LineSegment [constr] StartX=0 StartY=0 StartZ=0 EndX=15.9124 EndY=1.67246 EndZ=0
    g244: ArcOfCircle CenterX=-1.2e-14 CenterY=0 CenterZ=0 NormalX=0 NormalY=0 NormalZ=1 AngleXU=0 Radius=16 StartAngle=1.37073 EndAngle=1.51844
    g245: ArcOfCircle CenterX=-1.2e-14 CenterY=0 CenterZ=0 NormalX=0 NormalY=0 NormalZ=1 AngleXU=0 Radius=16 StartAngle=1.26601 EndAngle=1.35198
    g246: ArcOfCircle CenterX=-1.2e-14 CenterY=0 CenterZ=0 NormalX=0 NormalY=0 NormalZ=1 AngleXU=0 Radius=16 StartAngle=1.16129 EndAngle=1.24726
    g247: ArcOfCircle CenterX=-1.2e-14 CenterY=0 CenterZ=0 NormalX=0 NormalY=0 NormalZ=1 AngleXU=0 Radius=16 StartAngle=0.951853 EndAngle=1.14254
    g248: ArcOfCircle CenterX=-1.2e-14 CenterY=0 CenterZ=0 NormalX=0 NormalY=0 NormalZ=1 AngleXU=0 Radius=16 StartAngle=0.847133 EndAngle=0.933103
    g249: ArcOfCircle CenterX=-1.2e-14 CenterY=0 CenterZ=0 NormalX=0 NormalY=0 NormalZ=1 AngleXU=0 Radius=16 StartAngle=0.742413 EndAngle=0.828383
    g250: ArcOfCircle CenterX=-1.2e-14 CenterY=0 CenterZ=0 NormalX=0 NormalY=0 NormalZ=1 AngleXU=0 Radius=16 StartAngle=0.637694 EndAngle=0.723663
    g251: ArcOfCircle CenterX=-1.2e-14 CenterY=0 CenterZ=0 NormalX=0 NormalY=0 NormalZ=1 AngleXU=0 Radius=16 StartAngle=0.428254 EndAngle=0.618943
    g252: ArcOfCircle CenterX=-1.2e-14 CenterY=0 CenterZ=0 NormalX=0 NormalY=0 NormalZ=1 AngleXU=0 Radius=16 StartAngle=0.323534 EndAngle=0.409504
    g253: ArcOfCircle CenterX=-1.2e-14 CenterY=0 CenterZ=0 NormalX=0 NormalY=0 NormalZ=1 AngleXU=0 Radius=16 StartAngle=0.218815 EndAngle=0.304784
    g254: ArcOfCircle CenterX=-1.2e-14 CenterY=0 CenterZ=0 NormalX=0 NormalY=0 NormalZ=1 AngleXU=0 Radius=16 StartAngle=0.114095 EndAngle=0.200064
    g255: LineSegment [constr] StartX=15.9273 StartY=1.5232 StartZ=0 EndX=15.896 EndY=1.82156 EndZ=0
    g256: LineSegment [constr] StartX=15.6185 StartY=3.47316 StartZ=0 EndX=15.6809 EndY=3.17972 EndZ=0
    g257: LineSegment [constr] StartX=15.1699 StartY=5.08671 StartZ=0 EndX=15.2626 EndY=4.8014 EndZ=0
    g258: LineSegment [constr] StartX=14.6771 StartY=6.37047 StartZ=0 EndX=14.5551 EndY=6.64453 EndZ=0
    g259: LineSegment [constr] StartX=12.8555 StartY=9.5255 StartZ=0 EndX=13.0319 EndY=9.2828 EndZ=0
    g260: LineSegment [constr] StartX=11.9902 StartY=10.5941 StartZ=0 EndX=11.7894 EndY=10.8171 EndZ=0
    g261: LineSegment [constr] StartX=10.5941 StartY=11.9902 StartZ=0 EndX=10.8171 EndY=11.7894 EndZ=0
    g262: LineSegment [constr] StartX=9.2828 StartY=13.0319 StartZ=0 EndX=9.5255 EndY=12.8555 EndZ=0
    g263: LineSegment [constr] StartX=6.37047 StartY=14.6771 StartZ=0 EndX=6.64453 EndY=14.5551 EndZ=0
    g264: LineSegment [constr] StartX=4.8014 StartY=15.2626 StartZ=0 EndX=5.08671 EndY=15.1699 EndZ=0
    g265: LineSegment [constr] StartX=3.17972 StartY=15.6809 StartZ=0 EndX=3.47316 EndY=15.6185 EndZ=0
    g266: LineSegment StartX=3.17972 StartY=15.6809 StartZ=0 EndX=3.41896 EndY=16.8064 EndZ=0
    g267: ArcOfCircle CenterX=3.46787 CenterY=16.796 CenterZ=0 NormalX=0 NormalY=0 NormalZ=1 AngleXU=0 Radius=0.05 StartAngle=1.36136 EndAngle=2.93215
    g268: LineSegment StartX=3.47827 StartY=16.8449 StartZ=0 EndX=3.6739 EndY=16.8033 EndZ=0
    g269: ArcOfCircle CenterX=3.6635 CenterY=16.7544 CenterZ=0 NormalX=0 NormalY=0 NormalZ=1 AngleXU=0 Radius=0.05 StartAngle=6.07375 EndAngle=7.64454
    g270: LineSegment StartX=3.71241 StartY=16.744 StartZ=0 EndX=3.47316 EndY=15.6185 EndZ=0
    g271: GeomPoint X=3.57608 Y=16.8241 Z=0
    g272: Circle [constr] CenterX=-1.2e-14 CenterY=0 CenterZ=0 NormalX=0 NormalY=0 NormalZ=1 AngleXU=0 Radius=17.2
    g273: LineSegment StartX=4.8014 StartY=15.2626 StartZ=0 EndX=5.15698 EndY=16.357 EndZ=0
    g274: ArcOfCircle CenterX=5.20454 CenterY=16.3415 CenterZ=0 NormalX=0 NormalY=0 NormalZ=1 AngleXU=0 Radius=0.05 StartAngle=1.25664 EndAngle=2.82743
    g275: LineSegment StartX=5.21999 StartY=16.3891 StartZ=0 EndX=5.4102 EndY=16.3273 EndZ=0
    g276: ArcOfCircle CenterX=5.39475 CenterY=16.2797 CenterZ=0 NormalX=0 NormalY=0 NormalZ=1 AngleXU=0 Radius=0.05 StartAngle=5.96903 EndAngle=7.53982
    g277: LineSegment StartX=5.4423 StartY=16.2643 StartZ=0 EndX=5.08671 EndY=15.1699 EndZ=0
    g278: GeomPoint X=5.31509 Y=16.3582 Z=0
    g279: LineSegment StartX=6.37047 StartY=14.6771 StartZ=0 EndX=6.8385 EndY=15.7283 EndZ=0
    g280: ArcOfCircle CenterX=6.88418 CenterY=15.708 CenterZ=0 NormalX=0 NormalY=0 NormalZ=1 AngleXU=0 Radius=0.05 StartAngle=1.15192 EndAngle=2.72271
    g281: LineSegment StartX=6.90452 StartY=15.7537 StartZ=0 EndX=7.08722 EndY=15.6723 EndZ=0
    g282: GeomPoint X=6.99587 Y=15.713 Z=0
    g283: ArcOfCircle CenterX=7.06689 CenterY=15.6266 CenterZ=0 NormalX=0 NormalY=0 NormalZ=1 AngleXU=0 Radius=0.05 StartAngle=5.86431 EndAngle=7.4351
    g284: LineSegment StartX=7.11257 StartY=15.6063 StartZ=0 EndX=6.64453 EndY=14.5551 EndZ=0
    g285: LineSegment StartX=9.2828 StartY=13.0319 StartZ=0 EndX=9.95916 EndY=13.9628 EndZ=0
    g286: ArcOfCircle CenterX=9.99962 CenterY=13.9334 CenterZ=0 NormalX=0 NormalY=0 NormalZ=1 AngleXU=0 Radius=0.05 StartAngle=0.942478 EndAngle=2.51327
    g287: LineSegment StartX=10.029 StartY=13.9739 StartZ=0 EndX=10.1908 EndY=13.8563 EndZ=0
    g288: GeomPoint X=10.1099 Y=13.9151 Z=0
    g289: ArcOfCircle CenterX=10.1614 CenterY=13.8159 CenterZ=0 NormalX=0 NormalY=0 NormalZ=1 AngleXU=0 Radius=0.05 StartAngle=5.65487 EndAngle=7.22566
    g290: LineSegment StartX=10.2019 StartY=13.7865 StartZ=0 EndX=9.5255 EndY=12.8555 EndZ=0
    g291: LineSegment StartX=10.5941 StartY=11.9902 StartZ=0 EndX=11.3641 EndY=12.8453 EndZ=0
    g292: ArcOfCircle CenterX=11.4013 CenterY=12.8118 CenterZ=0 NormalX=0 NormalY=0 NormalZ=1 AngleXU=0 Radius=0.05 StartAngle=0.837758 EndAngle=2.40855
    g293: LineSegment StartX=11.4347 StartY=12.849 StartZ=0 EndX=11.5834 EndY=12.7152 EndZ=0
    g294: GeomPoint X=11.509 Y=12.7821 Z=0
    g295: ArcOfCircle CenterX=11.5499 CenterY=12.678 CenterZ=0 NormalX=0 NormalY=0 NormalZ=1 AngleXU=0 Radius=0.05 StartAngle=5.55015 EndAngle=7.12094
    g296: LineSegment StartX=11.5871 StartY=12.6446 StartZ=0 EndX=10.8171 EndY=11.7894 EndZ=0
    g297: LineSegment StartX=11.7894 StartY=10.8171 StartZ=0 EndX=12.6446 EndY=11.5871 EndZ=0
    g298: ArcOfCircle CenterX=12.678 CenterY=11.5499 CenterZ=0 NormalX=0 NormalY=0 NormalZ=1 AngleXU=0 Radius=0.05 StartAngle=0.733038 EndAngle=2.30383
    g299: LineSegment StartX=12.7152 StartY=11.5834 StartZ=0 EndX=12.849 EndY=11.4347 EndZ=0
    g300: GeomPoint X=12.7821 Y=11.509 Z=0
    g301: ArcOfCircle CenterX=12.8118 CenterY=11.4013 CenterZ=0 NormalX=0 NormalY=0 NormalZ=1 AngleXU=0 Radius=0.05 StartAngle=5.44543 EndAngle=7.01622
    g302: LineSegment StartX=12.8453 StartY=11.3641 StartZ=0 EndX=11.9902 EndY=10.5941 EndZ=0
    g303: LineSegment StartX=12.8555 StartY=9.5255 StartZ=0 EndX=13.7865 EndY=10.2019 EndZ=0
    g304: ArcOfCircle CenterX=13.8159 CenterY=10.1614 CenterZ=0 NormalX=0 NormalY=0 NormalZ=1 AngleXU=0 Radius=0.05 StartAngle=0.628319 EndAngle=2.19911
    g305: LineSegment StartX=13.8563 StartY=10.1908 StartZ=0 EndX=13.9739 EndY=10.029 EndZ=0
    g306: GeomPoint X=13.9151 Y=10.1099 Z=0
    g307: ArcOfCircle CenterX=13.9334 CenterY=9.99962 CenterZ=0 NormalX=0 NormalY=0 NormalZ=1 AngleXU=0 Radius=0.05 StartAngle=5.34071 EndAngle=6.9115
    g308: LineSegment StartX=13.9628 StartY=9.95916 StartZ=0 EndX=13.0319 EndY=9.2828 EndZ=0
    g309: LineSegment StartX=14.5551 StartY=6.64453 StartZ=0 EndX=15.6063 EndY=7.11257 EndZ=0
    g310: ArcOfCircle CenterX=15.6266 CenterY=7.06689 CenterZ=0 NormalX=0 NormalY=0 NormalZ=1 AngleXU=0 Radius=0.05 StartAngle=0.418879 EndAngle=1.98968
    g311: LineSegment StartX=15.6723 StartY=7.08722 StartZ=0 EndX=15.7537 EndY=6.90452 EndZ=0
    g312: GeomPoint X=15.713 Y=6.99587 Z=0
    g313: ArcOfCircle CenterX=15.708 CenterY=6.88418 CenterZ=0 NormalX=0 NormalY=0 NormalZ=1 AngleXU=0 Radius=0.05 StartAngle=5.13127 EndAngle=6.70206
    g314: LineSegment StartX=15.7283 StartY=6.8385 StartZ=0 EndX=14.6771 EndY=6.37047 EndZ=0
    g315: LineSegment StartX=15.1699 StartY=5.08671 StartZ=0 EndX=16.2643 EndY=5.4423 EndZ=0
    g316: ArcOfCircle CenterX=16.2797 CenterY=5.39475 CenterZ=0 NormalX=0 NormalY=0 NormalZ=1 AngleXU=0 Radius=0.05 StartAngle=0.314159 EndAngle=1.88496
    g317: LineSegment StartX=16.3273 StartY=5.4102 StartZ=0 EndX=16.3891 EndY=5.21999 EndZ=0
    g318: GeomPoint X=16.3582 Y=5.31509 Z=0
    g319: ArcOfCircle CenterX=16.3415 CenterY=5.20454 CenterZ=0 NormalX=0 NormalY=0 NormalZ=1 AngleXU=0 Radius=0.05 StartAngle=5.02655 EndAngle=6.59734
    g320: LineSegment StartX=16.357 StartY=5.15698 StartZ=0 EndX=15.2626 EndY=4.8014 EndZ=0
    g321: LineSegment StartX=15.6185 StartY=3.47316 StartZ=0 EndX=16.744 EndY=3.71241 EndZ=0
    g322: ArcOfCircle CenterX=16.7544 CenterY=3.6635 CenterZ=0 NormalX=0 NormalY=0 NormalZ=1 AngleXU=0 Radius=0.05 StartAngle=0.20944 EndAngle=1.78024
    g323: LineSegment StartX=16.8033 StartY=3.6739 StartZ=0 EndX=16.8449 EndY=3.47827 EndZ=0
    g324: GeomPoint X=16.8241 Y=3.57608 Z=0
    g325: ArcOfCircle CenterX=16.796 CenterY=3.46787 CenterZ=0 NormalX=0 NormalY=0 NormalZ=1 AngleXU=0 Radius=0.05 StartAngle=4.92183 EndAngle=6.49262
    g326: LineSegment StartX=16.8064 StartY=3.41896 StartZ=0 EndX=15.6809 EndY=3.17972 EndZ=0
    g327: LineSegment StartX=15.896 StartY=1.82156 StartZ=0 EndX=17.0404 EndY=1.94184 EndZ=0
    g328: ArcOfCircle CenterX=17.0456 CenterY=1.89212 CenterZ=0 NormalX=0 NormalY=0 NormalZ=1 AngleXU=0 Radius=0.05 StartAngle=0.10472 EndAngle=1.67552
    g329: LineSegment StartX=17.0953 StartY=1.89734 StartZ=0 EndX=17.1162 EndY=1.69844 EndZ=0
    g330: GeomPoint X=17.1058 Y=1.79789 Z=0
    g331: ArcOfCircle CenterX=17.0665 CenterY=1.69321 CenterZ=0 NormalX=0 NormalY=0 NormalZ=1 AngleXU=0 Radius=0.05 StartAngle=4.81711 EndAngle=6.38791
    g332: LineSegment StartX=17.0717 StartY=1.64348 StartZ=0 EndX=15.9273 EndY=1.5232 EndZ=0
    g333: Circle CenterX=0 CenterY=17.6 CenterZ=0 NormalX=0 NormalY=0 NormalZ=1 AngleXU=0 Radius=0.9
    g334: LineSegment StartX=0.837375 StartY=15.9781 StartZ=0 EndX=3.9919 EndY=18.7804 EndZ=0
    g335: LineSegment StartX=-0.837375 StartY=15.9781 StartZ=0 EndX=-3.9919 EndY=18.7804 EndZ=0
    g336: ArcOfCircle CenterX=-1.2e-14 CenterY=0 CenterZ=0 NormalX=0 NormalY=0 NormalZ=1 AngleXU=0 Radius=16 StartAngle=1.62316 EndAngle=6.37853
    g337: ArcOfCircle CenterX=-1.2e-14 CenterY=0 CenterZ=0 NormalX=0 NormalY=0 NormalZ=1 AngleXU=0 Radius=19.2 StartAngle=1.78024 EndAngle=7.64454
    g338: LineSegment [constr] StartX=3.57608 StartY=16.8241 StartZ=0 EndX=3.9919 EndY=18.7804 EndZ=0
    g339: LineSegment [constr] StartX=0.837375 StartY=15.9781 StartZ=0 EndX=-1.2e-14 EndY=0 EndZ=0
  constraints (552):
    c: Coincident(g0,g-1)
    c: Coincident(g1,g-1)
    c: Coincident(g2,g-1)
    c: Coincident(g3,g-1)
    c: Coincident(g4,g-1)
    c: Angle(g0,g-2) = 0.523599
    c: Angle(g1,g0) = 0.523599
    c: Angle(g-2,g3) = 2.61799
    c: Coincident(g9,g-1)
    c: Radius(g9) = 19.2
    c: Coincident(g10,g9)
    c: Radius(g10) = 17.6
    c: PointOnObject(g0,g10)
    c: Tangent(g7,g11) = -1.5708
    c: Tangent(g6,g11) = -1.5708
    c: Tangent(g6,g12) = -1.5708
    c: Tangent(g5,g12) = -1.5708
    c: Tangent(g7,g13) = -1.5708
    c: Tangent(g8,g13) = -1.5708
    c: Tangent(g8,g14) = -1.5708
    c: Tangent(g5,g14) = -1.5708
    c: Equal(g13,g14)
    c: Equal(g14,g12)
    c: Equal(g12,g11)
    c: Symmetric(g13,g12,g0)
    c: Symmetric(g6,g6,g0)
    c: Distance(g7,g5) = 0.6
    c: Distance(g6,g8) = 1.8
    c: Radius(g11) = 0.2
    c: Symmetric(g8,g8,g0)
    c: PointOnObject(g1,g10)
    c: PointOnObject(g2,g10)
    c: PointOnObject(g3,g10)
    c: PointOnObject(g4,g10)
    c: Angle(g2,g-2) = 2.61799
    c: Angle(g-2,g4) = 0.523599
    c: Tangent(g17,g19) = -1.5708
    c: Tangent(g16,g19) = -1.5708
    c: Tangent(g16,g20) = -1.5708
    c: Tangent(g15,g20) = -1.5708
    c: Tangent(g17,g21) = -1.5708
    c: Tangent(g18,g21) = -1.5708
    c: Tangent(g18,g22) = -1.5708
    c: Tangent(g15,g22) = -1.5708
    c: Equal(g21,g22)
    c: Equal(g22,g20)
    c: Equal(g20,g19)
    c: Distance(g17,g15) = 0.75
    c: Distance(g16,g18) = 1.8
    c: Equal(g11,g19) = 0.2
    c: Symmetric(g21,g20,g1)
    c: Symmetric(g18,g18,g1)
    c: Symmetric(g16,g16,g1)
    c: Tangent(g25,g27) = -1.5708
    c: Tangent(g24,g27) = -1.5708
    c: Tangent(g24,g28) = -1.5708
    c: Tangent(g23,g28) = -1.5708
    c: Tangent(g25,g29) = -1.5708
    c: Tangent(g26,g29) = -1.5708
    c: Tangent(g26,g30) = -1.5708
    c: Tangent(g23,g30) = -1.5708
    c: Equal(g29,g30)
    c: Equal(g30,g28)
    c: Equal(g28,g27)
    c: Distance(g25,g23) = 0.6
    c: Distance(g24,g26) = 1.8
    c: Equal(g11,g27) = 0.2
    c: PointOnObject(g31,g10)
    c: PointOnObject(g31,g-1)
    c: Symmetric(g29,g28,g31)
    c: Symmetric(g24,g24,g-1)
    c: Symmetric(g26,g26,g-1)
    c: Tangent(g34,g36) = -1.5708
    c: Tangent(g33,g36) = -1.5708
    c: Tangent(g33,g37) = -1.5708
    c: Tangent(g32,g37) = -1.5708
    c: Tangent(g34,g38) = -1.5708
    c: Tangent(g35,g38) = -1.5708
    c: Tangent(g35,g39) = -1.5708
    c: Tangent(g32,g39) = -1.5708
    c: Equal(g38,g39)
    c: Equal(g39,g37)
    c: Equal(g37,g36)
    c: Distance(g34,g32) = 0.6
    c: Distance(g33,g35) = 1.8
    c: Equal(g11,g36) = 0.2
    c: Symmetric(g36,g39,g2)
    c: Symmetric(g33,g33,g2)
    c: Symmetric(g35,g35,g2)
    c: Tangent(g42,g44) = -1.5708
    c: Tangent(g41,g44) = -1.5708
    c: Tangent(g41,g45) = -1.5708
    c: Tangent(g40,g45) = -1.5708
    c: Tangent(g42,g46) = -1.5708
    c: Tangent(g43,g46) = -1.5708
    c: Tangent(g43,g47) = -1.5708
    c: Tangent(g40,g47) = -1.5708
    c: Equal(g46,g47)
    c: Equal(g47,g45)
    c: Equal(g45,g44)
    c: Distance(g42,g40) = 0.6
    c: Distance(g41,g43) = 1.8
    c: Equal(g11,g44) = 0.2
    c: Symmetric(g46,g45,g4)
    c: Symmetric(g43,g43,g4)
    c: Symmetric(g41,g41,g4)
    c: Tangent(g50,g52) = -1.5708
    c: Tangent(g49,g52) = -1.5708
    c: Tangent(g49,g53) = -1.5708
    c: Tangent(g48,g53) = -1.5708
    c: Tangent(g50,g54) = -1.5708
    c: Tangent(g51,g54) = -1.5708
    c: Tangent(g51,g55) = -1.5708
    c: Tangent(g48,g55) = -1.5708
    c: Equal(g54,g55)
    c: Equal(g55,g53)
    c: Equal(g53,g52)
    c: Distance(g50,g48) = 0.6
    c: Distance(g49,g51) = 1.8
    c: Equal(g11,g52) = 0.2
    c: PointOnObject(g56,g-1)
    c: PointOnObject(g56,g10)
    c: Symmetric(g53,g54,g56)
    c: Symmetric(g51,g51,g-1)
    c: Symmetric(g49,g49,g-1)
    c: Tangent(g59,g61) = -1.5708
    c: Tangent(g58,g61) = -1.5708
    c: Tangent(g58,g62) = -1.5708
    c: Tangent(g57,g62) = -1.5708
    c: Tangent(g59,g63) = -1.5708
    c: Tangent(g60,g63) = -1.5708
    c: Tangent(g60,g64) = -1.5708
    c: Tangent(g57,g64) = -1.5708
    c: Equal(g63,g64)
    c: Equal(g64,g62)
    c: Equal(g62,g61)
    c: Distance(g59,g57) = 0.6
    c: Distance(g58,g60) = 1.8
    c: Equal(g11,g61) = 0.2
    c: Symmetric(g61,g64,g3)
    c: Symmetric(g63,g64,g3)
    c: Symmetric(g61,g62,g3)
    c: Distance(g0) = 17.6
    c: Coincident(g65,g66)
    c: Coincident(g66,g67)
    c: Coincident(g67,g68)
    c: Coincident(g68,g69)
    c: Coincident(g69,g70)
    c: Coincident(g70,g71)
    c: Coincident(g71,g72)
    c: Coincident(g72,g73)
    c: Coincident(g73,g74)
    c: Coincident(g74,g75)
    c: Coincident(g75,g76)
    c: Coincident(g76,g77)
    c: Coincident(g77,g78)
    c: Coincident(g78,g79)
    c: Coincident(g79,g80)
    c: Coincident(g80,g81)
    c: Coincident(g81,g82)
    c: Coincident(g82,g83)
    c: Coincident(g83,g84)
    c: Coincident(g84,g85)
    c: Coincident(g85,g86)
    c: Coincident(g86,g65)
    c: Coincident(g87,g88)
    c: Coincident(g88,g89)
    c: Coincident(g89,g90)
    c: Coincident(g90,g91)
    c: Coincident(g91,g92)
    c: Coincident(g92,g93)
    c: Coincident(g93,g94)
    c: Coincident(g94,g95)
    c: Coincident(g95,g96)
    c: Coincident(g96,g97)
    c: Coincident(g97,g98)
    c: Coincident(g98,g87)
    c: Coincident(g99,g100)
    c: Coincident(g100,g101)
    c: Coincident(g101,g102)
    c: Coincident(g102,g103)
    c: Coincident(g103,g104)
    c: Coincident(g104,g105)
    c: Coincident(g105,g106)
    c: Coincident(g106,g99)
    c: Coincident(g107,g108)
    c: Coincident(g108,g109)
    c: Coincident(g109,g110)
    c: Coincident(g110,g111)
    c: Coincident(g111,g112)
    c: Coincident(g112,g113)
    c: Coincident(g113,g114)
    c: Coincident(g114,g115)
    c: Coincident(g115,g116)
    c: Coincident(g116,g117)
    c: Coincident(g117,g107)
    c: Coincident(g118,g119)
    c: Coincident(g119,g120)
    c: Coincident(g120,g118)
    c: Coincident(g121,g122)
    c: Coincident(g122,g123)
    c: Coincident(g123,g124)
    c: Coincident(g124,g125)
    c: Coincident(g125,g126)
    c: Coincident(g126,g127)
    c: Coincident(g127,g128)
    c: Coincident(g128,g129)
    c: Coincident(g129,g130)
    c: Coincident(g130,g131)
    c: Coincident(g131,g132)
    c: Coincident(g132,g121)
    c: Coincident(g133,g134)
    c: Coincident(g134,g135)
    c: Coincident(g135,g136)
    c: Coincident(g136,g137)
    c: Coincident(g137,g138)
    c: Coincident(g138,g139)
    c: Coincident(g139,g140)
    c: Coincident(g140,g133)
    c: Coincident(g141,g142)
    c: Coincident(g142,g143)
    c: Coincident(g143,g144)
    c: Coincident(g144,g145)
    c: Coincident(g145,g146)
    c: Coincident(g146,g147)
    c: Coincident(g147,g148)
    c: Coincident(g148,g149)
    c: Coincident(g149,g150)
    c: Coincident(g150,g151)
    c: Coincident(g151,g152)
    c: Coincident(g152,g153)
    c: Coincident(g153,g154)
    c: Coincident(g154,g155)
    c: Coincident(g155,g156)
    c: Coincident(g156,g157)
    c: Coincident(g157,g158)
    c: Coincident(g158,g159)
    c: Coincident(g159,g160)
    c: Coincident(g160,g161)
    c: Coincident(g161,g162)
    c: Coincident(g162,g163)
    c: Coincident(g163,g164)
    c: Coincident(g164,g165)
    c: Coincident(g165,g166)
    c: Coincident(g166,g167)
    c: Coincident(g167,g168)
    c: Coincident(g168,g169)
    c: Coincident(g169,g170)
    c: Coincident(g170,g141)
    c: Coincident(g171,g172)
    c: Coincident(g172,g173)
    c: Coincident(g173,g174)
    c: Coincident(g174,g175)
    c: Coincident(g175,g176)
    c: Coincident(g176,g177)
    c: Coincident(g177,g178)
    c: Coincident(g178,g179)
    c: Coincident(g179,g180)
    c: Coincident(g180,g181)
    c: Coincident(g181,g182)
    c: Coincident(g182,g171)
    c: Coincident(g183,g184)
    c: Coincident(g184,g185)
    c: Coincident(g185,g186)
    c: Coincident(g186,g187)
    c: Coincident(g187,g188)
    c: Coincident(g188,g189)
    c: Coincident(g189,g190)
    c: Coincident(g190,g183)
    c: Coincident(g191,g192)
    c: Coincident(g192,g193)
    c: Coincident(g193,g194)
    c: Coincident(g194,g195)
    c: Coincident(g195,g196)
    c: Coincident(g196,g197)
    c: Coincident(g197,g198)
    c: Coincident(g198,g199)
    c: Coincident(g199,g200)
    c: Coincident(g200,g201)
    c: Coincident(g201,g202)
    c: Coincident(g202,g203)
    c: Coincident(g203,g204)
    c: Coincident(g204,g205)
    c: Coincident(g205,g206)
    c: Coincident(g206,g207)
    c: Coincident(g207,g208)
    c: Coincident(g208,g209)
    c: Coincident(g209,g210)
    c: Coincident(g210,g211)
    c: Coincident(g211,g212)
    c: Coincident(g212,g191)
    c: Coincident(g213,g214)
    c: Coincident(g214,g215)
    c: Coincident(g215,g216)
    c: Coincident(g216,g217)
    c: Coincident(g217,g218)
    c: Coincident(g218,g219)
    c: Coincident(g219,g220)
    c: Coincident(g220,g221)
    c: Coincident(g221,g222)
    c: Coincident(g222,g223)
    c: Coincident(g223,g224)
    c: Coincident(g224,g213)
    c: Coincident(g225,g226)
    c: Coincident(g226,g227)
    c: Coincident(g227,g228)
    c: Coincident(g228,g229)
    c: Coincident(g229,g230)
    c: Coincident(g230,g231)
    c: Coincident(g231,g232)
    c: Coincident(g232,g225)
    c: Coincident(g233,g-1)
    c: Coincident(g234,g-1)
    c: Coincident(g235,g-1)
    c: Coincident(g236,g-1)
    c: Coincident(g237,g-1)
    c: Coincident(g238,g-1)
    c: Coincident(g239,g-1)
    c: Coincident(g240,g-1)
    c: Coincident(g241,g-1)
    c: Coincident(g242,g-1)
    c: Coincident(g243,g-1)
    c: Angle(g233,g-2) = 0.20944
    c: Angle(g234,g233) = 0.10472
    c: Angle(g235,g234) = 0.10472
    c: Angle(g236,g235) = 0.20944
    c: Angle(g237,g236) = 0.10472
    c: Angle(g238,g237) = 0.10472
    c: Angle(g239,g238) = 0.10472
    c: Angle(g240,g239) = 0.20944
    c: Angle(g241,g240) = 0.10472
    c: Angle(g242,g241) = 0.10472
    c: Angle(g243,g242) = 0.10472
    c: Coincident(g244,g-1)
    c: Radius(g244) = 16
    c: PointOnObject(g233,g244)
    c: PointOnObject(g234,g244)
    c: PointOnObject(g235,g244)
    c: PointOnObject(g236,g244)
    c: PointOnObject(g237,g244)
    c: PointOnObject(g238,g244)
    c: PointOnObject(g239,g244)
    c: PointOnObject(g240,g244)
    c: PointOnObject(g241,g244)
    c: PointOnObject(g242,g244)
    c: PointOnObject(g243,g244)
    c: Coincident(g245,g244)
    c: Coincident(g246,g244)
    c: Coincident(g247,g244)
    c: Coincident(g248,g244)
    c: Coincident(g249,g244)
    c: Coincident(g250,g244)
    c: Coincident(g251,g244)
    c: Coincident(g252,g244)
    c: Coincident(g253,g244)
    c: Coincident(g254,g244)
    c: Symmetric(g244,g245,g233)
    c: Symmetric(g245,g246,g234)
    c: Symmetric(g246,g247,g235)
    c: Symmetric(g247,g248,g236)
    c: Symmetric(g248,g249,g237)
    c: Symmetric(g249,g250,g238)
    c: Symmetric(g250,g251,g239)
    c: Symmetric(g251,g252,g240)
    c: Symmetric(g252,g253,g241)
    c: Symmetric(g253,g254,g242)
    c: Symmetric(g254,g336,g243)
    c: Coincident(g255,g336)
    c: Coincident(g255,g254)
    c: Coincident(g256,g253)
    c: Coincident(g256,g254)
    c: Coincident(g257,g252)
    c: Coincident(g257,g253)
    c: Coincident(g258,g252)
    c: Coincident(g258,g251)
    c: Coincident(g259,g250)
    c: Coincident(g259,g251)
    c: Coincident(g260,g250)
    c: Coincident(g260,g249)
    c: Coincident(g261,g248)
    c: Coincident(g261,g249)
    c: Coincident(g262,g247)
    c: Coincident(g262,g248)
    c: Coincident(g263,g246)
    c: Coincident(g263,g247)
    c: Coincident(g264,g245)
    c: Coincident(g264,g246)
    c: Coincident(g265,g244)
    c: Coincident(g265,g245)
    c: Distance(g265) = 0.3
    c: Equal(g265,g264)
    c: Equal(g264,g263)
    c: Equal(g263,g262)
    c: Equal(g262,g261)
    c: Equal(g261,g260)
    c: Equal(g260,g259)
    c: Equal(g259,g258)
    c: Equal(g258,g257)
    c: Equal(g257,g256)
    c: Equal(g256,g255)
    c: Tangent(g266,g267) = 1.5708
    c: Tangent(g267,g268) = 1.5708
    c: Tangent(g268,g269) = 1.5708
    c: Tangent(g269,g270) = 1.5708
    c: Symmetric(g267,g268,g271)
    c: Coincident(g270,g245)
    c: Coincident(g244,g266)
    c: Equal(g267,g269)
    c: Parallel(g233,g270)
    c: Radius(g269) = 0.05
    c: Symmetric(g266,g269,g233)
    c: Distance(g271,g233) = 1.2
    c: Coincident(g272,g244)
    c: PointOnObject(g271,g272)
    c: Tangent(g273,g274) = 1.5708
    c: Tangent(g274,g275) = 1.5708
    c: Tangent(g275,g276) = 1.5708
    c: Tangent(g276,g277) = 1.5708
    c: Equal(g274,g276)
    c: Equal(g269,g276) = 0.05
    c: Coincident(g273,g245)
    c: Coincident(g277,g246)
    c: PointOnObject(g278,g272)
    c: Symmetric(g274,g275,g234)
    c: Parallel(g277,g234)
    c: Symmetric(g274,g275,g278)
    c: Tangent(g279,g280) = 1.5708
    c: Tangent(g280,g281) = 1.5708
    c: Tangent(g281,g283) = 1.5708
    c: Tangent(g283,g284) = 1.5708
    c: Symmetric(g280,g281,g282)
    c: Coincident(g279,g246)
    c: Coincident(g284,g247)
    c: Parallel(g284,g235)
    c: PointOnObject(g282,g272)
    c: Radius(g280) = 0.05
    c: Equal(g283,g280)
    c: Symmetric(g283,g279,g235)
    c: Tangent(g285,g286) = 1.5708
    c: Tangent(g286,g287) = 1.5708
    c: Tangent(g287,g289) = 1.5708
    c: Tangent(g289,g290) = 1.5708
    c: Symmetric(g286,g287,g288)
    c: Equal(g286,g289)
    c: Equal(g269,g289) = 0.05
    c: Coincident(g247,g285)
    c: Coincident(g248,g290)
    c: Parallel(g290,g236)
    c: PointOnObject(g288,g272)
    c: Symmetric(g285,g289,g236)
    c: Tangent(g291,g292) = 1.5708
    c: Tangent(g292,g293) = 1.5708
    c: Tangent(g293,g295) = 1.5708
    c: Tangent(g295,g296) = 1.5708
    c: Symmetric(g292,g293,g294)
    c: Equal(g292,g295)
    c: Equal(g269,g295) = 0.05
    c: Coincident(g291,g248)
    c: Coincident(g249,g296)
    c: PointOnObject(g294,g272)
    c: Parallel(g237,g296)
    c: Symmetric(g291,g295,g237)
    c: Tangent(g297,g298) = 1.5708
    c: Tangent(g298,g299) = 1.5708
    c: Tangent(g299,g301) = 1.5708
    c: Tangent(g301,g302) = 1.5708
    c: Symmetric(g298,g299,g300)
    c: Equal(g298,g301)
    c: Equal(g269,g301) = 0.05
    c: Coincident(g297,g249)
    c: Coincident(g302,g250)
    c: PointOnObject(g300,g272)
    c: Parallel(g302,g238)
    c: Symmetric(g298,g299,g238)
    c: Tangent(g303,g304) = 1.5708
    c: Tangent(g304,g305) = 1.5708
    c: Tangent(g305,g307) = 1.5708
    c: Tangent(g307,g308) = 1.5708
    c: Symmetric(g304,g305,g306)
    c: Equal(g304,g307)
    c: Equal(g269,g307) = 0.05
    c: Coincident(g303,g250)
    c: Coincident(g308,g251)
    c: PointOnObject(g306,g272)
    c: Parallel(g308,g239)
    c: Symmetric(g307,g303,g239)
    c: Tangent(g309,g310) = 1.5708
    c: Tangent(g310,g311) = 1.5708
    c: Tangent(g311,g313) = 1.5708
    c: Tangent(g313,g314) = 1.5708
    c: Symmetric(g310,g311,g312)
    c: Equal(g310,g313)
    c: Equal(g269,g313) = 0.05
    c: PointOnObject(g312,g272)
    c: Coincident(g309,g251)
    c: Coincident(g314,g252)
    c: Parallel(g314,g240)
    c: Symmetric(g309,g313,g240)
    c: Tangent(g315,g316) = 1.5708
    c: Tangent(g316,g317) = 1.5708
    c: Tangent(g317,g319) = 1.5708
    c: Tangent(g319,g320) = 1.5708
    c: Symmetric(g316,g317,g318)
    c: Equal(g316,g319)
    c: Equal(g269,g319) = 0.05
    c: PointOnObject(g318,g272)
    c: Coincident(g315,g252)
    c: Coincident(g253,g320)
    c: Parallel(g320,g241)
    c: Symmetric(g315,g319,g241)
    c: Tangent(g321,g322) = 1.5708
    c: Tangent(g322,g323) = 1.5708
    c: Tangent(g323,g325) = 1.5708
    c: Tangent(g325,g326) = 1.5708
    c: Symmetric(g322,g323,g324)
    c: Equal(g322,g325)
    c: Equal(g269,g325) = 0.05
    c: Coincident(g253,g321)
    c: PointOnObject(g324,g272)
    c: Coincident(g254,g326)
    c: Parallel(g242,g326)
    c: Symmetric(g321,g325,g242)
    c: Tangent(g327,g328) = 1.5708
    c: Tangent(g328,g329) = 1.5708
    c: Tangent(g329,g331) = 1.5708
    c: Tangent(g331,g332) = 1.5708
    c: Symmetric(g328,g329,g330)
    c: Equal(g328,g331)
    c: Equal(g269,g331) = 0.05
    c: PointOnObject(g330,g272)
    c: Coincident(g327,g254)
    c: Coincident(g332,g336)
    c: Parallel(g332,g243)
    c: Symmetric(g327,g331,g243)
    c: PointOnObject(g333,g-2)
    c: DistanceY(g333) = 17.6
    c: Radius(g333) = 0.9
    c: Coincident(g244,g334)
    c: Coincident(g336,g335)
    c: Coincident(g244,g336)
    c: Symmetric(g335,g244,g-2)
    c: Symmetric(g335,g334,g-2)
    c: Coincident(g337,g244)
    c: Coincident(g337,g334)
    c: Coincident(g337,g335)
    c: Radius(g337) = 19.2
    c: Coincident(g338,g271)
    c: Parallel(g233,g338)
    c: Coincident(g334,g338)
    c: Coincident(g339,g244)
    c: Coincident(g339,g244)
    c: Angle(g339,g-2) = 0.0523599
FEATURE [Part::Extrusion] Extrude027
  Base = -> Sketch101
  Dir = (0,0,1)
  DirMode = 2
  FaceMakerClass = Part::FaceMakerBullseye
  LengthFwd = 0.35
  LengthRev = 0
  Reversed = true
  Solid = true
  Symmetric = false
FEATURE [Part::Cut] Cut023  label="Bez17_Pers184"
  Base = -> Array030
  Tool = -> Extrude027
FEATURE [Sketcher::SketchObject] Sketch103
  MapMode = 5
  Placement = pos=(0,0,0) rot=(1,0,0;1.5708rad)
  sketch-geometry (16):
    g0: LineSegment StartX=15.6 StartY=3.3 StartZ=0 EndX=15.6 EndY=4.2 EndZ=0
    g1: LineSegment StartX=17.75 StartY=0 StartZ=0 EndX=16.75 EndY=0 EndZ=0
    g2: LineSegment StartX=16.75 StartY=3.3 StartZ=0 EndX=15.6 EndY=3.3 EndZ=0
    g3: LineSegment StartX=16.75 StartY=0 StartZ=0 EndX=16.75 EndY=0.5 EndZ=0
    g4: LineSegment StartX=16.75 StartY=0.5 StartZ=0 EndX=17.05 EndY=0.5 EndZ=0
    g5: LineSegment StartX=17.05 StartY=0.5 StartZ=0 EndX=17.05 EndY=0.75 EndZ=0
    g6: LineSegment StartX=17.05 StartY=0.75 StartZ=0 EndX=16.75 EndY=0.75 EndZ=0
    g7: LineSegment StartX=16.75 StartY=0.75 StartZ=0 EndX=16.75 EndY=3.3 EndZ=0
    g8: LineSegment StartX=17.75 StartY=0 StartZ=0 EndX=19.5 EndY=1.46842 EndZ=0
    g9: LineSegment StartX=19.5 StartY=1.46842 StartZ=0 EndX=19.5 EndY=3.36842 EndZ=0
    g10: LineSegment StartX=18.75 StartY=3.49342 StartZ=0 EndX=15.85 EndY=4.1 EndZ=0
    g11: LineSegment StartX=15.85 StartY=4.1 StartZ=0 EndX=15.85 EndY=4.2 EndZ=0
    g12: LineSegment StartX=15.85 StartY=4.2 StartZ=0 EndX=15.6 EndY=4.2 EndZ=0
    g13: LineSegment StartX=18.75 StartY=3.49342 StartZ=0 EndX=18.75 EndY=3.46842 EndZ=0
    g14: LineSegment StartX=18.75 StartY=3.46842 StartZ=0 EndX=19.4 EndY=3.46842 EndZ=0
    g15: ArcOfCircle CenterX=19.4 CenterY=3.36842 CenterZ=0 NormalX=0 NormalY=0 NormalZ=1 AngleXU=0 Radius=0.1 StartAngle=-1.8e-15 EndAngle=1.5708
  constraints (51):
    c: Vertical(g0)
    c: Horizontal(g2)
    c: Horizontal(g1)
    c: Coincident(g2,g0)
    c: Coincident(g1,g3)
    c: Vertical(g3)
    c: Coincident(g3,g4)
    c: Horizontal(g4)
    c: Coincident(g4,g5)
    c: Coincident(g5,g6)
    c: Coincident(g6,g7)
    c: Coincident(g7,g2)
    c: Vertical(g7)
    c: Vertical(g5)
    c: Horizontal(g6)
    c: Vertical(g6,g3)
    c: PointOnObject(g1,g-1)
    c: DistanceY(g3,g3) = 0.5
    c: DistanceY(g5,g5) = 0.25
    c: DistanceX(g6,g6) = 0.3
    c: DistanceX(g0) = 15.6
    c: DistanceX(g1,g1) = 1
    c: DistanceX(g6) = 16.75
    c: DistanceY(g0,g0) = 0.9
    c: DistanceY(g0) = 4.2
    c: Coincident(g1,g8)
    c: Coincident(g8,g9)
    c: Vertical(g9)
    c: Coincident(g10,g11)
    c: Coincident(g11,g12)
    c: Horizontal(g12)
    c: Vertical(g11)
    c: Coincident(g10,g13)
    c: Coincident(g13,g14)
    c: Horizontal(g14)
    c: Vertical(g13)
    c: DistanceY(g11,g11) = 0.1
    c: Coincident(g12,g0)
    c: DistanceX(g12,g12) = 0.25
    c: DistanceY(g13,g13) = 0.025
    c: Angle(g8) = 0.698132
    c: Tangent(g14,g15) = 1.5708
    c: Tangent(g9,g15) = -1.5708
    c: Radius(g15) = 0.1
    c: DistanceX(g9) = 19.5
    c: DistanceX(g13,g9) = 0.75
    c: DistanceY(g8,g14) = 2
    c: Angle(g0,g10) = 1.3646
    c: DistanceX(g10,g10) = 2.9
    c: DistanceX(g10) = 15.85
    c: DistanceY(g1,g14) = 3.46842
FEATURE [Part::Revolution] Revolve019
  Angle = 90
  Axis = (0,0,1)
  Base = (0,0,0)
  FaceMakerClass = Part::FaceMakerBullseye
  Solid = true
  Source = -> Sketch103
  Symmetric = false
FEATURE [Sketcher::SketchObject] Sketch105
  MapMode = 5
  Placement = pos=(0,0,3.5) rot=(0,0,1;0rad)
  sketch-geometry (5):
    g0: ArcOfCircle CenterX=46.4231 CenterY=12.439 CenterZ=0 NormalX=0 NormalY=0 NormalZ=1 AngleXU=0 Radius=29.2046 StartAngle=3.22521 EndAngle=3.58158
    g1: LineSegment [constr] StartX=17.3205 StartY=10 StartZ=0 EndX=0 EndY=0 EndZ=0
    g2: LineSegment StartX=17.3205 StartY=10 StartZ=0 EndX=18.8512 EndY=10.5305 EndZ=0
    g3: LineSegment StartX=18.8512 StartY=10.5305 StartZ=0 EndX=22.2329 EndY=0.773906 EndZ=0
    g4: LineSegment StartX=22.2329 StartY=0.773906 StartZ=0 EndX=20 EndY=1e-16 EndZ=0
  constraints (12):
    c: PointOnObject(g0,g-1)
    c: Coincident(g1,g0)
    c: Coincident(g1,g-1)
    c: Distance(g1) = 20
    c: Angle(g-1,g1) = 0.523599
    c: DistanceX(g-1,g0) = 20
    c: Coincident(g2,g3)
    c: Coincident(g3,g4)
    c: Coincident(g4,g0)
    c: Coincident(g2,g0)
    c: Perpendicular(g3,g2)
    c: Perpendicular(g3,g4)
FEATURE [Part::Extrusion] Extrude028
  Base = -> Sketch105
  Dir = (-1,0,2)
  DirMode = 0
  FaceMakerClass = Part::FaceMakerBullseye
  LengthFwd = 10
  LengthRev = 0
  Reversed = true
  Solid = true
  Symmetric = false
FEATURE [Part::FeaturePython] Array034  # Draft array (typed FeaturePython)
  Angle = 60
  ArrayType = 1
  Axis = (0,0,1)
  Base = -> Extrude028
  Center = (0,0,0)
  Fuse = false
  IntervalAxis = (0,0,0)
  IntervalX = (1,0,0)
  IntervalY = (0,1,0)
  IntervalZ = (0,0,1)
  NumberCircles = 2
  NumberPolar = 3
  NumberX = 1
  NumberY = 1
  NumberZ = 1
  RadialDistance = 1
  Symmetry = 1
  TangentialDistance = 1
FEATURE [Part::Cut] Cut025
  Base = -> Revolve019
  Tool = -> Array034
FEATURE [Part::FeaturePython] Array035  label="Bezel18_Mer2"  # Draft array (typed FeaturePython)
  Angle = 360
  ArrayType = 1
  Axis = (0,0,1)
  Base = -> Cut025
  Center = (0,0,0)
  Fuse = true
  IntervalAxis = (0,0,0)
  IntervalX = (1,0,0)
  IntervalY = (0,1,0)
  IntervalZ = (0,0,1)
  NumberCircles = 2
  NumberPolar = 4
  NumberX = 1
  NumberY = 1
  NumberZ = 1
  RadialDistance = 1
  Symmetry = 1
  TangentialDistance = 1
note: 9 file-system paths scrubbed to <path> (originals preserved in the JSON sidecar)
